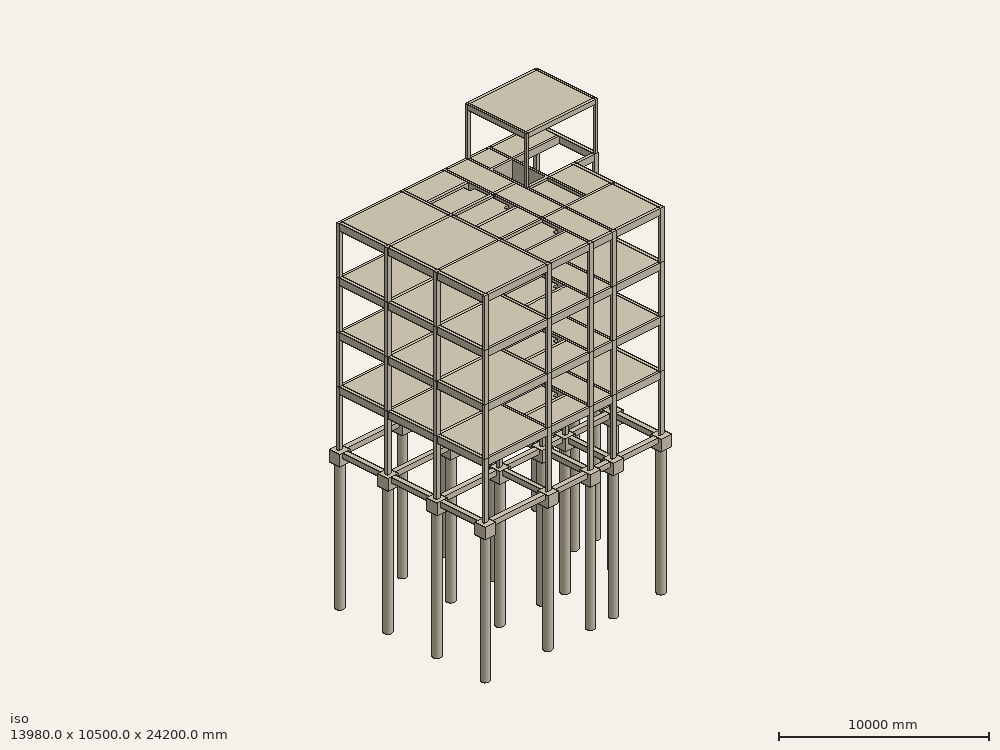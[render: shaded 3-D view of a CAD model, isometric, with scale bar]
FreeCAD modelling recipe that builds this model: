
FCSTD DOCUMENT  (FreeCAD 0.19R23074 (Git))
Label: 2021-01-14 Piloto estructural
License: All rights reserved
objects: Part::FeaturePython×395, Part::Part2DObjectPython×42, App::GeometryPython×29, TechDraw::DrawViewDimension×16, App::FeaturePython×11, App::DocumentObjectGroup×5, TechDraw::DrawSVGTemplate×5, TechDraw::DrawPage×5, TechDraw::DrawViewPart×4, TechDraw::DrawViewAnnotation×2, TechDraw::DrawViewSection×2, Spreadsheet::Sheet×1, App::MaterialObjectPython×1, App::DocumentObjectGroupPython×1, Sketcher::SketchObject×1, TechDraw::DrawViewArch×1
note: 470 computed .brp shape members not serialized (recipe doc carries the construction recipe); baked Part::Feature solids carry a one-line shape summary decoded from their .brp

FEATURE [Part::FeaturePython] Axis  label="Vertical"  # WARN: FeaturePython — macro-defined, semantics opaque (R4)
  Angles = [0,0,0,0,0,0,0]
  Distances = [1930,4230,2850,1550,1450,1770,1430]
  Length = 11000
  Placement = pos=(0,-500,0) rot=(0,0,1;0rad)
FEATURE [Part::FeaturePython] Axis002  label="Horizontal larga"  # WARN: FeaturePython — macro-defined, semantics opaque (R4)
  Angles = [0,0,0,0,0,0]
  Distances = [100,3250,2620,670,1730,1530]
  Length = 32000
  Placement = pos=(31000,1.077e-12,0) rot=(0,0,1;1.5708rad)
FEATURE [Part::Part2DObjectPython] Rectangle001  label="Lote"  # Draft 2D object (typed FeaturePython)
  Area = 0
  ChamferSize = 0
  Columns = 1
  FilletRadius = 0
  Height = 10000
  Length = 30000
  MakeFace = false
  Rows = 1
FEATURE [Part::Part2DObjectPython] Rectangle002  # Draft 2D object (typed FeaturePython)
  Area = 0
  ChamferSize = 0
  Columns = 1
  FilletRadius = 0
  Height = 700
  Length = 700
  MakeFace = false
  Placement = pos=(14860,9550,0) rot=(0,0,1;0rad)
  Rows = 1
  expr: Height = <<Estructura>>.CabAncho
  expr: Length = <<Estructura>>.CabAncho
FEATURE [Part::Part2DObjectPython] Circle  # Draft 2D object (typed FeaturePython)
  Area = 0
  FirstAngle = 0
  LastAngle = 0
  MakeFace = false
  Placement = pos=(15210,9900,0) rot=(0,0,1;0rad)
  Radius = 250
  expr: Radius = <<Estructura>>.PilRad
FEATURE [Part::FeaturePython] Beam001  # Arch/BIM 7 (typed FeaturePython)
  Chamfer = 0
  DentHeight = 0
  DentLength = 0
  Height = 300
  HorizontalArea = 1059000
  IfcData = attributes={"GlobalId": {"name": "GlobalId", "type": "IfcGloballyUniqueId", "is_enum": false, "enum_values": []}, "Description": {"... (+475 chars omitted),+1 more (map truncated)
  IfcType = 7
  Length = 3530
  MoveBase = false
  MoveWithHost = false
  PerimeterLength = 7660
  Placement = pos=(2280,6490,-800) rot=(0,0,1;0rad)
  PredefinedType = 0
  VerticalArea = 2298000
  Width = 300
FEATURE [Part::FeaturePython] Structure041  label="Beam002"  # Arch/BIM 7 (typed FeaturePython)
  FaceMaker = 0
  Height = 300
  HorizontalArea = 768000
  IfcData = attributes={"GlobalId": {"name": "GlobalId", "type": "IfcGloballyUniqueId", "is_enum": false, "enum_values": []}, "Description": {"... (+475 chars omitted),+1 more (map truncated)
  IfcType = 7
  Length = 2560
  MoveBase = false
  MoveWithHost = false
  Nodes = (2) [(1.2326e-31,-1.51582e-15,5.55112e-16),(2560,-1.51582e-15,5.55112e-16)]
  NodesOffset = 0
  Normal = (0,0,0)
  PerimeterLength = 5720
  Placement = pos=(1930,9550,-650) rot=(0,0,-1;1.5708rad)
  PredefinedType = 0
  VerticalArea = 1.716e+06
  Width = 300
  expr: Height = <<Estructura>>.VRAlto
  expr: Width = <<Estructura>>.VRAncho
FEATURE [Part::FeaturePython] Structure042  label="Beam003"  # Arch/BIM 7 (typed FeaturePython)
  FaceMaker = 0
  Height = 300
  HorizontalArea = 777000
  IfcData = attributes={"GlobalId": {"name": "GlobalId", "type": "IfcGloballyUniqueId", "is_enum": false, "enum_values": []}, "Description": {"... (+475 chars omitted),+1 more (map truncated)
  IfcType = 7
  Length = 2590
  MoveBase = false
  MoveWithHost = false
  Nodes = (2) [(1.2326e-31,-1.51582e-15,5.55112e-16),(2590,-1.51582e-15,5.55112e-16)]
  NodesOffset = 0
  Normal = (0,0,0)
  PerimeterLength = 5780
  Placement = pos=(1930,6290,-650) rot=(0,0,-1;1.5708rad)
  PredefinedType = 0
  VerticalArea = 1.734e+06
  Width = 300
FEATURE [Part::FeaturePython] Structure043  label="Beam004"  # Arch/BIM 7 (typed FeaturePython)
  FaceMaker = 0
  Height = 300
  HorizontalArea = 765000
  IfcData = attributes={"GlobalId": {"name": "GlobalId", "type": "IfcGloballyUniqueId", "is_enum": false, "enum_values": []}, "Description": {"... (+475 chars omitted),+1 more (map truncated)
  IfcType = 7
  Length = 2550
  MoveBase = false
  MoveWithHost = false
  Nodes = (2) [(1.2326e-31,-1.51582e-15,5.55112e-16),(2550,-1.51582e-15,5.55112e-16)]
  NodesOffset = 0
  Normal = (0,0,0)
  PerimeterLength = 5700
  Placement = pos=(1930,3000,-650) rot=(0,0,-1;1.5708rad)
  PredefinedType = 0
  VerticalArea = 1.71e+06
  Width = 300
FEATURE [Part::FeaturePython] Structure044  label="Beam005"  # Arch/BIM 7 (typed FeaturePython)
  FaceMaker = 0
  Height = 300
  HorizontalArea = 768000
  IfcData = attributes={"GlobalId": {"name": "GlobalId", "type": "IfcGloballyUniqueId", "is_enum": false, "enum_values": []}, "Description": {"... (+475 chars omitted),+1 more (map truncated)
  IfcType = 7
  Length = 2560
  MoveBase = false
  MoveWithHost = false
  Nodes = (2) [(1.2326e-31,-1.51582e-15,5.55112e-16),(2560,-1.51582e-15,5.55112e-16)]
  NodesOffset = 0
  Normal = (0,0,0)
  PerimeterLength = 5720
  Placement = pos=(6160.36,9550,-650) rot=(0,0,-1;1.5708rad)
  PredefinedType = 0
  VerticalArea = 1.716e+06
  Width = 300
FEATURE [Part::FeaturePython] Structure045  label="Beam006"  # Arch/BIM 7 (typed FeaturePython)
  FaceMaker = 0
  Height = 300
  HorizontalArea = 777000
  IfcData = attributes={"GlobalId": {"name": "GlobalId", "type": "IfcGloballyUniqueId", "is_enum": false, "enum_values": []}, "Description": {"... (+475 chars omitted),+1 more (map truncated)
  IfcType = 7
  Length = 2590
  MoveBase = false
  MoveWithHost = false
  Nodes = (2) [(1.2326e-31,-1.51582e-15,5.55112e-16),(2590,-1.51582e-15,5.55112e-16)]
  NodesOffset = 0
  Normal = (0,0,0)
  PerimeterLength = 5780
  Placement = pos=(6160.36,6290,-650) rot=(0,0,-1;1.5708rad)
  PredefinedType = 0
  VerticalArea = 1.734e+06
  Width = 300
FEATURE [Part::FeaturePython] Structure046  label="Beam007"  # Arch/BIM 7 (typed FeaturePython)
  FaceMaker = 0
  Height = 300
  HorizontalArea = 765000
  IfcData = attributes={"GlobalId": {"name": "GlobalId", "type": "IfcGloballyUniqueId", "is_enum": false, "enum_values": []}, "Description": {"... (+475 chars omitted),+1 more (map truncated)
  IfcType = 7
  Length = 2550
  MoveBase = false
  MoveWithHost = false
  Nodes = (2) [(1.2326e-31,-1.51582e-15,5.55112e-16),(2550,-1.51582e-15,5.55112e-16)]
  NodesOffset = 0
  Normal = (0,0,0)
  PerimeterLength = 5700
  Placement = pos=(6160.36,3000,-650) rot=(0,0,-1;1.5708rad)
  PredefinedType = 0
  VerticalArea = 1.71e+06
  Width = 300
FEATURE [Part::FeaturePython] Structure048  label="Beam009"  # Arch/BIM 7 (typed FeaturePython)
  FaceMaker = 0
  Height = 300
  HorizontalArea = 777000
  IfcData = attributes={"GlobalId": {"name": "GlobalId", "type": "IfcGloballyUniqueId", "is_enum": false, "enum_values": []}, "Description": {"... (+475 chars omitted),+1 more (map truncated)
  IfcType = 7
  Length = 2590
  MoveBase = false
  MoveWithHost = false
  Nodes = (2) [(1.2326e-31,-1.51582e-15,5.55112e-16),(2590,-1.51582e-15,5.55112e-16)]
  NodesOffset = 0
  Normal = (0,0,0)
  PerimeterLength = 5780
  Placement = pos=(9010.18,6290,-650) rot=(0,0,-1;1.5708rad)
  PredefinedType = 0
  VerticalArea = 1.734e+06
  Width = 300
FEATURE [Part::FeaturePython] Structure049  label="Beam010"  # Arch/BIM 7 (typed FeaturePython)
  FaceMaker = 0
  Height = 300
  HorizontalArea = 765000
  IfcData = attributes={"GlobalId": {"name": "GlobalId", "type": "IfcGloballyUniqueId", "is_enum": false, "enum_values": []}, "Description": {"... (+475 chars omitted),+1 more (map truncated)
  IfcType = 7
  Length = 2550
  MoveBase = false
  MoveWithHost = false
  Nodes = (2) [(1.2326e-31,-1.51582e-15,5.55112e-16),(2550,-1.51582e-15,5.55112e-16)]
  NodesOffset = 0
  Normal = (0,0,0)
  PerimeterLength = 5700
  Placement = pos=(9010.18,3000,-650) rot=(0,0,-1;1.5708rad)
  PredefinedType = 0
  VerticalArea = 1.71e+06
  Width = 300
FEATURE [Part::FeaturePython] Structure053  label="Beam014"  # Arch/BIM 7 (typed FeaturePython)
  FaceMaker = 0
  Height = 300
  HorizontalArea = 765000
  IfcData = attributes={"GlobalId": {"name": "GlobalId", "type": "IfcGloballyUniqueId", "is_enum": false, "enum_values": []}, "Description": {"... (+475 chars omitted),+1 more (map truncated)
  IfcType = 7
  Length = 2550
  MoveBase = false
  MoveWithHost = false
  Nodes = (2) [(1.2326e-31,-1.51582e-15,5.55112e-16),(2550,-1.51582e-15,5.55112e-16)]
  NodesOffset = 0
  Normal = (0,0,0)
  PerimeterLength = 5700
  Placement = pos=(13778.3,3000,-650) rot=(0,0,-1;1.5708rad)
  PredefinedType = 0
  VerticalArea = 1.71e+06
  Width = 300
FEATURE [Part::FeaturePython] Structure056  label="Beam017"  # Arch/BIM 7 (typed FeaturePython)
  FaceMaker = 0
  Height = 300
  HorizontalArea = 765000
  IfcData = attributes={"GlobalId": {"name": "GlobalId", "type": "IfcGloballyUniqueId", "is_enum": false, "enum_values": []}, "Description": {"... (+475 chars omitted),+1 more (map truncated)
  IfcType = 7
  Length = 2550
  MoveBase = false
  MoveWithHost = false
  Nodes = (2) [(1.2326e-31,-1.51582e-15,5.55112e-16),(2550,-1.51582e-15,5.55112e-16)]
  NodesOffset = 0
  Normal = (0,0,0)
  PerimeterLength = 5700
  Placement = pos=(10560,3000,-650) rot=(0,0,-1;1.5708rad)
  PredefinedType = 0
  VerticalArea = 1.71e+06
  Width = 300
FEATURE [Part::FeaturePython] Structure059  label="Beam020"  # Arch/BIM 7 (typed FeaturePython)
  FaceMaker = 0
  Height = 300
  HorizontalArea = 645000
  IfcData = attributes={"GlobalId": {"name": "GlobalId", "type": "IfcGloballyUniqueId", "is_enum": false, "enum_values": []}, "Description": {"... (+475 chars omitted),+1 more (map truncated)
  IfcType = 7
  Length = 2150
  MoveBase = false
  MoveWithHost = false
  Nodes = (2) [(1.2326e-31,-1.51582e-15,5.55112e-16),(2150,-1.51582e-15,5.55112e-16)]
  NodesOffset = 0
  Normal = (0,0,0)
  PerimeterLength = 4900
  Placement = pos=(6510,9900,-650) rot=(0,0,1;0rad)
  PredefinedType = 0
  VerticalArea = 1.47e+06
  Width = 300
FEATURE [Part::FeaturePython] Structure060  label="Beam021"  # Arch/BIM 7 (typed FeaturePython)
  FaceMaker = 0
  Height = 300
  HorizontalArea = 690000
  IfcData = attributes={"GlobalId": {"name": "GlobalId", "type": "IfcGloballyUniqueId", "is_enum": false, "enum_values": []}, "Description": {"... (+475 chars omitted),+1 more (map truncated)
  IfcType = 7
  Length = 2300
  MoveBase = false
  MoveWithHost = false
  Nodes = (2) [(1.2326e-31,-1.51582e-15,5.55112e-16),(2300,-1.51582e-15,5.55112e-16)]
  NodesOffset = 0
  Normal = (0,0,0)
  PerimeterLength = 5200
  Placement = pos=(9360,9900,-650) rot=(0,0,1;0rad)
  PredefinedType = 0
  VerticalArea = 1.56e+06
  Width = 300
FEATURE [Part::FeaturePython] Structure061  label="Beam022"  # Arch/BIM 7 (typed FeaturePython)
  FaceMaker = 0
  Height = 300
  HorizontalArea = 750000
  IfcData = attributes={"GlobalId": {"name": "GlobalId", "type": "IfcGloballyUniqueId", "is_enum": false, "enum_values": []}, "Description": {"... (+475 chars omitted),+1 more (map truncated)
  IfcType = 7
  Length = 2500
  MoveBase = false
  MoveWithHost = false
  Nodes = (2) [(1.2326e-31,-1.51582e-15,5.55112e-16),(2500,-1.51582e-15,5.55112e-16)]
  NodesOffset = 0
  Normal = (0,0,0)
  PerimeterLength = 5600
  Placement = pos=(12360,9900,-650) rot=(0,0,1;0rad)
  PredefinedType = 0
  VerticalArea = 1680000
  Width = 300
FEATURE [Part::FeaturePython] Structure064  label="Beam025"  # Arch/BIM 7 (typed FeaturePython)
  FaceMaker = 0
  Height = 300
  HorizontalArea = 645000
  IfcData = attributes={"GlobalId": {"name": "GlobalId", "type": "IfcGloballyUniqueId", "is_enum": false, "enum_values": []}, "Description": {"... (+475 chars omitted),+1 more (map truncated)
  IfcType = 7
  Length = 2150
  MoveBase = false
  MoveWithHost = false
  Nodes = (2) [(1.2326e-31,-1.51582e-15,5.55112e-16),(2150,-1.51582e-15,5.55112e-16)]
  NodesOffset = 0
  Normal = (0,0,0)
  PerimeterLength = 4900
  Placement = pos=(6510,6640,-650) rot=(0,0,1;0rad)
  PredefinedType = 0
  VerticalArea = 1.47e+06
  Width = 300
FEATURE [Part::FeaturePython] Structure065  label="Beam026"  # Arch/BIM 7 (typed FeaturePython)
  FaceMaker = 0
  Height = 300
  HorizontalArea = 768000
  IfcData = attributes={"GlobalId": {"name": "GlobalId", "type": "IfcGloballyUniqueId", "is_enum": false, "enum_values": []}, "Description": {"... (+475 chars omitted),+1 more (map truncated)
  IfcType = 7
  Length = 2560
  MoveBase = false
  MoveWithHost = false
  Nodes = (2) [(1.2326e-31,-1.51582e-15,5.55112e-16),(2560,-1.51582e-15,5.55112e-16)]
  NodesOffset = 0
  Normal = (0,0,0)
  PerimeterLength = 5720
  Placement = pos=(9010,6990,-650) rot=(0,0,1;1.5708rad)
  PredefinedType = 0
  VerticalArea = 1.716e+06
  Width = 300
FEATURE [Part::FeaturePython] Structure066  label="Beam027"  # Arch/BIM 7 (typed FeaturePython)
  FaceMaker = 0
  Height = 300
  HorizontalArea = 1.059e+06
  IfcData = attributes={"GlobalId": {"name": "GlobalId", "type": "IfcGloballyUniqueId", "is_enum": false, "enum_values": []}, "Description": {"... (+475 chars omitted),+1 more (map truncated)
  IfcType = 7
  Length = 3530
  MoveBase = false
  MoveWithHost = false
  Nodes = (2) [(1.2326e-31,-1.51582e-15,5.55112e-16),(3530,-1.51582e-15,5.55112e-16)]
  NodesOffset = 0
  Normal = (0,0,0)
  PerimeterLength = 7660
  Placement = pos=(2280,3350,-650) rot=(0,0,1;0rad)
  PredefinedType = 0
  VerticalArea = 2.298e+06
  Width = 300
FEATURE [Part::FeaturePython] Structure067  label="Beam028"  # Arch/BIM 7 (typed FeaturePython)
  FaceMaker = 0
  Height = 300
  HorizontalArea = 645000
  IfcData = attributes={"GlobalId": {"name": "GlobalId", "type": "IfcGloballyUniqueId", "is_enum": false, "enum_values": []}, "Description": {"... (+475 chars omitted),+1 more (map truncated)
  IfcType = 7
  Length = 2150
  MoveBase = false
  MoveWithHost = false
  Nodes = (2) [(1.2326e-31,-1.51582e-15,5.55112e-16),(2150,-1.51582e-15,5.55112e-16)]
  NodesOffset = 0
  Normal = (0,0,0)
  PerimeterLength = 4900
  Placement = pos=(6510,3350,-650) rot=(0,0,1;0rad)
  PredefinedType = 0
  VerticalArea = 1.47e+06
  Width = 300
FEATURE [Part::FeaturePython] Structure068  label="Beam029"  # Arch/BIM 7 (typed FeaturePython)
  FaceMaker = 0
  Height = 300
  HorizontalArea = 1.059e+06
  IfcData = attributes={"GlobalId": {"name": "GlobalId", "type": "IfcGloballyUniqueId", "is_enum": false, "enum_values": []}, "Description": {"... (+475 chars omitted),+1 more (map truncated)
  IfcType = 7
  Length = 3530
  MoveBase = false
  MoveWithHost = false
  Nodes = (2) [(1.2326e-31,-1.51582e-15,5.55112e-16),(3530,-1.51582e-15,5.55112e-16)]
  NodesOffset = 0
  Normal = (0,0,0)
  PerimeterLength = 7660
  Placement = pos=(2280,100,-650) rot=(0,0,1;0rad)
  PredefinedType = 0
  VerticalArea = 2.298e+06
  Width = 300
FEATURE [Part::FeaturePython] Structure069  label="Beam030"  # Arch/BIM 7 (typed FeaturePython)
  FaceMaker = 0
  Height = 300
  HorizontalArea = 645000
  IfcData = attributes={"GlobalId": {"name": "GlobalId", "type": "IfcGloballyUniqueId", "is_enum": false, "enum_values": []}, "Description": {"... (+475 chars omitted),+1 more (map truncated)
  IfcType = 7
  Length = 2150
  MoveBase = false
  MoveWithHost = false
  Nodes = (2) [(1.2326e-31,-1.51582e-15,5.55112e-16),(2150,-1.51582e-15,5.55112e-16)]
  NodesOffset = 0
  Normal = (0,0,0)
  PerimeterLength = 4900
  Placement = pos=(6510,100,-650) rot=(0,0,1;0rad)
  PredefinedType = 0
  VerticalArea = 1.47e+06
  Width = 300
FEATURE [Part::FeaturePython] Structure070  label="Beam031"  # Arch/BIM 7 (typed FeaturePython)
  FaceMaker = 0
  Height = 300
  HorizontalArea = 255000
  IfcData = attributes={"GlobalId": {"name": "GlobalId", "type": "IfcGloballyUniqueId", "is_enum": false, "enum_values": []}, "Description": {"... (+475 chars omitted),+1 more (map truncated)
  IfcType = 7
  Length = 850
  MoveBase = false
  MoveWithHost = false
  Nodes = (2) [(1.2326e-31,-1.51582e-15,5.55112e-16),(850,-1.51582e-15,5.55112e-16)]
  NodesOffset = 0
  Normal = (0,0,0)
  PerimeterLength = 2300
  Placement = pos=(9360,100,-650) rot=(0,0,1;0rad)
  PredefinedType = 0
  VerticalArea = 690000
  Width = 300
FEATURE [Part::FeaturePython] Structure071  label="Beam032"  # Arch/BIM 7 (typed FeaturePython)
  FaceMaker = 0
  Height = 300
  HorizontalArea = 756000
  IfcData = attributes={"GlobalId": {"name": "GlobalId", "type": "IfcGloballyUniqueId", "is_enum": false, "enum_values": []}, "Description": {"... (+475 chars omitted),+1 more (map truncated)
  IfcType = 7
  Length = 2520
  MoveBase = false
  MoveWithHost = false
  Nodes = (2) [(1.2326e-31,-1.51582e-15,5.55112e-16),(2520,-1.51582e-15,5.55112e-16)]
  NodesOffset = 0
  Normal = (0,0,0)
  PerimeterLength = 5640
  Placement = pos=(10910,100,-650) rot=(0,0,1;0rad)
  PredefinedType = 0
  VerticalArea = 1.692e+06
  Width = 300
FEATURE [Part::FeaturePython] Structure072  label="Beam033"  # Arch/BIM 7 (typed FeaturePython)
  FaceMaker = 0
  Height = 300
  HorizontalArea = 255000
  IfcData = attributes={"GlobalId": {"name": "GlobalId", "type": "IfcGloballyUniqueId", "is_enum": false, "enum_values": []}, "Description": {"... (+475 chars omitted),+1 more (map truncated)
  IfcType = 7
  Length = 850
  MoveBase = false
  MoveWithHost = false
  Nodes = (2) [(1.2326e-31,-1.51582e-15,5.55112e-16),(850,-1.51582e-15,5.55112e-16)]
  NodesOffset = 0
  Normal = (0,0,0)
  PerimeterLength = 2300
  Placement = pos=(9360,3350,-650) rot=(0,0,1;0rad)
  PredefinedType = 0
  VerticalArea = 690000
  Width = 300
FEATURE [Part::FeaturePython] Structure073  label="Beam034"  # Arch/BIM 7 (typed FeaturePython)
  FaceMaker = 0
  Height = 300
  HorizontalArea = 756000
  IfcData = attributes={"GlobalId": {"name": "GlobalId", "type": "IfcGloballyUniqueId", "is_enum": false, "enum_values": []}, "Description": {"... (+475 chars omitted),+1 more (map truncated)
  IfcType = 7
  Length = 2520
  MoveBase = false
  MoveWithHost = false
  Nodes = (2) [(1.2326e-31,-1.51582e-15,5.55112e-16),(2520,-1.51582e-15,5.55112e-16)]
  NodesOffset = 0
  Normal = (0,0,0)
  PerimeterLength = 5640
  Placement = pos=(10910,3350,-650) rot=(0,0,1;0rad)
  PredefinedType = 0
  VerticalArea = 1.692e+06
  Width = 300
FEATURE [Part::FeaturePython] Structure074  label="Beam035"  # Arch/BIM 7 (typed FeaturePython)
  FaceMaker = 0
  Height = 300
  HorizontalArea = 969000
  IfcData = attributes={"GlobalId": {"name": "GlobalId", "type": "IfcGloballyUniqueId", "is_enum": false, "enum_values": []}, "Description": {"... (+475 chars omitted),+1 more (map truncated)
  IfcType = 7
  Length = 3230
  MoveBase = false
  MoveWithHost = false
  Nodes = (2) [(1.2326e-31,-1.51582e-15,5.55112e-16),(3230,-1.51582e-15,5.55112e-16)]
  NodesOffset = 0
  Normal = (0,0,0)
  PerimeterLength = 7060
  Placement = pos=(15210,9550,-650) rot=(0,0,-1;1.5708rad)
  PredefinedType = 0
  VerticalArea = 2.118e+06
  Width = 300
FEATURE [Part::FeaturePython] Structure075  label="Beam036"  # Arch/BIM 7 (typed FeaturePython)
  FaceMaker = 0
  Height = 300
  HorizontalArea = 576000
  IfcData = attributes={"GlobalId": {"name": "GlobalId", "type": "IfcGloballyUniqueId", "is_enum": false, "enum_values": []}, "Description": {"... (+475 chars omitted),+1 more (map truncated)
  IfcType = 7
  Length = 1920
  MoveBase = false
  MoveWithHost = false
  Nodes = (2) [(1.2326e-31,-1.51582e-15,5.55112e-16),(1920,-1.51582e-15,5.55112e-16)]
  NodesOffset = 0
  Normal = (0,0,0)
  PerimeterLength = 4440
  Placement = pos=(13780,3700,-650) rot=(0,0,1;1.5708rad)
  PredefinedType = 0
  VerticalArea = 1.332e+06
  Width = 300
FEATURE [Part::FeaturePython] Structure076  label="Beam037"  # Arch/BIM 7 (typed FeaturePython)
  FaceMaker = 0
  Height = 300
  HorizontalArea = 219000
  IfcData = attributes={"GlobalId": {"name": "GlobalId", "type": "IfcGloballyUniqueId", "is_enum": false, "enum_values": []}, "Description": {"... (+475 chars omitted),+1 more (map truncated)
  IfcType = 7
  Length = 730
  MoveBase = false
  MoveWithHost = false
  Nodes = (2) [(1.2326e-31,-1.51582e-15,5.55112e-16),(730,-1.51582e-15,5.55112e-16)]
  NodesOffset = 0
  Normal = (0,0,0)
  PerimeterLength = 2060
  Placement = pos=(14130,5970,-650) rot=(0,0,1;0rad)
  PredefinedType = 0
  VerticalArea = 618000
  Width = 300
FEATURE [Part::FeaturePython] Structure077  label="Beam038"  # Arch/BIM 7 (typed FeaturePython)
  FaceMaker = 0
  Height = 300
  HorizontalArea = 681000
  IfcData = attributes={"GlobalId": {"name": "GlobalId", "type": "IfcGloballyUniqueId", "is_enum": false, "enum_values": []}, "Description": {"... (+475 chars omitted),+1 more (map truncated)
  IfcType = 7
  Length = 2270
  MoveBase = false
  MoveWithHost = false
  Nodes = (2) [(1.2326e-31,-1.51582e-15,5.55112e-16),(2270,-1.51582e-15,5.55112e-16)]
  NodesOffset = 0
  Normal = (0,0,0)
  PerimeterLength = 5140
  Placement = pos=(10560,3700,-650) rot=(0,0,1;1.5708rad)
  PredefinedType = 0
  VerticalArea = 1.542e+06
  Width = 300
FEATURE [Part::FeaturePython] Structure078  label="Beam039"  # Arch/BIM 7 (typed FeaturePython)
  FaceMaker = 0
  Height = 300
  HorizontalArea = 414000
  IfcData = attributes={"GlobalId": {"name": "GlobalId", "type": "IfcGloballyUniqueId", "is_enum": false, "enum_values": []}, "Description": {"... (+475 chars omitted),+1 more (map truncated)
  IfcType = 7
  Length = 1380
  MoveBase = false
  MoveWithHost = false
  Nodes = (2) [(1.2326e-31,-1.51582e-15,5.55112e-16),(1380,-1.51582e-15,5.55112e-16)]
  NodesOffset = 0
  Normal = (0,0,0)
  PerimeterLength = 3360
  Placement = pos=(10560,9750,-650) rot=(0,0,-1;1.5708rad)
  PredefinedType = 0
  VerticalArea = 1.008e+06
  Width = 300
FEATURE [Part::FeaturePython] Structure079  label="Beam040"  # Arch/BIM 7 (typed FeaturePython)
  FaceMaker = 0
  Height = 300
  HorizontalArea = 354000
  IfcData = attributes={"GlobalId": {"name": "GlobalId", "type": "IfcGloballyUniqueId", "is_enum": false, "enum_values": []}, "Description": {"... (+475 chars omitted),+1 more (map truncated)
  IfcType = 7
  Length = 1180
  MoveBase = false
  MoveWithHost = false
  Nodes = (2) [(1.2326e-31,-1.51582e-15,5.55112e-16),(1180,-1.51582e-15,5.55112e-16)]
  NodesOffset = 0
  Normal = (0,0,0)
  PerimeterLength = 2960
  Placement = pos=(12010,9550,-650) rot=(0,0,-1;1.5708rad)
  PredefinedType = 0
  VerticalArea = 888000
  Width = 300
FEATURE [Part::FeaturePython] Structure080  label="Beam041"  # Arch/BIM 7 (typed FeaturePython)
  FaceMaker = 0
  Height = 300
  HorizontalArea = 426000
  IfcData = attributes={"GlobalId": {"name": "GlobalId", "type": "IfcGloballyUniqueId", "is_enum": false, "enum_values": []}, "Description": {"... (+475 chars omitted),+1 more (map truncated)
  IfcType = 7
  Length = 1420
  MoveBase = false
  MoveWithHost = false
  Nodes = (2) [(1.2326e-31,-1.51582e-15,5.55112e-16),(1420,-1.51582e-15,5.55112e-16)]
  NodesOffset = 0
  Normal = (0,0,0)
  PerimeterLength = 3440
  Placement = pos=(13430,5970,-650) rot=(0,0,1;3.14159rad)
  PredefinedType = 0
  VerticalArea = 1.032e+06
  Width = 300
FEATURE [Part::Part2DObjectPython] Rectangle  # Draft 2D object (typed FeaturePython)
  Area = 0
  ChamferSize = 0
  Columns = 1
  FilletRadius = 0
  Height = 2550
  Length = 1600
  MakeFace = false
  Placement = pos=(10485,5895,0) rot=(0,0,1;0rad)
  Rows = 1
FEATURE [Spreadsheet::Sheet] Spreadsheet  label="Estructura"
  cells = A1=MODELO ESTRUCTURAL; A2=Descripcion; B2=Alias; C2=Valor; D2=Unidad; A3=Cabezal Ancho; B3=CabAncho; C3(CabAncho)=700; D3=mm; A4=Cabezal Espesor; B4=CabEsp; C4(CabEsp)=700; D4=mm; A5=Pilote Radio; B5=PilRad; C5(PilRad)=250; D5=mm; A6=Pilote Profundidad; B6=PilProf; C6(PilProf)=8000; D6=mm; A7=Viga Riostra Ancho; B7=VRAncho; C7(VRAncho)=300; D7=mm; A8=Viga Riostra Alto; B8=VRAlto; C8(VRAlto)=300; D8=mm
FEATURE [Part::FeaturePython] Beam  # Arch/BIM 7 (typed FeaturePython)
  Chamfer = 0
  DentHeight = 0
  DentLength = 0
  Height = 300
  HorizontalArea = 1059000
  IfcData = attributes={"GlobalId": {"name": "GlobalId", "type": "IfcGloballyUniqueId", "is_enum": false, "enum_values": []}, "Description": {"... (+475 chars omitted),+1 more (map truncated)
  IfcType = 7
  Length = 3530
  MoveBase = false
  MoveWithHost = false
  PerimeterLength = 7660
  Placement = pos=(2280,9750,-800) rot=(0,0,1;0rad)
  PredefinedType = 0
  VerticalArea = 2298000
  Width = 300
FEATURE [Part::Part2DObjectPython] Rectangle003  # Draft 2D object (typed FeaturePython)
  Area = 0
  ChamferSize = 0
  Columns = 1
  FilletRadius = 0
  Height = 2550
  Length = 1600
  MakeFace = false
  Placement = pos=(10485,5895,0) rot=(0,0,1;0rad)
  Rows = 1
FEATURE [Part::FeaturePython] Structure142  label="V15x40 V133"  # Arch/BIM 7 (typed FeaturePython)
  FaceMaker = 0
  Height = 400
  HorizontalArea = 597000
  IfcData = attributes={"GlobalId": {"name": "GlobalId", "type": "IfcGloballyUniqueId", "is_enum": false, "enum_values": []}, "Description": {"... (+475 chars omitted),+1 more (map truncated)
  IfcType = 7
  Length = 3980
  MoveBase = false
  MoveWithHost = false
  Nodes = (2) [(-1.72563e-31,-1.42109e-15,-7.77156e-16),(3980,-1.42109e-15,-7.77156e-16)]
  NodesOffset = 0
  Normal = (0,0,0)
  PerimeterLength = 8260
  Placement = pos=(2055,9900,5800) rot=(0,0,1;0rad)
  PredefinedType = 0
  VerticalArea = 3.304e+06
  Width = 150
FEATURE [Part::FeaturePython] Structure143  label="V15x40 V134"  # Arch/BIM 7 (typed FeaturePython)
  FaceMaker = 0
  Height = 400
  HorizontalArea = 390000
  IfcData = attributes={"GlobalId": {"name": "GlobalId", "type": "IfcGloballyUniqueId", "is_enum": false, "enum_values": []}, "Description": {"... (+475 chars omitted),+1 more (map truncated)
  IfcType = 7
  Length = 2600
  MoveBase = false
  MoveWithHost = false
  Nodes = (2) [(-1.72563e-31,-1.42109e-15,-7.77156e-16),(2600,-1.42109e-15,-7.77156e-16)]
  NodesOffset = 0
  Normal = (0,0,0)
  PerimeterLength = 5500
  Placement = pos=(6285,9900,5800) rot=(0,0,1;0rad)
  PredefinedType = 0
  VerticalArea = 2200000
  Width = 150
FEATURE [Part::FeaturePython] Structure144  label="V15x40 V135"  # Arch/BIM 7 (typed FeaturePython)
  FaceMaker = 0
  Height = 400
  HorizontalArea = 412500
  IfcData = attributes={"GlobalId": {"name": "GlobalId", "type": "IfcGloballyUniqueId", "is_enum": false, "enum_values": []}, "Description": {"... (+475 chars omitted),+1 more (map truncated)
  IfcType = 7
  Length = 2750
  MoveBase = false
  MoveWithHost = false
  Nodes = (2) [(-1.72563e-31,-1.42109e-15,-7.77156e-16),(2750,-1.42109e-15,-7.77156e-16)]
  NodesOffset = 0
  Normal = (0,0,0)
  PerimeterLength = 5800
  Placement = pos=(9135,9900,5800) rot=(0,0,1;0rad)
  PredefinedType = 0
  VerticalArea = 2320000
  Width = 150
FEATURE [Part::FeaturePython] Structure145  label="V15x40 V136"  # Arch/BIM 7 (typed FeaturePython)
  FaceMaker = 0
  Height = 400
  HorizontalArea = 442500
  IfcData = attributes={"GlobalId": {"name": "GlobalId", "type": "IfcGloballyUniqueId", "is_enum": false, "enum_values": []}, "Description": {"... (+475 chars omitted),+1 more (map truncated)
  IfcType = 7
  Length = 2950
  MoveBase = false
  MoveWithHost = false
  Nodes = (2) [(-1.72563e-31,-1.42109e-15,-7.77156e-16),(2950,-1.42109e-15,-7.77156e-16)]
  NodesOffset = 0
  Normal = (0,0,0)
  PerimeterLength = 6200
  Placement = pos=(12135,9900,5800) rot=(0,0,1;0rad)
  PredefinedType = 0
  VerticalArea = 2.48e+06
  Width = 150
FEATURE [Part::FeaturePython] Structure146  label="V15x40 V137"  # Arch/BIM 7 (typed FeaturePython)
  FaceMaker = 0
  Height = 400
  HorizontalArea = 453750
  IfcData = attributes={"GlobalId": {"name": "GlobalId", "type": "IfcGloballyUniqueId", "is_enum": false, "enum_values": []}, "Description": {"... (+475 chars omitted),+1 more (map truncated)
  IfcType = 7
  Length = 3025
  MoveBase = false
  MoveWithHost = false
  Nodes = (2) [(-1.72563e-31,-1.42109e-15,-7.77156e-16),(3025,-1.42109e-15,-7.77156e-16)]
  NodesOffset = 0
  Normal = (0,0,0)
  PerimeterLength = 6350
  Placement = pos=(12085,8370,5800) rot=(0,0,1;0rad)
  PredefinedType = 0
  VerticalArea = 2.54e+06
  Width = 150
FEATURE [Part::FeaturePython] Structure147  label="V15x40 V138"  # Arch/BIM 7 (typed FeaturePython)
  FaceMaker = 0
  Height = 400
  HorizontalArea = 597000
  IfcData = attributes={"GlobalId": {"name": "GlobalId", "type": "IfcGloballyUniqueId", "is_enum": false, "enum_values": []}, "Description": {"... (+475 chars omitted),+1 more (map truncated)
  IfcType = 7
  Length = 3980
  MoveBase = false
  MoveWithHost = false
  Nodes = (2) [(-1.72563e-31,-1.42109e-15,-7.77156e-16),(3980,-1.42109e-15,-7.77156e-16)]
  NodesOffset = 0
  Normal = (0,0,0)
  PerimeterLength = 8260
  Placement = pos=(2055,6640,5800) rot=(0,0,1;0rad)
  PredefinedType = 0
  VerticalArea = 3.304e+06
  Width = 150
FEATURE [Part::FeaturePython] Structure148  label="V15x40 V139"  # Arch/BIM 7 (typed FeaturePython)
  FaceMaker = 0
  Height = 400
  HorizontalArea = 397500
  IfcData = attributes={"GlobalId": {"name": "GlobalId", "type": "IfcGloballyUniqueId", "is_enum": false, "enum_values": []}, "Description": {"... (+475 chars omitted),+1 more (map truncated)
  IfcType = 7
  Length = 2650
  MoveBase = false
  MoveWithHost = false
  Nodes = (2) [(-1.72563e-31,-1.42109e-15,-7.77156e-16),(2650,-1.42109e-15,-7.77156e-16)]
  NodesOffset = 0
  Normal = (0,0,0)
  PerimeterLength = 5600
  Placement = pos=(6285,6640,5800) rot=(0,0,1;0rad)
  PredefinedType = 0
  VerticalArea = 2240000
  Width = 150
FEATURE [Part::FeaturePython] Structure149  label="V15x40 V140"  # Arch/BIM 7 (typed FeaturePython)
  FaceMaker = 0
  Height = 400
  HorizontalArea = 210000
  IfcData = attributes={"GlobalId": {"name": "GlobalId", "type": "IfcGloballyUniqueId", "is_enum": false, "enum_values": []}, "Description": {"... (+475 chars omitted),+1 more (map truncated)
  IfcType = 7
  Length = 1400
  MoveBase = false
  MoveWithHost = false
  Nodes = (2) [(-1.72563e-31,-1.42109e-15,-7.77156e-16),(1400,-1.42109e-15,-7.77156e-16)]
  NodesOffset = 0
  Normal = (0,0,0)
  PerimeterLength = 3100
  Placement = pos=(9085,6640,5800) rot=(0,0,1;0rad)
  PredefinedType = 0
  VerticalArea = 1240000
  Width = 150
FEATURE [Part::FeaturePython] Structure150  label="V15x40 V141"  # Arch/BIM 7 (typed FeaturePython)
  FaceMaker = 0
  Height = 400
  HorizontalArea = 235500
  IfcData = attributes={"GlobalId": {"name": "GlobalId", "type": "IfcGloballyUniqueId", "is_enum": false, "enum_values": []}, "Description": {"... (+475 chars omitted),+1 more (map truncated)
  IfcType = 7
  Length = 1570
  MoveBase = false
  MoveWithHost = false
  Nodes = (2) [(-1.72563e-31,-1.42109e-15,-7.77156e-16),(1570,-1.42109e-15,-7.77156e-16)]
  NodesOffset = 0
  Normal = (0,0,0)
  PerimeterLength = 3440
  Placement = pos=(13655,5970,5800) rot=(0,0,1;3.14159rad)
  PredefinedType = 0
  VerticalArea = 1.376e+06
  Width = 150
FEATURE [Part::FeaturePython] Structure151  label="V15x40 V142"  # Arch/BIM 7 (typed FeaturePython)
  FaceMaker = 0
  Height = 400
  HorizontalArea = 177000
  IfcData = attributes={"GlobalId": {"name": "GlobalId", "type": "IfcGloballyUniqueId", "is_enum": false, "enum_values": []}, "Description": {"... (+475 chars omitted),+1 more (map truncated)
  IfcType = 7
  Length = 1180
  MoveBase = false
  MoveWithHost = false
  Nodes = (2) [(-1.72563e-31,-1.42109e-15,-7.77156e-16),(1180,-1.42109e-15,-7.77156e-16)]
  NodesOffset = 0
  Normal = (0,0,0)
  PerimeterLength = 2660
  Placement = pos=(13905,5970,5800) rot=(0,0,1;0rad)
  PredefinedType = 0
  VerticalArea = 1064000
  Width = 150
FEATURE [Part::FeaturePython] Structure152  label="V15x40 V143"  # Arch/BIM 7 (typed FeaturePython)
  FaceMaker = 0
  Height = 400
  HorizontalArea = 597000
  IfcData = attributes={"GlobalId": {"name": "GlobalId", "type": "IfcGloballyUniqueId", "is_enum": false, "enum_values": []}, "Description": {"... (+475 chars omitted),+1 more (map truncated)
  IfcType = 7
  Length = 3980
  MoveBase = false
  MoveWithHost = false
  Nodes = (2) [(-1.72563e-31,-1.42109e-15,-7.77156e-16),(3980,-1.42109e-15,-7.77156e-16)]
  NodesOffset = 0
  Normal = (0,0,0)
  PerimeterLength = 8260
  Placement = pos=(2055,3350,5800) rot=(0,0,1;0rad)
  PredefinedType = 0
  VerticalArea = 3.304e+06
  Width = 150
FEATURE [Part::FeaturePython] Structure153  label="V15x40 V144"  # Arch/BIM 7 (typed FeaturePython)
  FaceMaker = 0
  Height = 400
  HorizontalArea = 397500
  IfcData = attributes={"GlobalId": {"name": "GlobalId", "type": "IfcGloballyUniqueId", "is_enum": false, "enum_values": []}, "Description": {"... (+475 chars omitted),+1 more (map truncated)
  IfcType = 7
  Length = 2650
  MoveBase = false
  MoveWithHost = false
  Nodes = (2) [(-1.72563e-31,-1.42109e-15,-7.77156e-16),(2650,-1.42109e-15,-7.77156e-16)]
  NodesOffset = 0
  Normal = (0,0,0)
  PerimeterLength = 5600
  Placement = pos=(6285,3350,5800) rot=(0,0,1;0rad)
  PredefinedType = 0
  VerticalArea = 2240000
  Width = 150
FEATURE [Part::FeaturePython] Structure154  label="V15x40 V145"  # Arch/BIM 7 (typed FeaturePython)
  FaceMaker = 0
  Height = 400
  HorizontalArea = 210000
  IfcData = attributes={"GlobalId": {"name": "GlobalId", "type": "IfcGloballyUniqueId", "is_enum": false, "enum_values": []}, "Description": {"... (+475 chars omitted),+1 more (map truncated)
  IfcType = 7
  Length = 1400
  MoveBase = false
  MoveWithHost = false
  Nodes = (2) [(-1.72563e-31,-1.42109e-15,-7.77156e-16),(1400,-1.42109e-15,-7.77156e-16)]
  NodesOffset = 0
  Normal = (0,0,0)
  PerimeterLength = 3100
  Placement = pos=(9085,3350,5800) rot=(0,0,1;0rad)
  PredefinedType = 0
  VerticalArea = 1240000
  Width = 150
FEATURE [Part::FeaturePython] Structure155  label="V15x40 V146"  # Arch/BIM 7 (typed FeaturePython)
  FaceMaker = 0
  Height = 400
  HorizontalArea = 460500
  IfcData = attributes={"GlobalId": {"name": "GlobalId", "type": "IfcGloballyUniqueId", "is_enum": false, "enum_values": []}, "Description": {"... (+475 chars omitted),+1 more (map truncated)
  IfcType = 7
  Length = 3070
  MoveBase = false
  MoveWithHost = false
  Nodes = (2) [(-1.72563e-31,-1.42109e-15,-7.77156e-16),(3070,-1.42109e-15,-7.77156e-16)]
  NodesOffset = 0
  Normal = (0,0,0)
  PerimeterLength = 6440
  Placement = pos=(10635,3350,5800) rot=(0,0,1;0rad)
  PredefinedType = 0
  VerticalArea = 2.576e+06
  Width = 150
FEATURE [Part::FeaturePython] Structure156  label="V15x40 V147"  # Arch/BIM 7 (typed FeaturePython)
  FaceMaker = 0
  Height = 400
  HorizontalArea = 597000
  IfcData = attributes={"GlobalId": {"name": "GlobalId", "type": "IfcGloballyUniqueId", "is_enum": false, "enum_values": []}, "Description": {"... (+475 chars omitted),+1 more (map truncated)
  IfcType = 7
  Length = 3980
  MoveBase = false
  MoveWithHost = false
  Nodes = (2) [(-1.72563e-31,-1.42109e-15,-7.77156e-16),(3980,-1.42109e-15,-7.77156e-16)]
  NodesOffset = 0
  Normal = (0,0,0)
  PerimeterLength = 8260
  Placement = pos=(2055,100,5800) rot=(0,0,1;0rad)
  PredefinedType = 0
  VerticalArea = 3.304e+06
  Width = 150
FEATURE [Part::FeaturePython] Structure157  label="V15x40 V148"  # Arch/BIM 7 (typed FeaturePython)
  FaceMaker = 0
  Height = 400
  HorizontalArea = 390000
  IfcData = attributes={"GlobalId": {"name": "GlobalId", "type": "IfcGloballyUniqueId", "is_enum": false, "enum_values": []}, "Description": {"... (+475 chars omitted),+1 more (map truncated)
  IfcType = 7
  Length = 2600
  MoveBase = false
  MoveWithHost = false
  Nodes = (2) [(-1.72563e-31,-1.42109e-15,-7.77156e-16),(2600,-1.42109e-15,-7.77156e-16)]
  NodesOffset = 0
  Normal = (0,0,0)
  PerimeterLength = 5500
  Placement = pos=(6285,100,5800) rot=(0,0,1;0rad)
  PredefinedType = 0
  VerticalArea = 2200000
  Width = 150
FEATURE [Part::FeaturePython] Structure158  label="V15x40 V149"  # Arch/BIM 7 (typed FeaturePython)
  FaceMaker = 0
  Height = 400
  HorizontalArea = 195000
  IfcData = attributes={"GlobalId": {"name": "GlobalId", "type": "IfcGloballyUniqueId", "is_enum": false, "enum_values": []}, "Description": {"... (+475 chars omitted),+1 more (map truncated)
  IfcType = 7
  Length = 1300
  MoveBase = false
  MoveWithHost = false
  Nodes = (2) [(-1.72563e-31,-1.42109e-15,-7.77156e-16),(1300,-1.42109e-15,-7.77156e-16)]
  NodesOffset = 0
  Normal = (0,0,0)
  PerimeterLength = 2900
  Placement = pos=(9135,100,5800) rot=(0,0,1;0rad)
  PredefinedType = 0
  VerticalArea = 1160000
  Width = 150
FEATURE [Part::FeaturePython] Structure159  label="V15x40 V150"  # Arch/BIM 7 (typed FeaturePython)
  FaceMaker = 0
  Height = 400
  HorizontalArea = 445500
  IfcData = attributes={"GlobalId": {"name": "GlobalId", "type": "IfcGloballyUniqueId", "is_enum": false, "enum_values": []}, "Description": {"... (+475 chars omitted),+1 more (map truncated)
  IfcType = 7
  Length = 2970
  MoveBase = false
  MoveWithHost = false
  Nodes = (2) [(-1.72563e-31,-1.42109e-15,-7.77156e-16),(2970,-1.42109e-15,-7.77156e-16)]
  NodesOffset = 0
  Normal = (0,0,0)
  PerimeterLength = 6240
  Placement = pos=(10685,100,5800) rot=(0,0,1;0rad)
  PredefinedType = 0
  VerticalArea = 2.496e+06
  Width = 150
FEATURE [Part::FeaturePython] Structure160  label="V15x40 V151"  # Arch/BIM 7 (typed FeaturePython)
  FaceMaker = 0
  Height = 400
  HorizontalArea = 465000
  IfcData = attributes={"GlobalId": {"name": "GlobalId", "type": "IfcGloballyUniqueId", "is_enum": false, "enum_values": []}, "Description": {"... (+475 chars omitted),+1 more (map truncated)
  IfcType = 7
  Length = 3100
  MoveBase = false
  MoveWithHost = false
  Nodes = (2) [(-1.72563e-31,-1.42109e-15,-7.77156e-16),(3100,-1.42109e-15,-7.77156e-16)]
  NodesOffset = 0
  Normal = (0,0,0)
  PerimeterLength = 6500
  Placement = pos=(6160,3275,5800) rot=(0,0,-1;1.5708rad)
  PredefinedType = 0
  VerticalArea = 2.6e+06
  Width = 150
FEATURE [Part::FeaturePython] Structure161  label="V15x40 V152"  # Arch/BIM 7 (typed FeaturePython)
  FaceMaker = 0
  Height = 400
  HorizontalArea = 471000
  IfcData = attributes={"GlobalId": {"name": "GlobalId", "type": "IfcGloballyUniqueId", "is_enum": false, "enum_values": []}, "Description": {"... (+475 chars omitted),+1 more (map truncated)
  IfcType = 7
  Length = 3140
  MoveBase = false
  MoveWithHost = false
  Nodes = (2) [(-1.72563e-31,-1.42109e-15,-7.77156e-16),(3140,-1.42109e-15,-7.77156e-16)]
  NodesOffset = 0
  Normal = (0,0,0)
  PerimeterLength = 6580
  Placement = pos=(6160,6565,5800) rot=(0,0,-1;1.5708rad)
  PredefinedType = 0
  VerticalArea = 2.632e+06
  Width = 150
FEATURE [Part::FeaturePython] Structure162  label="V15x40 V153"  # Arch/BIM 7 (typed FeaturePython)
  FaceMaker = 0
  Height = 400
  HorizontalArea = 466500
  IfcData = attributes={"GlobalId": {"name": "GlobalId", "type": "IfcGloballyUniqueId", "is_enum": false, "enum_values": []}, "Description": {"... (+475 chars omitted),+1 more (map truncated)
  IfcType = 7
  Length = 3110
  MoveBase = false
  MoveWithHost = false
  Nodes = (2) [(-1.72563e-31,-1.42109e-15,-7.77156e-16),(3110,-1.42109e-15,-7.77156e-16)]
  NodesOffset = 0
  Normal = (0,0,0)
  PerimeterLength = 6520
  Placement = pos=(6160,9825,5800) rot=(0,0,-1;1.5708rad)
  PredefinedType = 0
  VerticalArea = 2.608e+06
  Width = 150
FEATURE [Part::FeaturePython] Structure163  label="V15x40 V154"  # Arch/BIM 7 (typed FeaturePython)
  FaceMaker = 0
  Height = 400
  HorizontalArea = 457500
  IfcData = attributes={"GlobalId": {"name": "GlobalId", "type": "IfcGloballyUniqueId", "is_enum": false, "enum_values": []}, "Description": {"... (+475 chars omitted),+1 more (map truncated)
  IfcType = 7
  Length = 3050
  MoveBase = false
  MoveWithHost = false
  Nodes = (2) [(-1.72563e-31,-1.42109e-15,-7.77156e-16),(3050,-1.42109e-15,-7.77156e-16)]
  NodesOffset = 0
  Normal = (0,0,0)
  PerimeterLength = 6400
  Placement = pos=(9010,3225,5800) rot=(0,0,-1;1.5708rad)
  PredefinedType = 0
  VerticalArea = 2.56e+06
  Width = 150
FEATURE [Part::FeaturePython] Structure164  label="V15x40 V155"  # Arch/BIM 7 (typed FeaturePython)
  FaceMaker = 0
  Height = 400
  HorizontalArea = 456000
  IfcData = attributes={"GlobalId": {"name": "GlobalId", "type": "IfcGloballyUniqueId", "is_enum": false, "enum_values": []}, "Description": {"... (+475 chars omitted),+1 more (map truncated)
  IfcType = 7
  Length = 3040
  MoveBase = false
  MoveWithHost = false
  Nodes = (2) [(-1.72563e-31,-1.42109e-15,-7.77156e-16),(3040,-1.42109e-15,-7.77156e-16)]
  NodesOffset = 0
  Normal = (0,0,0)
  PerimeterLength = 6380
  Placement = pos=(9010,6515,5800) rot=(0,0,-1;1.5708rad)
  PredefinedType = 0
  VerticalArea = 2.552e+06
  Width = 150
FEATURE [Part::FeaturePython] Structure165  label="V15x40 V156"  # Arch/BIM 7 (typed FeaturePython)
  FaceMaker = 0
  Height = 400
  HorizontalArea = 459000
  IfcData = attributes={"GlobalId": {"name": "GlobalId", "type": "IfcGloballyUniqueId", "is_enum": false, "enum_values": []}, "Description": {"... (+475 chars omitted),+1 more (map truncated)
  IfcType = 7
  Length = 3060
  MoveBase = false
  MoveWithHost = false
  Nodes = (2) [(-1.72563e-31,-1.42109e-15,-7.77156e-16),(3060,-1.42109e-15,-7.77156e-16)]
  NodesOffset = 0
  Normal = (0,0,0)
  PerimeterLength = 6420
  Placement = pos=(9010,9825,5800) rot=(0,0,-1;1.5708rad)
  PredefinedType = 0
  VerticalArea = 2.568e+06
  Width = 150
FEATURE [Part::FeaturePython] Structure166  label="V15x40 V157"  # Arch/BIM 7 (typed FeaturePython)
  FaceMaker = 0
  Height = 400
  HorizontalArea = 457500
  IfcData = attributes={"GlobalId": {"name": "GlobalId", "type": "IfcGloballyUniqueId", "is_enum": false, "enum_values": []}, "Description": {"... (+475 chars omitted),+1 more (map truncated)
  IfcType = 7
  Length = 3050
  MoveBase = false
  MoveWithHost = false
  Nodes = (2) [(-1.72563e-31,-1.42109e-15,-7.77156e-16),(3050,-1.42109e-15,-7.77156e-16)]
  NodesOffset = 0
  Normal = (0,0,0)
  PerimeterLength = 6400
  Placement = pos=(10560,3225,5800) rot=(0,0,-1;1.5708rad)
  PredefinedType = 0
  VerticalArea = 2.56e+06
  Width = 150
FEATURE [Part::FeaturePython] Structure167  label="V15x40 V158"  # Arch/BIM 7 (typed FeaturePython)
  FaceMaker = 0
  Height = 400
  HorizontalArea = 363000
  IfcData = attributes={"GlobalId": {"name": "GlobalId", "type": "IfcGloballyUniqueId", "is_enum": false, "enum_values": []}, "Description": {"... (+475 chars omitted),+1 more (map truncated)
  IfcType = 7
  Length = 2420
  MoveBase = false
  MoveWithHost = false
  Nodes = (2) [(-1.72563e-31,-1.42109e-15,-7.77156e-16),(2420,-1.42109e-15,-7.77156e-16)]
  NodesOffset = 0
  Normal = (0,0,0)
  PerimeterLength = 5140
  Placement = pos=(10560,3475,5800) rot=(0,0,1;1.5708rad)
  PredefinedType = 0
  VerticalArea = 2056000
  Width = 150
FEATURE [Part::FeaturePython] Structure168  label="V15x40 V159"  # Arch/BIM 7 (typed FeaturePython)
  FaceMaker = 0
  Height = 400
  HorizontalArea = 207000
  IfcData = attributes={"GlobalId": {"name": "GlobalId", "type": "IfcGloballyUniqueId", "is_enum": false, "enum_values": []}, "Description": {"... (+475 chars omitted),+1 more (map truncated)
  IfcType = 7
  Length = 1380
  MoveBase = false
  MoveWithHost = false
  Nodes = (2) [(-1.72563e-31,-1.42109e-15,-7.77156e-16),(1380,-1.42109e-15,-7.77156e-16)]
  NodesOffset = 0
  Normal = (0,0,0)
  PerimeterLength = 3060
  Placement = pos=(10560,8445,5800) rot=(0,0,1;1.5708rad)
  PredefinedType = 0
  VerticalArea = 1224000
  Width = 150
FEATURE [Part::FeaturePython] Structure169  label="V15x40 V160"  # Arch/BIM 7 (typed FeaturePython)
  FaceMaker = 0
  Height = 400
  HorizontalArea = 207000
  IfcData = attributes={"GlobalId": {"name": "GlobalId", "type": "IfcGloballyUniqueId", "is_enum": false, "enum_values": []}, "Description": {"... (+475 chars omitted),+1 more (map truncated)
  IfcType = 7
  Length = 1380
  MoveBase = false
  MoveWithHost = false
  Nodes = (2) [(-1.72563e-31,-1.42109e-15,-7.77156e-16),(1380,-1.42109e-15,-7.77156e-16)]
  NodesOffset = 0
  Normal = (0,0,0)
  PerimeterLength = 3060
  Placement = pos=(12010,9825,5800) rot=(0,0,-1;1.5708rad)
  PredefinedType = 0
  VerticalArea = 1224000
  Width = 150
FEATURE [Part::FeaturePython] Structure170  label="V20x40 V136"  # Arch/BIM 7 (typed FeaturePython)
  FaceMaker = 0
  Height = 400
  HorizontalArea = 615000
  IfcData = attributes={"GlobalId": {"name": "GlobalId", "type": "IfcGloballyUniqueId", "is_enum": false, "enum_values": []}, "Description": {"... (+475 chars omitted),+1 more (map truncated)
  IfcType = 7
  Length = 3075
  MoveBase = false
  MoveWithHost = false
  Nodes = (2) [(-1.72563e-31,0,-7.77156e-16),(3075,0,-7.77156e-16)]
  NodesOffset = 0
  Normal = (0,0,0)
  PerimeterLength = 6550
  Placement = pos=(1930,3250,5800) rot=(0,0,-1;1.5708rad)
  PredefinedType = 0
  VerticalArea = 2.62e+06
  Width = 200
FEATURE [Part::FeaturePython] Structure171  label="V20x40 V137"  # Arch/BIM 7 (typed FeaturePython)
  FaceMaker = 0
  Height = 400
  HorizontalArea = 618000
  IfcData = attributes={"GlobalId": {"name": "GlobalId", "type": "IfcGloballyUniqueId", "is_enum": false, "enum_values": []}, "Description": {"... (+475 chars omitted),+1 more (map truncated)
  IfcType = 7
  Length = 3090
  MoveBase = false
  MoveWithHost = false
  Nodes = (2) [(-1.72563e-31,0,-7.77156e-16),(3090,0,-7.77156e-16)]
  NodesOffset = 0
  Normal = (0,0,0)
  PerimeterLength = 6580
  Placement = pos=(1930,6540,5800) rot=(0,0,-1;1.5708rad)
  PredefinedType = 0
  VerticalArea = 2.632e+06
  Width = 200
FEATURE [Part::FeaturePython] Structure172  label="V20x40 V138"  # Arch/BIM 7 (typed FeaturePython)
  FaceMaker = 0
  Height = 400
  HorizontalArea = 617000
  IfcData = attributes={"GlobalId": {"name": "GlobalId", "type": "IfcGloballyUniqueId", "is_enum": false, "enum_values": []}, "Description": {"... (+475 chars omitted),+1 more (map truncated)
  IfcType = 7
  Length = 3085
  MoveBase = false
  MoveWithHost = false
  Nodes = (2) [(-1.72563e-31,0,-7.77156e-16),(3085,0,-7.77156e-16)]
  NodesOffset = 0
  Normal = (0,0,0)
  PerimeterLength = 6570
  Placement = pos=(1930,9825,5800) rot=(0,0,-1;1.5708rad)
  PredefinedType = 0
  VerticalArea = 2.628e+06
  Width = 200
FEATURE [Part::FeaturePython] Structure173  label="V20x40 V139"  # Arch/BIM 7 (typed FeaturePython)
  FaceMaker = 0
  Height = 400
  HorizontalArea = 635000
  IfcData = attributes={"GlobalId": {"name": "GlobalId", "type": "IfcGloballyUniqueId", "is_enum": false, "enum_values": []}, "Description": {"... (+475 chars omitted),+1 more (map truncated)
  IfcType = 7
  Length = 3175
  MoveBase = false
  MoveWithHost = false
  Nodes = (2) [(-1.72563e-31,0,-7.77156e-16),(3175,0,-7.77156e-16)]
  NodesOffset = 0
  Normal = (0,0,0)
  PerimeterLength = 6750
  Placement = pos=(13780,175,5800) rot=(0,0,1;1.5708rad)
  PredefinedType = 0
  VerticalArea = 2.7e+06
  Width = 200
FEATURE [Part::FeaturePython] Structure174  label="V20x40 V140"  # Arch/BIM 7 (typed FeaturePython)
  FaceMaker = 0
  Height = 400
  HorizontalArea = 509000
  IfcData = attributes={"GlobalId": {"name": "GlobalId", "type": "IfcGloballyUniqueId", "is_enum": false, "enum_values": []}, "Description": {"... (+475 chars omitted),+1 more (map truncated)
  IfcType = 7
  Length = 2545
  MoveBase = false
  MoveWithHost = false
  Nodes = (2) [(-1.72563e-31,0,-7.77156e-16),(2545,0,-7.77156e-16)]
  NodesOffset = 0
  Normal = (0,0,0)
  PerimeterLength = 5490
  Placement = pos=(13780,3350,5800) rot=(0,0,1;1.5708rad)
  PredefinedType = 0
  VerticalArea = 2196000
  Width = 200
FEATURE [Part::FeaturePython] Structure175  label="V20x40 V141"  # Arch/BIM 7 (typed FeaturePython)
  FaceMaker = 0
  Height = 400
  HorizontalArea = 756000
  IfcData = attributes={"GlobalId": {"name": "GlobalId", "type": "IfcGloballyUniqueId", "is_enum": false, "enum_values": []}, "Description": {"... (+475 chars omitted),+1 more (map truncated)
  IfcType = 7
  Length = 3780
  MoveBase = false
  MoveWithHost = false
  Nodes = (2) [(-1.72563e-31,0,-7.77156e-16),(3780,0,-7.77156e-16)]
  NodesOffset = 0
  Normal = (0,0,0)
  PerimeterLength = 7960
  Placement = pos=(15210,6045,5800) rot=(0,0,1;1.5708rad)
  PredefinedType = 0
  VerticalArea = 3.184e+06
  Width = 200
FEATURE [Part::FeaturePython] Structure176  label="25x15 C026"  # Arch/BIM 24 (typed FeaturePython)
  FaceMaker = 0
  Height = 3000
  HorizontalArea = 37500
  IfcData = attributes={"GlobalId": {"name": "GlobalId", "type": "IfcGloballyUniqueId", "is_enum": false, "enum_values": []}, "Description": {"... (+438 chars omitted),+1 more (map truncated)
  IfcType = 24
  Length = 250
  MoveBase = false
  MoveWithHost = false
  Nodes = (2) [(-1.05471e-15,1.36424e-15,0),(-1.05471e-15,1.36424e-15,3000)]
  NodesOffset = 0
  Normal = (0,0,0)
  PerimeterLength = 800
  Placement = pos=(1930,9900,3000) rot=(0,0,1;0rad)
  PredefinedType = 0
  VerticalArea = 2400000
  Width = 150
FEATURE [Part::FeaturePython] Structure177  label="25x15 C027"  # Arch/BIM 172 (typed FeaturePython)
  FaceMaker = 0
  Height = 3000
  HorizontalArea = 37500
  IfcData = attributes={"GlobalId": {"name": "GlobalId", "type": "IfcGloballyUniqueId", "is_enum": false, "enum_values": []}, "Description": {"... (+484 chars omitted),+1 more (map truncated)
  IfcType = 172
  Length = 250
  MoveBase = false
  MoveWithHost = false
  Nodes = (2) [(-1.05471e-15,1.36424e-15,0),(-1.05471e-15,1.36424e-15,3000)]
  NodesOffset = 0
  Normal = (0,0,0)
  PerimeterLength = 800
  Placement = pos=(1930,100,3000) rot=(0,0,1;0rad)
  PredefinedType = 0
  VerticalArea = 2400000
  Width = 150
FEATURE [Part::FeaturePython] Structure178  label="25x20 C008"  # Arch/BIM 24 (typed FeaturePython)
  FaceMaker = 0
  Height = 3000
  HorizontalArea = 50000
  IfcData = attributes={"GlobalId": {"name": "GlobalId", "type": "IfcGloballyUniqueId", "is_enum": false, "enum_values": []}, "Description": {"... (+438 chars omitted),+1 more (map truncated)
  IfcType = 24
  Length = 250
  MoveBase = false
  MoveWithHost = false
  Nodes = (2) [(-1.05471e-15,-1.81899e-15,0),(-1.05471e-15,-1.81899e-15,3000)]
  NodesOffset = 0
  Normal = (0,0,0)
  PerimeterLength = 900
  Placement = pos=(1930,6640,3000) rot=(0,0,1;0rad)
  PredefinedType = 0
  VerticalArea = 2700000
  Width = 200
FEATURE [Part::FeaturePython] Structure180  label="25x15 C028"  # Arch/BIM 24 (typed FeaturePython)
  FaceMaker = 0
  Height = 3000
  HorizontalArea = 37500
  IfcData = attributes={"GlobalId": {"name": "GlobalId", "type": "IfcGloballyUniqueId", "is_enum": false, "enum_values": []}, "Description": {"... (+438 chars omitted),+1 more (map truncated)
  IfcType = 24
  Length = 250
  MoveBase = false
  MoveWithHost = false
  Nodes = (2) [(-1.05471e-15,1.36424e-15,0),(-1.05471e-15,1.36424e-15,3000)]
  NodesOffset = 0
  Normal = (0,0,0)
  PerimeterLength = 800
  Placement = pos=(6160,6640,3000) rot=(0,0,1;0rad)
  PredefinedType = 0
  VerticalArea = 2400000
  Width = 150
FEATURE [Part::FeaturePython] Structure181  label="25x15 C029"  # Arch/BIM 24 (typed FeaturePython)
  FaceMaker = 0
  Height = 3000
  HorizontalArea = 37500
  IfcData = attributes={"GlobalId": {"name": "GlobalId", "type": "IfcGloballyUniqueId", "is_enum": false, "enum_values": []}, "Description": {"... (+438 chars omitted),+1 more (map truncated)
  IfcType = 24
  Length = 250
  MoveBase = false
  MoveWithHost = false
  Nodes = (2) [(-1.05471e-15,1.36424e-15,0),(-1.05471e-15,1.36424e-15,3000)]
  NodesOffset = 0
  Normal = (0,0,0)
  PerimeterLength = 800
  Placement = pos=(6160,3350,3000) rot=(0,0,1;0rad)
  PredefinedType = 0
  VerticalArea = 2400000
  Width = 150
FEATURE [Part::FeaturePython] Structure182  label="25x15 C030"  # Arch/BIM 24 (typed FeaturePython)
  FaceMaker = 0
  Height = 3000
  HorizontalArea = 37500
  IfcData = attributes={"GlobalId": {"name": "GlobalId", "type": "IfcGloballyUniqueId", "is_enum": false, "enum_values": []}, "Description": {"... (+438 chars omitted),+1 more (map truncated)
  IfcType = 24
  Length = 250
  MoveBase = false
  MoveWithHost = false
  Nodes = (2) [(-1.05471e-15,1.36424e-15,0),(-1.05471e-15,1.36424e-15,3000)]
  NodesOffset = 0
  Normal = (0,0,0)
  PerimeterLength = 800
  Placement = pos=(6160,100,3000) rot=(0,0,1;0rad)
  PredefinedType = 0
  VerticalArea = 2400000
  Width = 150
FEATURE [Part::FeaturePython] Structure183  label="25x15 C031"  # Arch/BIM 24 (typed FeaturePython)
  FaceMaker = 0
  Height = 3000
  HorizontalArea = 37500
  IfcData = attributes={"GlobalId": {"name": "GlobalId", "type": "IfcGloballyUniqueId", "is_enum": false, "enum_values": []}, "Description": {"... (+438 chars omitted),+1 more (map truncated)
  IfcType = 24
  Length = 250
  MoveBase = false
  MoveWithHost = false
  Nodes = (2) [(-1.05471e-15,1.36424e-15,0),(-1.05471e-15,1.36424e-15,3000)]
  NodesOffset = 0
  Normal = (0,0,0)
  PerimeterLength = 800
  Placement = pos=(9010,100,3000) rot=(0,0,1;0rad)
  PredefinedType = 0
  VerticalArea = 2400000
  Width = 150
FEATURE [Part::FeaturePython] Structure184  label="25x15 C032"  # Arch/BIM 24 (typed FeaturePython)
  FaceMaker = 0
  Height = 3000
  HorizontalArea = 37500
  IfcData = attributes={"GlobalId": {"name": "GlobalId", "type": "IfcGloballyUniqueId", "is_enum": false, "enum_values": []}, "Description": {"... (+438 chars omitted),+1 more (map truncated)
  IfcType = 24
  Length = 250
  MoveBase = false
  MoveWithHost = false
  Nodes = (2) [(-1.05471e-15,1.36424e-15,0),(-1.05471e-15,1.36424e-15,3000)]
  NodesOffset = 0
  Normal = (0,0,0)
  PerimeterLength = 800
  Placement = pos=(10560,100,3000) rot=(0,0,1;0rad)
  PredefinedType = 0
  VerticalArea = 2400000
  Width = 150
FEATURE [Part::FeaturePython] Structure185  label="25x15 C033"  # Arch/BIM 24 (typed FeaturePython)
  FaceMaker = 0
  Height = 3000
  HorizontalArea = 37500
  IfcData = attributes={"GlobalId": {"name": "GlobalId", "type": "IfcGloballyUniqueId", "is_enum": false, "enum_values": []}, "Description": {"... (+438 chars omitted),+1 more (map truncated)
  IfcType = 24
  Length = 250
  MoveBase = false
  MoveWithHost = false
  Nodes = (2) [(-1.05471e-15,1.36424e-15,0),(-1.05471e-15,1.36424e-15,3000)]
  NodesOffset = 0
  Normal = (0,0,0)
  PerimeterLength = 800
  Placement = pos=(13780,100,3000) rot=(0,0,1;0rad)
  PredefinedType = 0
  VerticalArea = 2400000
  Width = 150
FEATURE [Part::FeaturePython] Structure186  label="25x15 C034"  # Arch/BIM 24 (typed FeaturePython)
  FaceMaker = 0
  Height = 3000
  HorizontalArea = 37500
  IfcData = attributes={"GlobalId": {"name": "GlobalId", "type": "IfcGloballyUniqueId", "is_enum": false, "enum_values": []}, "Description": {"... (+438 chars omitted),+1 more (map truncated)
  IfcType = 24
  Length = 250
  MoveBase = false
  MoveWithHost = false
  Nodes = (2) [(-1.05471e-15,1.36424e-15,0),(-1.05471e-15,1.36424e-15,3000)]
  NodesOffset = 0
  Normal = (0,0,0)
  PerimeterLength = 800
  Placement = pos=(15210,5970,3000) rot=(0,0,1;0rad)
  PredefinedType = 0
  VerticalArea = 2400000
  Width = 150
FEATURE [Part::FeaturePython] Structure187  label="25x15 C035"  # Arch/BIM 24 (typed FeaturePython)
  FaceMaker = 0
  Height = 3000
  HorizontalArea = 37500
  IfcData = attributes={"GlobalId": {"name": "GlobalId", "type": "IfcGloballyUniqueId", "is_enum": false, "enum_values": []}, "Description": {"... (+438 chars omitted),+1 more (map truncated)
  IfcType = 24
  Length = 250
  MoveBase = false
  MoveWithHost = false
  Nodes = (2) [(-1.05471e-15,1.36424e-15,0),(-1.05471e-15,1.36424e-15,3000)]
  NodesOffset = 0
  Normal = (0,0,0)
  PerimeterLength = 800
  Placement = pos=(13780,5970,3000) rot=(0,0,1;0rad)
  PredefinedType = 0
  VerticalArea = 2400000
  Width = 150
FEATURE [Part::FeaturePython] Structure188  label="25x15 C036"  # Arch/BIM 172 (typed FeaturePython)
  FaceMaker = 0
  Height = 3000
  HorizontalArea = 37500
  IfcData = attributes={"GlobalId": {"name": "GlobalId", "type": "IfcGloballyUniqueId", "is_enum": false, "enum_values": []}, "Description": {"... (+484 chars omitted),+1 more (map truncated)
  IfcType = 172
  Length = 250
  MoveBase = false
  MoveWithHost = false
  Nodes = (2) [(-1.05471e-15,1.36424e-15,0),(-1.05471e-15,1.36424e-15,3000)]
  NodesOffset = 0
  Normal = (0,0,0)
  PerimeterLength = 800
  Placement = pos=(1930,9900,3000) rot=(0,0,1;0rad)
  PredefinedType = 0
  VerticalArea = 2400000
  Width = 150
FEATURE [Part::FeaturePython] Structure189  label="25x15 C037"  # Arch/BIM 172 (typed FeaturePython)
  FaceMaker = 0
  Height = 3000
  HorizontalArea = 37500
  IfcData = attributes={"GlobalId": {"name": "GlobalId", "type": "IfcGloballyUniqueId", "is_enum": false, "enum_values": []}, "Description": {"... (+484 chars omitted),+1 more (map truncated)
  IfcType = 172
  Length = 250
  MoveBase = false
  MoveWithHost = false
  Nodes = (2) [(-1.05471e-15,1.36424e-15,0),(-1.05471e-15,1.36424e-15,3000)]
  NodesOffset = 0
  Normal = (0,0,0)
  PerimeterLength = 800
  Placement = pos=(9010,6640,3000) rot=(0,0,1;1.5708rad)
  PredefinedType = 0
  VerticalArea = 2400000
  Width = 150
FEATURE [Part::FeaturePython] Structure190  label="25x15 C038"  # Arch/BIM 172 (typed FeaturePython)
  FaceMaker = 0
  Height = 3000
  HorizontalArea = 37500
  IfcData = attributes={"GlobalId": {"name": "GlobalId", "type": "IfcGloballyUniqueId", "is_enum": false, "enum_values": []}, "Description": {"... (+484 chars omitted),+1 more (map truncated)
  IfcType = 172
  Length = 250
  MoveBase = false
  MoveWithHost = false
  Nodes = (2) [(-1.05471e-15,1.36424e-15,0),(-1.05471e-15,1.36424e-15,3000)]
  NodesOffset = 0
  Normal = (0,0,0)
  PerimeterLength = 800
  Placement = pos=(9010,3350,3000) rot=(0,0,1;1.5708rad)
  PredefinedType = 0
  VerticalArea = 2400000
  Width = 150
FEATURE [Part::FeaturePython] Structure191  label="25x15 C039"  # Arch/BIM 172 (typed FeaturePython)
  FaceMaker = 0
  Height = 3000
  HorizontalArea = 37500
  IfcData = attributes={"GlobalId": {"name": "GlobalId", "type": "IfcGloballyUniqueId", "is_enum": false, "enum_values": []}, "Description": {"... (+484 chars omitted),+1 more (map truncated)
  IfcType = 172
  Length = 250
  MoveBase = false
  MoveWithHost = false
  Nodes = (2) [(-1.05471e-15,1.36424e-15,0),(-1.05471e-15,1.36424e-15,3000)]
  NodesOffset = 0
  Normal = (0,0,0)
  PerimeterLength = 800
  Placement = pos=(10560,3350,3000) rot=(0,0,1;1.5708rad)
  PredefinedType = 0
  VerticalArea = 2400000
  Width = 150
FEATURE [Part::FeaturePython] Structure192  label="25x15 C040"  # Arch/BIM 172 (typed FeaturePython)
  FaceMaker = 0
  Height = 3000
  HorizontalArea = 37500
  IfcData = attributes={"GlobalId": {"name": "GlobalId", "type": "IfcGloballyUniqueId", "is_enum": false, "enum_values": []}, "Description": {"... (+484 chars omitted),+1 more (map truncated)
  IfcType = 172
  Length = 250
  MoveBase = false
  MoveWithHost = false
  Nodes = (2) [(-1.05471e-15,1.36424e-15,0),(-1.05471e-15,1.36424e-15,3000)]
  NodesOffset = 0
  Normal = (0,0,0)
  PerimeterLength = 800
  Placement = pos=(13780,3350,3000) rot=(0,0,1;1.5708rad)
  PredefinedType = 0
  VerticalArea = 2400000
  Width = 150
FEATURE [Part::FeaturePython] Structure193  label="25x15 C041"  # Arch/BIM 172 (typed FeaturePython)
  FaceMaker = 0
  Height = 3000
  HorizontalArea = 37500
  IfcData = attributes={"GlobalId": {"name": "GlobalId", "type": "IfcGloballyUniqueId", "is_enum": false, "enum_values": []}, "Description": {"... (+484 chars omitted),+1 more (map truncated)
  IfcType = 172
  Length = 250
  MoveBase = false
  MoveWithHost = false
  Nodes = (2) [(-1.05471e-15,1.36424e-15,0),(-1.05471e-15,1.36424e-15,3000)]
  NodesOffset = 0
  Normal = (0,0,0)
  PerimeterLength = 800
  Placement = pos=(9010,9900,3000) rot=(0,0,1;0rad)
  PredefinedType = 0
  VerticalArea = 2400000
  Width = 150
FEATURE [Part::FeaturePython] Structure194  label="25x15 C042"  # Arch/BIM 172 (typed FeaturePython)
  FaceMaker = 0
  Height = 3000
  HorizontalArea = 37500
  IfcData = attributes={"GlobalId": {"name": "GlobalId", "type": "IfcGloballyUniqueId", "is_enum": false, "enum_values": []}, "Description": {"... (+484 chars omitted),+1 more (map truncated)
  IfcType = 172
  Length = 250
  MoveBase = false
  MoveWithHost = false
  Nodes = (2) [(-1.05471e-15,1.36424e-15,0),(-1.05471e-15,1.36424e-15,3000)]
  NodesOffset = 0
  Normal = (0,0,0)
  PerimeterLength = 800
  Placement = pos=(6160,9900,3000) rot=(0,0,1;0rad)
  PredefinedType = 0
  VerticalArea = 2400000
  Width = 150
FEATURE [Part::FeaturePython] Structure195  label="25x15 C043"  # Arch/BIM 172 (typed FeaturePython)
  FaceMaker = 0
  Height = 3000
  HorizontalArea = 37500
  IfcData = attributes={"GlobalId": {"name": "GlobalId", "type": "IfcGloballyUniqueId", "is_enum": false, "enum_values": []}, "Description": {"... (+484 chars omitted),+1 more (map truncated)
  IfcType = 172
  Length = 250
  MoveBase = false
  MoveWithHost = false
  Nodes = (2) [(-1.05471e-15,1.36424e-15,0),(-1.05471e-15,1.36424e-15,3000)]
  NodesOffset = 0
  Normal = (0,0,0)
  PerimeterLength = 800
  Placement = pos=(12010,9900,3000) rot=(0,0,1;0rad)
  PredefinedType = 0
  VerticalArea = 2400000
  Width = 150
FEATURE [Part::FeaturePython] Structure196  label="25x15 C044"  # Arch/BIM 172 (typed FeaturePython)
  FaceMaker = 0
  Height = 3000
  HorizontalArea = 37500
  IfcData = attributes={"GlobalId": {"name": "GlobalId", "type": "IfcGloballyUniqueId", "is_enum": false, "enum_values": []}, "Description": {"... (+484 chars omitted),+1 more (map truncated)
  IfcType = 172
  Length = 250
  MoveBase = false
  MoveWithHost = false
  Nodes = (2) [(-1.05471e-15,1.36424e-15,0),(-1.05471e-15,1.36424e-15,3000)]
  NodesOffset = 0
  Normal = (0,0,0)
  PerimeterLength = 800
  Placement = pos=(15210,9900,3000) rot=(0,0,1;0rad)
  PredefinedType = 0
  VerticalArea = 2400000
  Width = 150
FEATURE [Part::FeaturePython] Structure179  label="25x20 C009"  # Arch/BIM 172 (typed FeaturePython)
  FaceMaker = 0
  Height = 3000
  HorizontalArea = 50000
  IfcData = attributes={"GlobalId": {"name": "GlobalId", "type": "IfcGloballyUniqueId", "is_enum": false, "enum_values": []}, "Description": {"... (+484 chars omitted),+1 more (map truncated)
  IfcType = 172
  Length = 250
  MoveBase = false
  MoveWithHost = false
  Nodes = (2) [(-1.05471e-15,-1.81899e-15,0),(-1.05471e-15,-1.81899e-15,3000)]
  NodesOffset = 0
  Normal = (0,0,0)
  PerimeterLength = 900
  Placement = pos=(1930,3350,3000) rot=(0,0,1;0rad)
  PredefinedType = 0
  VerticalArea = 2700000
  Width = 200
FEATURE [App::GeometryPython] BuildingPart012  label="Columnas P1"  # Arch/BIM 172 (typed FeaturePython)
  Area = 0
  Group = -> [Structure176,Structure177,Structure180,Structure181,Structure182,Structure183,Structure184,Structure185,Structure186,Structure187,Structure188,Structure189,Structure190,Structure191,Structure192,Structure193,Structure194,Structure195,Structure196,Structure178,Structure179]
  Height = 0
  HeightPropagate = true
  IfcData = attributes={"GlobalId": {"name": "GlobalId", "type": "IfcGloballyUniqueId", "is_enum": false, "enum_values": []}, "Description": {"... (+484 chars omitted),+1 more (map truncated)
  IfcType = 172
  LevelOffset = 0
  PredefinedType = 0
FEATURE [Part::FeaturePython] Wall002  label="Tabique Ascensor P1"  # Arch/BIM 166 (typed FeaturePython)
  Align = 1
  Area = 24900000
  Base = -> Rectangle003
  BlockHeight = 0
  BlockLength = 0
  CountBroken = 0
  CountEntire = 0
  Face = 0
  Height = 3000
  HorizontalArea = 1155000
  IfcData = attributes={"GlobalId": {"name": "GlobalId", "type": "IfcGloballyUniqueId", "is_enum": false, "enum_values": []}, "Description": {"... (+533 chars omitted),+1 more (map truncated)
  IfcType = 166
  Joint = 0
  Length = 8300
  MakeBlocks = false
  MoveBase = false
  MoveWithHost = false
  Normal = (0,0,0)
  OffsetFirst = 0
  OffsetSecond = 0
  PerimeterLength = 8300
  Placement = pos=(0,0,3000) rot=(0,0,1;0rad)
  PredefinedType = 0
  VerticalArea = 46200000
  Width = 150
FEATURE [Part::Part2DObjectPython] Rectangle004  # Draft 2D object (typed FeaturePython)
  Area = 12611050
  ChamferSize = 0
  Columns = 1
  FilletRadius = 0
  Height = 3110
  Length = 4055
  MakeFace = true
  Placement = pos=(2030,6715,3000) rot=(0,0,1;0rad)
  Rows = 1
FEATURE [Part::Part2DObjectPython] Rectangle005  # Draft 2D object (typed FeaturePython)
  Area = 12732700
  ChamferSize = 0
  Columns = 1
  FilletRadius = 0
  Height = 3140
  Length = 4055
  MakeFace = true
  Placement = pos=(2030,3425,3000) rot=(0,0,1;0rad)
  Rows = 1
FEATURE [Part::Part2DObjectPython] Rectangle006  # Draft 2D object (typed FeaturePython)
  Area = 1.25705e+07
  ChamferSize = 0
  Columns = 1
  FilletRadius = 0
  Height = 3100
  Length = 4055
  MakeFace = true
  Placement = pos=(2030,175,3000) rot=(0,0,1;0rad)
  Rows = 1
FEATURE [Part::Part2DObjectPython] Rectangle008  # Draft 2D object (typed FeaturePython)
  Area = 4354000
  ChamferSize = 0
  Columns = 1
  FilletRadius = 0
  Height = 3110
  Length = 1400
  MakeFace = true
  Placement = pos=(9085,6715,3000) rot=(0,0,1;0rad)
  Rows = 1
FEATURE [Part::Part2DObjectPython] Rectangle009  # Draft 2D object (typed FeaturePython)
  Area = 1.794e+06
  ChamferSize = 0
  Columns = 1
  FilletRadius = 0
  Height = 1380
  Length = 1300
  MakeFace = true
  Placement = pos=(10635,8445,3000) rot=(0,0,1;0rad)
  Rows = 1
FEATURE [Part::Part2DObjectPython] Rectangle011  # Draft 2D object (typed FeaturePython)
  Area = 4396000
  ChamferSize = 0
  Columns = 1
  FilletRadius = 0
  Height = 3140
  Length = 1400
  MakeFace = true
  Placement = pos=(9085,3425,3000) rot=(0,0,1;0rad)
  Rows = 1
FEATURE [Part::Part2DObjectPython] Rectangle013  # Draft 2D object (typed FeaturePython)
  Area = 4.34e+06
  ChamferSize = 0
  Columns = 1
  FilletRadius = 0
  Height = 3100
  Length = 1400
  MakeFace = true
  Placement = pos=(9085,175,3000) rot=(0,0,1;0rad)
  Rows = 1
FEATURE [Part::Part2DObjectPython] Rectangle014  # Draft 2D object (typed FeaturePython)
  Area = 3928500
  ChamferSize = 0
  Columns = 1
  FilletRadius = 0
  Height = 1455
  Length = 2700
  MakeFace = true
  Placement = pos=(6235,8370,3000) rot=(0,0,1;0rad)
  Rows = 1
FEATURE [Part::Part2DObjectPython] Rectangle015  # Draft 2D object (typed FeaturePython)
  Area = 4.0365e+06
  ChamferSize = 0
  Columns = 1
  FilletRadius = 0
  Height = 1495
  Length = 2700
  MakeFace = true
  Placement = pos=(6235,3425,3000) rot=(0,0,1;0rad)
  Rows = 1
FEATURE [Part::Part2DObjectPython] Rectangle016  # Draft 2D object (typed FeaturePython)
  Area = 3.915e+06
  ChamferSize = 0
  Columns = 1
  FilletRadius = 0
  Height = 1450
  Length = 2700
  MakeFace = true
  Placement = pos=(6235,175,3000) rot=(0,0,1;0rad)
  Rows = 1
FEATURE [Part::Part2DObjectPython] Line  # Draft 2D object (typed FeaturePython)
  Area = 0
  ChamferSize = 0
  Closed = false
  End = (8635,7770,3000)
  FilletRadius = 0
  Length = 450
  MakeFace = true
  Placement = pos=(8635,8220,3000) rot=(0,0,1;0rad)
  Points = (2) [(0,0,0),(0,-450,0)]
  Start = (8635,8220,3000)
  Subdivisions = 0
FEATURE [Part::Part2DObjectPython] Line001  # Draft 2D object (typed FeaturePython)
  Area = 0
  ChamferSize = 0
  Closed = false
  End = (8935,7770,3000)
  FilletRadius = 0
  Length = 300
  MakeFace = true
  Placement = pos=(8635,7770,3000) rot=(0,0,1;0rad)
  Points = (2) [(0,0,0),(300,0,0)]
  Start = (8635,7770,3000)
  Subdivisions = 0
FEATURE [Part::Part2DObjectPython] Line002  # Draft 2D object (typed FeaturePython)
  Area = 0
  ChamferSize = 0
  Closed = false
  End = (8635,5070.11,3000)
  FilletRadius = 0
  Length = 450
  MakeFace = true
  Placement = pos=(8635,5520.11,3000) rot=(0,0,1;0rad)
  Points = (2) [(0,0,0),(0,-450,0)]
  Start = (8635,5520.11,3000)
  Subdivisions = 0
FEATURE [Part::Part2DObjectPython] Line003  # Draft 2D object (typed FeaturePython)
  Area = 0
  ChamferSize = 0
  Closed = false
  End = (8935,5520.11,3000)
  FilletRadius = 0
  Length = 300
  MakeFace = true
  Placement = pos=(8635,5520.11,3000) rot=(0,0,1;0rad)
  Points = (2) [(0,0,0),(300,0,0)]
  Start = (8635,5520.11,3000)
  Subdivisions = 0
FEATURE [Part::Part2DObjectPython] Line004  # Draft 2D object (typed FeaturePython)
  Area = 0
  ChamferSize = 0
  Closed = false
  End = (8935,2225.11,3000)
  FilletRadius = 0
  Length = 300
  MakeFace = true
  Placement = pos=(8635,2225.11,3000) rot=(0,0,1;0rad)
  Points = (2) [(0,0,0),(300,0,0)]
  Start = (8635,2225.11,3000)
  Subdivisions = 0
FEATURE [Part::Part2DObjectPython] Line005  # Draft 2D object (typed FeaturePython)
  Area = 0
  ChamferSize = 0
  Closed = false
  End = (8635,1775.11,3000)
  FilletRadius = 0
  Length = 450
  MakeFace = true
  Placement = pos=(8635,2225.11,3000) rot=(0,0,1;0rad)
  Points = (2) [(0,0,0),(0,-450,0)]
  Start = (8635,2225.11,3000)
  Subdivisions = 0
FEATURE [Part::Part2DObjectPython] Line006  # Draft 2D object (typed FeaturePython)
  Area = 0
  ChamferSize = 0
  Closed = false
  End = (8935,8220,3000)
  FilletRadius = 0
  Length = 540.833
  MakeFace = true
  Placement = pos=(8635,7770,3000) rot=(0,0,1;0rad)
  Points = (2) [(0,0,0),(300,450,0)]
  Start = (8635,7770,3000)
  Subdivisions = 0
FEATURE [Part::Part2DObjectPython] Line007  # Draft 2D object (typed FeaturePython)
  Area = 0
  ChamferSize = 0
  Closed = false
  End = (8935,7770,3000)
  FilletRadius = 0
  Length = 540.833
  MakeFace = true
  Placement = pos=(8635,8220,3000) rot=(0,0,1;0rad)
  Points = (2) [(0,0,0),(300,-450,0)]
  Start = (8635,8220,3000)
  Subdivisions = 0
FEATURE [Part::Part2DObjectPython] Line008  # Draft 2D object (typed FeaturePython)
  Area = 0
  ChamferSize = 0
  Closed = false
  End = (8935,5070,3000)
  FilletRadius = 0
  Length = 540.921
  MakeFace = true
  Placement = pos=(8635,5520.11,3000) rot=(0,0,1;0rad)
  Points = (2) [(0,0,0),(300,-450.106,0)]
  Start = (8635,5520.11,3000)
  Subdivisions = 0
FEATURE [Part::Part2DObjectPython] Line009  # Draft 2D object (typed FeaturePython)
  Area = 0
  ChamferSize = 0
  Closed = false
  End = (8935,5520.11,3000)
  FilletRadius = 0
  Length = 540.833
  MakeFace = true
  Placement = pos=(8635,5070.11,3000) rot=(0,0,1;0rad)
  Points = (2) [(0,0,0),(300,450,0)]
  Start = (8635,5070.11,3000)
  Subdivisions = 0
FEATURE [Part::Part2DObjectPython] Line010  # Draft 2D object (typed FeaturePython)
  Area = 0
  ChamferSize = 0
  Closed = false
  End = (8935,2225.11,3000)
  FilletRadius = 0
  Length = 540.833
  MakeFace = true
  Placement = pos=(8635,1775.11,3000) rot=(0,0,1;0rad)
  Points = (2) [(0,0,0),(300,450,0)]
  Start = (8635,1775.11,3000)
  Subdivisions = 0
FEATURE [Part::Part2DObjectPython] Line011  # Draft 2D object (typed FeaturePython)
  Area = 0
  ChamferSize = 0
  Closed = false
  End = (8935,1775,3000)
  FilletRadius = 0
  Length = 540.921
  MakeFace = true
  Placement = pos=(8635,2225.11,3000) rot=(0,0,1;0rad)
  Points = (2) [(0,0,0),(300,-450.106,0)]
  Start = (8635,2225.11,3000)
  Subdivisions = 0
FEATURE [Part::Part2DObjectPython] Wire  # Draft 2D object (typed FeaturePython)
  Area = 3.9285e+06
  ChamferSize = 0
  Closed = true
  End = (8935,6715,3000)
  FilletRadius = 0
  Length = 8410
  MakeFace = true
  Placement = pos=(6235,6715,3000) rot=(0,0,1;0rad)
  Points = (6) [(0,0,0),(0,1505,0),(2400,1505,0),(2400,1055,0),(2700,1055,0),(2700,9.09495e-13,0)]
  Start = (6235,6715,3000)
  Subdivisions = 0
FEATURE [Part::Part2DObjectPython] Wire001  # Draft 2D object (typed FeaturePython)
  Area = 3.90134e+06
  ChamferSize = 0
  Closed = true
  End = (6235,5070,3000)
  FilletRadius = 0
  Length = 8389.89
  MakeFace = true
  Placement = pos=(6235,6565,3000) rot=(0,0,1;0rad)
  Points = (6) [(0,0,0),(2700,0,0),(2700,-1044.89,0),(2400,-1044.89,0),(2400,-1494.89,0),(0,-1495,0)]
  Start = (6235,6565,3000)
  Subdivisions = 0
FEATURE [Part::Part2DObjectPython] Wire002  # Draft 2D object (typed FeaturePython)
  Area = 3.91484e+06
  ChamferSize = 0
  Closed = true
  End = (6235,1775,3000)
  FilletRadius = 0
  Length = 8399.89
  MakeFace = true
  Placement = pos=(6235,3275,3000) rot=(0,0,1;0rad)
  Points = (6) [(0,0,0),(2700,-4.54747e-13,0),(2700,-1049.89,0),(2400,-1049.89,0),(2400,-1499.89,0),(0,-1500,0)]
  Start = (6235,3275,3000)
  Subdivisions = 0
FEATURE [Part::Part2DObjectPython] Rectangle017  # Draft 2D object (typed FeaturePython)
  Area = 4174500
  ChamferSize = 0
  Columns = 1
  FilletRadius = 0
  Height = 1380
  Length = 3025
  MakeFace = true
  Placement = pos=(12085,8445,3000) rot=(0,0,1;0rad)
  Rows = 1
FEATURE [Part::Part2DObjectPython] Rectangle018  # Draft 2D object (typed FeaturePython)
  Area = 3.211e+06
  ChamferSize = 0
  Columns = 1
  FilletRadius = 0
  Height = 2470
  Length = 1300
  MakeFace = true
  Placement = pos=(10635,3425,3000) rot=(0,0,1;0rad)
  Rows = 1
FEATURE [Part::Part2DObjectPython] Rectangle019  # Draft 2D object (typed FeaturePython)
  Area = 3.93965e+06
  ChamferSize = 0
  Columns = 1
  FilletRadius = 0
  Height = 2470
  Length = 1595
  MakeFace = true
  Placement = pos=(12085,3425,3000) rot=(0,0,1;0rad)
  Rows = 1
FEATURE [Part::Part2DObjectPython] Rectangle020  # Draft 2D object (typed FeaturePython)
  Area = 9439500
  ChamferSize = 0
  Columns = 1
  FilletRadius = 0
  Height = 3100
  Length = 3045
  MakeFace = true
  Placement = pos=(10635,175,3000) rot=(0,0,1;0rad)
  Rows = 1
FEATURE [Part::FeaturePython] Structure219  label="L118"  # Arch/BIM 172 (typed FeaturePython)
  Base = -> Rectangle004
  FaceMaker = 0
  Height = 150
  HorizontalArea = 12611050
  IfcData = attributes={"GlobalId": {"name": "GlobalId", "type": "IfcGloballyUniqueId", "is_enum": false, "enum_values": []}, "Description": {"... (+484 chars omitted),+1 more (map truncated)
  IfcType = 172
  Length = 0
  MoveBase = false
  MoveWithHost = false
  Nodes = (2) [(4057.5,8270,3000),(4057.5,8270,2850)]
  NodesOffset = 0
  Normal = (0,0,-1)
  PerimeterLength = 14330
  Placement = pos=(0,0,3000) rot=(0,0,1;0rad)
  PredefinedType = 0
  VerticalArea = 2149500
  Width = 150
FEATURE [Part::FeaturePython] Structure220  label="L119"  # Arch/BIM 172 (typed FeaturePython)
  Base = -> Rectangle005
  FaceMaker = 0
  Height = 150
  HorizontalArea = 12732700
  IfcData = attributes={"GlobalId": {"name": "GlobalId", "type": "IfcGloballyUniqueId", "is_enum": false, "enum_values": []}, "Description": {"... (+484 chars omitted),+1 more (map truncated)
  IfcType = 172
  Length = 0
  MoveBase = false
  MoveWithHost = false
  Nodes = (2) [(4057.5,4995,3000),(4057.5,4995,2850)]
  NodesOffset = 0
  Normal = (0,0,-1)
  PerimeterLength = 14390
  Placement = pos=(0,0,3000) rot=(0,0,1;0rad)
  PredefinedType = 0
  VerticalArea = 2158500
  Width = 150
FEATURE [Part::FeaturePython] Structure221  label="L120"  # Arch/BIM 172 (typed FeaturePython)
  Base = -> Rectangle006
  FaceMaker = 0
  Height = 150
  HorizontalArea = 1.25705e+07
  IfcData = attributes={"GlobalId": {"name": "GlobalId", "type": "IfcGloballyUniqueId", "is_enum": false, "enum_values": []}, "Description": {"... (+484 chars omitted),+1 more (map truncated)
  IfcType = 172
  Length = 0
  MoveBase = false
  MoveWithHost = false
  Nodes = (2) [(4057.5,1725,3000),(4057.5,1725,2850)]
  NodesOffset = 0
  Normal = (0,0,-1)
  PerimeterLength = 14310
  Placement = pos=(0,0,3000) rot=(0,0,1;0rad)
  PredefinedType = 0
  VerticalArea = 2146500
  Width = 150
FEATURE [Part::FeaturePython] Structure222  label="V15x40 V102a001"  # Arch/BIM 7 (typed FeaturePython)
  FaceMaker = 0
  Height = 400
  HorizontalArea = 405000
  IfcData = attributes={"GlobalId": {"name": "GlobalId", "type": "IfcGloballyUniqueId", "is_enum": false, "enum_values": []}, "Description": {"... (+475 chars omitted),+1 more (map truncated)
  IfcType = 7
  Length = 2700
  MoveBase = false
  MoveWithHost = false
  Nodes = (2) [(-1.72563e-31,-1.42109e-15,-7.77156e-16),(2700,-1.42109e-15,-7.77156e-16)]
  NodesOffset = 0
  Normal = (0,0,0)
  PerimeterLength = 5700
  Placement = pos=(8935,8295,5800) rot=(0,0,1;3.14159rad)
  PredefinedType = 0
  VerticalArea = 2.28e+06
  Width = 150
FEATURE [Part::FeaturePython] Structure223  label="V15x40 V107a001"  # Arch/BIM 7 (typed FeaturePython)
  FaceMaker = 0
  Height = 400
  HorizontalArea = 405000
  IfcData = attributes={"GlobalId": {"name": "GlobalId", "type": "IfcGloballyUniqueId", "is_enum": false, "enum_values": []}, "Description": {"... (+475 chars omitted),+1 more (map truncated)
  IfcType = 7
  Length = 2700
  MoveBase = false
  MoveWithHost = false
  Nodes = (2) [(-1.72563e-31,-1.42109e-15,-7.77156e-16),(2700,-1.42109e-15,-7.77156e-16)]
  NodesOffset = 0
  Normal = (0,0,0)
  PerimeterLength = 5700
  Placement = pos=(8935,4995,5800) rot=(0,0,1;3.14159rad)
  PredefinedType = 0
  VerticalArea = 2.28e+06
  Width = 150
FEATURE [Part::FeaturePython] Structure224  label="V15x40 V112a001"  # Arch/BIM 7 (typed FeaturePython)
  FaceMaker = 0
  Height = 400
  HorizontalArea = 405000
  IfcData = attributes={"GlobalId": {"name": "GlobalId", "type": "IfcGloballyUniqueId", "is_enum": false, "enum_values": []}, "Description": {"... (+475 chars omitted),+1 more (map truncated)
  IfcType = 7
  Length = 2700
  MoveBase = false
  MoveWithHost = false
  Nodes = (2) [(-1.72563e-31,-1.42109e-15,-7.77156e-16),(2700,-1.42109e-15,-7.77156e-16)]
  NodesOffset = 0
  Normal = (0,0,0)
  PerimeterLength = 5700
  Placement = pos=(8935,1700,5800) rot=(0,0,1;3.14159rad)
  PredefinedType = 0
  VerticalArea = 2.28e+06
  Width = 150
FEATURE [Part::FeaturePython] Structure225  label="V15x40 V130a001"  # Arch/BIM 7 (typed FeaturePython)
  FaceMaker = 0
  Height = 400
  HorizontalArea = 370500
  IfcData = attributes={"GlobalId": {"name": "GlobalId", "type": "IfcGloballyUniqueId", "is_enum": false, "enum_values": []}, "Description": {"... (+475 chars omitted),+1 more (map truncated)
  IfcType = 7
  Length = 2470
  MoveBase = false
  MoveWithHost = false
  Nodes = (2) [(-1.72563e-31,-1.42109e-15,-7.77156e-16),(2470,-1.42109e-15,-7.77156e-16)]
  NodesOffset = 0
  Normal = (0,0,0)
  PerimeterLength = 5240
  Placement = pos=(12010,3425,5800) rot=(0,0,1;1.5708rad)
  PredefinedType = 0
  VerticalArea = 2096000
  Width = 150
FEATURE [App::GeometryPython] BuildingPart011  label="Vigas sobre P1"  # Arch/BIM 172 (typed FeaturePython)
  Area = 0
  Group = -> [Structure222,Structure223,Structure224,Structure225,Structure142,Structure143,Structure144,Structure145,Structure146,Structure147,Structure148,Structure149,Structure150,Structure151,Structure152,Structure153,Structure154,Structure155,Structure156,Structure157,Structure158,Structure159,Structure160,Structure161,Structure162,Structure163,Structure164,Structure165,Structure166,Structure167,+8 more]
  Height = 0
  HeightPropagate = true
  IfcData = attributes={"GlobalId": {"name": "GlobalId", "type": "IfcGloballyUniqueId", "is_enum": false, "enum_values": []}, "Description": {"... (+484 chars omitted),+1 more (map truncated)
  IfcType = 172
  LevelOffset = 0
  PredefinedType = 0
FEATURE [Part::FeaturePython] Structure226  label="L121"  # Arch/BIM 172 (typed FeaturePython)
  Base = -> Rectangle014
  FaceMaker = 0
  Height = 150
  HorizontalArea = 3928500
  IfcData = attributes={"GlobalId": {"name": "GlobalId", "type": "IfcGloballyUniqueId", "is_enum": false, "enum_values": []}, "Description": {"... (+484 chars omitted),+1 more (map truncated)
  IfcType = 172
  Length = 0
  MoveBase = false
  MoveWithHost = false
  Nodes = (2) [(7585,9097.5,3000),(7585,9097.5,2850)]
  NodesOffset = 0
  Normal = (0,0,-1)
  PerimeterLength = 8310
  Placement = pos=(0,0,3000) rot=(0,0,1;0rad)
  PredefinedType = 0
  VerticalArea = 1246500
  Width = 150
FEATURE [Part::FeaturePython] Structure227  label="L122"  # Arch/BIM 172 (typed FeaturePython)
  Base = -> Wire
  FaceMaker = 0
  Height = 150
  HorizontalArea = 3.9285e+06
  IfcData = attributes={"GlobalId": {"name": "GlobalId", "type": "IfcGloballyUniqueId", "is_enum": false, "enum_values": []}, "Description": {"... (+484 chars omitted),+1 more (map truncated)
  IfcType = 172
  Length = 0
  MoveBase = false
  MoveWithHost = false
  Nodes = (2) [(7543.76,7449.37,3000),(7543.76,7449.37,2850)]
  NodesOffset = 0
  Normal = (0,0,-1)
  PerimeterLength = 8410
  Placement = pos=(0,0,2850) rot=(0,0,1;0rad)
  PredefinedType = 0
  VerticalArea = 1261500
  Width = 150
FEATURE [Part::FeaturePython] Structure228  label="L123"  # Arch/BIM 172 (typed FeaturePython)
  Base = -> Wire001
  FaceMaker = 0
  Height = 150
  HorizontalArea = 3.90134e+06
  IfcData = attributes={"GlobalId": {"name": "GlobalId", "type": "IfcGloballyUniqueId", "is_enum": false, "enum_values": []}, "Description": {"... (+484 chars omitted),+1 more (map truncated)
  IfcType = 172
  Length = 0
  MoveBase = false
  MoveWithHost = false
  Nodes = (2) [(7543.46,5835.61,3000),(7543.46,5835.61,2850)]
  NodesOffset = 0
  Normal = (0,0,-1)
  PerimeterLength = 8389.89
  Placement = pos=(0,0,2850) rot=(0,0,1;0rad)
  PredefinedType = 0
  VerticalArea = 1.25848e+06
  Width = 150
FEATURE [Part::FeaturePython] Structure229  label="L124"  # Arch/BIM 172 (typed FeaturePython)
  Base = -> Rectangle015
  FaceMaker = 0
  Height = 150
  HorizontalArea = 4.0365e+06
  IfcData = attributes={"GlobalId": {"name": "GlobalId", "type": "IfcGloballyUniqueId", "is_enum": false, "enum_values": []}, "Description": {"... (+484 chars omitted),+1 more (map truncated)
  IfcType = 172
  Length = 0
  MoveBase = false
  MoveWithHost = false
  Nodes = (2) [(7585,4172.5,3000),(7585,4172.5,2850)]
  NodesOffset = 0
  Normal = (0,0,-1)
  PerimeterLength = 8390
  Placement = pos=(0,0,3000) rot=(0,0,1;0rad)
  PredefinedType = 0
  VerticalArea = 1258500
  Width = 150
FEATURE [Part::FeaturePython] Structure230  label="L125"  # Arch/BIM 172 (typed FeaturePython)
  Base = -> Wire002
  FaceMaker = 0
  Height = 150
  HorizontalArea = 3.91484e+06
  IfcData = attributes={"GlobalId": {"name": "GlobalId", "type": "IfcGloballyUniqueId", "is_enum": false, "enum_values": []}, "Description": {"... (+484 chars omitted),+1 more (map truncated)
  IfcType = 172
  Length = 0
  MoveBase = false
  MoveWithHost = false
  Nodes = (2) [(7543.6,2543.13,3000),(7543.6,2543.13,2850)]
  NodesOffset = 0
  Normal = (0,0,-1)
  PerimeterLength = 8399.89
  Placement = pos=(0,0,2850) rot=(0,0,1;0rad)
  PredefinedType = 0
  VerticalArea = 1.25998e+06
  Width = 150
FEATURE [Part::FeaturePython] Structure231  label="L126"  # Arch/BIM 172 (typed FeaturePython)
  Base = -> Rectangle016
  FaceMaker = 0
  Height = 150
  HorizontalArea = 3.915e+06
  IfcData = attributes={"GlobalId": {"name": "GlobalId", "type": "IfcGloballyUniqueId", "is_enum": false, "enum_values": []}, "Description": {"... (+484 chars omitted),+1 more (map truncated)
  IfcType = 172
  Length = 0
  MoveBase = false
  MoveWithHost = false
  Nodes = (2) [(7585,900,3000),(7585,900,2850)]
  NodesOffset = 0
  Normal = (0,0,-1)
  PerimeterLength = 8300
  Placement = pos=(0,0,3000) rot=(0,0,1;0rad)
  PredefinedType = 0
  VerticalArea = 1.245e+06
  Width = 150
FEATURE [Part::FeaturePython] Structure232  label="L127"  # Arch/BIM 172 (typed FeaturePython)
  Base = -> Rectangle008
  FaceMaker = 0
  Height = 150
  HorizontalArea = 4354000
  IfcData = attributes={"GlobalId": {"name": "GlobalId", "type": "IfcGloballyUniqueId", "is_enum": false, "enum_values": []}, "Description": {"... (+484 chars omitted),+1 more (map truncated)
  IfcType = 172
  Length = 0
  MoveBase = false
  MoveWithHost = false
  Nodes = (2) [(9785,8270,3000),(9785,8270,2850)]
  NodesOffset = 0
  Normal = (0,0,-1)
  PerimeterLength = 9020
  Placement = pos=(0,0,3000) rot=(0,0,1;0rad)
  PredefinedType = 0
  VerticalArea = 1353000
  Width = 150
FEATURE [Part::FeaturePython] Structure233  label="L128"  # Arch/BIM 172 (typed FeaturePython)
  Base = -> Rectangle011
  FaceMaker = 0
  Height = 150
  HorizontalArea = 4396000
  IfcData = attributes={"GlobalId": {"name": "GlobalId", "type": "IfcGloballyUniqueId", "is_enum": false, "enum_values": []}, "Description": {"... (+484 chars omitted),+1 more (map truncated)
  IfcType = 172
  Length = 0
  MoveBase = false
  MoveWithHost = false
  Nodes = (2) [(9785,4995,3000),(9785,4995,2850)]
  NodesOffset = 0
  Normal = (0,0,-1)
  PerimeterLength = 9080
  Placement = pos=(0,0,3000) rot=(0,0,1;0rad)
  PredefinedType = 0
  VerticalArea = 1362000
  Width = 150
FEATURE [Part::FeaturePython] Structure234  label="L129"  # Arch/BIM 172 (typed FeaturePython)
  Base = -> Rectangle013
  FaceMaker = 0
  Height = 150
  HorizontalArea = 4.34e+06
  IfcData = attributes={"GlobalId": {"name": "GlobalId", "type": "IfcGloballyUniqueId", "is_enum": false, "enum_values": []}, "Description": {"... (+484 chars omitted),+1 more (map truncated)
  IfcType = 172
  Length = 0
  MoveBase = false
  MoveWithHost = false
  Nodes = (2) [(9785,1725,3000),(9785,1725,2850)]
  NodesOffset = 0
  Normal = (0,0,-1)
  PerimeterLength = 9000
  Placement = pos=(0,0,3000) rot=(0,0,1;0rad)
  PredefinedType = 0
  VerticalArea = 1350000
  Width = 150
FEATURE [Part::FeaturePython] Structure235  label="L130"  # Arch/BIM 172 (typed FeaturePython)
  Base = -> Rectangle009
  FaceMaker = 0
  Height = 150
  HorizontalArea = 1.794e+06
  IfcData = attributes={"GlobalId": {"name": "GlobalId", "type": "IfcGloballyUniqueId", "is_enum": false, "enum_values": []}, "Description": {"... (+484 chars omitted),+1 more (map truncated)
  IfcType = 172
  Length = 0
  MoveBase = false
  MoveWithHost = false
  Nodes = (2) [(11285,9135,3000),(11285,9135,2850)]
  NodesOffset = 0
  Normal = (0,0,-1)
  PerimeterLength = 5360
  Placement = pos=(0,0,3000) rot=(0,0,1;0rad)
  PredefinedType = 0
  VerticalArea = 804000
  Width = 150
FEATURE [Part::FeaturePython] Structure236  label="L131"  # Arch/BIM 172 (typed FeaturePython)
  Base = -> Rectangle018
  FaceMaker = 0
  Height = 150
  HorizontalArea = 3.211e+06
  IfcData = attributes={"GlobalId": {"name": "GlobalId", "type": "IfcGloballyUniqueId", "is_enum": false, "enum_values": []}, "Description": {"... (+484 chars omitted),+1 more (map truncated)
  IfcType = 172
  Length = 0
  MoveBase = false
  MoveWithHost = false
  Nodes = (2) [(11285,4660,3000),(11285,4660,2850)]
  NodesOffset = 0
  Normal = (0,0,-1)
  PerimeterLength = 7540
  Placement = pos=(0,0,2850) rot=(0,0,1;0rad)
  PredefinedType = 0
  VerticalArea = 1.131e+06
  Width = 150
FEATURE [Part::FeaturePython] Structure237  label="L132"  # Arch/BIM 172 (typed FeaturePython)
  Base = -> Rectangle020
  FaceMaker = 0
  Height = 150
  HorizontalArea = 9439500
  IfcData = attributes={"GlobalId": {"name": "GlobalId", "type": "IfcGloballyUniqueId", "is_enum": false, "enum_values": []}, "Description": {"... (+484 chars omitted),+1 more (map truncated)
  IfcType = 172
  Length = 0
  MoveBase = false
  MoveWithHost = false
  Nodes = (2) [(12157.5,1725,3000),(12157.5,1725,2850)]
  NodesOffset = 0
  Normal = (0,0,-1)
  PerimeterLength = 12290
  Placement = pos=(0,0,3000) rot=(0,0,1;0rad)
  PredefinedType = 0
  VerticalArea = 1843500
  Width = 150
FEATURE [Part::FeaturePython] Structure238  label="L133"  # Arch/BIM 172 (typed FeaturePython)
  Base = -> Rectangle019
  FaceMaker = 0
  Height = 150
  HorizontalArea = 3.93965e+06
  IfcData = attributes={"GlobalId": {"name": "GlobalId", "type": "IfcGloballyUniqueId", "is_enum": false, "enum_values": []}, "Description": {"... (+484 chars omitted),+1 more (map truncated)
  IfcType = 172
  Length = 0
  MoveBase = false
  MoveWithHost = false
  Nodes = (2) [(12882.5,4660,3000),(12882.5,4660,2850)]
  NodesOffset = 0
  Normal = (0,0,-1)
  PerimeterLength = 8130
  Placement = pos=(0,0,3000) rot=(0,0,1;0rad)
  PredefinedType = 0
  VerticalArea = 1.2195e+06
  Width = 150
FEATURE [Part::FeaturePython] Structure239  label="L134"  # Arch/BIM 172 (typed FeaturePython)
  Base = -> Rectangle017
  FaceMaker = 0
  Height = 150
  HorizontalArea = 4174500
  IfcData = attributes={"GlobalId": {"name": "GlobalId", "type": "IfcGloballyUniqueId", "is_enum": false, "enum_values": []}, "Description": {"... (+484 chars omitted),+1 more (map truncated)
  IfcType = 172
  Length = 0
  MoveBase = false
  MoveWithHost = false
  Nodes = (2) [(13597.5,9135,3000),(13597.5,9135,2850)]
  NodesOffset = 0
  Normal = (0,0,-1)
  PerimeterLength = 8810
  Placement = pos=(0,0,3000) rot=(0,0,1;0rad)
  PredefinedType = 0
  VerticalArea = 1321500
  Width = 150
FEATURE [App::GeometryPython] BuildingPart015  label="Losas sobre P1"  # Arch/BIM 172 (typed FeaturePython)
  Area = 0
  Group = -> [Structure219,Structure220,Structure221,Structure226,Structure227,Structure228,Structure229,Structure230,Structure231,Structure232,Structure233,Structure234,Structure235,Structure236,Structure237,Structure238,Structure239]
  Height = 0
  HeightPropagate = true
  IfcData = attributes={"GlobalId": {"name": "GlobalId", "type": "IfcGloballyUniqueId", "is_enum": false, "enum_values": []}, "Description": {"... (+484 chars omitted),+1 more (map truncated)
  IfcType = 172
  LevelOffset = 0
  PredefinedType = 0
FEATURE [App::GeometryPython] BuildingPart003  label="Piso 1"  # Arch/BIM 172 (typed FeaturePython)
  Area = 24900000
  Group = -> [BuildingPart012,BuildingPart015,Wall002,BuildingPart011]
  Height = 0
  HeightPropagate = true
  IfcData = attributes={"GlobalId": {"name": "GlobalId", "type": "IfcGloballyUniqueId", "is_enum": false, "enum_values": []}, "Description": {"... (+484 chars omitted),+1 more (map truncated)
  IfcType = 172
  LevelOffset = 0
  Placement = pos=(0,0,3000) rot=(0,0,1;0rad)
  PredefinedType = 0
FEATURE [Part::FeaturePython] Structure240  label="25x15 C045"  # Arch/BIM 24 (typed FeaturePython)
  FaceMaker = 0
  Height = 3000
  HorizontalArea = 37500
  IfcData = attributes={"GlobalId": {"name": "GlobalId", "type": "IfcGloballyUniqueId", "is_enum": false, "enum_values": []}, "Description": {"... (+438 chars omitted),+1 more (map truncated)
  IfcType = 24
  Length = 250
  MoveBase = false
  MoveWithHost = false
  Nodes = (2) [(-1.05471e-15,1.36424e-15,0),(-1.05471e-15,1.36424e-15,3000)]
  NodesOffset = 0
  Normal = (0,0,0)
  PerimeterLength = 800
  Placement = pos=(1930,9900,6000) rot=(0,0,1;0rad)
  PredefinedType = 0
  VerticalArea = 2400000
  Width = 150
FEATURE [Part::FeaturePython] Structure241  label="25x15 C046"  # Arch/BIM 172 (typed FeaturePython)
  FaceMaker = 0
  Height = 3000
  HorizontalArea = 37500
  IfcData = attributes={"GlobalId": {"name": "GlobalId", "type": "IfcGloballyUniqueId", "is_enum": false, "enum_values": []}, "Description": {"... (+484 chars omitted),+1 more (map truncated)
  IfcType = 172
  Length = 250
  MoveBase = false
  MoveWithHost = false
  Nodes = (2) [(-1.05471e-15,1.36424e-15,0),(-1.05471e-15,1.36424e-15,3000)]
  NodesOffset = 0
  Normal = (0,0,0)
  PerimeterLength = 800
  Placement = pos=(1930,100,6000) rot=(0,0,1;0rad)
  PredefinedType = 0
  VerticalArea = 2400000
  Width = 150
FEATURE [Part::FeaturePython] Structure242  label="25x20 C010"  # Arch/BIM 24 (typed FeaturePython)
  FaceMaker = 0
  Height = 3000
  HorizontalArea = 50000
  IfcData = attributes={"GlobalId": {"name": "GlobalId", "type": "IfcGloballyUniqueId", "is_enum": false, "enum_values": []}, "Description": {"... (+438 chars omitted),+1 more (map truncated)
  IfcType = 24
  Length = 250
  MoveBase = false
  MoveWithHost = false
  Nodes = (2) [(-1.05471e-15,-1.81899e-15,0),(-1.05471e-15,-1.81899e-15,3000)]
  NodesOffset = 0
  Normal = (0,0,0)
  PerimeterLength = 900
  Placement = pos=(1930,6640,6000) rot=(0,0,1;0rad)
  PredefinedType = 0
  VerticalArea = 2700000
  Width = 200
FEATURE [Part::FeaturePython] Structure243  label="25x20 C011"  # Arch/BIM 172 (typed FeaturePython)
  FaceMaker = 0
  Height = 3000
  HorizontalArea = 50000
  IfcData = attributes={"GlobalId": {"name": "GlobalId", "type": "IfcGloballyUniqueId", "is_enum": false, "enum_values": []}, "Description": {"... (+484 chars omitted),+1 more (map truncated)
  IfcType = 172
  Length = 250
  MoveBase = false
  MoveWithHost = false
  Nodes = (2) [(-1.05471e-15,-1.81899e-15,0),(-1.05471e-15,-1.81899e-15,3000)]
  NodesOffset = 0
  Normal = (0,0,0)
  PerimeterLength = 900
  Placement = pos=(1930,3350,6000) rot=(0,0,1;0rad)
  PredefinedType = 0
  VerticalArea = 2700000
  Width = 200
FEATURE [Part::FeaturePython] Structure244  label="25x15 C047"  # Arch/BIM 24 (typed FeaturePython)
  FaceMaker = 0
  Height = 3000
  HorizontalArea = 37500
  IfcData = attributes={"GlobalId": {"name": "GlobalId", "type": "IfcGloballyUniqueId", "is_enum": false, "enum_values": []}, "Description": {"... (+438 chars omitted),+1 more (map truncated)
  IfcType = 24
  Length = 250
  MoveBase = false
  MoveWithHost = false
  Nodes = (2) [(-1.05471e-15,1.36424e-15,0),(-1.05471e-15,1.36424e-15,3000)]
  NodesOffset = 0
  Normal = (0,0,0)
  PerimeterLength = 800
  Placement = pos=(6160,6640,6000) rot=(0,0,1;0rad)
  PredefinedType = 0
  VerticalArea = 2400000
  Width = 150
FEATURE [Part::FeaturePython] Structure245  label="25x15 C048"  # Arch/BIM 24 (typed FeaturePython)
  FaceMaker = 0
  Height = 3000
  HorizontalArea = 37500
  IfcData = attributes={"GlobalId": {"name": "GlobalId", "type": "IfcGloballyUniqueId", "is_enum": false, "enum_values": []}, "Description": {"... (+438 chars omitted),+1 more (map truncated)
  IfcType = 24
  Length = 250
  MoveBase = false
  MoveWithHost = false
  Nodes = (2) [(-1.05471e-15,1.36424e-15,0),(-1.05471e-15,1.36424e-15,3000)]
  NodesOffset = 0
  Normal = (0,0,0)
  PerimeterLength = 800
  Placement = pos=(6160,3350,6000) rot=(0,0,1;0rad)
  PredefinedType = 0
  VerticalArea = 2400000
  Width = 150
FEATURE [Part::FeaturePython] Structure246  label="25x15 C049"  # Arch/BIM 24 (typed FeaturePython)
  FaceMaker = 0
  Height = 3000
  HorizontalArea = 37500
  IfcData = attributes={"GlobalId": {"name": "GlobalId", "type": "IfcGloballyUniqueId", "is_enum": false, "enum_values": []}, "Description": {"... (+438 chars omitted),+1 more (map truncated)
  IfcType = 24
  Length = 250
  MoveBase = false
  MoveWithHost = false
  Nodes = (2) [(-1.05471e-15,1.36424e-15,0),(-1.05471e-15,1.36424e-15,3000)]
  NodesOffset = 0
  Normal = (0,0,0)
  PerimeterLength = 800
  Placement = pos=(6160,100,6000) rot=(0,0,1;0rad)
  PredefinedType = 0
  VerticalArea = 2400000
  Width = 150
FEATURE [Part::FeaturePython] Structure247  label="25x15 C050"  # Arch/BIM 24 (typed FeaturePython)
  FaceMaker = 0
  Height = 3000
  HorizontalArea = 37500
  IfcData = attributes={"GlobalId": {"name": "GlobalId", "type": "IfcGloballyUniqueId", "is_enum": false, "enum_values": []}, "Description": {"... (+438 chars omitted),+1 more (map truncated)
  IfcType = 24
  Length = 250
  MoveBase = false
  MoveWithHost = false
  Nodes = (2) [(-1.05471e-15,1.36424e-15,0),(-1.05471e-15,1.36424e-15,3000)]
  NodesOffset = 0
  Normal = (0,0,0)
  PerimeterLength = 800
  Placement = pos=(9010,100,6000) rot=(0,0,1;0rad)
  PredefinedType = 0
  VerticalArea = 2400000
  Width = 150
FEATURE [Part::FeaturePython] Structure248  label="25x15 C051"  # Arch/BIM 24 (typed FeaturePython)
  FaceMaker = 0
  Height = 3000
  HorizontalArea = 37500
  IfcData = attributes={"GlobalId": {"name": "GlobalId", "type": "IfcGloballyUniqueId", "is_enum": false, "enum_values": []}, "Description": {"... (+438 chars omitted),+1 more (map truncated)
  IfcType = 24
  Length = 250
  MoveBase = false
  MoveWithHost = false
  Nodes = (2) [(-1.05471e-15,1.36424e-15,0),(-1.05471e-15,1.36424e-15,3000)]
  NodesOffset = 0
  Normal = (0,0,0)
  PerimeterLength = 800
  Placement = pos=(10560,100,6000) rot=(0,0,1;0rad)
  PredefinedType = 0
  VerticalArea = 2400000
  Width = 150
FEATURE [Part::FeaturePython] Structure249  label="25x15 C052"  # Arch/BIM 24 (typed FeaturePython)
  FaceMaker = 0
  Height = 3000
  HorizontalArea = 37500
  IfcData = attributes={"GlobalId": {"name": "GlobalId", "type": "IfcGloballyUniqueId", "is_enum": false, "enum_values": []}, "Description": {"... (+438 chars omitted),+1 more (map truncated)
  IfcType = 24
  Length = 250
  MoveBase = false
  MoveWithHost = false
  Nodes = (2) [(-1.05471e-15,1.36424e-15,0),(-1.05471e-15,1.36424e-15,3000)]
  NodesOffset = 0
  Normal = (0,0,0)
  PerimeterLength = 800
  Placement = pos=(13780,100,6000) rot=(0,0,1;0rad)
  PredefinedType = 0
  VerticalArea = 2400000
  Width = 150
FEATURE [Part::FeaturePython] Structure250  label="25x15 C053"  # Arch/BIM 24 (typed FeaturePython)
  FaceMaker = 0
  Height = 3000
  HorizontalArea = 37500
  IfcData = attributes={"GlobalId": {"name": "GlobalId", "type": "IfcGloballyUniqueId", "is_enum": false, "enum_values": []}, "Description": {"... (+438 chars omitted),+1 more (map truncated)
  IfcType = 24
  Length = 250
  MoveBase = false
  MoveWithHost = false
  Nodes = (2) [(-1.05471e-15,1.36424e-15,0),(-1.05471e-15,1.36424e-15,3000)]
  NodesOffset = 0
  Normal = (0,0,0)
  PerimeterLength = 800
  Placement = pos=(15210,5970,6000) rot=(0,0,1;0rad)
  PredefinedType = 0
  VerticalArea = 2400000
  Width = 150
FEATURE [Part::FeaturePython] Structure251  label="25x15 C054"  # Arch/BIM 24 (typed FeaturePython)
  FaceMaker = 0
  Height = 3000
  HorizontalArea = 37500
  IfcData = attributes={"GlobalId": {"name": "GlobalId", "type": "IfcGloballyUniqueId", "is_enum": false, "enum_values": []}, "Description": {"... (+438 chars omitted),+1 more (map truncated)
  IfcType = 24
  Length = 250
  MoveBase = false
  MoveWithHost = false
  Nodes = (2) [(-1.05471e-15,1.36424e-15,0),(-1.05471e-15,1.36424e-15,3000)]
  NodesOffset = 0
  Normal = (0,0,0)
  PerimeterLength = 800
  Placement = pos=(13780,5970,6000) rot=(0,0,1;0rad)
  PredefinedType = 0
  VerticalArea = 2400000
  Width = 150
FEATURE [Part::FeaturePython] Structure252  label="25x15 C055"  # Arch/BIM 172 (typed FeaturePython)
  FaceMaker = 0
  Height = 3000
  HorizontalArea = 37500
  IfcData = attributes={"GlobalId": {"name": "GlobalId", "type": "IfcGloballyUniqueId", "is_enum": false, "enum_values": []}, "Description": {"... (+484 chars omitted),+1 more (map truncated)
  IfcType = 172
  Length = 250
  MoveBase = false
  MoveWithHost = false
  Nodes = (2) [(-1.05471e-15,1.36424e-15,0),(-1.05471e-15,1.36424e-15,3000)]
  NodesOffset = 0
  Normal = (0,0,0)
  PerimeterLength = 800
  Placement = pos=(1930,9900,6000) rot=(0,0,1;0rad)
  PredefinedType = 0
  VerticalArea = 2400000
  Width = 150
FEATURE [Part::FeaturePython] Structure253  label="25x15 C056"  # Arch/BIM 172 (typed FeaturePython)
  FaceMaker = 0
  Height = 3000
  HorizontalArea = 37500
  IfcData = attributes={"GlobalId": {"name": "GlobalId", "type": "IfcGloballyUniqueId", "is_enum": false, "enum_values": []}, "Description": {"... (+484 chars omitted),+1 more (map truncated)
  IfcType = 172
  Length = 250
  MoveBase = false
  MoveWithHost = false
  Nodes = (2) [(-1.05471e-15,1.36424e-15,0),(-1.05471e-15,1.36424e-15,3000)]
  NodesOffset = 0
  Normal = (0,0,0)
  PerimeterLength = 800
  Placement = pos=(9010,6640,6000) rot=(0,0,1;1.5708rad)
  PredefinedType = 0
  VerticalArea = 2400000
  Width = 150
FEATURE [Part::FeaturePython] Structure254  label="25x15 C057"  # Arch/BIM 172 (typed FeaturePython)
  FaceMaker = 0
  Height = 3000
  HorizontalArea = 37500
  IfcData = attributes={"GlobalId": {"name": "GlobalId", "type": "IfcGloballyUniqueId", "is_enum": false, "enum_values": []}, "Description": {"... (+484 chars omitted),+1 more (map truncated)
  IfcType = 172
  Length = 250
  MoveBase = false
  MoveWithHost = false
  Nodes = (2) [(-1.05471e-15,1.36424e-15,0),(-1.05471e-15,1.36424e-15,3000)]
  NodesOffset = 0
  Normal = (0,0,0)
  PerimeterLength = 800
  Placement = pos=(9010,3350,6000) rot=(0,0,1;1.5708rad)
  PredefinedType = 0
  VerticalArea = 2400000
  Width = 150
FEATURE [Part::FeaturePython] Structure255  label="25x15 C058"  # Arch/BIM 172 (typed FeaturePython)
  FaceMaker = 0
  Height = 3000
  HorizontalArea = 37500
  IfcData = attributes={"GlobalId": {"name": "GlobalId", "type": "IfcGloballyUniqueId", "is_enum": false, "enum_values": []}, "Description": {"... (+484 chars omitted),+1 more (map truncated)
  IfcType = 172
  Length = 250
  MoveBase = false
  MoveWithHost = false
  Nodes = (2) [(-1.05471e-15,1.36424e-15,0),(-1.05471e-15,1.36424e-15,3000)]
  NodesOffset = 0
  Normal = (0,0,0)
  PerimeterLength = 800
  Placement = pos=(10560,3350,6000) rot=(0,0,1;1.5708rad)
  PredefinedType = 0
  VerticalArea = 2400000
  Width = 150
FEATURE [Part::FeaturePython] Structure256  label="25x15 C059"  # Arch/BIM 172 (typed FeaturePython)
  FaceMaker = 0
  Height = 3000
  HorizontalArea = 37500
  IfcData = attributes={"GlobalId": {"name": "GlobalId", "type": "IfcGloballyUniqueId", "is_enum": false, "enum_values": []}, "Description": {"... (+484 chars omitted),+1 more (map truncated)
  IfcType = 172
  Length = 250
  MoveBase = false
  MoveWithHost = false
  Nodes = (2) [(-1.05471e-15,1.36424e-15,0),(-1.05471e-15,1.36424e-15,3000)]
  NodesOffset = 0
  Normal = (0,0,0)
  PerimeterLength = 800
  Placement = pos=(13780,3350,6000) rot=(0,0,1;1.5708rad)
  PredefinedType = 0
  VerticalArea = 2400000
  Width = 150
FEATURE [Part::FeaturePython] Structure257  label="25x15 C060"  # Arch/BIM 172 (typed FeaturePython)
  FaceMaker = 0
  Height = 3000
  HorizontalArea = 37500
  IfcData = attributes={"GlobalId": {"name": "GlobalId", "type": "IfcGloballyUniqueId", "is_enum": false, "enum_values": []}, "Description": {"... (+484 chars omitted),+1 more (map truncated)
  IfcType = 172
  Length = 250
  MoveBase = false
  MoveWithHost = false
  Nodes = (2) [(-1.05471e-15,1.36424e-15,0),(-1.05471e-15,1.36424e-15,3000)]
  NodesOffset = 0
  Normal = (0,0,0)
  PerimeterLength = 800
  Placement = pos=(9010,9900,6000) rot=(0,0,1;0rad)
  PredefinedType = 0
  VerticalArea = 2400000
  Width = 150
FEATURE [Part::FeaturePython] Structure258  label="25x15 C061"  # Arch/BIM 172 (typed FeaturePython)
  FaceMaker = 0
  Height = 3000
  HorizontalArea = 37500
  IfcData = attributes={"GlobalId": {"name": "GlobalId", "type": "IfcGloballyUniqueId", "is_enum": false, "enum_values": []}, "Description": {"... (+484 chars omitted),+1 more (map truncated)
  IfcType = 172
  Length = 250
  MoveBase = false
  MoveWithHost = false
  Nodes = (2) [(-1.05471e-15,1.36424e-15,0),(-1.05471e-15,1.36424e-15,3000)]
  NodesOffset = 0
  Normal = (0,0,0)
  PerimeterLength = 800
  Placement = pos=(6160,9900,6000) rot=(0,0,1;0rad)
  PredefinedType = 0
  VerticalArea = 2400000
  Width = 150
FEATURE [Part::FeaturePython] Structure259  label="25x15 C062"  # Arch/BIM 172 (typed FeaturePython)
  FaceMaker = 0
  Height = 3000
  HorizontalArea = 37500
  IfcData = attributes={"GlobalId": {"name": "GlobalId", "type": "IfcGloballyUniqueId", "is_enum": false, "enum_values": []}, "Description": {"... (+484 chars omitted),+1 more (map truncated)
  IfcType = 172
  Length = 250
  MoveBase = false
  MoveWithHost = false
  Nodes = (2) [(-1.05471e-15,1.36424e-15,0),(-1.05471e-15,1.36424e-15,3000)]
  NodesOffset = 0
  Normal = (0,0,0)
  PerimeterLength = 800
  Placement = pos=(12010,9900,6000) rot=(0,0,1;0rad)
  PredefinedType = 0
  VerticalArea = 2400000
  Width = 150
FEATURE [Part::FeaturePython] Structure260  label="25x15 C063"  # Arch/BIM 172 (typed FeaturePython)
  FaceMaker = 0
  Height = 3000
  HorizontalArea = 37500
  IfcData = attributes={"GlobalId": {"name": "GlobalId", "type": "IfcGloballyUniqueId", "is_enum": false, "enum_values": []}, "Description": {"... (+484 chars omitted),+1 more (map truncated)
  IfcType = 172
  Length = 250
  MoveBase = false
  MoveWithHost = false
  Nodes = (2) [(-1.05471e-15,1.36424e-15,0),(-1.05471e-15,1.36424e-15,3000)]
  NodesOffset = 0
  Normal = (0,0,0)
  PerimeterLength = 800
  Placement = pos=(15210,9900,6000) rot=(0,0,1;0rad)
  PredefinedType = 0
  VerticalArea = 2400000
  Width = 150
FEATURE [App::GeometryPython] BuildingPart016  label="Columnas P2"  # Arch/BIM 172 (typed FeaturePython)
  Area = 0
  Group = -> [Structure240,Structure241,Structure244,Structure245,Structure246,Structure247,Structure248,Structure249,Structure250,Structure251,Structure252,Structure253,Structure254,Structure255,Structure256,Structure257,Structure258,Structure259,Structure260,Structure242,Structure243]
  Height = 0
  HeightPropagate = true
  IfcData = attributes={"GlobalId": {"name": "GlobalId", "type": "IfcGloballyUniqueId", "is_enum": false, "enum_values": []}, "Description": {"... (+484 chars omitted),+1 more (map truncated)
  IfcType = 172
  LevelOffset = 0
  PredefinedType = 0
FEATURE [Part::FeaturePython] Wall003  label="Tabique Ascensor P2"  # Arch/BIM 166 (typed FeaturePython)
  Align = 1
  Area = 24900000
  Base = -> Rectangle003
  BlockHeight = 0
  BlockLength = 0
  CountBroken = 0
  CountEntire = 0
  Face = 0
  Height = 3000
  HorizontalArea = 1155000
  IfcData = attributes={"GlobalId": {"name": "GlobalId", "type": "IfcGloballyUniqueId", "is_enum": false, "enum_values": []}, "Description": {"... (+533 chars omitted),+1 more (map truncated)
  IfcType = 166
  Joint = 0
  Length = 8300
  MakeBlocks = false
  MoveBase = false
  MoveWithHost = false
  Normal = (0,0,0)
  OffsetFirst = 0
  OffsetSecond = 0
  PerimeterLength = 8300
  Placement = pos=(0,0,6000) rot=(0,0,1;0rad)
  PredefinedType = 0
  VerticalArea = 46200000
  Width = 150
FEATURE [Part::FeaturePython] Structure261  label="V15x40 V161"  # Arch/BIM 7 (typed FeaturePython)
  FaceMaker = 0
  Height = 400
  HorizontalArea = 597000
  IfcData = attributes={"GlobalId": {"name": "GlobalId", "type": "IfcGloballyUniqueId", "is_enum": false, "enum_values": []}, "Description": {"... (+475 chars omitted),+1 more (map truncated)
  IfcType = 7
  Length = 3980
  MoveBase = false
  MoveWithHost = false
  Nodes = (2) [(-1.72563e-31,-1.42109e-15,-7.77156e-16),(3980,-1.42109e-15,-7.77156e-16)]
  NodesOffset = 0
  Normal = (0,0,0)
  PerimeterLength = 8260
  Placement = pos=(2055,9900,8800) rot=(0,0,1;0rad)
  PredefinedType = 0
  VerticalArea = 3.304e+06
  Width = 150
FEATURE [Part::FeaturePython] Structure262  label="V15x40 V162"  # Arch/BIM 7 (typed FeaturePython)
  FaceMaker = 0
  Height = 400
  HorizontalArea = 390000
  IfcData = attributes={"GlobalId": {"name": "GlobalId", "type": "IfcGloballyUniqueId", "is_enum": false, "enum_values": []}, "Description": {"... (+475 chars omitted),+1 more (map truncated)
  IfcType = 7
  Length = 2600
  MoveBase = false
  MoveWithHost = false
  Nodes = (2) [(-1.72563e-31,-1.42109e-15,-7.77156e-16),(2600,-1.42109e-15,-7.77156e-16)]
  NodesOffset = 0
  Normal = (0,0,0)
  PerimeterLength = 5500
  Placement = pos=(6285,9900,8800) rot=(0,0,1;0rad)
  PredefinedType = 0
  VerticalArea = 2200000
  Width = 150
FEATURE [Part::FeaturePython] Structure263  label="V15x40 V163"  # Arch/BIM 7 (typed FeaturePython)
  FaceMaker = 0
  Height = 400
  HorizontalArea = 412500
  IfcData = attributes={"GlobalId": {"name": "GlobalId", "type": "IfcGloballyUniqueId", "is_enum": false, "enum_values": []}, "Description": {"... (+475 chars omitted),+1 more (map truncated)
  IfcType = 7
  Length = 2750
  MoveBase = false
  MoveWithHost = false
  Nodes = (2) [(-1.72563e-31,-1.42109e-15,-7.77156e-16),(2750,-1.42109e-15,-7.77156e-16)]
  NodesOffset = 0
  Normal = (0,0,0)
  PerimeterLength = 5800
  Placement = pos=(9135,9900,8800) rot=(0,0,1;0rad)
  PredefinedType = 0
  VerticalArea = 2320000
  Width = 150
FEATURE [Part::FeaturePython] Structure264  label="V15x40 V164"  # Arch/BIM 7 (typed FeaturePython)
  FaceMaker = 0
  Height = 400
  HorizontalArea = 442500
  IfcData = attributes={"GlobalId": {"name": "GlobalId", "type": "IfcGloballyUniqueId", "is_enum": false, "enum_values": []}, "Description": {"... (+475 chars omitted),+1 more (map truncated)
  IfcType = 7
  Length = 2950
  MoveBase = false
  MoveWithHost = false
  Nodes = (2) [(-1.72563e-31,-1.42109e-15,-7.77156e-16),(2950,-1.42109e-15,-7.77156e-16)]
  NodesOffset = 0
  Normal = (0,0,0)
  PerimeterLength = 6200
  Placement = pos=(12135,9900,8800) rot=(0,0,1;0rad)
  PredefinedType = 0
  VerticalArea = 2.48e+06
  Width = 150
FEATURE [Part::FeaturePython] Structure265  label="V15x40 V165"  # Arch/BIM 7 (typed FeaturePython)
  FaceMaker = 0
  Height = 400
  HorizontalArea = 453750
  IfcData = attributes={"GlobalId": {"name": "GlobalId", "type": "IfcGloballyUniqueId", "is_enum": false, "enum_values": []}, "Description": {"... (+475 chars omitted),+1 more (map truncated)
  IfcType = 7
  Length = 3025
  MoveBase = false
  MoveWithHost = false
  Nodes = (2) [(-1.72563e-31,-1.42109e-15,-7.77156e-16),(3025,-1.42109e-15,-7.77156e-16)]
  NodesOffset = 0
  Normal = (0,0,0)
  PerimeterLength = 6350
  Placement = pos=(12085,8370,8800) rot=(0,0,1;0rad)
  PredefinedType = 0
  VerticalArea = 2.54e+06
  Width = 150
FEATURE [Part::FeaturePython] Structure266  label="V15x40 V166"  # Arch/BIM 7 (typed FeaturePython)
  FaceMaker = 0
  Height = 400
  HorizontalArea = 597000
  IfcData = attributes={"GlobalId": {"name": "GlobalId", "type": "IfcGloballyUniqueId", "is_enum": false, "enum_values": []}, "Description": {"... (+475 chars omitted),+1 more (map truncated)
  IfcType = 7
  Length = 3980
  MoveBase = false
  MoveWithHost = false
  Nodes = (2) [(-1.72563e-31,-1.42109e-15,-7.77156e-16),(3980,-1.42109e-15,-7.77156e-16)]
  NodesOffset = 0
  Normal = (0,0,0)
  PerimeterLength = 8260
  Placement = pos=(2055,6640,8800) rot=(0,0,1;0rad)
  PredefinedType = 0
  VerticalArea = 3.304e+06
  Width = 150
FEATURE [Part::FeaturePython] Structure267  label="V15x40 V167"  # Arch/BIM 7 (typed FeaturePython)
  FaceMaker = 0
  Height = 400
  HorizontalArea = 397500
  IfcData = attributes={"GlobalId": {"name": "GlobalId", "type": "IfcGloballyUniqueId", "is_enum": false, "enum_values": []}, "Description": {"... (+475 chars omitted),+1 more (map truncated)
  IfcType = 7
  Length = 2650
  MoveBase = false
  MoveWithHost = false
  Nodes = (2) [(-1.72563e-31,-1.42109e-15,-7.77156e-16),(2650,-1.42109e-15,-7.77156e-16)]
  NodesOffset = 0
  Normal = (0,0,0)
  PerimeterLength = 5600
  Placement = pos=(6285,6640,8800) rot=(0,0,1;0rad)
  PredefinedType = 0
  VerticalArea = 2240000
  Width = 150
FEATURE [Part::FeaturePython] Structure268  label="V15x40 V168"  # Arch/BIM 7 (typed FeaturePython)
  FaceMaker = 0
  Height = 400
  HorizontalArea = 210000
  IfcData = attributes={"GlobalId": {"name": "GlobalId", "type": "IfcGloballyUniqueId", "is_enum": false, "enum_values": []}, "Description": {"... (+475 chars omitted),+1 more (map truncated)
  IfcType = 7
  Length = 1400
  MoveBase = false
  MoveWithHost = false
  Nodes = (2) [(-1.72563e-31,-1.42109e-15,-7.77156e-16),(1400,-1.42109e-15,-7.77156e-16)]
  NodesOffset = 0
  Normal = (0,0,0)
  PerimeterLength = 3100
  Placement = pos=(9085,6640,8800) rot=(0,0,1;0rad)
  PredefinedType = 0
  VerticalArea = 1240000
  Width = 150
FEATURE [Part::FeaturePython] Structure269  label="V15x40 V169"  # Arch/BIM 7 (typed FeaturePython)
  FaceMaker = 0
  Height = 400
  HorizontalArea = 235500
  IfcData = attributes={"GlobalId": {"name": "GlobalId", "type": "IfcGloballyUniqueId", "is_enum": false, "enum_values": []}, "Description": {"... (+475 chars omitted),+1 more (map truncated)
  IfcType = 7
  Length = 1570
  MoveBase = false
  MoveWithHost = false
  Nodes = (2) [(-1.72563e-31,-1.42109e-15,-7.77156e-16),(1570,-1.42109e-15,-7.77156e-16)]
  NodesOffset = 0
  Normal = (0,0,0)
  PerimeterLength = 3440
  Placement = pos=(13655,5970,8800) rot=(0,0,1;3.14159rad)
  PredefinedType = 0
  VerticalArea = 1.376e+06
  Width = 150
FEATURE [Part::FeaturePython] Structure270  label="V15x40 V170"  # Arch/BIM 7 (typed FeaturePython)
  FaceMaker = 0
  Height = 400
  HorizontalArea = 177000
  IfcData = attributes={"GlobalId": {"name": "GlobalId", "type": "IfcGloballyUniqueId", "is_enum": false, "enum_values": []}, "Description": {"... (+475 chars omitted),+1 more (map truncated)
  IfcType = 7
  Length = 1180
  MoveBase = false
  MoveWithHost = false
  Nodes = (2) [(-1.72563e-31,-1.42109e-15,-7.77156e-16),(1180,-1.42109e-15,-7.77156e-16)]
  NodesOffset = 0
  Normal = (0,0,0)
  PerimeterLength = 2660
  Placement = pos=(13905,5970,8800) rot=(0,0,1;0rad)
  PredefinedType = 0
  VerticalArea = 1064000
  Width = 150
FEATURE [Part::FeaturePython] Structure271  label="V15x40 V171"  # Arch/BIM 7 (typed FeaturePython)
  FaceMaker = 0
  Height = 400
  HorizontalArea = 597000
  IfcData = attributes={"GlobalId": {"name": "GlobalId", "type": "IfcGloballyUniqueId", "is_enum": false, "enum_values": []}, "Description": {"... (+475 chars omitted),+1 more (map truncated)
  IfcType = 7
  Length = 3980
  MoveBase = false
  MoveWithHost = false
  Nodes = (2) [(-1.72563e-31,-1.42109e-15,-7.77156e-16),(3980,-1.42109e-15,-7.77156e-16)]
  NodesOffset = 0
  Normal = (0,0,0)
  PerimeterLength = 8260
  Placement = pos=(2055,3350,8800) rot=(0,0,1;0rad)
  PredefinedType = 0
  VerticalArea = 3.304e+06
  Width = 150
FEATURE [Part::FeaturePython] Structure272  label="V15x40 V172"  # Arch/BIM 7 (typed FeaturePython)
  FaceMaker = 0
  Height = 400
  HorizontalArea = 397500
  IfcData = attributes={"GlobalId": {"name": "GlobalId", "type": "IfcGloballyUniqueId", "is_enum": false, "enum_values": []}, "Description": {"... (+475 chars omitted),+1 more (map truncated)
  IfcType = 7
  Length = 2650
  MoveBase = false
  MoveWithHost = false
  Nodes = (2) [(-1.72563e-31,-1.42109e-15,-7.77156e-16),(2650,-1.42109e-15,-7.77156e-16)]
  NodesOffset = 0
  Normal = (0,0,0)
  PerimeterLength = 5600
  Placement = pos=(6285,3350,8800) rot=(0,0,1;0rad)
  PredefinedType = 0
  VerticalArea = 2240000
  Width = 150
FEATURE [Part::FeaturePython] Structure273  label="V15x40 V173"  # Arch/BIM 7 (typed FeaturePython)
  FaceMaker = 0
  Height = 400
  HorizontalArea = 210000
  IfcData = attributes={"GlobalId": {"name": "GlobalId", "type": "IfcGloballyUniqueId", "is_enum": false, "enum_values": []}, "Description": {"... (+475 chars omitted),+1 more (map truncated)
  IfcType = 7
  Length = 1400
  MoveBase = false
  MoveWithHost = false
  Nodes = (2) [(-1.72563e-31,-1.42109e-15,-7.77156e-16),(1400,-1.42109e-15,-7.77156e-16)]
  NodesOffset = 0
  Normal = (0,0,0)
  PerimeterLength = 3100
  Placement = pos=(9085,3350,8800) rot=(0,0,1;0rad)
  PredefinedType = 0
  VerticalArea = 1240000
  Width = 150
FEATURE [Part::FeaturePython] Structure274  label="V15x40 V174"  # Arch/BIM 7 (typed FeaturePython)
  FaceMaker = 0
  Height = 400
  HorizontalArea = 460500
  IfcData = attributes={"GlobalId": {"name": "GlobalId", "type": "IfcGloballyUniqueId", "is_enum": false, "enum_values": []}, "Description": {"... (+475 chars omitted),+1 more (map truncated)
  IfcType = 7
  Length = 3070
  MoveBase = false
  MoveWithHost = false
  Nodes = (2) [(-1.72563e-31,-1.42109e-15,-7.77156e-16),(3070,-1.42109e-15,-7.77156e-16)]
  NodesOffset = 0
  Normal = (0,0,0)
  PerimeterLength = 6440
  Placement = pos=(10635,3350,8800) rot=(0,0,1;0rad)
  PredefinedType = 0
  VerticalArea = 2.576e+06
  Width = 150
FEATURE [Part::FeaturePython] Structure275  label="V15x40 V175"  # Arch/BIM 7 (typed FeaturePython)
  FaceMaker = 0
  Height = 400
  HorizontalArea = 597000
  IfcData = attributes={"GlobalId": {"name": "GlobalId", "type": "IfcGloballyUniqueId", "is_enum": false, "enum_values": []}, "Description": {"... (+475 chars omitted),+1 more (map truncated)
  IfcType = 7
  Length = 3980
  MoveBase = false
  MoveWithHost = false
  Nodes = (2) [(-1.72563e-31,-1.42109e-15,-7.77156e-16),(3980,-1.42109e-15,-7.77156e-16)]
  NodesOffset = 0
  Normal = (0,0,0)
  PerimeterLength = 8260
  Placement = pos=(2055,100,8800) rot=(0,0,1;0rad)
  PredefinedType = 0
  VerticalArea = 3.304e+06
  Width = 150
FEATURE [Part::FeaturePython] Structure276  label="V15x40 V176"  # Arch/BIM 7 (typed FeaturePython)
  FaceMaker = 0
  Height = 400
  HorizontalArea = 390000
  IfcData = attributes={"GlobalId": {"name": "GlobalId", "type": "IfcGloballyUniqueId", "is_enum": false, "enum_values": []}, "Description": {"... (+475 chars omitted),+1 more (map truncated)
  IfcType = 7
  Length = 2600
  MoveBase = false
  MoveWithHost = false
  Nodes = (2) [(-1.72563e-31,-1.42109e-15,-7.77156e-16),(2600,-1.42109e-15,-7.77156e-16)]
  NodesOffset = 0
  Normal = (0,0,0)
  PerimeterLength = 5500
  Placement = pos=(6285,100,8800) rot=(0,0,1;0rad)
  PredefinedType = 0
  VerticalArea = 2200000
  Width = 150
FEATURE [Part::FeaturePython] Structure277  label="V15x40 V177"  # Arch/BIM 7 (typed FeaturePython)
  FaceMaker = 0
  Height = 400
  HorizontalArea = 195000
  IfcData = attributes={"GlobalId": {"name": "GlobalId", "type": "IfcGloballyUniqueId", "is_enum": false, "enum_values": []}, "Description": {"... (+475 chars omitted),+1 more (map truncated)
  IfcType = 7
  Length = 1300
  MoveBase = false
  MoveWithHost = false
  Nodes = (2) [(-1.72563e-31,-1.42109e-15,-7.77156e-16),(1300,-1.42109e-15,-7.77156e-16)]
  NodesOffset = 0
  Normal = (0,0,0)
  PerimeterLength = 2900
  Placement = pos=(9135,100,8800) rot=(0,0,1;0rad)
  PredefinedType = 0
  VerticalArea = 1160000
  Width = 150
FEATURE [Part::FeaturePython] Structure278  label="V15x40 V178"  # Arch/BIM 7 (typed FeaturePython)
  FaceMaker = 0
  Height = 400
  HorizontalArea = 445500
  IfcData = attributes={"GlobalId": {"name": "GlobalId", "type": "IfcGloballyUniqueId", "is_enum": false, "enum_values": []}, "Description": {"... (+475 chars omitted),+1 more (map truncated)
  IfcType = 7
  Length = 2970
  MoveBase = false
  MoveWithHost = false
  Nodes = (2) [(-1.72563e-31,-1.42109e-15,-7.77156e-16),(2970,-1.42109e-15,-7.77156e-16)]
  NodesOffset = 0
  Normal = (0,0,0)
  PerimeterLength = 6240
  Placement = pos=(10685,100,8800) rot=(0,0,1;0rad)
  PredefinedType = 0
  VerticalArea = 2.496e+06
  Width = 150
FEATURE [Part::FeaturePython] Structure279  label="V15x40 V179"  # Arch/BIM 7 (typed FeaturePython)
  FaceMaker = 0
  Height = 400
  HorizontalArea = 465000
  IfcData = attributes={"GlobalId": {"name": "GlobalId", "type": "IfcGloballyUniqueId", "is_enum": false, "enum_values": []}, "Description": {"... (+475 chars omitted),+1 more (map truncated)
  IfcType = 7
  Length = 3100
  MoveBase = false
  MoveWithHost = false
  Nodes = (2) [(-1.72563e-31,-1.42109e-15,-7.77156e-16),(3100,-1.42109e-15,-7.77156e-16)]
  NodesOffset = 0
  Normal = (0,0,0)
  PerimeterLength = 6500
  Placement = pos=(6160,3275,8800) rot=(0,0,-1;1.5708rad)
  PredefinedType = 0
  VerticalArea = 2.6e+06
  Width = 150
FEATURE [Part::FeaturePython] Structure280  label="V15x40 V180"  # Arch/BIM 7 (typed FeaturePython)
  FaceMaker = 0
  Height = 400
  HorizontalArea = 471000
  IfcData = attributes={"GlobalId": {"name": "GlobalId", "type": "IfcGloballyUniqueId", "is_enum": false, "enum_values": []}, "Description": {"... (+475 chars omitted),+1 more (map truncated)
  IfcType = 7
  Length = 3140
  MoveBase = false
  MoveWithHost = false
  Nodes = (2) [(-1.72563e-31,-1.42109e-15,-7.77156e-16),(3140,-1.42109e-15,-7.77156e-16)]
  NodesOffset = 0
  Normal = (0,0,0)
  PerimeterLength = 6580
  Placement = pos=(6160,6565,8800) rot=(0,0,-1;1.5708rad)
  PredefinedType = 0
  VerticalArea = 2.632e+06
  Width = 150
FEATURE [Part::FeaturePython] Structure281  label="V15x40 V181"  # Arch/BIM 7 (typed FeaturePython)
  FaceMaker = 0
  Height = 400
  HorizontalArea = 466500
  IfcData = attributes={"GlobalId": {"name": "GlobalId", "type": "IfcGloballyUniqueId", "is_enum": false, "enum_values": []}, "Description": {"... (+475 chars omitted),+1 more (map truncated)
  IfcType = 7
  Length = 3110
  MoveBase = false
  MoveWithHost = false
  Nodes = (2) [(-1.72563e-31,-1.42109e-15,-7.77156e-16),(3110,-1.42109e-15,-7.77156e-16)]
  NodesOffset = 0
  Normal = (0,0,0)
  PerimeterLength = 6520
  Placement = pos=(6160,9825,8800) rot=(0,0,-1;1.5708rad)
  PredefinedType = 0
  VerticalArea = 2.608e+06
  Width = 150
FEATURE [Part::FeaturePython] Structure282  label="V15x40 V182"  # Arch/BIM 7 (typed FeaturePython)
  FaceMaker = 0
  Height = 400
  HorizontalArea = 457500
  IfcData = attributes={"GlobalId": {"name": "GlobalId", "type": "IfcGloballyUniqueId", "is_enum": false, "enum_values": []}, "Description": {"... (+475 chars omitted),+1 more (map truncated)
  IfcType = 7
  Length = 3050
  MoveBase = false
  MoveWithHost = false
  Nodes = (2) [(-1.72563e-31,-1.42109e-15,-7.77156e-16),(3050,-1.42109e-15,-7.77156e-16)]
  NodesOffset = 0
  Normal = (0,0,0)
  PerimeterLength = 6400
  Placement = pos=(9010,3225,8800) rot=(0,0,-1;1.5708rad)
  PredefinedType = 0
  VerticalArea = 2.56e+06
  Width = 150
FEATURE [Part::FeaturePython] Structure283  label="V15x40 V183"  # Arch/BIM 7 (typed FeaturePython)
  FaceMaker = 0
  Height = 400
  HorizontalArea = 456000
  IfcData = attributes={"GlobalId": {"name": "GlobalId", "type": "IfcGloballyUniqueId", "is_enum": false, "enum_values": []}, "Description": {"... (+475 chars omitted),+1 more (map truncated)
  IfcType = 7
  Length = 3040
  MoveBase = false
  MoveWithHost = false
  Nodes = (2) [(-1.72563e-31,-1.42109e-15,-7.77156e-16),(3040,-1.42109e-15,-7.77156e-16)]
  NodesOffset = 0
  Normal = (0,0,0)
  PerimeterLength = 6380
  Placement = pos=(9010,6515,8800) rot=(0,0,-1;1.5708rad)
  PredefinedType = 0
  VerticalArea = 2.552e+06
  Width = 150
FEATURE [Part::FeaturePython] Structure284  label="V15x40 V184"  # Arch/BIM 7 (typed FeaturePython)
  FaceMaker = 0
  Height = 400
  HorizontalArea = 459000
  IfcData = attributes={"GlobalId": {"name": "GlobalId", "type": "IfcGloballyUniqueId", "is_enum": false, "enum_values": []}, "Description": {"... (+475 chars omitted),+1 more (map truncated)
  IfcType = 7
  Length = 3060
  MoveBase = false
  MoveWithHost = false
  Nodes = (2) [(-1.72563e-31,-1.42109e-15,-7.77156e-16),(3060,-1.42109e-15,-7.77156e-16)]
  NodesOffset = 0
  Normal = (0,0,0)
  PerimeterLength = 6420
  Placement = pos=(9010,9825,8800) rot=(0,0,-1;1.5708rad)
  PredefinedType = 0
  VerticalArea = 2.568e+06
  Width = 150
FEATURE [Part::FeaturePython] Structure285  label="V15x40 V185"  # Arch/BIM 7 (typed FeaturePython)
  FaceMaker = 0
  Height = 400
  HorizontalArea = 457500
  IfcData = attributes={"GlobalId": {"name": "GlobalId", "type": "IfcGloballyUniqueId", "is_enum": false, "enum_values": []}, "Description": {"... (+475 chars omitted),+1 more (map truncated)
  IfcType = 7
  Length = 3050
  MoveBase = false
  MoveWithHost = false
  Nodes = (2) [(-1.72563e-31,-1.42109e-15,-7.77156e-16),(3050,-1.42109e-15,-7.77156e-16)]
  NodesOffset = 0
  Normal = (0,0,0)
  PerimeterLength = 6400
  Placement = pos=(10560,3225,8800) rot=(0,0,-1;1.5708rad)
  PredefinedType = 0
  VerticalArea = 2.56e+06
  Width = 150
FEATURE [Part::FeaturePython] Structure286  label="V15x40 V186"  # Arch/BIM 7 (typed FeaturePython)
  FaceMaker = 0
  Height = 400
  HorizontalArea = 363000
  IfcData = attributes={"GlobalId": {"name": "GlobalId", "type": "IfcGloballyUniqueId", "is_enum": false, "enum_values": []}, "Description": {"... (+475 chars omitted),+1 more (map truncated)
  IfcType = 7
  Length = 2420
  MoveBase = false
  MoveWithHost = false
  Nodes = (2) [(-1.72563e-31,-1.42109e-15,-7.77156e-16),(2420,-1.42109e-15,-7.77156e-16)]
  NodesOffset = 0
  Normal = (0,0,0)
  PerimeterLength = 5140
  Placement = pos=(10560,3475,8800) rot=(0,0,1;1.5708rad)
  PredefinedType = 0
  VerticalArea = 2056000
  Width = 150
FEATURE [Part::FeaturePython] Structure287  label="V15x40 V187"  # Arch/BIM 7 (typed FeaturePython)
  FaceMaker = 0
  Height = 400
  HorizontalArea = 207000
  IfcData = attributes={"GlobalId": {"name": "GlobalId", "type": "IfcGloballyUniqueId", "is_enum": false, "enum_values": []}, "Description": {"... (+475 chars omitted),+1 more (map truncated)
  IfcType = 7
  Length = 1380
  MoveBase = false
  MoveWithHost = false
  Nodes = (2) [(-1.72563e-31,-1.42109e-15,-7.77156e-16),(1380,-1.42109e-15,-7.77156e-16)]
  NodesOffset = 0
  Normal = (0,0,0)
  PerimeterLength = 3060
  Placement = pos=(10560,8445,8800) rot=(0,0,1;1.5708rad)
  PredefinedType = 0
  VerticalArea = 1224000
  Width = 150
FEATURE [Part::FeaturePython] Structure288  label="V15x40 V188"  # Arch/BIM 7 (typed FeaturePython)
  FaceMaker = 0
  Height = 400
  HorizontalArea = 207000
  IfcData = attributes={"GlobalId": {"name": "GlobalId", "type": "IfcGloballyUniqueId", "is_enum": false, "enum_values": []}, "Description": {"... (+475 chars omitted),+1 more (map truncated)
  IfcType = 7
  Length = 1380
  MoveBase = false
  MoveWithHost = false
  Nodes = (2) [(-1.72563e-31,-1.42109e-15,-7.77156e-16),(1380,-1.42109e-15,-7.77156e-16)]
  NodesOffset = 0
  Normal = (0,0,0)
  PerimeterLength = 3060
  Placement = pos=(12010,9825,8800) rot=(0,0,-1;1.5708rad)
  PredefinedType = 0
  VerticalArea = 1224000
  Width = 150
FEATURE [Part::FeaturePython] Structure289  label="V20x40 V142"  # Arch/BIM 7 (typed FeaturePython)
  FaceMaker = 0
  Height = 400
  HorizontalArea = 615000
  IfcData = attributes={"GlobalId": {"name": "GlobalId", "type": "IfcGloballyUniqueId", "is_enum": false, "enum_values": []}, "Description": {"... (+475 chars omitted),+1 more (map truncated)
  IfcType = 7
  Length = 3075
  MoveBase = false
  MoveWithHost = false
  Nodes = (2) [(-1.72563e-31,0,-7.77156e-16),(3075,0,-7.77156e-16)]
  NodesOffset = 0
  Normal = (0,0,0)
  PerimeterLength = 6550
  Placement = pos=(1930,3250,8800) rot=(0,0,-1;1.5708rad)
  PredefinedType = 0
  VerticalArea = 2.62e+06
  Width = 200
FEATURE [Part::FeaturePython] Structure290  label="V20x40 V143"  # Arch/BIM 7 (typed FeaturePython)
  FaceMaker = 0
  Height = 400
  HorizontalArea = 618000
  IfcData = attributes={"GlobalId": {"name": "GlobalId", "type": "IfcGloballyUniqueId", "is_enum": false, "enum_values": []}, "Description": {"... (+475 chars omitted),+1 more (map truncated)
  IfcType = 7
  Length = 3090
  MoveBase = false
  MoveWithHost = false
  Nodes = (2) [(-1.72563e-31,0,-7.77156e-16),(3090,0,-7.77156e-16)]
  NodesOffset = 0
  Normal = (0,0,0)
  PerimeterLength = 6580
  Placement = pos=(1930,6540,8800) rot=(0,0,-1;1.5708rad)
  PredefinedType = 0
  VerticalArea = 2.632e+06
  Width = 200
FEATURE [Part::FeaturePython] Structure291  label="V20x40 V144"  # Arch/BIM 7 (typed FeaturePython)
  FaceMaker = 0
  Height = 400
  HorizontalArea = 617000
  IfcData = attributes={"GlobalId": {"name": "GlobalId", "type": "IfcGloballyUniqueId", "is_enum": false, "enum_values": []}, "Description": {"... (+475 chars omitted),+1 more (map truncated)
  IfcType = 7
  Length = 3085
  MoveBase = false
  MoveWithHost = false
  Nodes = (2) [(-1.72563e-31,0,-7.77156e-16),(3085,0,-7.77156e-16)]
  NodesOffset = 0
  Normal = (0,0,0)
  PerimeterLength = 6570
  Placement = pos=(1930,9825,8800) rot=(0,0,-1;1.5708rad)
  PredefinedType = 0
  VerticalArea = 2.628e+06
  Width = 200
FEATURE [Part::FeaturePython] Structure292  label="V20x40 V145"  # Arch/BIM 7 (typed FeaturePython)
  FaceMaker = 0
  Height = 400
  HorizontalArea = 635000
  IfcData = attributes={"GlobalId": {"name": "GlobalId", "type": "IfcGloballyUniqueId", "is_enum": false, "enum_values": []}, "Description": {"... (+475 chars omitted),+1 more (map truncated)
  IfcType = 7
  Length = 3175
  MoveBase = false
  MoveWithHost = false
  Nodes = (2) [(-1.72563e-31,0,-7.77156e-16),(3175,0,-7.77156e-16)]
  NodesOffset = 0
  Normal = (0,0,0)
  PerimeterLength = 6750
  Placement = pos=(13780,175,8800) rot=(0,0,1;1.5708rad)
  PredefinedType = 0
  VerticalArea = 2.7e+06
  Width = 200
FEATURE [Part::FeaturePython] Structure293  label="V20x40 V146"  # Arch/BIM 7 (typed FeaturePython)
  FaceMaker = 0
  Height = 400
  HorizontalArea = 509000
  IfcData = attributes={"GlobalId": {"name": "GlobalId", "type": "IfcGloballyUniqueId", "is_enum": false, "enum_values": []}, "Description": {"... (+475 chars omitted),+1 more (map truncated)
  IfcType = 7
  Length = 2545
  MoveBase = false
  MoveWithHost = false
  Nodes = (2) [(-1.72563e-31,0,-7.77156e-16),(2545,0,-7.77156e-16)]
  NodesOffset = 0
  Normal = (0,0,0)
  PerimeterLength = 5490
  Placement = pos=(13780,3350,8800) rot=(0,0,1;1.5708rad)
  PredefinedType = 0
  VerticalArea = 2196000
  Width = 200
FEATURE [Part::FeaturePython] Structure294  label="V20x40 V147"  # Arch/BIM 7 (typed FeaturePython)
  FaceMaker = 0
  Height = 400
  HorizontalArea = 756000
  IfcData = attributes={"GlobalId": {"name": "GlobalId", "type": "IfcGloballyUniqueId", "is_enum": false, "enum_values": []}, "Description": {"... (+475 chars omitted),+1 more (map truncated)
  IfcType = 7
  Length = 3780
  MoveBase = false
  MoveWithHost = false
  Nodes = (2) [(-1.72563e-31,0,-7.77156e-16),(3780,0,-7.77156e-16)]
  NodesOffset = 0
  Normal = (0,0,0)
  PerimeterLength = 7960
  Placement = pos=(15210,6045,8800) rot=(0,0,1;1.5708rad)
  PredefinedType = 0
  VerticalArea = 3.184e+06
  Width = 200
FEATURE [Part::FeaturePython] Structure295  label="L135"  # Arch/BIM 172 (typed FeaturePython)
  Base = -> Rectangle004
  FaceMaker = 0
  Height = 150
  HorizontalArea = 12611050
  IfcData = attributes={"GlobalId": {"name": "GlobalId", "type": "IfcGloballyUniqueId", "is_enum": false, "enum_values": []}, "Description": {"... (+484 chars omitted),+1 more (map truncated)
  IfcType = 172
  Length = 0
  MoveBase = false
  MoveWithHost = false
  Nodes = (2) [(4057.5,8270,3000),(4057.5,8270,2850)]
  NodesOffset = 0
  Normal = (0,0,-1)
  PerimeterLength = 14330
  Placement = pos=(0,0,6000) rot=(0,0,1;0rad)
  PredefinedType = 0
  VerticalArea = 2149500
  Width = 150
FEATURE [Part::FeaturePython] Structure296  label="L136"  # Arch/BIM 172 (typed FeaturePython)
  Base = -> Rectangle005
  FaceMaker = 0
  Height = 150
  HorizontalArea = 12732700
  IfcData = attributes={"GlobalId": {"name": "GlobalId", "type": "IfcGloballyUniqueId", "is_enum": false, "enum_values": []}, "Description": {"... (+484 chars omitted),+1 more (map truncated)
  IfcType = 172
  Length = 0
  MoveBase = false
  MoveWithHost = false
  Nodes = (2) [(4057.5,4995,3000),(4057.5,4995,2850)]
  NodesOffset = 0
  Normal = (0,0,-1)
  PerimeterLength = 14390
  Placement = pos=(0,0,6000) rot=(0,0,1;0rad)
  PredefinedType = 0
  VerticalArea = 2158500
  Width = 150
FEATURE [Part::FeaturePython] Structure297  label="L137"  # Arch/BIM 172 (typed FeaturePython)
  Base = -> Rectangle006
  FaceMaker = 0
  Height = 150
  HorizontalArea = 1.25705e+07
  IfcData = attributes={"GlobalId": {"name": "GlobalId", "type": "IfcGloballyUniqueId", "is_enum": false, "enum_values": []}, "Description": {"... (+484 chars omitted),+1 more (map truncated)
  IfcType = 172
  Length = 0
  MoveBase = false
  MoveWithHost = false
  Nodes = (2) [(4057.5,1725,3000),(4057.5,1725,2850)]
  NodesOffset = 0
  Normal = (0,0,-1)
  PerimeterLength = 14310
  Placement = pos=(0,0,6000) rot=(0,0,1;0rad)
  PredefinedType = 0
  VerticalArea = 2146500
  Width = 150
FEATURE [Part::FeaturePython] Structure298  label="V15x40 V102a002"  # Arch/BIM 7 (typed FeaturePython)
  FaceMaker = 0
  Height = 400
  HorizontalArea = 405000
  IfcData = attributes={"GlobalId": {"name": "GlobalId", "type": "IfcGloballyUniqueId", "is_enum": false, "enum_values": []}, "Description": {"... (+475 chars omitted),+1 more (map truncated)
  IfcType = 7
  Length = 2700
  MoveBase = false
  MoveWithHost = false
  Nodes = (2) [(-1.72563e-31,-1.42109e-15,-7.77156e-16),(2700,-1.42109e-15,-7.77156e-16)]
  NodesOffset = 0
  Normal = (0,0,0)
  PerimeterLength = 5700
  Placement = pos=(8935,8295,8800) rot=(0,0,1;3.14159rad)
  PredefinedType = 0
  VerticalArea = 2.28e+06
  Width = 150
FEATURE [Part::FeaturePython] Structure299  label="V15x40 V107a002"  # Arch/BIM 7 (typed FeaturePython)
  FaceMaker = 0
  Height = 400
  HorizontalArea = 405000
  IfcData = attributes={"GlobalId": {"name": "GlobalId", "type": "IfcGloballyUniqueId", "is_enum": false, "enum_values": []}, "Description": {"... (+475 chars omitted),+1 more (map truncated)
  IfcType = 7
  Length = 2700
  MoveBase = false
  MoveWithHost = false
  Nodes = (2) [(-1.72563e-31,-1.42109e-15,-7.77156e-16),(2700,-1.42109e-15,-7.77156e-16)]
  NodesOffset = 0
  Normal = (0,0,0)
  PerimeterLength = 5700
  Placement = pos=(8935,4995,8800) rot=(0,0,1;3.14159rad)
  PredefinedType = 0
  VerticalArea = 2.28e+06
  Width = 150
FEATURE [Part::FeaturePython] Structure300  label="V15x40 V112a002"  # Arch/BIM 7 (typed FeaturePython)
  FaceMaker = 0
  Height = 400
  HorizontalArea = 405000
  IfcData = attributes={"GlobalId": {"name": "GlobalId", "type": "IfcGloballyUniqueId", "is_enum": false, "enum_values": []}, "Description": {"... (+475 chars omitted),+1 more (map truncated)
  IfcType = 7
  Length = 2700
  MoveBase = false
  MoveWithHost = false
  Nodes = (2) [(-1.72563e-31,-1.42109e-15,-7.77156e-16),(2700,-1.42109e-15,-7.77156e-16)]
  NodesOffset = 0
  Normal = (0,0,0)
  PerimeterLength = 5700
  Placement = pos=(8935,1700,8800) rot=(0,0,1;3.14159rad)
  PredefinedType = 0
  VerticalArea = 2.28e+06
  Width = 150
FEATURE [Part::FeaturePython] Structure301  label="V15x40 V130a002"  # Arch/BIM 7 (typed FeaturePython)
  FaceMaker = 0
  Height = 400
  HorizontalArea = 370500
  IfcData = attributes={"GlobalId": {"name": "GlobalId", "type": "IfcGloballyUniqueId", "is_enum": false, "enum_values": []}, "Description": {"... (+475 chars omitted),+1 more (map truncated)
  IfcType = 7
  Length = 2470
  MoveBase = false
  MoveWithHost = false
  Nodes = (2) [(-1.72563e-31,-1.42109e-15,-7.77156e-16),(2470,-1.42109e-15,-7.77156e-16)]
  NodesOffset = 0
  Normal = (0,0,0)
  PerimeterLength = 5240
  Placement = pos=(12010,3425,8800) rot=(0,0,1;1.5708rad)
  PredefinedType = 0
  VerticalArea = 2096000
  Width = 150
FEATURE [App::GeometryPython] BuildingPart017  label="Vigas sobre P2"  # Arch/BIM 172 (typed FeaturePython)
  Area = 0
  Group = -> [Structure298,Structure299,Structure300,Structure301,Structure261,Structure262,Structure263,Structure264,Structure265,Structure266,Structure267,Structure268,Structure269,Structure270,Structure271,Structure272,Structure273,Structure274,Structure275,Structure276,Structure277,Structure278,Structure279,Structure280,Structure281,Structure282,Structure283,Structure284,Structure285,Structure286,+8 more]
  Height = 0
  HeightPropagate = true
  IfcData = attributes={"GlobalId": {"name": "GlobalId", "type": "IfcGloballyUniqueId", "is_enum": false, "enum_values": []}, "Description": {"... (+484 chars omitted),+1 more (map truncated)
  IfcType = 172
  LevelOffset = 0
  PredefinedType = 0
FEATURE [Part::FeaturePython] Structure302  label="L138"  # Arch/BIM 172 (typed FeaturePython)
  Base = -> Rectangle014
  FaceMaker = 0
  Height = 150
  HorizontalArea = 3928500
  IfcData = attributes={"GlobalId": {"name": "GlobalId", "type": "IfcGloballyUniqueId", "is_enum": false, "enum_values": []}, "Description": {"... (+484 chars omitted),+1 more (map truncated)
  IfcType = 172
  Length = 0
  MoveBase = false
  MoveWithHost = false
  Nodes = (2) [(7585,9097.5,3000),(7585,9097.5,2850)]
  NodesOffset = 0
  Normal = (0,0,-1)
  PerimeterLength = 8310
  Placement = pos=(0,0,6000) rot=(0,0,1;0rad)
  PredefinedType = 0
  VerticalArea = 1246500
  Width = 150
FEATURE [Part::FeaturePython] Structure303  label="L139"  # Arch/BIM 172 (typed FeaturePython)
  Base = -> Wire
  FaceMaker = 0
  Height = 150
  HorizontalArea = 3.9285e+06
  IfcData = attributes={"GlobalId": {"name": "GlobalId", "type": "IfcGloballyUniqueId", "is_enum": false, "enum_values": []}, "Description": {"... (+484 chars omitted),+1 more (map truncated)
  IfcType = 172
  Length = 0
  MoveBase = false
  MoveWithHost = false
  Nodes = (2) [(7543.76,7449.37,3000),(7543.76,7449.37,2850)]
  NodesOffset = 0
  Normal = (0,0,-1)
  PerimeterLength = 8410
  Placement = pos=(0,0,5850) rot=(0,0,1;0rad)
  PredefinedType = 0
  VerticalArea = 1261500
  Width = 150
FEATURE [Part::FeaturePython] Structure304  label="L140"  # Arch/BIM 172 (typed FeaturePython)
  Base = -> Wire001
  FaceMaker = 0
  Height = 150
  HorizontalArea = 3.90134e+06
  IfcData = attributes={"GlobalId": {"name": "GlobalId", "type": "IfcGloballyUniqueId", "is_enum": false, "enum_values": []}, "Description": {"... (+484 chars omitted),+1 more (map truncated)
  IfcType = 172
  Length = 0
  MoveBase = false
  MoveWithHost = false
  Nodes = (2) [(7543.46,5835.61,3000),(7543.46,5835.61,2850)]
  NodesOffset = 0
  Normal = (0,0,-1)
  PerimeterLength = 8389.89
  Placement = pos=(0,0,5850) rot=(0,0,1;0rad)
  PredefinedType = 0
  VerticalArea = 1.25848e+06
  Width = 150
FEATURE [Part::FeaturePython] Structure305  label="L141"  # Arch/BIM 172 (typed FeaturePython)
  Base = -> Rectangle015
  FaceMaker = 0
  Height = 150
  HorizontalArea = 4.0365e+06
  IfcData = attributes={"GlobalId": {"name": "GlobalId", "type": "IfcGloballyUniqueId", "is_enum": false, "enum_values": []}, "Description": {"... (+484 chars omitted),+1 more (map truncated)
  IfcType = 172
  Length = 0
  MoveBase = false
  MoveWithHost = false
  Nodes = (2) [(7585,4172.5,3000),(7585,4172.5,2850)]
  NodesOffset = 0
  Normal = (0,0,-1)
  PerimeterLength = 8390
  Placement = pos=(0,0,6000) rot=(0,0,1;0rad)
  PredefinedType = 0
  VerticalArea = 1258500
  Width = 150
FEATURE [Part::FeaturePython] Structure306  label="L142"  # Arch/BIM 172 (typed FeaturePython)
  Base = -> Wire002
  FaceMaker = 0
  Height = 150
  HorizontalArea = 3.91484e+06
  IfcData = attributes={"GlobalId": {"name": "GlobalId", "type": "IfcGloballyUniqueId", "is_enum": false, "enum_values": []}, "Description": {"... (+484 chars omitted),+1 more (map truncated)
  IfcType = 172
  Length = 0
  MoveBase = false
  MoveWithHost = false
  Nodes = (2) [(7543.6,2543.13,3000),(7543.6,2543.13,2850)]
  NodesOffset = 0
  Normal = (0,0,-1)
  PerimeterLength = 8399.89
  Placement = pos=(0,0,5850) rot=(0,0,1;0rad)
  PredefinedType = 0
  VerticalArea = 1.25998e+06
  Width = 150
FEATURE [Part::FeaturePython] Structure307  label="L143"  # Arch/BIM 172 (typed FeaturePython)
  Base = -> Rectangle016
  FaceMaker = 0
  Height = 150
  HorizontalArea = 3.915e+06
  IfcData = attributes={"GlobalId": {"name": "GlobalId", "type": "IfcGloballyUniqueId", "is_enum": false, "enum_values": []}, "Description": {"... (+484 chars omitted),+1 more (map truncated)
  IfcType = 172
  Length = 0
  MoveBase = false
  MoveWithHost = false
  Nodes = (2) [(7585,900,3000),(7585,900,2850)]
  NodesOffset = 0
  Normal = (0,0,-1)
  PerimeterLength = 8300
  Placement = pos=(0,0,6000) rot=(0,0,1;0rad)
  PredefinedType = 0
  VerticalArea = 1.245e+06
  Width = 150
FEATURE [Part::FeaturePython] Structure308  label="L144"  # Arch/BIM 172 (typed FeaturePython)
  Base = -> Rectangle008
  FaceMaker = 0
  Height = 150
  HorizontalArea = 4354000
  IfcData = attributes={"GlobalId": {"name": "GlobalId", "type": "IfcGloballyUniqueId", "is_enum": false, "enum_values": []}, "Description": {"... (+484 chars omitted),+1 more (map truncated)
  IfcType = 172
  Length = 0
  MoveBase = false
  MoveWithHost = false
  Nodes = (2) [(9785,8270,3000),(9785,8270,2850)]
  NodesOffset = 0
  Normal = (0,0,-1)
  PerimeterLength = 9020
  Placement = pos=(0,0,6000) rot=(0,0,1;0rad)
  PredefinedType = 0
  VerticalArea = 1353000
  Width = 150
FEATURE [Part::FeaturePython] Structure309  label="L145"  # Arch/BIM 172 (typed FeaturePython)
  Base = -> Rectangle011
  FaceMaker = 0
  Height = 150
  HorizontalArea = 4396000
  IfcData = attributes={"GlobalId": {"name": "GlobalId", "type": "IfcGloballyUniqueId", "is_enum": false, "enum_values": []}, "Description": {"... (+484 chars omitted),+1 more (map truncated)
  IfcType = 172
  Length = 0
  MoveBase = false
  MoveWithHost = false
  Nodes = (2) [(9785,4995,3000),(9785,4995,2850)]
  NodesOffset = 0
  Normal = (0,0,-1)
  PerimeterLength = 9080
  Placement = pos=(0,0,6000) rot=(0,0,1;0rad)
  PredefinedType = 0
  VerticalArea = 1362000
  Width = 150
FEATURE [Part::FeaturePython] Structure310  label="L146"  # Arch/BIM 172 (typed FeaturePython)
  Base = -> Rectangle013
  FaceMaker = 0
  Height = 150
  HorizontalArea = 4.34e+06
  IfcData = attributes={"GlobalId": {"name": "GlobalId", "type": "IfcGloballyUniqueId", "is_enum": false, "enum_values": []}, "Description": {"... (+484 chars omitted),+1 more (map truncated)
  IfcType = 172
  Length = 0
  MoveBase = false
  MoveWithHost = false
  Nodes = (2) [(9785,1725,3000),(9785,1725,2850)]
  NodesOffset = 0
  Normal = (0,0,-1)
  PerimeterLength = 9000
  Placement = pos=(0,0,6000) rot=(0,0,1;0rad)
  PredefinedType = 0
  VerticalArea = 1350000
  Width = 150
FEATURE [Part::FeaturePython] Structure311  label="L147"  # Arch/BIM 172 (typed FeaturePython)
  Base = -> Rectangle009
  FaceMaker = 0
  Height = 150
  HorizontalArea = 1.794e+06
  IfcData = attributes={"GlobalId": {"name": "GlobalId", "type": "IfcGloballyUniqueId", "is_enum": false, "enum_values": []}, "Description": {"... (+484 chars omitted),+1 more (map truncated)
  IfcType = 172
  Length = 0
  MoveBase = false
  MoveWithHost = false
  Nodes = (2) [(11285,9135,3000),(11285,9135,2850)]
  NodesOffset = 0
  Normal = (0,0,-1)
  PerimeterLength = 5360
  Placement = pos=(0,0,6000) rot=(0,0,1;0rad)
  PredefinedType = 0
  VerticalArea = 804000
  Width = 150
FEATURE [Part::FeaturePython] Structure312  label="L148"  # Arch/BIM 172 (typed FeaturePython)
  Base = -> Rectangle018
  FaceMaker = 0
  Height = 150
  HorizontalArea = 3.211e+06
  IfcData = attributes={"GlobalId": {"name": "GlobalId", "type": "IfcGloballyUniqueId", "is_enum": false, "enum_values": []}, "Description": {"... (+484 chars omitted),+1 more (map truncated)
  IfcType = 172
  Length = 0
  MoveBase = false
  MoveWithHost = false
  Nodes = (2) [(11285,4660,3000),(11285,4660,2850)]
  NodesOffset = 0
  Normal = (0,0,-1)
  PerimeterLength = 7540
  Placement = pos=(0,0,5850) rot=(0,0,1;0rad)
  PredefinedType = 0
  VerticalArea = 1.131e+06
  Width = 150
FEATURE [Part::FeaturePython] Structure313  label="L149"  # Arch/BIM 172 (typed FeaturePython)
  Base = -> Rectangle020
  FaceMaker = 0
  Height = 150
  HorizontalArea = 9439500
  IfcData = attributes={"GlobalId": {"name": "GlobalId", "type": "IfcGloballyUniqueId", "is_enum": false, "enum_values": []}, "Description": {"... (+484 chars omitted),+1 more (map truncated)
  IfcType = 172
  Length = 0
  MoveBase = false
  MoveWithHost = false
  Nodes = (2) [(12157.5,1725,3000),(12157.5,1725,2850)]
  NodesOffset = 0
  Normal = (0,0,-1)
  PerimeterLength = 12290
  Placement = pos=(0,0,6000) rot=(0,0,1;0rad)
  PredefinedType = 0
  VerticalArea = 1843500
  Width = 150
FEATURE [Part::FeaturePython] Structure314  label="L150"  # Arch/BIM 172 (typed FeaturePython)
  Base = -> Rectangle019
  FaceMaker = 0
  Height = 150
  HorizontalArea = 3.93965e+06
  IfcData = attributes={"GlobalId": {"name": "GlobalId", "type": "IfcGloballyUniqueId", "is_enum": false, "enum_values": []}, "Description": {"... (+484 chars omitted),+1 more (map truncated)
  IfcType = 172
  Length = 0
  MoveBase = false
  MoveWithHost = false
  Nodes = (2) [(12882.5,4660,3000),(12882.5,4660,2850)]
  NodesOffset = 0
  Normal = (0,0,-1)
  PerimeterLength = 8130
  Placement = pos=(0,0,6000) rot=(0,0,1;0rad)
  PredefinedType = 0
  VerticalArea = 1.2195e+06
  Width = 150
FEATURE [Part::FeaturePython] Structure315  label="L151"  # Arch/BIM 172 (typed FeaturePython)
  Base = -> Rectangle017
  FaceMaker = 0
  Height = 150
  HorizontalArea = 4174500
  IfcData = attributes={"GlobalId": {"name": "GlobalId", "type": "IfcGloballyUniqueId", "is_enum": false, "enum_values": []}, "Description": {"... (+484 chars omitted),+1 more (map truncated)
  IfcType = 172
  Length = 0
  MoveBase = false
  MoveWithHost = false
  Nodes = (2) [(13597.5,9135,3000),(13597.5,9135,2850)]
  NodesOffset = 0
  Normal = (0,0,-1)
  PerimeterLength = 8810
  Placement = pos=(0,0,6000) rot=(0,0,1;0rad)
  PredefinedType = 0
  VerticalArea = 1321500
  Width = 150
FEATURE [App::GeometryPython] BuildingPart018  label="Losas sobre P2"  # Arch/BIM 172 (typed FeaturePython)
  Area = 0
  Group = -> [Structure295,Structure296,Structure297,Structure302,Structure303,Structure304,Structure305,Structure306,Structure307,Structure308,Structure309,Structure310,Structure311,Structure312,Structure313,Structure314,Structure315]
  Height = 0
  HeightPropagate = true
  IfcData = attributes={"GlobalId": {"name": "GlobalId", "type": "IfcGloballyUniqueId", "is_enum": false, "enum_values": []}, "Description": {"... (+484 chars omitted),+1 more (map truncated)
  IfcType = 172
  LevelOffset = 0
  PredefinedType = 0
FEATURE [App::GeometryPython] BuildingPart010  label="Piso 2"  # Arch/BIM 172 (typed FeaturePython)
  Area = 24900000
  Group = -> [BuildingPart016,BuildingPart018,Wall003,BuildingPart017]
  Height = 0
  HeightPropagate = true
  IfcData = attributes={"GlobalId": {"name": "GlobalId", "type": "IfcGloballyUniqueId", "is_enum": false, "enum_values": []}, "Description": {"... (+484 chars omitted),+1 more (map truncated)
  IfcType = 172
  LevelOffset = 0
  Placement = pos=(0,0,6000) rot=(0,0,1;0rad)
  PredefinedType = 0
FEATURE [Part::FeaturePython] Structure316  label="25x15 C064"  # Arch/BIM 24 (typed FeaturePython)
  FaceMaker = 0
  Height = 3000
  HorizontalArea = 37500
  IfcData = attributes={"GlobalId": {"name": "GlobalId", "type": "IfcGloballyUniqueId", "is_enum": false, "enum_values": []}, "Description": {"... (+438 chars omitted),+1 more (map truncated)
  IfcType = 24
  Length = 250
  MoveBase = false
  MoveWithHost = false
  Nodes = (2) [(-1.05471e-15,1.36424e-15,0),(-1.05471e-15,1.36424e-15,3000)]
  NodesOffset = 0
  Normal = (0,0,0)
  PerimeterLength = 800
  Placement = pos=(1930,9900,9000) rot=(0,0,1;0rad)
  PredefinedType = 0
  VerticalArea = 2400000
  Width = 150
FEATURE [Part::FeaturePython] Structure317  label="25x15 C065"  # Arch/BIM 172 (typed FeaturePython)
  FaceMaker = 0
  Height = 3000
  HorizontalArea = 37500
  IfcData = attributes={"GlobalId": {"name": "GlobalId", "type": "IfcGloballyUniqueId", "is_enum": false, "enum_values": []}, "Description": {"... (+484 chars omitted),+1 more (map truncated)
  IfcType = 172
  Length = 250
  MoveBase = false
  MoveWithHost = false
  Nodes = (2) [(-1.05471e-15,1.36424e-15,0),(-1.05471e-15,1.36424e-15,3000)]
  NodesOffset = 0
  Normal = (0,0,0)
  PerimeterLength = 800
  Placement = pos=(1930,100,9000) rot=(0,0,1;0rad)
  PredefinedType = 0
  VerticalArea = 2400000
  Width = 150
FEATURE [Part::FeaturePython] Structure318  label="25x15 C066"  # Arch/BIM 24 (typed FeaturePython)
  FaceMaker = 0
  Height = 3000
  HorizontalArea = 37500
  IfcData = attributes={"GlobalId": {"name": "GlobalId", "type": "IfcGloballyUniqueId", "is_enum": false, "enum_values": []}, "Description": {"... (+438 chars omitted),+1 more (map truncated)
  IfcType = 24
  Length = 250
  MoveBase = false
  MoveWithHost = false
  Nodes = (2) [(-1.05471e-15,1.36424e-15,0),(-1.05471e-15,1.36424e-15,3000)]
  NodesOffset = 0
  Normal = (0,0,0)
  PerimeterLength = 800
  Placement = pos=(6160,6640,9000) rot=(0,0,1;0rad)
  PredefinedType = 0
  VerticalArea = 2400000
  Width = 150
FEATURE [Part::FeaturePython] Structure319  label="25x15 C067"  # Arch/BIM 24 (typed FeaturePython)
  FaceMaker = 0
  Height = 3000
  HorizontalArea = 37500
  IfcData = attributes={"GlobalId": {"name": "GlobalId", "type": "IfcGloballyUniqueId", "is_enum": false, "enum_values": []}, "Description": {"... (+438 chars omitted),+1 more (map truncated)
  IfcType = 24
  Length = 250
  MoveBase = false
  MoveWithHost = false
  Nodes = (2) [(-1.05471e-15,1.36424e-15,0),(-1.05471e-15,1.36424e-15,3000)]
  NodesOffset = 0
  Normal = (0,0,0)
  PerimeterLength = 800
  Placement = pos=(6160,3350,9000) rot=(0,0,1;0rad)
  PredefinedType = 0
  VerticalArea = 2400000
  Width = 150
FEATURE [Part::FeaturePython] Structure320  label="25x15 C068"  # Arch/BIM 24 (typed FeaturePython)
  FaceMaker = 0
  Height = 3000
  HorizontalArea = 37500
  IfcData = attributes={"GlobalId": {"name": "GlobalId", "type": "IfcGloballyUniqueId", "is_enum": false, "enum_values": []}, "Description": {"... (+438 chars omitted),+1 more (map truncated)
  IfcType = 24
  Length = 250
  MoveBase = false
  MoveWithHost = false
  Nodes = (2) [(-1.05471e-15,1.36424e-15,0),(-1.05471e-15,1.36424e-15,3000)]
  NodesOffset = 0
  Normal = (0,0,0)
  PerimeterLength = 800
  Placement = pos=(6160,100,9000) rot=(0,0,1;0rad)
  PredefinedType = 0
  VerticalArea = 2400000
  Width = 150
FEATURE [Part::FeaturePython] Structure321  label="25x15 C069"  # Arch/BIM 24 (typed FeaturePython)
  FaceMaker = 0
  Height = 3000
  HorizontalArea = 37500
  IfcData = attributes={"GlobalId": {"name": "GlobalId", "type": "IfcGloballyUniqueId", "is_enum": false, "enum_values": []}, "Description": {"... (+438 chars omitted),+1 more (map truncated)
  IfcType = 24
  Length = 250
  MoveBase = false
  MoveWithHost = false
  Nodes = (2) [(-1.05471e-15,1.36424e-15,0),(-1.05471e-15,1.36424e-15,3000)]
  NodesOffset = 0
  Normal = (0,0,0)
  PerimeterLength = 800
  Placement = pos=(9010,100,9000) rot=(0,0,1;0rad)
  PredefinedType = 0
  VerticalArea = 2400000
  Width = 150
FEATURE [Part::FeaturePython] Structure322  label="25x15 C070"  # Arch/BIM 24 (typed FeaturePython)
  FaceMaker = 0
  Height = 3000
  HorizontalArea = 37500
  IfcData = attributes={"GlobalId": {"name": "GlobalId", "type": "IfcGloballyUniqueId", "is_enum": false, "enum_values": []}, "Description": {"... (+438 chars omitted),+1 more (map truncated)
  IfcType = 24
  Length = 250
  MoveBase = false
  MoveWithHost = false
  Nodes = (2) [(-1.05471e-15,1.36424e-15,0),(-1.05471e-15,1.36424e-15,3000)]
  NodesOffset = 0
  Normal = (0,0,0)
  PerimeterLength = 800
  Placement = pos=(10560,100,9000) rot=(0,0,1;0rad)
  PredefinedType = 0
  VerticalArea = 2400000
  Width = 150
FEATURE [Part::FeaturePython] Structure323  label="25x15 C071"  # Arch/BIM 24 (typed FeaturePython)
  FaceMaker = 0
  Height = 3000
  HorizontalArea = 37500
  IfcData = attributes={"GlobalId": {"name": "GlobalId", "type": "IfcGloballyUniqueId", "is_enum": false, "enum_values": []}, "Description": {"... (+438 chars omitted),+1 more (map truncated)
  IfcType = 24
  Length = 250
  MoveBase = false
  MoveWithHost = false
  Nodes = (2) [(-1.05471e-15,1.36424e-15,0),(-1.05471e-15,1.36424e-15,3000)]
  NodesOffset = 0
  Normal = (0,0,0)
  PerimeterLength = 800
  Placement = pos=(13780,100,9000) rot=(0,0,1;0rad)
  PredefinedType = 0
  VerticalArea = 2400000
  Width = 150
FEATURE [Part::FeaturePython] Structure324  label="25x15 C072"  # Arch/BIM 24 (typed FeaturePython)
  FaceMaker = 0
  Height = 3000
  HorizontalArea = 37500
  IfcData = attributes={"GlobalId": {"name": "GlobalId", "type": "IfcGloballyUniqueId", "is_enum": false, "enum_values": []}, "Description": {"... (+438 chars omitted),+1 more (map truncated)
  IfcType = 24
  Length = 250
  MoveBase = false
  MoveWithHost = false
  Nodes = (2) [(-1.05471e-15,1.36424e-15,0),(-1.05471e-15,1.36424e-15,3000)]
  NodesOffset = 0
  Normal = (0,0,0)
  PerimeterLength = 800
  Placement = pos=(15210,5970,9000) rot=(0,0,1;0rad)
  PredefinedType = 0
  VerticalArea = 2400000
  Width = 150
FEATURE [Part::FeaturePython] Structure325  label="25x15 C073"  # Arch/BIM 24 (typed FeaturePython)
  FaceMaker = 0
  Height = 3000
  HorizontalArea = 37500
  IfcData = attributes={"GlobalId": {"name": "GlobalId", "type": "IfcGloballyUniqueId", "is_enum": false, "enum_values": []}, "Description": {"... (+438 chars omitted),+1 more (map truncated)
  IfcType = 24
  Length = 250
  MoveBase = false
  MoveWithHost = false
  Nodes = (2) [(-1.05471e-15,1.36424e-15,0),(-1.05471e-15,1.36424e-15,3000)]
  NodesOffset = 0
  Normal = (0,0,0)
  PerimeterLength = 800
  Placement = pos=(13780,5970,9000) rot=(0,0,1;0rad)
  PredefinedType = 0
  VerticalArea = 2400000
  Width = 150
FEATURE [Part::FeaturePython] Structure326  label="25x15 C074"  # Arch/BIM 172 (typed FeaturePython)
  FaceMaker = 0
  Height = 3000
  HorizontalArea = 37500
  IfcData = attributes={"GlobalId": {"name": "GlobalId", "type": "IfcGloballyUniqueId", "is_enum": false, "enum_values": []}, "Description": {"... (+484 chars omitted),+1 more (map truncated)
  IfcType = 172
  Length = 250
  MoveBase = false
  MoveWithHost = false
  Nodes = (2) [(-1.05471e-15,1.36424e-15,0),(-1.05471e-15,1.36424e-15,3000)]
  NodesOffset = 0
  Normal = (0,0,0)
  PerimeterLength = 800
  Placement = pos=(1930,9900,9000) rot=(0,0,1;0rad)
  PredefinedType = 0
  VerticalArea = 2400000
  Width = 150
FEATURE [Part::FeaturePython] Structure327  label="25x15 C075"  # Arch/BIM 172 (typed FeaturePython)
  FaceMaker = 0
  Height = 3000
  HorizontalArea = 37500
  IfcData = attributes={"GlobalId": {"name": "GlobalId", "type": "IfcGloballyUniqueId", "is_enum": false, "enum_values": []}, "Description": {"... (+484 chars omitted),+1 more (map truncated)
  IfcType = 172
  Length = 250
  MoveBase = false
  MoveWithHost = false
  Nodes = (2) [(-1.05471e-15,1.36424e-15,0),(-1.05471e-15,1.36424e-15,3000)]
  NodesOffset = 0
  Normal = (0,0,0)
  PerimeterLength = 800
  Placement = pos=(9010,6640,9000) rot=(0,0,1;1.5708rad)
  PredefinedType = 0
  VerticalArea = 2400000
  Width = 150
FEATURE [Part::FeaturePython] Structure328  label="25x15 C076"  # Arch/BIM 172 (typed FeaturePython)
  FaceMaker = 0
  Height = 3000
  HorizontalArea = 37500
  IfcData = attributes={"GlobalId": {"name": "GlobalId", "type": "IfcGloballyUniqueId", "is_enum": false, "enum_values": []}, "Description": {"... (+484 chars omitted),+1 more (map truncated)
  IfcType = 172
  Length = 250
  MoveBase = false
  MoveWithHost = false
  Nodes = (2) [(-1.05471e-15,1.36424e-15,0),(-1.05471e-15,1.36424e-15,3000)]
  NodesOffset = 0
  Normal = (0,0,0)
  PerimeterLength = 800
  Placement = pos=(9010,3350,9000) rot=(0,0,1;1.5708rad)
  PredefinedType = 0
  VerticalArea = 2400000
  Width = 150
FEATURE [Part::FeaturePython] Structure329  label="25x15 C077"  # Arch/BIM 172 (typed FeaturePython)
  FaceMaker = 0
  Height = 3000
  HorizontalArea = 37500
  IfcData = attributes={"GlobalId": {"name": "GlobalId", "type": "IfcGloballyUniqueId", "is_enum": false, "enum_values": []}, "Description": {"... (+484 chars omitted),+1 more (map truncated)
  IfcType = 172
  Length = 250
  MoveBase = false
  MoveWithHost = false
  Nodes = (2) [(-1.05471e-15,1.36424e-15,0),(-1.05471e-15,1.36424e-15,3000)]
  NodesOffset = 0
  Normal = (0,0,0)
  PerimeterLength = 800
  Placement = pos=(10560,3350,9000) rot=(0,0,1;1.5708rad)
  PredefinedType = 0
  VerticalArea = 2400000
  Width = 150
FEATURE [Part::FeaturePython] Structure330  label="25x15 C078"  # Arch/BIM 172 (typed FeaturePython)
  FaceMaker = 0
  Height = 3000
  HorizontalArea = 37500
  IfcData = attributes={"GlobalId": {"name": "GlobalId", "type": "IfcGloballyUniqueId", "is_enum": false, "enum_values": []}, "Description": {"... (+484 chars omitted),+1 more (map truncated)
  IfcType = 172
  Length = 250
  MoveBase = false
  MoveWithHost = false
  Nodes = (2) [(-1.05471e-15,1.36424e-15,0),(-1.05471e-15,1.36424e-15,3000)]
  NodesOffset = 0
  Normal = (0,0,0)
  PerimeterLength = 800
  Placement = pos=(13780,3350,9000) rot=(0,0,1;1.5708rad)
  PredefinedType = 0
  VerticalArea = 2400000
  Width = 150
FEATURE [Part::FeaturePython] Structure331  label="25x15 C079"  # Arch/BIM 172 (typed FeaturePython)
  FaceMaker = 0
  Height = 3000
  HorizontalArea = 37500
  IfcData = attributes={"GlobalId": {"name": "GlobalId", "type": "IfcGloballyUniqueId", "is_enum": false, "enum_values": []}, "Description": {"... (+484 chars omitted),+1 more (map truncated)
  IfcType = 172
  Length = 250
  MoveBase = false
  MoveWithHost = false
  Nodes = (2) [(-1.05471e-15,1.36424e-15,0),(-1.05471e-15,1.36424e-15,3000)]
  NodesOffset = 0
  Normal = (0,0,0)
  PerimeterLength = 800
  Placement = pos=(9010,9900,9000) rot=(0,0,1;0rad)
  PredefinedType = 0
  VerticalArea = 2400000
  Width = 150
FEATURE [Part::FeaturePython] Structure332  label="25x15 C080"  # Arch/BIM 172 (typed FeaturePython)
  FaceMaker = 0
  Height = 3000
  HorizontalArea = 37500
  IfcData = attributes={"GlobalId": {"name": "GlobalId", "type": "IfcGloballyUniqueId", "is_enum": false, "enum_values": []}, "Description": {"... (+484 chars omitted),+1 more (map truncated)
  IfcType = 172
  Length = 250
  MoveBase = false
  MoveWithHost = false
  Nodes = (2) [(-1.05471e-15,1.36424e-15,0),(-1.05471e-15,1.36424e-15,3000)]
  NodesOffset = 0
  Normal = (0,0,0)
  PerimeterLength = 800
  Placement = pos=(6160,9900,9000) rot=(0,0,1;0rad)
  PredefinedType = 0
  VerticalArea = 2400000
  Width = 150
FEATURE [Part::FeaturePython] Structure333  label="25x15 C081"  # Arch/BIM 172 (typed FeaturePython)
  FaceMaker = 0
  Height = 3000
  HorizontalArea = 37500
  IfcData = attributes={"GlobalId": {"name": "GlobalId", "type": "IfcGloballyUniqueId", "is_enum": false, "enum_values": []}, "Description": {"... (+484 chars omitted),+1 more (map truncated)
  IfcType = 172
  Length = 250
  MoveBase = false
  MoveWithHost = false
  Nodes = (2) [(-1.05471e-15,1.36424e-15,0),(-1.05471e-15,1.36424e-15,3000)]
  NodesOffset = 0
  Normal = (0,0,0)
  PerimeterLength = 800
  Placement = pos=(12010,9900,9000) rot=(0,0,1;0rad)
  PredefinedType = 0
  VerticalArea = 2400000
  Width = 150
FEATURE [Part::FeaturePython] Structure334  label="25x15 C082"  # Arch/BIM 172 (typed FeaturePython)
  FaceMaker = 0
  Height = 3000
  HorizontalArea = 37500
  IfcData = attributes={"GlobalId": {"name": "GlobalId", "type": "IfcGloballyUniqueId", "is_enum": false, "enum_values": []}, "Description": {"... (+484 chars omitted),+1 more (map truncated)
  IfcType = 172
  Length = 250
  MoveBase = false
  MoveWithHost = false
  Nodes = (2) [(-1.05471e-15,1.36424e-15,0),(-1.05471e-15,1.36424e-15,3000)]
  NodesOffset = 0
  Normal = (0,0,0)
  PerimeterLength = 800
  Placement = pos=(15210,9900,9000) rot=(0,0,1;0rad)
  PredefinedType = 0
  VerticalArea = 2400000
  Width = 150
FEATURE [Part::FeaturePython] Structure335  label="25x20 C012"  # Arch/BIM 24 (typed FeaturePython)
  FaceMaker = 0
  Height = 3000
  HorizontalArea = 50000
  IfcData = attributes={"GlobalId": {"name": "GlobalId", "type": "IfcGloballyUniqueId", "is_enum": false, "enum_values": []}, "Description": {"... (+438 chars omitted),+1 more (map truncated)
  IfcType = 24
  Length = 250
  MoveBase = false
  MoveWithHost = false
  Nodes = (2) [(-1.05471e-15,-1.81899e-15,0),(-1.05471e-15,-1.81899e-15,3000)]
  NodesOffset = 0
  Normal = (0,0,0)
  PerimeterLength = 900
  Placement = pos=(1930,6640,9000) rot=(0,0,1;0rad)
  PredefinedType = 0
  VerticalArea = 2700000
  Width = 200
FEATURE [Part::FeaturePython] Structure336  label="25x20 C013"  # Arch/BIM 172 (typed FeaturePython)
  FaceMaker = 0
  Height = 3000
  HorizontalArea = 50000
  IfcData = attributes={"GlobalId": {"name": "GlobalId", "type": "IfcGloballyUniqueId", "is_enum": false, "enum_values": []}, "Description": {"... (+484 chars omitted),+1 more (map truncated)
  IfcType = 172
  Length = 250
  MoveBase = false
  MoveWithHost = false
  Nodes = (2) [(-1.05471e-15,-1.81899e-15,0),(-1.05471e-15,-1.81899e-15,3000)]
  NodesOffset = 0
  Normal = (0,0,0)
  PerimeterLength = 900
  Placement = pos=(1930,3350,9000) rot=(0,0,1;0rad)
  PredefinedType = 0
  VerticalArea = 2700000
  Width = 200
FEATURE [App::GeometryPython] BuildingPart020  label="Columnas sobre P3"  # Arch/BIM 172 (typed FeaturePython)
  Area = 0
  Group = -> [Structure316,Structure317,Structure318,Structure319,Structure320,Structure321,Structure322,Structure323,Structure324,Structure325,Structure326,Structure327,Structure328,Structure329,Structure330,Structure331,Structure332,Structure333,Structure334,Structure335,Structure336]
  Height = 0
  HeightPropagate = true
  IfcData = attributes={"GlobalId": {"name": "GlobalId", "type": "IfcGloballyUniqueId", "is_enum": false, "enum_values": []}, "Description": {"... (+484 chars omitted),+1 more (map truncated)
  IfcType = 172
  LevelOffset = 0
  PredefinedType = 0
FEATURE [Part::FeaturePython] Structure337  label="L152"  # Arch/BIM 172 (typed FeaturePython)
  Base = -> Rectangle004
  FaceMaker = 0
  Height = 150
  HorizontalArea = 12611050
  IfcData = attributes={"GlobalId": {"name": "GlobalId", "type": "IfcGloballyUniqueId", "is_enum": false, "enum_values": []}, "Description": {"... (+484 chars omitted),+1 more (map truncated)
  IfcType = 172
  Length = 0
  MoveBase = false
  MoveWithHost = false
  Nodes = (2) [(4057.5,8270,3000),(4057.5,8270,2850)]
  NodesOffset = 0
  Normal = (0,0,-1)
  PerimeterLength = 14330
  Placement = pos=(0,0,9000) rot=(0,0,1;0rad)
  PredefinedType = 0
  VerticalArea = 2149500
  Width = 150
FEATURE [Part::FeaturePython] Structure338  label="L153"  # Arch/BIM 172 (typed FeaturePython)
  Base = -> Rectangle005
  FaceMaker = 0
  Height = 150
  HorizontalArea = 12732700
  IfcData = attributes={"GlobalId": {"name": "GlobalId", "type": "IfcGloballyUniqueId", "is_enum": false, "enum_values": []}, "Description": {"... (+484 chars omitted),+1 more (map truncated)
  IfcType = 172
  Length = 0
  MoveBase = false
  MoveWithHost = false
  Nodes = (2) [(4057.5,4995,3000),(4057.5,4995,2850)]
  NodesOffset = 0
  Normal = (0,0,-1)
  PerimeterLength = 14390
  Placement = pos=(0,0,9000) rot=(0,0,1;0rad)
  PredefinedType = 0
  VerticalArea = 2158500
  Width = 150
FEATURE [Part::FeaturePython] Structure339  label="L154"  # Arch/BIM 172 (typed FeaturePython)
  Base = -> Rectangle006
  FaceMaker = 0
  Height = 150
  HorizontalArea = 1.25705e+07
  IfcData = attributes={"GlobalId": {"name": "GlobalId", "type": "IfcGloballyUniqueId", "is_enum": false, "enum_values": []}, "Description": {"... (+484 chars omitted),+1 more (map truncated)
  IfcType = 172
  Length = 0
  MoveBase = false
  MoveWithHost = false
  Nodes = (2) [(4057.5,1725,3000),(4057.5,1725,2850)]
  NodesOffset = 0
  Normal = (0,0,-1)
  PerimeterLength = 14310
  Placement = pos=(0,0,9000) rot=(0,0,1;0rad)
  PredefinedType = 0
  VerticalArea = 2146500
  Width = 150
FEATURE [Part::FeaturePython] Structure340  label="L155"  # Arch/BIM 172 (typed FeaturePython)
  Base = -> Rectangle014
  FaceMaker = 0
  Height = 150
  HorizontalArea = 3928500
  IfcData = attributes={"GlobalId": {"name": "GlobalId", "type": "IfcGloballyUniqueId", "is_enum": false, "enum_values": []}, "Description": {"... (+484 chars omitted),+1 more (map truncated)
  IfcType = 172
  Length = 0
  MoveBase = false
  MoveWithHost = false
  Nodes = (2) [(7585,9097.5,3000),(7585,9097.5,2850)]
  NodesOffset = 0
  Normal = (0,0,-1)
  PerimeterLength = 8310
  Placement = pos=(0,0,9000) rot=(0,0,1;0rad)
  PredefinedType = 0
  VerticalArea = 1246500
  Width = 150
FEATURE [Part::FeaturePython] Structure341  label="L156"  # Arch/BIM 172 (typed FeaturePython)
  Base = -> Wire
  FaceMaker = 0
  Height = 150
  HorizontalArea = 3.9285e+06
  IfcData = attributes={"GlobalId": {"name": "GlobalId", "type": "IfcGloballyUniqueId", "is_enum": false, "enum_values": []}, "Description": {"... (+484 chars omitted),+1 more (map truncated)
  IfcType = 172
  Length = 0
  MoveBase = false
  MoveWithHost = false
  Nodes = (2) [(7543.76,7449.37,3000),(7543.76,7449.37,2850)]
  NodesOffset = 0
  Normal = (0,0,-1)
  PerimeterLength = 8410
  Placement = pos=(0,0,8850) rot=(0,0,1;0rad)
  PredefinedType = 0
  VerticalArea = 1261500
  Width = 150
FEATURE [Part::FeaturePython] Structure342  label="L157"  # Arch/BIM 172 (typed FeaturePython)
  Base = -> Wire001
  FaceMaker = 0
  Height = 150
  HorizontalArea = 3.90134e+06
  IfcData = attributes={"GlobalId": {"name": "GlobalId", "type": "IfcGloballyUniqueId", "is_enum": false, "enum_values": []}, "Description": {"... (+484 chars omitted),+1 more (map truncated)
  IfcType = 172
  Length = 0
  MoveBase = false
  MoveWithHost = false
  Nodes = (2) [(7543.46,5835.61,3000),(7543.46,5835.61,2850)]
  NodesOffset = 0
  Normal = (0,0,-1)
  PerimeterLength = 8389.89
  Placement = pos=(0,0,8850) rot=(0,0,1;0rad)
  PredefinedType = 0
  VerticalArea = 1.25848e+06
  Width = 150
FEATURE [Part::FeaturePython] Structure343  label="L158"  # Arch/BIM 172 (typed FeaturePython)
  Base = -> Rectangle015
  FaceMaker = 0
  Height = 150
  HorizontalArea = 4.0365e+06
  IfcData = attributes={"GlobalId": {"name": "GlobalId", "type": "IfcGloballyUniqueId", "is_enum": false, "enum_values": []}, "Description": {"... (+484 chars omitted),+1 more (map truncated)
  IfcType = 172
  Length = 0
  MoveBase = false
  MoveWithHost = false
  Nodes = (2) [(7585,4172.5,3000),(7585,4172.5,2850)]
  NodesOffset = 0
  Normal = (0,0,-1)
  PerimeterLength = 8390
  Placement = pos=(0,0,9000) rot=(0,0,1;0rad)
  PredefinedType = 0
  VerticalArea = 1258500
  Width = 150
FEATURE [Part::FeaturePython] Structure344  label="L159"  # Arch/BIM 172 (typed FeaturePython)
  Base = -> Wire002
  FaceMaker = 0
  Height = 150
  HorizontalArea = 3.91484e+06
  IfcData = attributes={"GlobalId": {"name": "GlobalId", "type": "IfcGloballyUniqueId", "is_enum": false, "enum_values": []}, "Description": {"... (+484 chars omitted),+1 more (map truncated)
  IfcType = 172
  Length = 0
  MoveBase = false
  MoveWithHost = false
  Nodes = (2) [(7543.6,2543.13,3000),(7543.6,2543.13,2850)]
  NodesOffset = 0
  Normal = (0,0,-1)
  PerimeterLength = 8399.89
  Placement = pos=(0,0,8850) rot=(0,0,1;0rad)
  PredefinedType = 0
  VerticalArea = 1.25998e+06
  Width = 150
FEATURE [Part::FeaturePython] Structure345  label="L160"  # Arch/BIM 172 (typed FeaturePython)
  Base = -> Rectangle016
  FaceMaker = 0
  Height = 150
  HorizontalArea = 3.915e+06
  IfcData = attributes={"GlobalId": {"name": "GlobalId", "type": "IfcGloballyUniqueId", "is_enum": false, "enum_values": []}, "Description": {"... (+484 chars omitted),+1 more (map truncated)
  IfcType = 172
  Length = 0
  MoveBase = false
  MoveWithHost = false
  Nodes = (2) [(7585,900,3000),(7585,900,2850)]
  NodesOffset = 0
  Normal = (0,0,-1)
  PerimeterLength = 8300
  Placement = pos=(0,0,9000) rot=(0,0,1;0rad)
  PredefinedType = 0
  VerticalArea = 1.245e+06
  Width = 150
FEATURE [Part::FeaturePython] Structure346  label="L161"  # Arch/BIM 172 (typed FeaturePython)
  Base = -> Rectangle008
  FaceMaker = 0
  Height = 150
  HorizontalArea = 4354000
  IfcData = attributes={"GlobalId": {"name": "GlobalId", "type": "IfcGloballyUniqueId", "is_enum": false, "enum_values": []}, "Description": {"... (+484 chars omitted),+1 more (map truncated)
  IfcType = 172
  Length = 0
  MoveBase = false
  MoveWithHost = false
  Nodes = (2) [(9785,8270,3000),(9785,8270,2850)]
  NodesOffset = 0
  Normal = (0,0,-1)
  PerimeterLength = 9020
  Placement = pos=(0,0,9000) rot=(0,0,1;0rad)
  PredefinedType = 0
  VerticalArea = 1353000
  Width = 150
FEATURE [Part::FeaturePython] Structure347  label="L162"  # Arch/BIM 172 (typed FeaturePython)
  Base = -> Rectangle011
  FaceMaker = 0
  Height = 150
  HorizontalArea = 4396000
  IfcData = attributes={"GlobalId": {"name": "GlobalId", "type": "IfcGloballyUniqueId", "is_enum": false, "enum_values": []}, "Description": {"... (+484 chars omitted),+1 more (map truncated)
  IfcType = 172
  Length = 0
  MoveBase = false
  MoveWithHost = false
  Nodes = (2) [(9785,4995,3000),(9785,4995,2850)]
  NodesOffset = 0
  Normal = (0,0,-1)
  PerimeterLength = 9080
  Placement = pos=(0,0,9000) rot=(0,0,1;0rad)
  PredefinedType = 0
  VerticalArea = 1362000
  Width = 150
FEATURE [Part::FeaturePython] Structure348  label="L163"  # Arch/BIM 172 (typed FeaturePython)
  Base = -> Rectangle013
  FaceMaker = 0
  Height = 150
  HorizontalArea = 4.34e+06
  IfcData = attributes={"GlobalId": {"name": "GlobalId", "type": "IfcGloballyUniqueId", "is_enum": false, "enum_values": []}, "Description": {"... (+484 chars omitted),+1 more (map truncated)
  IfcType = 172
  Length = 0
  MoveBase = false
  MoveWithHost = false
  Nodes = (2) [(9785,1725,3000),(9785,1725,2850)]
  NodesOffset = 0
  Normal = (0,0,-1)
  PerimeterLength = 9000
  Placement = pos=(0,0,9000) rot=(0,0,1;0rad)
  PredefinedType = 0
  VerticalArea = 1350000
  Width = 150
FEATURE [Part::FeaturePython] Structure349  label="L164"  # Arch/BIM 172 (typed FeaturePython)
  Base = -> Rectangle009
  FaceMaker = 0
  Height = 150
  HorizontalArea = 1.794e+06
  IfcData = attributes={"GlobalId": {"name": "GlobalId", "type": "IfcGloballyUniqueId", "is_enum": false, "enum_values": []}, "Description": {"... (+484 chars omitted),+1 more (map truncated)
  IfcType = 172
  Length = 0
  MoveBase = false
  MoveWithHost = false
  Nodes = (2) [(11285,9135,3000),(11285,9135,2850)]
  NodesOffset = 0
  Normal = (0,0,-1)
  PerimeterLength = 5360
  Placement = pos=(0,0,9000) rot=(0,0,1;0rad)
  PredefinedType = 0
  VerticalArea = 804000
  Width = 150
FEATURE [Part::FeaturePython] Structure350  label="L165"  # Arch/BIM 172 (typed FeaturePython)
  Base = -> Rectangle018
  FaceMaker = 0
  Height = 150
  HorizontalArea = 3.211e+06
  IfcData = attributes={"GlobalId": {"name": "GlobalId", "type": "IfcGloballyUniqueId", "is_enum": false, "enum_values": []}, "Description": {"... (+484 chars omitted),+1 more (map truncated)
  IfcType = 172
  Length = 0
  MoveBase = false
  MoveWithHost = false
  Nodes = (2) [(11285,4660,3000),(11285,4660,2850)]
  NodesOffset = 0
  Normal = (0,0,-1)
  PerimeterLength = 7540
  Placement = pos=(0,0,8850) rot=(0,0,1;0rad)
  PredefinedType = 0
  VerticalArea = 1.131e+06
  Width = 150
FEATURE [Part::FeaturePython] Structure351  label="L166"  # Arch/BIM 172 (typed FeaturePython)
  Base = -> Rectangle020
  FaceMaker = 0
  Height = 150
  HorizontalArea = 9439500
  IfcData = attributes={"GlobalId": {"name": "GlobalId", "type": "IfcGloballyUniqueId", "is_enum": false, "enum_values": []}, "Description": {"... (+484 chars omitted),+1 more (map truncated)
  IfcType = 172
  Length = 0
  MoveBase = false
  MoveWithHost = false
  Nodes = (2) [(12157.5,1725,3000),(12157.5,1725,2850)]
  NodesOffset = 0
  Normal = (0,0,-1)
  PerimeterLength = 12290
  Placement = pos=(0,0,9000) rot=(0,0,1;0rad)
  PredefinedType = 0
  VerticalArea = 1843500
  Width = 150
FEATURE [Part::FeaturePython] Structure352  label="L167"  # Arch/BIM 172 (typed FeaturePython)
  Base = -> Rectangle019
  FaceMaker = 0
  Height = 150
  HorizontalArea = 3.93965e+06
  IfcData = attributes={"GlobalId": {"name": "GlobalId", "type": "IfcGloballyUniqueId", "is_enum": false, "enum_values": []}, "Description": {"... (+484 chars omitted),+1 more (map truncated)
  IfcType = 172
  Length = 0
  MoveBase = false
  MoveWithHost = false
  Nodes = (2) [(12882.5,4660,3000),(12882.5,4660,2850)]
  NodesOffset = 0
  Normal = (0,0,-1)
  PerimeterLength = 8130
  Placement = pos=(0,0,9000) rot=(0,0,1;0rad)
  PredefinedType = 0
  VerticalArea = 1.2195e+06
  Width = 150
FEATURE [Part::FeaturePython] Structure353  label="L168"  # Arch/BIM 172 (typed FeaturePython)
  Base = -> Rectangle017
  FaceMaker = 0
  Height = 150
  HorizontalArea = 4174500
  IfcData = attributes={"GlobalId": {"name": "GlobalId", "type": "IfcGloballyUniqueId", "is_enum": false, "enum_values": []}, "Description": {"... (+484 chars omitted),+1 more (map truncated)
  IfcType = 172
  Length = 0
  MoveBase = false
  MoveWithHost = false
  Nodes = (2) [(13597.5,9135,3000),(13597.5,9135,2850)]
  NodesOffset = 0
  Normal = (0,0,-1)
  PerimeterLength = 8810
  Placement = pos=(0,0,9000) rot=(0,0,1;0rad)
  PredefinedType = 0
  VerticalArea = 1321500
  Width = 150
FEATURE [App::GeometryPython] BuildingPart021  label="Losas sobre P3"  # Arch/BIM 172 (typed FeaturePython)
  Area = 0
  Group = -> [Structure337,Structure338,Structure339,Structure340,Structure341,Structure342,Structure343,Structure344,Structure345,Structure346,Structure347,Structure348,Structure349,Structure350,Structure351,Structure352,Structure353]
  Height = 0
  HeightPropagate = true
  IfcData = attributes={"GlobalId": {"name": "GlobalId", "type": "IfcGloballyUniqueId", "is_enum": false, "enum_values": []}, "Description": {"... (+484 chars omitted),+1 more (map truncated)
  IfcType = 172
  LevelOffset = 0
  PredefinedType = 0
FEATURE [Part::FeaturePython] Wall004  label="Tabique Ascensor P3"  # Arch/BIM 166 (typed FeaturePython)
  Align = 1
  Area = 24900000
  Base = -> Rectangle003
  BlockHeight = 0
  BlockLength = 0
  CountBroken = 0
  CountEntire = 0
  Face = 0
  Height = 3000
  HorizontalArea = 1155000
  IfcData = attributes={"GlobalId": {"name": "GlobalId", "type": "IfcGloballyUniqueId", "is_enum": false, "enum_values": []}, "Description": {"... (+533 chars omitted),+1 more (map truncated)
  IfcType = 166
  Joint = 0
  Length = 8300
  MakeBlocks = false
  MoveBase = false
  MoveWithHost = false
  Normal = (0,0,0)
  OffsetFirst = 0
  OffsetSecond = 0
  PerimeterLength = 8300
  Placement = pos=(0,0,9000) rot=(0,0,1;0rad)
  PredefinedType = 0
  VerticalArea = 46200000
  Width = 150
FEATURE [Part::FeaturePython] Structure354  label="V15x40 V102a003"  # Arch/BIM 7 (typed FeaturePython)
  FaceMaker = 0
  Height = 400
  HorizontalArea = 405000
  IfcData = attributes={"GlobalId": {"name": "GlobalId", "type": "IfcGloballyUniqueId", "is_enum": false, "enum_values": []}, "Description": {"... (+475 chars omitted),+1 more (map truncated)
  IfcType = 7
  Length = 2700
  MoveBase = false
  MoveWithHost = false
  Nodes = (2) [(-1.72563e-31,-1.42109e-15,-7.77156e-16),(2700,-1.42109e-15,-7.77156e-16)]
  NodesOffset = 0
  Normal = (0,0,0)
  PerimeterLength = 5700
  Placement = pos=(8935,8295,11800) rot=(0,0,1;3.14159rad)
  PredefinedType = 0
  VerticalArea = 2.28e+06
  Width = 150
FEATURE [Part::FeaturePython] Structure355  label="V15x40 V107a003"  # Arch/BIM 7 (typed FeaturePython)
  FaceMaker = 0
  Height = 400
  HorizontalArea = 405000
  IfcData = attributes={"GlobalId": {"name": "GlobalId", "type": "IfcGloballyUniqueId", "is_enum": false, "enum_values": []}, "Description": {"... (+475 chars omitted),+1 more (map truncated)
  IfcType = 7
  Length = 2700
  MoveBase = false
  MoveWithHost = false
  Nodes = (2) [(-1.72563e-31,-1.42109e-15,-7.77156e-16),(2700,-1.42109e-15,-7.77156e-16)]
  NodesOffset = 0
  Normal = (0,0,0)
  PerimeterLength = 5700
  Placement = pos=(8935,4995,11800) rot=(0,0,1;3.14159rad)
  PredefinedType = 0
  VerticalArea = 2.28e+06
  Width = 150
FEATURE [Part::FeaturePython] Structure356  label="V15x40 V112a003"  # Arch/BIM 7 (typed FeaturePython)
  FaceMaker = 0
  Height = 400
  HorizontalArea = 405000
  IfcData = attributes={"GlobalId": {"name": "GlobalId", "type": "IfcGloballyUniqueId", "is_enum": false, "enum_values": []}, "Description": {"... (+475 chars omitted),+1 more (map truncated)
  IfcType = 7
  Length = 2700
  MoveBase = false
  MoveWithHost = false
  Nodes = (2) [(-1.72563e-31,-1.42109e-15,-7.77156e-16),(2700,-1.42109e-15,-7.77156e-16)]
  NodesOffset = 0
  Normal = (0,0,0)
  PerimeterLength = 5700
  Placement = pos=(8935,1700,11800) rot=(0,0,1;3.14159rad)
  PredefinedType = 0
  VerticalArea = 2.28e+06
  Width = 150
FEATURE [Part::FeaturePython] Structure357  label="V15x40 V130a003"  # Arch/BIM 7 (typed FeaturePython)
  FaceMaker = 0
  Height = 400
  HorizontalArea = 370500
  IfcData = attributes={"GlobalId": {"name": "GlobalId", "type": "IfcGloballyUniqueId", "is_enum": false, "enum_values": []}, "Description": {"... (+475 chars omitted),+1 more (map truncated)
  IfcType = 7
  Length = 2470
  MoveBase = false
  MoveWithHost = false
  Nodes = (2) [(-1.72563e-31,-1.42109e-15,-7.77156e-16),(2470,-1.42109e-15,-7.77156e-16)]
  NodesOffset = 0
  Normal = (0,0,0)
  PerimeterLength = 5240
  Placement = pos=(12010,3425,11800) rot=(0,0,1;1.5708rad)
  PredefinedType = 0
  VerticalArea = 2096000
  Width = 150
FEATURE [Part::FeaturePython] Structure358  label="V15x40 V189"  # Arch/BIM 7 (typed FeaturePython)
  FaceMaker = 0
  Height = 400
  HorizontalArea = 597000
  IfcData = attributes={"GlobalId": {"name": "GlobalId", "type": "IfcGloballyUniqueId", "is_enum": false, "enum_values": []}, "Description": {"... (+475 chars omitted),+1 more (map truncated)
  IfcType = 7
  Length = 3980
  MoveBase = false
  MoveWithHost = false
  Nodes = (2) [(-1.72563e-31,-1.42109e-15,-7.77156e-16),(3980,-1.42109e-15,-7.77156e-16)]
  NodesOffset = 0
  Normal = (0,0,0)
  PerimeterLength = 8260
  Placement = pos=(2055,9900,11800) rot=(0,0,1;0rad)
  PredefinedType = 0
  VerticalArea = 3.304e+06
  Width = 150
FEATURE [Part::FeaturePython] Structure359  label="V15x40 V190"  # Arch/BIM 7 (typed FeaturePython)
  FaceMaker = 0
  Height = 400
  HorizontalArea = 390000
  IfcData = attributes={"GlobalId": {"name": "GlobalId", "type": "IfcGloballyUniqueId", "is_enum": false, "enum_values": []}, "Description": {"... (+475 chars omitted),+1 more (map truncated)
  IfcType = 7
  Length = 2600
  MoveBase = false
  MoveWithHost = false
  Nodes = (2) [(-1.72563e-31,-1.42109e-15,-7.77156e-16),(2600,-1.42109e-15,-7.77156e-16)]
  NodesOffset = 0
  Normal = (0,0,0)
  PerimeterLength = 5500
  Placement = pos=(6285,9900,11800) rot=(0,0,1;0rad)
  PredefinedType = 0
  VerticalArea = 2200000
  Width = 150
FEATURE [Part::FeaturePython] Structure360  label="V15x40 V191"  # Arch/BIM 7 (typed FeaturePython)
  FaceMaker = 0
  Height = 400
  HorizontalArea = 412500
  IfcData = attributes={"GlobalId": {"name": "GlobalId", "type": "IfcGloballyUniqueId", "is_enum": false, "enum_values": []}, "Description": {"... (+475 chars omitted),+1 more (map truncated)
  IfcType = 7
  Length = 2750
  MoveBase = false
  MoveWithHost = false
  Nodes = (2) [(-1.72563e-31,-1.42109e-15,-7.77156e-16),(2750,-1.42109e-15,-7.77156e-16)]
  NodesOffset = 0
  Normal = (0,0,0)
  PerimeterLength = 5800
  Placement = pos=(9135,9900,11800) rot=(0,0,1;0rad)
  PredefinedType = 0
  VerticalArea = 2320000
  Width = 150
FEATURE [Part::FeaturePython] Structure361  label="V15x40 V192"  # Arch/BIM 7 (typed FeaturePython)
  FaceMaker = 0
  Height = 400
  HorizontalArea = 442500
  IfcData = attributes={"GlobalId": {"name": "GlobalId", "type": "IfcGloballyUniqueId", "is_enum": false, "enum_values": []}, "Description": {"... (+475 chars omitted),+1 more (map truncated)
  IfcType = 7
  Length = 2950
  MoveBase = false
  MoveWithHost = false
  Nodes = (2) [(-1.72563e-31,-1.42109e-15,-7.77156e-16),(2950,-1.42109e-15,-7.77156e-16)]
  NodesOffset = 0
  Normal = (0,0,0)
  PerimeterLength = 6200
  Placement = pos=(12135,9900,11800) rot=(0,0,1;0rad)
  PredefinedType = 0
  VerticalArea = 2.48e+06
  Width = 150
FEATURE [Part::FeaturePython] Structure362  label="V15x40 V193"  # Arch/BIM 7 (typed FeaturePython)
  FaceMaker = 0
  Height = 400
  HorizontalArea = 453750
  IfcData = attributes={"GlobalId": {"name": "GlobalId", "type": "IfcGloballyUniqueId", "is_enum": false, "enum_values": []}, "Description": {"... (+475 chars omitted),+1 more (map truncated)
  IfcType = 7
  Length = 3025
  MoveBase = false
  MoveWithHost = false
  Nodes = (2) [(-1.72563e-31,-1.42109e-15,-7.77156e-16),(3025,-1.42109e-15,-7.77156e-16)]
  NodesOffset = 0
  Normal = (0,0,0)
  PerimeterLength = 6350
  Placement = pos=(12085,8370,11800) rot=(0,0,1;0rad)
  PredefinedType = 0
  VerticalArea = 2.54e+06
  Width = 150
FEATURE [Part::FeaturePython] Structure363  label="V15x40 V194"  # Arch/BIM 7 (typed FeaturePython)
  FaceMaker = 0
  Height = 400
  HorizontalArea = 597000
  IfcData = attributes={"GlobalId": {"name": "GlobalId", "type": "IfcGloballyUniqueId", "is_enum": false, "enum_values": []}, "Description": {"... (+475 chars omitted),+1 more (map truncated)
  IfcType = 7
  Length = 3980
  MoveBase = false
  MoveWithHost = false
  Nodes = (2) [(-1.72563e-31,-1.42109e-15,-7.77156e-16),(3980,-1.42109e-15,-7.77156e-16)]
  NodesOffset = 0
  Normal = (0,0,0)
  PerimeterLength = 8260
  Placement = pos=(2055,6640,11800) rot=(0,0,1;0rad)
  PredefinedType = 0
  VerticalArea = 3.304e+06
  Width = 150
FEATURE [Part::FeaturePython] Structure364  label="V15x40 V195"  # Arch/BIM 7 (typed FeaturePython)
  FaceMaker = 0
  Height = 400
  HorizontalArea = 397500
  IfcData = attributes={"GlobalId": {"name": "GlobalId", "type": "IfcGloballyUniqueId", "is_enum": false, "enum_values": []}, "Description": {"... (+475 chars omitted),+1 more (map truncated)
  IfcType = 7
  Length = 2650
  MoveBase = false
  MoveWithHost = false
  Nodes = (2) [(-1.72563e-31,-1.42109e-15,-7.77156e-16),(2650,-1.42109e-15,-7.77156e-16)]
  NodesOffset = 0
  Normal = (0,0,0)
  PerimeterLength = 5600
  Placement = pos=(6285,6640,11800) rot=(0,0,1;0rad)
  PredefinedType = 0
  VerticalArea = 2240000
  Width = 150
FEATURE [Part::FeaturePython] Structure365  label="V15x40 V196"  # Arch/BIM 7 (typed FeaturePython)
  FaceMaker = 0
  Height = 400
  HorizontalArea = 210000
  IfcData = attributes={"GlobalId": {"name": "GlobalId", "type": "IfcGloballyUniqueId", "is_enum": false, "enum_values": []}, "Description": {"... (+475 chars omitted),+1 more (map truncated)
  IfcType = 7
  Length = 1400
  MoveBase = false
  MoveWithHost = false
  Nodes = (2) [(-1.72563e-31,-1.42109e-15,-7.77156e-16),(1400,-1.42109e-15,-7.77156e-16)]
  NodesOffset = 0
  Normal = (0,0,0)
  PerimeterLength = 3100
  Placement = pos=(9085,6640,11800) rot=(0,0,1;0rad)
  PredefinedType = 0
  VerticalArea = 1240000
  Width = 150
FEATURE [Part::FeaturePython] Structure366  label="V15x40 V197"  # Arch/BIM 7 (typed FeaturePython)
  FaceMaker = 0
  Height = 400
  HorizontalArea = 235500
  IfcData = attributes={"GlobalId": {"name": "GlobalId", "type": "IfcGloballyUniqueId", "is_enum": false, "enum_values": []}, "Description": {"... (+475 chars omitted),+1 more (map truncated)
  IfcType = 7
  Length = 1570
  MoveBase = false
  MoveWithHost = false
  Nodes = (2) [(-1.72563e-31,-1.42109e-15,-7.77156e-16),(1570,-1.42109e-15,-7.77156e-16)]
  NodesOffset = 0
  Normal = (0,0,0)
  PerimeterLength = 3440
  Placement = pos=(13655,5970,11800) rot=(0,0,1;3.14159rad)
  PredefinedType = 0
  VerticalArea = 1.376e+06
  Width = 150
FEATURE [Part::FeaturePython] Structure367  label="V15x40 V198"  # Arch/BIM 7 (typed FeaturePython)
  FaceMaker = 0
  Height = 400
  HorizontalArea = 177000
  IfcData = attributes={"GlobalId": {"name": "GlobalId", "type": "IfcGloballyUniqueId", "is_enum": false, "enum_values": []}, "Description": {"... (+475 chars omitted),+1 more (map truncated)
  IfcType = 7
  Length = 1180
  MoveBase = false
  MoveWithHost = false
  Nodes = (2) [(-1.72563e-31,-1.42109e-15,-7.77156e-16),(1180,-1.42109e-15,-7.77156e-16)]
  NodesOffset = 0
  Normal = (0,0,0)
  PerimeterLength = 2660
  Placement = pos=(13905,5970,11800) rot=(0,0,1;0rad)
  PredefinedType = 0
  VerticalArea = 1064000
  Width = 150
FEATURE [Part::FeaturePython] Structure368  label="V15x40 V199"  # Arch/BIM 7 (typed FeaturePython)
  FaceMaker = 0
  Height = 400
  HorizontalArea = 597000
  IfcData = attributes={"GlobalId": {"name": "GlobalId", "type": "IfcGloballyUniqueId", "is_enum": false, "enum_values": []}, "Description": {"... (+475 chars omitted),+1 more (map truncated)
  IfcType = 7
  Length = 3980
  MoveBase = false
  MoveWithHost = false
  Nodes = (2) [(-1.72563e-31,-1.42109e-15,-7.77156e-16),(3980,-1.42109e-15,-7.77156e-16)]
  NodesOffset = 0
  Normal = (0,0,0)
  PerimeterLength = 8260
  Placement = pos=(2055,3350,11800) rot=(0,0,1;0rad)
  PredefinedType = 0
  VerticalArea = 3.304e+06
  Width = 150
FEATURE [Part::FeaturePython] Structure369  label="V15x40 V200"  # Arch/BIM 7 (typed FeaturePython)
  FaceMaker = 0
  Height = 400
  HorizontalArea = 397500
  IfcData = attributes={"GlobalId": {"name": "GlobalId", "type": "IfcGloballyUniqueId", "is_enum": false, "enum_values": []}, "Description": {"... (+475 chars omitted),+1 more (map truncated)
  IfcType = 7
  Length = 2650
  MoveBase = false
  MoveWithHost = false
  Nodes = (2) [(-1.72563e-31,-1.42109e-15,-7.77156e-16),(2650,-1.42109e-15,-7.77156e-16)]
  NodesOffset = 0
  Normal = (0,0,0)
  PerimeterLength = 5600
  Placement = pos=(6285,3350,11800) rot=(0,0,1;0rad)
  PredefinedType = 0
  VerticalArea = 2240000
  Width = 150
FEATURE [Part::FeaturePython] Structure370  label="V15x40 V201"  # Arch/BIM 7 (typed FeaturePython)
  FaceMaker = 0
  Height = 400
  HorizontalArea = 210000
  IfcData = attributes={"GlobalId": {"name": "GlobalId", "type": "IfcGloballyUniqueId", "is_enum": false, "enum_values": []}, "Description": {"... (+475 chars omitted),+1 more (map truncated)
  IfcType = 7
  Length = 1400
  MoveBase = false
  MoveWithHost = false
  Nodes = (2) [(-1.72563e-31,-1.42109e-15,-7.77156e-16),(1400,-1.42109e-15,-7.77156e-16)]
  NodesOffset = 0
  Normal = (0,0,0)
  PerimeterLength = 3100
  Placement = pos=(9085,3350,11800) rot=(0,0,1;0rad)
  PredefinedType = 0
  VerticalArea = 1240000
  Width = 150
FEATURE [Part::FeaturePython] Structure371  label="V15x40 V202"  # Arch/BIM 7 (typed FeaturePython)
  FaceMaker = 0
  Height = 400
  HorizontalArea = 460500
  IfcData = attributes={"GlobalId": {"name": "GlobalId", "type": "IfcGloballyUniqueId", "is_enum": false, "enum_values": []}, "Description": {"... (+475 chars omitted),+1 more (map truncated)
  IfcType = 7
  Length = 3070
  MoveBase = false
  MoveWithHost = false
  Nodes = (2) [(-1.72563e-31,-1.42109e-15,-7.77156e-16),(3070,-1.42109e-15,-7.77156e-16)]
  NodesOffset = 0
  Normal = (0,0,0)
  PerimeterLength = 6440
  Placement = pos=(10635,3350,11800) rot=(0,0,1;0rad)
  PredefinedType = 0
  VerticalArea = 2.576e+06
  Width = 150
FEATURE [Part::FeaturePython] Structure372  label="V15x40 V203"  # Arch/BIM 7 (typed FeaturePython)
  FaceMaker = 0
  Height = 400
  HorizontalArea = 597000
  IfcData = attributes={"GlobalId": {"name": "GlobalId", "type": "IfcGloballyUniqueId", "is_enum": false, "enum_values": []}, "Description": {"... (+475 chars omitted),+1 more (map truncated)
  IfcType = 7
  Length = 3980
  MoveBase = false
  MoveWithHost = false
  Nodes = (2) [(-1.72563e-31,-1.42109e-15,-7.77156e-16),(3980,-1.42109e-15,-7.77156e-16)]
  NodesOffset = 0
  Normal = (0,0,0)
  PerimeterLength = 8260
  Placement = pos=(2055,100,11800) rot=(0,0,1;0rad)
  PredefinedType = 0
  VerticalArea = 3.304e+06
  Width = 150
FEATURE [Part::FeaturePython] Structure373  label="V15x40 V204"  # Arch/BIM 7 (typed FeaturePython)
  FaceMaker = 0
  Height = 400
  HorizontalArea = 390000
  IfcData = attributes={"GlobalId": {"name": "GlobalId", "type": "IfcGloballyUniqueId", "is_enum": false, "enum_values": []}, "Description": {"... (+475 chars omitted),+1 more (map truncated)
  IfcType = 7
  Length = 2600
  MoveBase = false
  MoveWithHost = false
  Nodes = (2) [(-1.72563e-31,-1.42109e-15,-7.77156e-16),(2600,-1.42109e-15,-7.77156e-16)]
  NodesOffset = 0
  Normal = (0,0,0)
  PerimeterLength = 5500
  Placement = pos=(6285,100,11800) rot=(0,0,1;0rad)
  PredefinedType = 0
  VerticalArea = 2200000
  Width = 150
FEATURE [Part::FeaturePython] Structure374  label="V15x40 V205"  # Arch/BIM 7 (typed FeaturePython)
  FaceMaker = 0
  Height = 400
  HorizontalArea = 195000
  IfcData = attributes={"GlobalId": {"name": "GlobalId", "type": "IfcGloballyUniqueId", "is_enum": false, "enum_values": []}, "Description": {"... (+475 chars omitted),+1 more (map truncated)
  IfcType = 7
  Length = 1300
  MoveBase = false
  MoveWithHost = false
  Nodes = (2) [(-1.72563e-31,-1.42109e-15,-7.77156e-16),(1300,-1.42109e-15,-7.77156e-16)]
  NodesOffset = 0
  Normal = (0,0,0)
  PerimeterLength = 2900
  Placement = pos=(9135,100,11800) rot=(0,0,1;0rad)
  PredefinedType = 0
  VerticalArea = 1160000
  Width = 150
FEATURE [Part::FeaturePython] Structure375  label="V15x40 V206"  # Arch/BIM 7 (typed FeaturePython)
  FaceMaker = 0
  Height = 400
  HorizontalArea = 445500
  IfcData = attributes={"GlobalId": {"name": "GlobalId", "type": "IfcGloballyUniqueId", "is_enum": false, "enum_values": []}, "Description": {"... (+475 chars omitted),+1 more (map truncated)
  IfcType = 7
  Length = 2970
  MoveBase = false
  MoveWithHost = false
  Nodes = (2) [(-1.72563e-31,-1.42109e-15,-7.77156e-16),(2970,-1.42109e-15,-7.77156e-16)]
  NodesOffset = 0
  Normal = (0,0,0)
  PerimeterLength = 6240
  Placement = pos=(10685,100,11800) rot=(0,0,1;0rad)
  PredefinedType = 0
  VerticalArea = 2.496e+06
  Width = 150
FEATURE [Part::FeaturePython] Structure376  label="V15x40 V207"  # Arch/BIM 7 (typed FeaturePython)
  FaceMaker = 0
  Height = 400
  HorizontalArea = 465000
  IfcData = attributes={"GlobalId": {"name": "GlobalId", "type": "IfcGloballyUniqueId", "is_enum": false, "enum_values": []}, "Description": {"... (+475 chars omitted),+1 more (map truncated)
  IfcType = 7
  Length = 3100
  MoveBase = false
  MoveWithHost = false
  Nodes = (2) [(-1.72563e-31,-1.42109e-15,-7.77156e-16),(3100,-1.42109e-15,-7.77156e-16)]
  NodesOffset = 0
  Normal = (0,0,0)
  PerimeterLength = 6500
  Placement = pos=(6160,3275,11800) rot=(0,0,-1;1.5708rad)
  PredefinedType = 0
  VerticalArea = 2.6e+06
  Width = 150
FEATURE [Part::FeaturePython] Structure377  label="V15x40 V208"  # Arch/BIM 7 (typed FeaturePython)
  FaceMaker = 0
  Height = 400
  HorizontalArea = 471000
  IfcData = attributes={"GlobalId": {"name": "GlobalId", "type": "IfcGloballyUniqueId", "is_enum": false, "enum_values": []}, "Description": {"... (+475 chars omitted),+1 more (map truncated)
  IfcType = 7
  Length = 3140
  MoveBase = false
  MoveWithHost = false
  Nodes = (2) [(-1.72563e-31,-1.42109e-15,-7.77156e-16),(3140,-1.42109e-15,-7.77156e-16)]
  NodesOffset = 0
  Normal = (0,0,0)
  PerimeterLength = 6580
  Placement = pos=(6160,6565,11800) rot=(0,0,-1;1.5708rad)
  PredefinedType = 0
  VerticalArea = 2.632e+06
  Width = 150
FEATURE [Part::FeaturePython] Structure378  label="V15x40 V209"  # Arch/BIM 7 (typed FeaturePython)
  FaceMaker = 0
  Height = 400
  HorizontalArea = 466500
  IfcData = attributes={"GlobalId": {"name": "GlobalId", "type": "IfcGloballyUniqueId", "is_enum": false, "enum_values": []}, "Description": {"... (+475 chars omitted),+1 more (map truncated)
  IfcType = 7
  Length = 3110
  MoveBase = false
  MoveWithHost = false
  Nodes = (2) [(-1.72563e-31,-1.42109e-15,-7.77156e-16),(3110,-1.42109e-15,-7.77156e-16)]
  NodesOffset = 0
  Normal = (0,0,0)
  PerimeterLength = 6520
  Placement = pos=(6160,9825,11800) rot=(0,0,-1;1.5708rad)
  PredefinedType = 0
  VerticalArea = 2.608e+06
  Width = 150
FEATURE [Part::FeaturePython] Structure379  label="V15x40 V210"  # Arch/BIM 7 (typed FeaturePython)
  FaceMaker = 0
  Height = 400
  HorizontalArea = 457500
  IfcData = attributes={"GlobalId": {"name": "GlobalId", "type": "IfcGloballyUniqueId", "is_enum": false, "enum_values": []}, "Description": {"... (+475 chars omitted),+1 more (map truncated)
  IfcType = 7
  Length = 3050
  MoveBase = false
  MoveWithHost = false
  Nodes = (2) [(-1.72563e-31,-1.42109e-15,-7.77156e-16),(3050,-1.42109e-15,-7.77156e-16)]
  NodesOffset = 0
  Normal = (0,0,0)
  PerimeterLength = 6400
  Placement = pos=(9010,3225,11800) rot=(0,0,-1;1.5708rad)
  PredefinedType = 0
  VerticalArea = 2.56e+06
  Width = 150
FEATURE [Part::FeaturePython] Structure380  label="V15x40 V211"  # Arch/BIM 7 (typed FeaturePython)
  FaceMaker = 0
  Height = 400
  HorizontalArea = 456000
  IfcData = attributes={"GlobalId": {"name": "GlobalId", "type": "IfcGloballyUniqueId", "is_enum": false, "enum_values": []}, "Description": {"... (+475 chars omitted),+1 more (map truncated)
  IfcType = 7
  Length = 3040
  MoveBase = false
  MoveWithHost = false
  Nodes = (2) [(-1.72563e-31,-1.42109e-15,-7.77156e-16),(3040,-1.42109e-15,-7.77156e-16)]
  NodesOffset = 0
  Normal = (0,0,0)
  PerimeterLength = 6380
  Placement = pos=(9010,6515,11800) rot=(0,0,-1;1.5708rad)
  PredefinedType = 0
  VerticalArea = 2.552e+06
  Width = 150
FEATURE [Part::FeaturePython] Structure381  label="V15x40 V212"  # Arch/BIM 7 (typed FeaturePython)
  FaceMaker = 0
  Height = 400
  HorizontalArea = 459000
  IfcData = attributes={"GlobalId": {"name": "GlobalId", "type": "IfcGloballyUniqueId", "is_enum": false, "enum_values": []}, "Description": {"... (+475 chars omitted),+1 more (map truncated)
  IfcType = 7
  Length = 3060
  MoveBase = false
  MoveWithHost = false
  Nodes = (2) [(-1.72563e-31,-1.42109e-15,-7.77156e-16),(3060,-1.42109e-15,-7.77156e-16)]
  NodesOffset = 0
  Normal = (0,0,0)
  PerimeterLength = 6420
  Placement = pos=(9010,9825,11800) rot=(0,0,-1;1.5708rad)
  PredefinedType = 0
  VerticalArea = 2.568e+06
  Width = 150
FEATURE [Part::FeaturePython] Structure382  label="V15x40 V213"  # Arch/BIM 7 (typed FeaturePython)
  FaceMaker = 0
  Height = 400
  HorizontalArea = 457500
  IfcData = attributes={"GlobalId": {"name": "GlobalId", "type": "IfcGloballyUniqueId", "is_enum": false, "enum_values": []}, "Description": {"... (+475 chars omitted),+1 more (map truncated)
  IfcType = 7
  Length = 3050
  MoveBase = false
  MoveWithHost = false
  Nodes = (2) [(-1.72563e-31,-1.42109e-15,-7.77156e-16),(3050,-1.42109e-15,-7.77156e-16)]
  NodesOffset = 0
  Normal = (0,0,0)
  PerimeterLength = 6400
  Placement = pos=(10560,3225,11800) rot=(0,0,-1;1.5708rad)
  PredefinedType = 0
  VerticalArea = 2.56e+06
  Width = 150
FEATURE [Part::FeaturePython] Structure383  label="V15x40 V214"  # Arch/BIM 7 (typed FeaturePython)
  FaceMaker = 0
  Height = 400
  HorizontalArea = 363000
  IfcData = attributes={"GlobalId": {"name": "GlobalId", "type": "IfcGloballyUniqueId", "is_enum": false, "enum_values": []}, "Description": {"... (+475 chars omitted),+1 more (map truncated)
  IfcType = 7
  Length = 2420
  MoveBase = false
  MoveWithHost = false
  Nodes = (2) [(-1.72563e-31,-1.42109e-15,-7.77156e-16),(2420,-1.42109e-15,-7.77156e-16)]
  NodesOffset = 0
  Normal = (0,0,0)
  PerimeterLength = 5140
  Placement = pos=(10560,3475,11800) rot=(0,0,1;1.5708rad)
  PredefinedType = 0
  VerticalArea = 2056000
  Width = 150
FEATURE [Part::FeaturePython] Structure384  label="V15x40 V215"  # Arch/BIM 7 (typed FeaturePython)
  FaceMaker = 0
  Height = 400
  HorizontalArea = 207000
  IfcData = attributes={"GlobalId": {"name": "GlobalId", "type": "IfcGloballyUniqueId", "is_enum": false, "enum_values": []}, "Description": {"... (+475 chars omitted),+1 more (map truncated)
  IfcType = 7
  Length = 1380
  MoveBase = false
  MoveWithHost = false
  Nodes = (2) [(-1.72563e-31,-1.42109e-15,-7.77156e-16),(1380,-1.42109e-15,-7.77156e-16)]
  NodesOffset = 0
  Normal = (0,0,0)
  PerimeterLength = 3060
  Placement = pos=(10560,8445,11800) rot=(0,0,1;1.5708rad)
  PredefinedType = 0
  VerticalArea = 1224000
  Width = 150
FEATURE [Part::FeaturePython] Structure385  label="V15x40 V216"  # Arch/BIM 7 (typed FeaturePython)
  FaceMaker = 0
  Height = 400
  HorizontalArea = 207000
  IfcData = attributes={"GlobalId": {"name": "GlobalId", "type": "IfcGloballyUniqueId", "is_enum": false, "enum_values": []}, "Description": {"... (+475 chars omitted),+1 more (map truncated)
  IfcType = 7
  Length = 1380
  MoveBase = false
  MoveWithHost = false
  Nodes = (2) [(-1.72563e-31,-1.42109e-15,-7.77156e-16),(1380,-1.42109e-15,-7.77156e-16)]
  NodesOffset = 0
  Normal = (0,0,0)
  PerimeterLength = 3060
  Placement = pos=(12010,9825,11800) rot=(0,0,-1;1.5708rad)
  PredefinedType = 0
  VerticalArea = 1224000
  Width = 150
FEATURE [Part::FeaturePython] Structure386  label="V20x40 V148"  # Arch/BIM 7 (typed FeaturePython)
  FaceMaker = 0
  Height = 400
  HorizontalArea = 615000
  IfcData = attributes={"GlobalId": {"name": "GlobalId", "type": "IfcGloballyUniqueId", "is_enum": false, "enum_values": []}, "Description": {"... (+475 chars omitted),+1 more (map truncated)
  IfcType = 7
  Length = 3075
  MoveBase = false
  MoveWithHost = false
  Nodes = (2) [(-1.72563e-31,0,-7.77156e-16),(3075,0,-7.77156e-16)]
  NodesOffset = 0
  Normal = (0,0,0)
  PerimeterLength = 6550
  Placement = pos=(1930,3250,11800) rot=(0,0,-1;1.5708rad)
  PredefinedType = 0
  VerticalArea = 2.62e+06
  Width = 200
FEATURE [Part::FeaturePython] Structure387  label="V20x40 V149"  # Arch/BIM 7 (typed FeaturePython)
  FaceMaker = 0
  Height = 400
  HorizontalArea = 618000
  IfcData = attributes={"GlobalId": {"name": "GlobalId", "type": "IfcGloballyUniqueId", "is_enum": false, "enum_values": []}, "Description": {"... (+475 chars omitted),+1 more (map truncated)
  IfcType = 7
  Length = 3090
  MoveBase = false
  MoveWithHost = false
  Nodes = (2) [(-1.72563e-31,0,-7.77156e-16),(3090,0,-7.77156e-16)]
  NodesOffset = 0
  Normal = (0,0,0)
  PerimeterLength = 6580
  Placement = pos=(1930,6540,11800) rot=(0,0,-1;1.5708rad)
  PredefinedType = 0
  VerticalArea = 2.632e+06
  Width = 200
FEATURE [Part::FeaturePython] Structure388  label="V20x40 V150"  # Arch/BIM 7 (typed FeaturePython)
  FaceMaker = 0
  Height = 400
  HorizontalArea = 617000
  IfcData = attributes={"GlobalId": {"name": "GlobalId", "type": "IfcGloballyUniqueId", "is_enum": false, "enum_values": []}, "Description": {"... (+475 chars omitted),+1 more (map truncated)
  IfcType = 7
  Length = 3085
  MoveBase = false
  MoveWithHost = false
  Nodes = (2) [(-1.72563e-31,0,-7.77156e-16),(3085,0,-7.77156e-16)]
  NodesOffset = 0
  Normal = (0,0,0)
  PerimeterLength = 6570
  Placement = pos=(1930,9825,11800) rot=(0,0,-1;1.5708rad)
  PredefinedType = 0
  VerticalArea = 2.628e+06
  Width = 200
FEATURE [Part::FeaturePython] Structure389  label="V20x40 V151"  # Arch/BIM 7 (typed FeaturePython)
  FaceMaker = 0
  Height = 400
  HorizontalArea = 635000
  IfcData = attributes={"GlobalId": {"name": "GlobalId", "type": "IfcGloballyUniqueId", "is_enum": false, "enum_values": []}, "Description": {"... (+475 chars omitted),+1 more (map truncated)
  IfcType = 7
  Length = 3175
  MoveBase = false
  MoveWithHost = false
  Nodes = (2) [(-1.72563e-31,0,-7.77156e-16),(3175,0,-7.77156e-16)]
  NodesOffset = 0
  Normal = (0,0,0)
  PerimeterLength = 6750
  Placement = pos=(13780,175,11800) rot=(0,0,1;1.5708rad)
  PredefinedType = 0
  VerticalArea = 2.7e+06
  Width = 200
FEATURE [Part::FeaturePython] Structure390  label="V20x40 V152"  # Arch/BIM 7 (typed FeaturePython)
  FaceMaker = 0
  Height = 400
  HorizontalArea = 509000
  IfcData = attributes={"GlobalId": {"name": "GlobalId", "type": "IfcGloballyUniqueId", "is_enum": false, "enum_values": []}, "Description": {"... (+475 chars omitted),+1 more (map truncated)
  IfcType = 7
  Length = 2545
  MoveBase = false
  MoveWithHost = false
  Nodes = (2) [(-1.72563e-31,0,-7.77156e-16),(2545,0,-7.77156e-16)]
  NodesOffset = 0
  Normal = (0,0,0)
  PerimeterLength = 5490
  Placement = pos=(13780,3350,11800) rot=(0,0,1;1.5708rad)
  PredefinedType = 0
  VerticalArea = 2196000
  Width = 200
FEATURE [Part::FeaturePython] Structure391  label="V20x40 V153"  # Arch/BIM 7 (typed FeaturePython)
  FaceMaker = 0
  Height = 400
  HorizontalArea = 756000
  IfcData = attributes={"GlobalId": {"name": "GlobalId", "type": "IfcGloballyUniqueId", "is_enum": false, "enum_values": []}, "Description": {"... (+475 chars omitted),+1 more (map truncated)
  IfcType = 7
  Length = 3780
  MoveBase = false
  MoveWithHost = false
  Nodes = (2) [(-1.72563e-31,0,-7.77156e-16),(3780,0,-7.77156e-16)]
  NodesOffset = 0
  Normal = (0,0,0)
  PerimeterLength = 7960
  Placement = pos=(15210,6045,11800) rot=(0,0,1;1.5708rad)
  PredefinedType = 0
  VerticalArea = 3.184e+06
  Width = 200
FEATURE [App::GeometryPython] BuildingPart022  label="Vigas sobre P3"  # Arch/BIM 172 (typed FeaturePython)
  Area = 0
  Group = -> [Structure354,Structure355,Structure356,Structure357,Structure358,Structure359,Structure360,Structure361,Structure362,Structure363,Structure364,Structure365,Structure366,Structure367,Structure368,Structure369,Structure370,Structure371,Structure372,Structure373,Structure374,Structure375,Structure376,Structure377,Structure378,Structure379,Structure380,Structure381,Structure382,Structure383,+8 more]
  Height = 0
  HeightPropagate = true
  IfcData = attributes={"GlobalId": {"name": "GlobalId", "type": "IfcGloballyUniqueId", "is_enum": false, "enum_values": []}, "Description": {"... (+484 chars omitted),+1 more (map truncated)
  IfcType = 172
  LevelOffset = 0
  PredefinedType = 0
FEATURE [App::GeometryPython] BuildingPart019  label="Piso 3"  # Arch/BIM 172 (typed FeaturePython)
  Area = 24900000
  Group = -> [BuildingPart020,BuildingPart021,Wall004,BuildingPart022]
  Height = 0
  HeightPropagate = true
  IfcData = attributes={"GlobalId": {"name": "GlobalId", "type": "IfcGloballyUniqueId", "is_enum": false, "enum_values": []}, "Description": {"... (+484 chars omitted),+1 more (map truncated)
  IfcType = 172
  LevelOffset = 0
  Placement = pos=(0,0,9000) rot=(0,0,1;0rad)
  PredefinedType = 0
FEATURE [App::GeometryPython] BuildingPart024  label="Sobre Terraza"  # Arch/BIM 172 (typed FeaturePython)
  Area = 0
  Height = 0
  HeightPropagate = true
  IfcData = attributes={"GlobalId": {"name": "GlobalId", "type": "IfcGloballyUniqueId", "is_enum": false, "enum_values": []}, "Description": {"... (+484 chars omitted),+1 more (map truncated)
  IfcType = 172
  LevelOffset = 0
  PredefinedType = 0
FEATURE [Part::FeaturePython] Structure392  label="Column"  # Arch/BIM 24 (typed FeaturePython)
  FaceMaker = 0
  Height = 3000
  HorizontalArea = 22500
  IfcData = attributes={"GlobalId": {"name": "GlobalId", "type": "IfcGloballyUniqueId", "is_enum": false, "enum_values": []}, "Description": {"... (+438 chars omitted),+1 more (map truncated)
  IfcType = 24
  Length = 150
  MoveBase = false
  MoveWithHost = false
  Nodes = (2) [(2.77556e-16,7.57912e-16,0),(2.77556e-16,7.57912e-16,3000)]
  NodesOffset = 0
  Normal = (0,0,0)
  PerimeterLength = 600
  Placement = pos=(15210,9900,12000) rot=(0,0,1;0rad)
  PredefinedType = 0
  VerticalArea = 1800000
  Width = 150
FEATURE [Part::FeaturePython] Structure393  label="Column001"  # Arch/BIM 24 (typed FeaturePython)
  FaceMaker = 0
  Height = 3000
  HorizontalArea = 22500
  IfcData = attributes={"GlobalId": {"name": "GlobalId", "type": "IfcGloballyUniqueId", "is_enum": false, "enum_values": []}, "Description": {"... (+438 chars omitted),+1 more (map truncated)
  IfcType = 24
  Length = 150
  MoveBase = false
  MoveWithHost = false
  Nodes = (2) [(2.77556e-16,7.57912e-16,0),(2.77556e-16,7.57912e-16,3000)]
  NodesOffset = 0
  Normal = (0,0,0)
  PerimeterLength = 600
  Placement = pos=(10560,9900,12000) rot=(0,0,1;0rad)
  PredefinedType = 0
  VerticalArea = 1800000
  Width = 150
FEATURE [Part::FeaturePython] Structure394  label="Column002"  # Arch/BIM 24 (typed FeaturePython)
  FaceMaker = 0
  Height = 3000
  HorizontalArea = 22500
  IfcData = attributes={"GlobalId": {"name": "GlobalId", "type": "IfcGloballyUniqueId", "is_enum": false, "enum_values": []}, "Description": {"... (+438 chars omitted),+1 more (map truncated)
  IfcType = 24
  Length = 150
  MoveBase = false
  MoveWithHost = false
  Nodes = (2) [(2.77556e-16,7.57912e-16,0),(2.77556e-16,7.57912e-16,3000)]
  NodesOffset = 0
  Normal = (0,0,0)
  PerimeterLength = 600
  Placement = pos=(15210,5970,12000) rot=(0,0,1;0rad)
  PredefinedType = 0
  VerticalArea = 1800000
  Width = 150
FEATURE [Part::FeaturePython] Structure395  label="Column003"  # Arch/BIM 24 (typed FeaturePython)
  FaceMaker = 0
  Height = 3000
  HorizontalArea = 22500
  IfcData = attributes={"GlobalId": {"name": "GlobalId", "type": "IfcGloballyUniqueId", "is_enum": false, "enum_values": []}, "Description": {"... (+438 chars omitted),+1 more (map truncated)
  IfcType = 24
  Length = 150
  MoveBase = false
  MoveWithHost = false
  Nodes = (2) [(2.77556e-16,7.57912e-16,0),(2.77556e-16,7.57912e-16,3000)]
  NodesOffset = 0
  Normal = (0,0,0)
  PerimeterLength = 600
  Placement = pos=(10560,5970,12000) rot=(0,0,1;0rad)
  PredefinedType = 0
  VerticalArea = 1800000
  Width = 150
FEATURE [Part::FeaturePython] Structure396  label="Beam042"  # Arch/BIM 7 (typed FeaturePython)
  FaceMaker = 0
  Height = 300
  HorizontalArea = 675000
  IfcData = attributes={"GlobalId": {"name": "GlobalId", "type": "IfcGloballyUniqueId", "is_enum": false, "enum_values": []}, "Description": {"... (+475 chars omitted),+1 more (map truncated)
  IfcType = 7
  Length = 4500
  MoveBase = false
  MoveWithHost = false
  Nodes = (2) [(1.2326e-31,-7.57912e-16,5.55112e-16),(4500,-7.57912e-16,5.55112e-16)]
  NodesOffset = 0
  Normal = (0,0,0)
  PerimeterLength = 9300
  Placement = pos=(10635,9900,14850) rot=(0,0,1;0rad)
  PredefinedType = 0
  VerticalArea = 2790000
  Width = 150
FEATURE [Part::FeaturePython] Structure397  label="Beam043"  # Arch/BIM 7 (typed FeaturePython)
  FaceMaker = 0
  Height = 300
  HorizontalArea = 567000
  IfcData = attributes={"GlobalId": {"name": "GlobalId", "type": "IfcGloballyUniqueId", "is_enum": false, "enum_values": []}, "Description": {"... (+475 chars omitted),+1 more (map truncated)
  IfcType = 7
  Length = 3780
  MoveBase = false
  MoveWithHost = false
  Nodes = (2) [(1.2326e-31,-7.57912e-16,5.55112e-16),(3780,-7.57912e-16,5.55112e-16)]
  NodesOffset = 0
  Normal = (0,0,0)
  PerimeterLength = 7860
  Placement = pos=(15210,9825,14850) rot=(0,0,-1;1.5708rad)
  PredefinedType = 0
  VerticalArea = 2.358e+06
  Width = 150
FEATURE [Part::FeaturePython] Structure398  label="Beam044"  # Arch/BIM 7 (typed FeaturePython)
  FaceMaker = 0
  Height = 300
  HorizontalArea = 675000
  IfcData = attributes={"GlobalId": {"name": "GlobalId", "type": "IfcGloballyUniqueId", "is_enum": false, "enum_values": []}, "Description": {"... (+475 chars omitted),+1 more (map truncated)
  IfcType = 7
  Length = 4500
  MoveBase = false
  MoveWithHost = false
  Nodes = (2) [(1.2326e-31,-7.57912e-16,5.55112e-16),(4500,-7.57912e-16,5.55112e-16)]
  NodesOffset = 0
  Normal = (0,0,0)
  PerimeterLength = 9300
  Placement = pos=(15135,5970,14850) rot=(0,0,1;3.14159rad)
  PredefinedType = 0
  VerticalArea = 2790000
  Width = 150
FEATURE [Part::FeaturePython] Structure399  label="Beam045"  # Arch/BIM 7 (typed FeaturePython)
  FaceMaker = 0
  Height = 300
  HorizontalArea = 567000
  IfcData = attributes={"GlobalId": {"name": "GlobalId", "type": "IfcGloballyUniqueId", "is_enum": false, "enum_values": []}, "Description": {"... (+475 chars omitted),+1 more (map truncated)
  IfcType = 7
  Length = 3780
  MoveBase = false
  MoveWithHost = false
  Nodes = (2) [(1.2326e-31,-7.57912e-16,5.55112e-16),(3780,-7.57912e-16,5.55112e-16)]
  NodesOffset = 0
  Normal = (0,0,0)
  PerimeterLength = 7860
  Placement = pos=(10560,6045,14850) rot=(0,0,1;1.5708rad)
  PredefinedType = 0
  VerticalArea = 2.358e+06
  Width = 150
FEATURE [App::GeometryPython] BuildingPart025  label="Vigas sobre Terraza"  # Arch/BIM 172 (typed FeaturePython)
  Area = 0
  Group = -> [Structure396,Structure397,Structure398,Structure399]
  Height = 0
  HeightPropagate = true
  IfcData = attributes={"GlobalId": {"name": "GlobalId", "type": "IfcGloballyUniqueId", "is_enum": false, "enum_values": []}, "Description": {"... (+484 chars omitted),+1 more (map truncated)
  IfcType = 172
  LevelOffset = 0
  Placement = pos=(0,0,12000) rot=(0,0,1;0rad)
  PredefinedType = 0
FEATURE [App::GeometryPython] BuildingPart026  label="Columnas Terraza"  # Arch/BIM 172 (typed FeaturePython)
  Area = 0
  Group = -> [Structure392,Structure393,Structure394,Structure395]
  Height = 0
  HeightPropagate = true
  IfcData = attributes={"GlobalId": {"name": "GlobalId", "type": "IfcGloballyUniqueId", "is_enum": false, "enum_values": []}, "Description": {"... (+484 chars omitted),+1 more (map truncated)
  IfcType = 172
  LevelOffset = 0
  Placement = pos=(0,0,12000) rot=(0,0,1;0rad)
  PredefinedType = 0
FEATURE [Part::Part2DObjectPython] Rectangle021  # Draft 2D object (typed FeaturePython)
  Area = 1.701e+07
  ChamferSize = 0
  Columns = 1
  FilletRadius = 0
  Height = 3780
  Length = 4500
  MakeFace = true
  Placement = pos=(10635,6045,15000) rot=(0,0,1;0rad)
  Rows = 1
FEATURE [Part::FeaturePython] Structure400  label="Structure"  # Arch/BIM 172 (typed FeaturePython)
  Base = -> Rectangle021
  FaceMaker = 0
  Height = 150
  HorizontalArea = 1.701e+07
  IfcData = attributes={"GlobalId": {"name": "GlobalId", "type": "IfcGloballyUniqueId", "is_enum": false, "enum_values": []}, "Description": {"... (+484 chars omitted),+1 more (map truncated)
  IfcType = 172
  Length = 0
  MoveBase = false
  MoveWithHost = false
  Nodes = (2) [(12885,7935,15000),(12885,7935,14850)]
  NodesOffset = 0
  Normal = (0,0,-1)
  PerimeterLength = 16560
  PredefinedType = 0
  VerticalArea = 2484000
  Width = 150
FEATURE [App::GeometryPython] BuildingPart027  label="Losas sobre Terraza"  # Arch/BIM 172 (typed FeaturePython)
  Area = 0
  Group = -> [Structure400]
  Height = 0
  HeightPropagate = true
  IfcData = attributes={"GlobalId": {"name": "GlobalId", "type": "IfcGloballyUniqueId", "is_enum": false, "enum_values": []}, "Description": {"... (+484 chars omitted),+1 more (map truncated)
  IfcType = 172
  LevelOffset = 0
  Placement = pos=(0,0,12000) rot=(0,0,1;0rad)
  PredefinedType = 0
FEATURE [App::GeometryPython] BuildingPart023  label="Terraza"  # Arch/BIM 172 (typed FeaturePython)
  Area = 0
  Group = -> [BuildingPart026,BuildingPart025,BuildingPart027]
  Height = 0
  HeightPropagate = true
  IfcData = attributes={"GlobalId": {"name": "GlobalId", "type": "IfcGloballyUniqueId", "is_enum": false, "enum_values": []}, "Description": {"... (+484 chars omitted),+1 more (map truncated)
  IfcType = 172
  LevelOffset = 0
  Placement = pos=(0,0,12000) rot=(0,0,1;0rad)
  PredefinedType = 0
FEATURE [Part::FeaturePython] Axis004  label="Horizontal corta"  # WARN: FeaturePython — macro-defined, semantics opaque (R4)
  Angles = [0,0,0,0,0,0]
  Distances = [100,3250,2620,670,1730,1530]
  Length = 18000
  Placement = pos=(17000,1.077e-12,0) rot=(0,0,1;1.5708rad)
FEATURE [App::DocumentObjectGroup] Group  label="Rejillas"
  Group = -> [Axis002,Axis,Axis004]
FEATURE [App::DocumentObjectGroup] Group004  label="2D-Nivel 0"
  Group = -> [Line,Line001,Line002,Line003,Line004,Line005,Line006,Line007,Line008,Line009,Line010,Line011]
FEATURE [App::DocumentObjectGroup] Group003  label="Anotaciones"
  Group = -> [Group004,Group,Rectangle001]
FEATURE [App::MaterialObjectPython] Material  label="Hormigon Armado"  # material (typed FeaturePython)
  Description = HA
  Material = Description=HA,DiffuseColor=(0.8500000238418579, 0.8500000238418579, 0.8500000238418579),Name=Hormigon Armado,+2 more (map truncated)
  Transparency = 0
FEATURE [Part::FeaturePython] Structure  label="CAB PIL 1"  # Arch/BIM 77 (typed FeaturePython)
  Base = -> Rectangle002
  Description = Pilote rectangular
  FaceMaker = 0
  Height = 700
  HorizontalArea = 490000
  IfcData = attributes={"GlobalId": {"name": "GlobalId", "type": "IfcGloballyUniqueId", "is_enum": false, "enum_values": []}, "Description": {"... (+547 chars omitted),+1 more (map truncated)
  IfcType = 77
  Length = 0
  Material = -> Material
  MoveBase = false
  MoveWithHost = false
  Nodes = (2) [(15210,9900,0),(15210,9900,-700)]
  NodesOffset = 0
  Normal = (0,0,-1)
  PerimeterLength = 2800
  Placement = pos=(-13280,1.819e-12,-500) rot=(0,0,1;0rad)
  PredefinedType = 3
  Tag = B1
  VerticalArea = 1960000
  Width = 0
  expr: Height = <<Estructura>>.CabEsp
FEATURE [Part::FeaturePython] Structure001  label="PIL 1"  # Arch/BIM 96 (typed FeaturePython)
  Base = -> Circle
  ConstructionType = 0
  Description = Pilote circular
  FaceMaker = 0
  Height = 8000
  HorizontalArea = 196350
  IfcData = attributes={"GlobalId": {"name": "GlobalId", "type": "IfcGloballyUniqueId", "is_enum": false, "enum_values": []}, "Description": {"... (+752 chars omitted),+1 more (map truncated)
  IfcType = 96
  Length = 0
  Material = -> Material
  MoveBase = false
  MoveWithHost = false
  Nodes = (2) [(15210,9900,0),(15210,9900,-8000)]
  NodesOffset = 0
  Normal = (0,0,-1)
  PerimeterLength = 1570.8
  Placement = pos=(-13280,1.819e-12,-1200) rot=(0,0,1;0rad)
  PredefinedType = 5
  VerticalArea = 1.25664e+07
  Width = 100
  expr: Height = <<Estructura>>.PilProf
FEATURE [Part::FeaturePython] Structure002  label="CAB PIL 6"  # Arch/BIM 172 (typed FeaturePython)
  CloneOf = -> Structure
  FaceMaker = 0
  Height = 700
  HorizontalArea = 490000
  IfcData = attributes={"GlobalId": {"name": "GlobalId", "type": "IfcGloballyUniqueId", "is_enum": false, "enum_values": []}, "Description": {"... (+484 chars omitted),+1 more (map truncated)
  IfcType = 172
  Length = 0
  Material = -> Material
  MoveBase = false
  MoveWithHost = false
  Nodes = (2) [(15210,9900,0),(15210,9900,-700)]
  NodesOffset = 0
  Normal = (0,0,0)
  PerimeterLength = 2800
  Placement = pos=(-13280,-3260,-500) rot=(0,0,1;0rad)
  PredefinedType = 0
  VerticalArea = 1960000
  Width = 0
FEATURE [Part::FeaturePython] Structure003  label="PIL 6"  # Arch/BIM 172 (typed FeaturePython)
  CloneOf = -> Structure001
  FaceMaker = 0
  Height = 8000
  HorizontalArea = 196350
  IfcData = attributes={"GlobalId": {"name": "GlobalId", "type": "IfcGloballyUniqueId", "is_enum": false, "enum_values": []}, "Description": {"... (+484 chars omitted),+1 more (map truncated)
  IfcType = 172
  Length = 0
  Material = -> Material
  MoveBase = false
  MoveWithHost = false
  Nodes = (2) [(15210,9900,0),(15210,9900,-8000)]
  NodesOffset = 0
  Normal = (0,0,0)
  PerimeterLength = 1570.8
  Placement = pos=(-13280,-3260,-1200) rot=(0,0,1;0rad)
  PredefinedType = 0
  VerticalArea = 1.25664e+07
  Width = 100
FEATURE [Part::FeaturePython] Structure004  label="CAB PIL 11"  # Arch/BIM 172 (typed FeaturePython)
  CloneOf = -> Structure
  FaceMaker = 0
  Height = 700
  HorizontalArea = 490000
  IfcData = attributes={"GlobalId": {"name": "GlobalId", "type": "IfcGloballyUniqueId", "is_enum": false, "enum_values": []}, "Description": {"... (+484 chars omitted),+1 more (map truncated)
  IfcType = 172
  Length = 0
  Material = -> Material
  MoveBase = false
  MoveWithHost = false
  Nodes = (2) [(15210,9900,0),(15210,9900,-700)]
  NodesOffset = 0
  Normal = (0,0,0)
  PerimeterLength = 2800
  Placement = pos=(-13280,-6550,-500) rot=(0,0,1;0rad)
  PredefinedType = 0
  VerticalArea = 1960000
  Width = 0
FEATURE [Part::FeaturePython] Structure005  label="PIL 11"  # Arch/BIM 172 (typed FeaturePython)
  CloneOf = -> Structure001
  FaceMaker = 0
  Height = 8000
  HorizontalArea = 196350
  IfcData = attributes={"GlobalId": {"name": "GlobalId", "type": "IfcGloballyUniqueId", "is_enum": false, "enum_values": []}, "Description": {"... (+484 chars omitted),+1 more (map truncated)
  IfcType = 172
  Length = 0
  Material = -> Material
  MoveBase = false
  MoveWithHost = false
  Nodes = (2) [(15210,9900,0),(15210,9900,-8000)]
  NodesOffset = 0
  Normal = (0,0,0)
  PerimeterLength = 1570.8
  Placement = pos=(-13280,-6550,-1200) rot=(0,0,1;0rad)
  PredefinedType = 0
  VerticalArea = 1.25664e+07
  Width = 100
FEATURE [Part::FeaturePython] Structure006  label="CAB PIL 2"  # Arch/BIM 172 (typed FeaturePython)
  CloneOf = -> Structure
  FaceMaker = 0
  Height = 700
  HorizontalArea = 490000
  IfcData = attributes={"GlobalId": {"name": "GlobalId", "type": "IfcGloballyUniqueId", "is_enum": false, "enum_values": []}, "Description": {"... (+484 chars omitted),+1 more (map truncated)
  IfcType = 172
  Length = 0
  Material = -> Material
  MoveBase = false
  MoveWithHost = false
  Nodes = (2) [(15210,9900,0),(15210,9900,-700)]
  NodesOffset = 0
  Normal = (0,0,0)
  PerimeterLength = 2800
  Placement = pos=(-9050,0,-500) rot=(0,0,1;0rad)
  PredefinedType = 0
  VerticalArea = 1960000
  Width = 0
FEATURE [Part::FeaturePython] Structure007  label="PIL 2"  # Arch/BIM 172 (typed FeaturePython)
  CloneOf = -> Structure001
  FaceMaker = 0
  Height = 8000
  HorizontalArea = 196350
  IfcData = attributes={"GlobalId": {"name": "GlobalId", "type": "IfcGloballyUniqueId", "is_enum": false, "enum_values": []}, "Description": {"... (+484 chars omitted),+1 more (map truncated)
  IfcType = 172
  Length = 0
  Material = -> Material
  MoveBase = false
  MoveWithHost = false
  Nodes = (2) [(15210,9900,0),(15210,9900,-8000)]
  NodesOffset = 0
  Normal = (0,0,0)
  PerimeterLength = 1570.8
  Placement = pos=(-9050,0,-1200) rot=(0,0,1;0rad)
  PredefinedType = 0
  VerticalArea = 1.25664e+07
  Width = 100
FEATURE [Part::FeaturePython] Structure008  label="CAB PIL 3"  # Arch/BIM 172 (typed FeaturePython)
  CloneOf = -> Structure
  FaceMaker = 0
  Height = 700
  HorizontalArea = 490000
  IfcData = attributes={"GlobalId": {"name": "GlobalId", "type": "IfcGloballyUniqueId", "is_enum": false, "enum_values": []}, "Description": {"... (+484 chars omitted),+1 more (map truncated)
  IfcType = 172
  Length = 0
  Material = -> Material
  MoveBase = false
  MoveWithHost = false
  Nodes = (2) [(15210,9900,0),(15210,9900,-700)]
  NodesOffset = 0
  Normal = (0,0,0)
  PerimeterLength = 2800
  Placement = pos=(-6200,0,-500) rot=(0,0,1;0rad)
  PredefinedType = 0
  VerticalArea = 1960000
  Width = 0
FEATURE [Part::FeaturePython] Structure009  label="PIL 3"  # Arch/BIM 172 (typed FeaturePython)
  CloneOf = -> Structure001
  FaceMaker = 0
  Height = 8000
  HorizontalArea = 196350
  IfcData = attributes={"GlobalId": {"name": "GlobalId", "type": "IfcGloballyUniqueId", "is_enum": false, "enum_values": []}, "Description": {"... (+484 chars omitted),+1 more (map truncated)
  IfcType = 172
  Length = 0
  Material = -> Material
  MoveBase = false
  MoveWithHost = false
  Nodes = (2) [(15210,9900,0),(15210,9900,-8000)]
  NodesOffset = 0
  Normal = (0,0,0)
  PerimeterLength = 1570.8
  Placement = pos=(-6200,0,-1200) rot=(0,0,1;0rad)
  PredefinedType = 0
  VerticalArea = 1.25664e+07
  Width = 100
FEATURE [Part::FeaturePython] Structure010  label="CAB PIL 4"  # Arch/BIM 172 (typed FeaturePython)
  CloneOf = -> Structure
  FaceMaker = 0
  Height = 700
  HorizontalArea = 490000
  IfcData = attributes={"GlobalId": {"name": "GlobalId", "type": "IfcGloballyUniqueId", "is_enum": false, "enum_values": []}, "Description": {"... (+484 chars omitted),+1 more (map truncated)
  IfcType = 172
  Length = 0
  Material = -> Material
  MoveBase = false
  MoveWithHost = false
  Nodes = (2) [(15210,9900,0),(15210,9900,-700)]
  NodesOffset = 0
  Normal = (0,0,0)
  PerimeterLength = 2800
  Placement = pos=(-3200,0,-500) rot=(0,0,1;0rad)
  PredefinedType = 0
  VerticalArea = 1960000
  Width = 0
FEATURE [Part::FeaturePython] Structure011  label="PIL 4"  # Arch/BIM 172 (typed FeaturePython)
  CloneOf = -> Structure001
  FaceMaker = 0
  Height = 8000
  HorizontalArea = 196350
  IfcData = attributes={"GlobalId": {"name": "GlobalId", "type": "IfcGloballyUniqueId", "is_enum": false, "enum_values": []}, "Description": {"... (+484 chars omitted),+1 more (map truncated)
  IfcType = 172
  Length = 0
  Material = -> Material
  MoveBase = false
  MoveWithHost = false
  Nodes = (2) [(15210,9900,0),(15210,9900,-8000)]
  NodesOffset = 0
  Normal = (0,0,0)
  PerimeterLength = 1570.8
  Placement = pos=(-3200,0,-1200) rot=(0,0,1;0rad)
  PredefinedType = 0
  VerticalArea = 1.25664e+07
  Width = 100
FEATURE [Part::FeaturePython] Structure012  label="CAB PIL 5"  # Arch/BIM 172 (typed FeaturePython)
  CloneOf = -> Structure
  FaceMaker = 0
  Height = 700
  HorizontalArea = 490000
  IfcData = attributes={"GlobalId": {"name": "GlobalId", "type": "IfcGloballyUniqueId", "is_enum": false, "enum_values": []}, "Description": {"... (+484 chars omitted),+1 more (map truncated)
  IfcType = 172
  Length = 0
  Material = -> Material
  MoveBase = false
  MoveWithHost = false
  Nodes = (2) [(15210,9900,0),(15210,9900,-700)]
  NodesOffset = 0
  Normal = (0,0,0)
  PerimeterLength = 2800
  Placement = pos=(-9.09e-13,0,-500) rot=(0,0,1;0rad)
  PredefinedType = 0
  VerticalArea = 1960000
  Width = 0
FEATURE [Part::FeaturePython] Structure013  label="PIL 5"  # Arch/BIM 172 (typed FeaturePython)
  CloneOf = -> Structure001
  FaceMaker = 0
  Height = 8000
  HorizontalArea = 196350
  IfcData = attributes={"GlobalId": {"name": "GlobalId", "type": "IfcGloballyUniqueId", "is_enum": false, "enum_values": []}, "Description": {"... (+484 chars omitted),+1 more (map truncated)
  IfcType = 172
  Length = 0
  Material = -> Material
  MoveBase = false
  MoveWithHost = false
  Nodes = (2) [(15210,9900,0),(15210,9900,-8000)]
  NodesOffset = 0
  Normal = (0,0,0)
  PerimeterLength = 1570.8
  Placement = pos=(-9.09e-13,0,-1200) rot=(0,0,1;0rad)
  PredefinedType = 0
  VerticalArea = 1.25664e+07
  Width = 100
FEATURE [Part::FeaturePython] Structure014  label="CAB PIL 7"  # Arch/BIM 172 (typed FeaturePython)
  CloneOf = -> Structure
  FaceMaker = 0
  Height = 700
  HorizontalArea = 490000
  IfcData = attributes={"GlobalId": {"name": "GlobalId", "type": "IfcGloballyUniqueId", "is_enum": false, "enum_values": []}, "Description": {"... (+484 chars omitted),+1 more (map truncated)
  IfcType = 172
  Length = 0
  Material = -> Material
  MoveBase = false
  MoveWithHost = false
  Nodes = (2) [(15210,9900,0),(15210,9900,-700)]
  NodesOffset = 0
  Normal = (0,0,0)
  PerimeterLength = 2800
  Placement = pos=(-9050,-3260,-500) rot=(0,0,1;0rad)
  PredefinedType = 0
  VerticalArea = 1960000
  Width = 0
FEATURE [Part::FeaturePython] Structure015  label="PIL 7"  # Arch/BIM 172 (typed FeaturePython)
  CloneOf = -> Structure001
  FaceMaker = 0
  Height = 8000
  HorizontalArea = 196350
  IfcData = attributes={"GlobalId": {"name": "GlobalId", "type": "IfcGloballyUniqueId", "is_enum": false, "enum_values": []}, "Description": {"... (+484 chars omitted),+1 more (map truncated)
  IfcType = 172
  Length = 0
  Material = -> Material
  MoveBase = false
  MoveWithHost = false
  Nodes = (2) [(15210,9900,0),(15210,9900,-8000)]
  NodesOffset = 0
  Normal = (0,0,0)
  PerimeterLength = 1570.8
  Placement = pos=(-9050,-3260,-1200) rot=(0,0,1;0rad)
  PredefinedType = 0
  VerticalArea = 1.25664e+07
  Width = 100
FEATURE [Part::FeaturePython] Structure016  label="CAB PIL 8"  # Arch/BIM 172 (typed FeaturePython)
  CloneOf = -> Structure
  FaceMaker = 0
  Height = 700
  HorizontalArea = 490000
  IfcData = attributes={"GlobalId": {"name": "GlobalId", "type": "IfcGloballyUniqueId", "is_enum": false, "enum_values": []}, "Description": {"... (+484 chars omitted),+1 more (map truncated)
  IfcType = 172
  Length = 0
  Material = -> Material
  MoveBase = false
  MoveWithHost = false
  Nodes = (2) [(15210,9900,0),(15210,9900,-700)]
  NodesOffset = 0
  Normal = (0,0,0)
  PerimeterLength = 2800
  Placement = pos=(-6200,-3260,-500) rot=(0,0,1;0rad)
  PredefinedType = 0
  VerticalArea = 1960000
  Width = 0
FEATURE [Part::FeaturePython] Structure017  label="PIL 8"  # Arch/BIM 172 (typed FeaturePython)
  CloneOf = -> Structure001
  FaceMaker = 0
  Height = 8000
  HorizontalArea = 196350
  IfcData = attributes={"GlobalId": {"name": "GlobalId", "type": "IfcGloballyUniqueId", "is_enum": false, "enum_values": []}, "Description": {"... (+484 chars omitted),+1 more (map truncated)
  IfcType = 172
  Length = 0
  Material = -> Material
  MoveBase = false
  MoveWithHost = false
  Nodes = (2) [(15210,9900,0),(15210,9900,-8000)]
  NodesOffset = 0
  Normal = (0,0,0)
  PerimeterLength = 1570.8
  Placement = pos=(-6200,-3260,-1200) rot=(0,0,1;0rad)
  PredefinedType = 0
  VerticalArea = 1.25664e+07
  Width = 100
FEATURE [Part::FeaturePython] Structure018  label="CAB PIL 9"  # Arch/BIM 172 (typed FeaturePython)
  CloneOf = -> Structure
  FaceMaker = 0
  Height = 700
  HorizontalArea = 490000
  IfcData = attributes={"GlobalId": {"name": "GlobalId", "type": "IfcGloballyUniqueId", "is_enum": false, "enum_values": []}, "Description": {"... (+484 chars omitted),+1 more (map truncated)
  IfcType = 172
  Length = 0
  Material = -> Material
  MoveBase = false
  MoveWithHost = false
  Nodes = (2) [(15210,9900,0),(15210,9900,-700)]
  NodesOffset = 0
  Normal = (0,0,0)
  PerimeterLength = 2800
  Placement = pos=(-1430,-3930,-500) rot=(0,0,1;0rad)
  PredefinedType = 0
  VerticalArea = 1960000
  Width = 0
FEATURE [Part::FeaturePython] Structure019  label="PIL 9"  # Arch/BIM 172 (typed FeaturePython)
  CloneOf = -> Structure001
  FaceMaker = 0
  Height = 8000
  HorizontalArea = 196350
  IfcData = attributes={"GlobalId": {"name": "GlobalId", "type": "IfcGloballyUniqueId", "is_enum": false, "enum_values": []}, "Description": {"... (+484 chars omitted),+1 more (map truncated)
  IfcType = 172
  Length = 0
  Material = -> Material
  MoveBase = false
  MoveWithHost = false
  Nodes = (2) [(15210,9900,0),(15210,9900,-8000)]
  NodesOffset = 0
  Normal = (0,0,0)
  PerimeterLength = 1570.8
  Placement = pos=(-1430,-3930,-1200) rot=(0,0,1;0rad)
  PredefinedType = 0
  VerticalArea = 1.25664e+07
  Width = 100
FEATURE [Part::FeaturePython] Structure020  label="CAB PIL 10"  # Arch/BIM 172 (typed FeaturePython)
  CloneOf = -> Structure
  FaceMaker = 0
  Height = 700
  HorizontalArea = 490000
  IfcData = attributes={"GlobalId": {"name": "GlobalId", "type": "IfcGloballyUniqueId", "is_enum": false, "enum_values": []}, "Description": {"... (+484 chars omitted),+1 more (map truncated)
  IfcType = 172
  Length = 0
  Material = -> Material
  MoveBase = false
  MoveWithHost = false
  Nodes = (2) [(15210,9900,0),(15210,9900,-700)]
  NodesOffset = 0
  Normal = (0,0,0)
  PerimeterLength = 2800
  Placement = pos=(-9.09e-13,-3930,-500) rot=(0,0,1;0rad)
  PredefinedType = 0
  VerticalArea = 1960000
  Width = 0
FEATURE [Part::FeaturePython] Structure021  label="PIL 10"  # Arch/BIM 172 (typed FeaturePython)
  CloneOf = -> Structure001
  FaceMaker = 0
  Height = 8000
  HorizontalArea = 196350
  IfcData = attributes={"GlobalId": {"name": "GlobalId", "type": "IfcGloballyUniqueId", "is_enum": false, "enum_values": []}, "Description": {"... (+484 chars omitted),+1 more (map truncated)
  IfcType = 172
  Length = 0
  Material = -> Material
  MoveBase = false
  MoveWithHost = false
  Nodes = (2) [(15210,9900,0),(15210,9900,-8000)]
  NodesOffset = 0
  Normal = (0,0,0)
  PerimeterLength = 1570.8
  Placement = pos=(-9.09e-13,-3930,-1200) rot=(0,0,1;0rad)
  PredefinedType = 0
  VerticalArea = 1.25664e+07
  Width = 100
FEATURE [Part::FeaturePython] Structure022  label="CAB PIL 12"  # Arch/BIM 172 (typed FeaturePython)
  CloneOf = -> Structure
  FaceMaker = 0
  Height = 700
  HorizontalArea = 490000
  IfcData = attributes={"GlobalId": {"name": "GlobalId", "type": "IfcGloballyUniqueId", "is_enum": false, "enum_values": []}, "Description": {"... (+484 chars omitted),+1 more (map truncated)
  IfcType = 172
  Length = 0
  Material = -> Material
  MoveBase = false
  MoveWithHost = false
  Nodes = (2) [(15210,9900,0),(15210,9900,-700)]
  NodesOffset = 0
  Normal = (0,0,0)
  PerimeterLength = 2800
  Placement = pos=(-9050,-6550,-500) rot=(0,0,1;0rad)
  PredefinedType = 0
  VerticalArea = 1960000
  Width = 0
FEATURE [Part::FeaturePython] Structure023  label="PIL 12"  # Arch/BIM 172 (typed FeaturePython)
  CloneOf = -> Structure001
  FaceMaker = 0
  Height = 8000
  HorizontalArea = 196350
  IfcData = attributes={"GlobalId": {"name": "GlobalId", "type": "IfcGloballyUniqueId", "is_enum": false, "enum_values": []}, "Description": {"... (+484 chars omitted),+1 more (map truncated)
  IfcType = 172
  Length = 0
  Material = -> Material
  MoveBase = false
  MoveWithHost = false
  Nodes = (2) [(15210,9900,0),(15210,9900,-8000)]
  NodesOffset = 0
  Normal = (0,0,0)
  PerimeterLength = 1570.8
  Placement = pos=(-9050,-6550,-1200) rot=(0,0,1;0rad)
  PredefinedType = 0
  VerticalArea = 1.25664e+07
  Width = 100
FEATURE [Part::FeaturePython] Structure024  label="CAB PIL 13"  # Arch/BIM 172 (typed FeaturePython)
  CloneOf = -> Structure
  FaceMaker = 0
  Height = 700
  HorizontalArea = 490000
  IfcData = attributes={"GlobalId": {"name": "GlobalId", "type": "IfcGloballyUniqueId", "is_enum": false, "enum_values": []}, "Description": {"... (+484 chars omitted),+1 more (map truncated)
  IfcType = 172
  Length = 0
  Material = -> Material
  MoveBase = false
  MoveWithHost = false
  Nodes = (2) [(15210,9900,0),(15210,9900,-700)]
  NodesOffset = 0
  Normal = (0,0,0)
  PerimeterLength = 2800
  Placement = pos=(-6200,-6550,-500) rot=(0,0,1;0rad)
  PredefinedType = 0
  VerticalArea = 1960000
  Width = 0
FEATURE [Part::FeaturePython] Structure025  label="PIL 13"  # Arch/BIM 172 (typed FeaturePython)
  CloneOf = -> Structure001
  FaceMaker = 0
  Height = 8000
  HorizontalArea = 196350
  IfcData = attributes={"GlobalId": {"name": "GlobalId", "type": "IfcGloballyUniqueId", "is_enum": false, "enum_values": []}, "Description": {"... (+484 chars omitted),+1 more (map truncated)
  IfcType = 172
  Length = 0
  Material = -> Material
  MoveBase = false
  MoveWithHost = false
  Nodes = (2) [(15210,9900,0),(15210,9900,-8000)]
  NodesOffset = 0
  Normal = (0,0,0)
  PerimeterLength = 1570.8
  Placement = pos=(-6200,-6550,-1200) rot=(0,0,1;0rad)
  PredefinedType = 0
  VerticalArea = 1.25664e+07
  Width = 100
FEATURE [Part::FeaturePython] Structure026  label="CAB PIL 14"  # Arch/BIM 172 (typed FeaturePython)
  CloneOf = -> Structure
  FaceMaker = 0
  Height = 700
  HorizontalArea = 490000
  IfcData = attributes={"GlobalId": {"name": "GlobalId", "type": "IfcGloballyUniqueId", "is_enum": false, "enum_values": []}, "Description": {"... (+484 chars omitted),+1 more (map truncated)
  IfcType = 172
  Length = 0
  Material = -> Material
  MoveBase = false
  MoveWithHost = false
  Nodes = (2) [(15210,9900,0),(15210,9900,-700)]
  NodesOffset = 0
  Normal = (0,0,0)
  PerimeterLength = 2800
  Placement = pos=(-4650,-6550,-500) rot=(0,0,1;0rad)
  PredefinedType = 0
  VerticalArea = 1960000
  Width = 0
FEATURE [Part::FeaturePython] Structure027  label="PIL 14"  # Arch/BIM 172 (typed FeaturePython)
  CloneOf = -> Structure001
  FaceMaker = 0
  Height = 8000
  HorizontalArea = 196350
  IfcData = attributes={"GlobalId": {"name": "GlobalId", "type": "IfcGloballyUniqueId", "is_enum": false, "enum_values": []}, "Description": {"... (+484 chars omitted),+1 more (map truncated)
  IfcType = 172
  Length = 0
  Material = -> Material
  MoveBase = false
  MoveWithHost = false
  Nodes = (2) [(15210,9900,0),(15210,9900,-8000)]
  NodesOffset = 0
  Normal = (0,0,0)
  PerimeterLength = 1570.8
  Placement = pos=(-4650,-6550,-1200) rot=(0,0,1;0rad)
  PredefinedType = 0
  VerticalArea = 1.25664e+07
  Width = 100
FEATURE [Part::FeaturePython] Structure028  label="PIL 15"  # Arch/BIM 172 (typed FeaturePython)
  CloneOf = -> Structure001
  FaceMaker = 0
  Height = 8000
  HorizontalArea = 196350
  IfcData = attributes={"GlobalId": {"name": "GlobalId", "type": "IfcGloballyUniqueId", "is_enum": false, "enum_values": []}, "Description": {"... (+484 chars omitted),+1 more (map truncated)
  IfcType = 172
  Length = 0
  Material = -> Material
  MoveBase = false
  MoveWithHost = false
  Nodes = (2) [(15210,9900,0),(15210,9900,-8000)]
  NodesOffset = 0
  Normal = (0,0,0)
  PerimeterLength = 1570.8
  Placement = pos=(-1430,-6550,-1200) rot=(0,0,1;0rad)
  PredefinedType = 0
  VerticalArea = 1.25664e+07
  Width = 100
FEATURE [Part::FeaturePython] Structure029  label="CAB PIL 15"  # Arch/BIM 172 (typed FeaturePython)
  CloneOf = -> Structure
  FaceMaker = 0
  Height = 700
  HorizontalArea = 490000
  IfcData = attributes={"GlobalId": {"name": "GlobalId", "type": "IfcGloballyUniqueId", "is_enum": false, "enum_values": []}, "Description": {"... (+484 chars omitted),+1 more (map truncated)
  IfcType = 172
  Length = 0
  Material = -> Material
  MoveBase = false
  MoveWithHost = false
  Nodes = (2) [(15210,9900,0),(15210,9900,-700)]
  NodesOffset = 0
  Normal = (0,0,0)
  PerimeterLength = 2800
  Placement = pos=(-1430,-6550,-500) rot=(0,0,1;0rad)
  PredefinedType = 0
  VerticalArea = 1960000
  Width = 0
FEATURE [Part::FeaturePython] Structure030  label="CAB PIL 16"  # Arch/BIM 172 (typed FeaturePython)
  CloneOf = -> Structure
  FaceMaker = 0
  Height = 700
  HorizontalArea = 490000
  IfcData = attributes={"GlobalId": {"name": "GlobalId", "type": "IfcGloballyUniqueId", "is_enum": false, "enum_values": []}, "Description": {"... (+484 chars omitted),+1 more (map truncated)
  IfcType = 172
  Length = 0
  Material = -> Material
  MoveBase = false
  MoveWithHost = false
  Nodes = (2) [(15210,9900,0),(15210,9900,-700)]
  NodesOffset = 0
  Normal = (0,0,0)
  PerimeterLength = 2800
  Placement = pos=(-13280,-9800,-500) rot=(0,0,1;0rad)
  PredefinedType = 0
  VerticalArea = 1960000
  Width = 0
FEATURE [Part::FeaturePython] Structure031  label="PIL 16"  # Arch/BIM 172 (typed FeaturePython)
  CloneOf = -> Structure001
  FaceMaker = 0
  Height = 8000
  HorizontalArea = 196350
  IfcData = attributes={"GlobalId": {"name": "GlobalId", "type": "IfcGloballyUniqueId", "is_enum": false, "enum_values": []}, "Description": {"... (+484 chars omitted),+1 more (map truncated)
  IfcType = 172
  Length = 0
  Material = -> Material
  MoveBase = false
  MoveWithHost = false
  Nodes = (2) [(15210,9900,0),(15210,9900,-8000)]
  NodesOffset = 0
  Normal = (0,0,0)
  PerimeterLength = 1570.8
  Placement = pos=(-13280,-9800,-1200) rot=(0,0,1;0rad)
  PredefinedType = 0
  VerticalArea = 1.25664e+07
  Width = 100
FEATURE [Part::FeaturePython] Structure032  label="CAB PIL 17"  # Arch/BIM 172 (typed FeaturePython)
  CloneOf = -> Structure
  FaceMaker = 0
  Height = 700
  HorizontalArea = 490000
  IfcData = attributes={"GlobalId": {"name": "GlobalId", "type": "IfcGloballyUniqueId", "is_enum": false, "enum_values": []}, "Description": {"... (+484 chars omitted),+1 more (map truncated)
  IfcType = 172
  Length = 0
  Material = -> Material
  MoveBase = false
  MoveWithHost = false
  Nodes = (2) [(15210,9900,0),(15210,9900,-700)]
  NodesOffset = 0
  Normal = (0,0,0)
  PerimeterLength = 2800
  Placement = pos=(-9050,-9800,-500) rot=(0,0,1;0rad)
  PredefinedType = 0
  VerticalArea = 1960000
  Width = 0
FEATURE [Part::FeaturePython] Structure033  label="PIL 17"  # Arch/BIM 172 (typed FeaturePython)
  CloneOf = -> Structure001
  FaceMaker = 0
  Height = 8000
  HorizontalArea = 196350
  IfcData = attributes={"GlobalId": {"name": "GlobalId", "type": "IfcGloballyUniqueId", "is_enum": false, "enum_values": []}, "Description": {"... (+484 chars omitted),+1 more (map truncated)
  IfcType = 172
  Length = 0
  Material = -> Material
  MoveBase = false
  MoveWithHost = false
  Nodes = (2) [(15210,9900,0),(15210,9900,-8000)]
  NodesOffset = 0
  Normal = (0,0,0)
  PerimeterLength = 1570.8
  Placement = pos=(-9050,-9800,-1200) rot=(0,0,1;0rad)
  PredefinedType = 0
  VerticalArea = 1.25664e+07
  Width = 100
FEATURE [Part::FeaturePython] Structure034  label="CAB PIL 18"  # Arch/BIM 172 (typed FeaturePython)
  CloneOf = -> Structure
  FaceMaker = 0
  Height = 700
  HorizontalArea = 490000
  IfcData = attributes={"GlobalId": {"name": "GlobalId", "type": "IfcGloballyUniqueId", "is_enum": false, "enum_values": []}, "Description": {"... (+484 chars omitted),+1 more (map truncated)
  IfcType = 172
  Length = 0
  Material = -> Material
  MoveBase = false
  MoveWithHost = false
  Nodes = (2) [(15210,9900,0),(15210,9900,-700)]
  NodesOffset = 0
  Normal = (0,0,0)
  PerimeterLength = 2800
  Placement = pos=(-6200,-9800,-500) rot=(0,0,1;0rad)
  PredefinedType = 0
  VerticalArea = 1960000
  Width = 0
FEATURE [Part::FeaturePython] Structure035  label="PIL 18"  # Arch/BIM 172 (typed FeaturePython)
  CloneOf = -> Structure001
  FaceMaker = 0
  Height = 8000
  HorizontalArea = 196350
  IfcData = attributes={"GlobalId": {"name": "GlobalId", "type": "IfcGloballyUniqueId", "is_enum": false, "enum_values": []}, "Description": {"... (+484 chars omitted),+1 more (map truncated)
  IfcType = 172
  Length = 0
  Material = -> Material
  MoveBase = false
  MoveWithHost = false
  Nodes = (2) [(15210,9900,0),(15210,9900,-8000)]
  NodesOffset = 0
  Normal = (0,0,0)
  PerimeterLength = 1570.8
  Placement = pos=(-6200,-9800,-1200) rot=(0,0,1;0rad)
  PredefinedType = 0
  VerticalArea = 1.25664e+07
  Width = 100
FEATURE [Part::FeaturePython] Structure036  label="CAB PIL 19"  # Arch/BIM 172 (typed FeaturePython)
  CloneOf = -> Structure
  FaceMaker = 0
  Height = 700
  HorizontalArea = 490000
  IfcData = attributes={"GlobalId": {"name": "GlobalId", "type": "IfcGloballyUniqueId", "is_enum": false, "enum_values": []}, "Description": {"... (+484 chars omitted),+1 more (map truncated)
  IfcType = 172
  Length = 0
  Material = -> Material
  MoveBase = false
  MoveWithHost = false
  Nodes = (2) [(15210,9900,0),(15210,9900,-700)]
  NodesOffset = 0
  Normal = (0,0,0)
  PerimeterLength = 2800
  Placement = pos=(-4650,-9800,-500) rot=(0,0,1;0rad)
  PredefinedType = 0
  VerticalArea = 1960000
  Width = 0
FEATURE [Part::FeaturePython] Structure037  label="PIL 19"  # Arch/BIM 172 (typed FeaturePython)
  CloneOf = -> Structure001
  FaceMaker = 0
  Height = 8000
  HorizontalArea = 196350
  IfcData = attributes={"GlobalId": {"name": "GlobalId", "type": "IfcGloballyUniqueId", "is_enum": false, "enum_values": []}, "Description": {"... (+484 chars omitted),+1 more (map truncated)
  IfcType = 172
  Length = 0
  Material = -> Material
  MoveBase = false
  MoveWithHost = false
  Nodes = (2) [(15210,9900,0),(15210,9900,-8000)]
  NodesOffset = 0
  Normal = (0,0,0)
  PerimeterLength = 1570.8
  Placement = pos=(-4650,-9800,-1200) rot=(0,0,1;0rad)
  PredefinedType = 0
  VerticalArea = 1.25664e+07
  Width = 100
FEATURE [Part::FeaturePython] Structure038  label="CAB PIL 20"  # Arch/BIM 172 (typed FeaturePython)
  CloneOf = -> Structure
  FaceMaker = 0
  Height = 700
  HorizontalArea = 490000
  IfcData = attributes={"GlobalId": {"name": "GlobalId", "type": "IfcGloballyUniqueId", "is_enum": false, "enum_values": []}, "Description": {"... (+484 chars omitted),+1 more (map truncated)
  IfcType = 172
  Length = 0
  Material = -> Material
  MoveBase = false
  MoveWithHost = false
  Nodes = (2) [(15210,9900,0),(15210,9900,-700)]
  NodesOffset = 0
  Normal = (0,0,0)
  PerimeterLength = 2800
  Placement = pos=(-1430,-9800,-500) rot=(0,0,1;0rad)
  PredefinedType = 0
  VerticalArea = 1960000
  Width = 0
FEATURE [Part::FeaturePython] Structure039  label="PIL 20"  # Arch/BIM 172 (typed FeaturePython)
  CloneOf = -> Structure001
  FaceMaker = 0
  Height = 8000
  HorizontalArea = 196350
  IfcData = attributes={"GlobalId": {"name": "GlobalId", "type": "IfcGloballyUniqueId", "is_enum": false, "enum_values": []}, "Description": {"... (+484 chars omitted),+1 more (map truncated)
  IfcType = 172
  Length = 0
  Material = -> Material
  MoveBase = false
  MoveWithHost = false
  Nodes = (2) [(15210,9900,0),(15210,9900,-8000)]
  NodesOffset = 0
  Normal = (0,0,0)
  PerimeterLength = 1570.8
  Placement = pos=(-1430,-9800,-1200) rot=(0,0,1;0rad)
  PredefinedType = 0
  VerticalArea = 1.25664e+07
  Width = 100
FEATURE [Part::FeaturePython] Structure040  label="L01"  # Arch/BIM 172 (typed FeaturePython)
  FaceMaker = 0
  Height = 250
  HorizontalArea = 9230000
  IfcData = attributes={"GlobalId": {"name": "GlobalId", "type": "IfcGloballyUniqueId", "is_enum": false, "enum_values": []}, "Description": {"... (+484 chars omitted),+1 more (map truncated)
  IfcType = 172
  Length = 0
  Material = -> Material
  MoveBase = false
  MoveWithHost = false
  Nodes = (2) [(18300,6875,0),(18300,6875,-250)]
  NodesOffset = 0
  Normal = (0,0,-1)
  PerimeterLength = 12300
  Placement = pos=(-7015,295,-1000) rot=(0,0,1;0rad)
  PredefinedType = 0
  VerticalArea = 3075000
  Width = 100
FEATURE [Part::FeaturePython] Structure081  label="25x15 C1"  # Arch/BIM 24 (typed FeaturePython)
  FaceMaker = 0
  Height = 3500
  HorizontalArea = 37500
  IfcData = attributes={"GlobalId": {"name": "GlobalId", "type": "IfcGloballyUniqueId", "is_enum": false, "enum_values": []}, "Description": {"... (+438 chars omitted),+1 more (map truncated)
  IfcType = 24
  Length = 250
  Material = -> Material
  MoveBase = false
  MoveWithHost = false
  Nodes = (2) [(-1.05471e-15,1.36424e-15,0),(-1.05471e-15,1.36424e-15,3500)]
  NodesOffset = 0
  Normal = (0,0,0)
  PerimeterLength = 800
  Placement = pos=(1930,9900,-500) rot=(0,0,1;0rad)
  PredefinedType = 0
  VerticalArea = 2.8e+06
  Width = 150
FEATURE [Part::FeaturePython] Structure084  label="25x15 C004"  # Arch/BIM 172 (typed FeaturePython)
  CloneOf = -> Structure081
  FaceMaker = 0
  Height = 3500
  HorizontalArea = 37500
  IfcData = attributes={"GlobalId": {"name": "GlobalId", "type": "IfcGloballyUniqueId", "is_enum": false, "enum_values": []}, "Description": {"... (+484 chars omitted),+1 more (map truncated)
  IfcType = 172
  Length = 250
  Material = -> Material
  MoveBase = false
  MoveWithHost = false
  Nodes = (2) [(-1.05471e-15,1.36424e-15,0),(-1.05471e-15,1.36424e-15,3500)]
  NodesOffset = 0
  Normal = (0,0,0)
  PerimeterLength = 800
  Placement = pos=(1930,100,-500) rot=(0,0,1;0rad)
  PredefinedType = 0
  VerticalArea = 2.8e+06
  Width = 150
FEATURE [Part::FeaturePython] Structure085  label="25x20 C6"  # Arch/BIM 24 (typed FeaturePython)
  FaceMaker = 0
  Height = 3500
  HorizontalArea = 50000
  IfcData = attributes={"GlobalId": {"name": "GlobalId", "type": "IfcGloballyUniqueId", "is_enum": false, "enum_values": []}, "Description": {"... (+438 chars omitted),+1 more (map truncated)
  IfcType = 24
  Length = 250
  Material = -> Material
  MoveBase = false
  MoveWithHost = false
  Nodes = (2) [(-1.05471e-15,-1.81899e-15,0),(-1.05471e-15,-1.81899e-15,3500)]
  NodesOffset = 0
  Normal = (0,0,0)
  PerimeterLength = 900
  Placement = pos=(1930,6640,-500) rot=(0,0,1;0rad)
  PredefinedType = 0
  VerticalArea = 3.15e+06
  Width = 200
FEATURE [Part::FeaturePython] Structure086  label="25x20 C007"  # Arch/BIM 172 (typed FeaturePython)
  CloneOf = -> Structure085
  FaceMaker = 0
  Height = 3500
  HorizontalArea = 50000
  IfcData = attributes={"GlobalId": {"name": "GlobalId", "type": "IfcGloballyUniqueId", "is_enum": false, "enum_values": []}, "Description": {"... (+484 chars omitted),+1 more (map truncated)
  IfcType = 172
  Length = 250
  Material = -> Material
  MoveBase = false
  MoveWithHost = false
  Nodes = (2) [(-1.05471e-15,-1.81899e-15,0),(-1.05471e-15,-1.81899e-15,3500)]
  NodesOffset = 0
  Normal = (0,0,0)
  PerimeterLength = 900
  Placement = pos=(1930,3350,-500) rot=(0,0,1;0rad)
  PredefinedType = 0
  VerticalArea = 3.15e+06
  Width = 200
FEATURE [Part::FeaturePython] Structure088  label="25x15 C005"  # Arch/BIM 24 (typed FeaturePython)
  FaceMaker = 0
  Height = 3500
  HorizontalArea = 37500
  IfcData = attributes={"GlobalId": {"name": "GlobalId", "type": "IfcGloballyUniqueId", "is_enum": false, "enum_values": []}, "Description": {"... (+438 chars omitted),+1 more (map truncated)
  IfcType = 24
  Length = 250
  Material = -> Material
  MoveBase = false
  MoveWithHost = false
  Nodes = (2) [(-1.05471e-15,1.36424e-15,0),(-1.05471e-15,1.36424e-15,3500)]
  NodesOffset = 0
  Normal = (0,0,0)
  PerimeterLength = 800
  Placement = pos=(6160,6640,-500) rot=(0,0,1;0rad)
  PredefinedType = 0
  VerticalArea = 2.8e+06
  Width = 150
FEATURE [Part::FeaturePython] Structure089  label="25x15 C006"  # Arch/BIM 24 (typed FeaturePython)
  FaceMaker = 0
  Height = 3500
  HorizontalArea = 37500
  IfcData = attributes={"GlobalId": {"name": "GlobalId", "type": "IfcGloballyUniqueId", "is_enum": false, "enum_values": []}, "Description": {"... (+438 chars omitted),+1 more (map truncated)
  IfcType = 24
  Length = 250
  Material = -> Material
  MoveBase = false
  MoveWithHost = false
  Nodes = (2) [(-1.05471e-15,1.36424e-15,0),(-1.05471e-15,1.36424e-15,3500)]
  NodesOffset = 0
  Normal = (0,0,0)
  PerimeterLength = 800
  Placement = pos=(6160,3350,-500) rot=(0,0,1;0rad)
  PredefinedType = 0
  VerticalArea = 2.8e+06
  Width = 150
FEATURE [Part::FeaturePython] Structure090  label="25x15 C007"  # Arch/BIM 24 (typed FeaturePython)
  FaceMaker = 0
  Height = 3500
  HorizontalArea = 37500
  IfcData = attributes={"GlobalId": {"name": "GlobalId", "type": "IfcGloballyUniqueId", "is_enum": false, "enum_values": []}, "Description": {"... (+438 chars omitted),+1 more (map truncated)
  IfcType = 24
  Length = 250
  Material = -> Material
  MoveBase = false
  MoveWithHost = false
  Nodes = (2) [(-1.05471e-15,1.36424e-15,0),(-1.05471e-15,1.36424e-15,3500)]
  NodesOffset = 0
  Normal = (0,0,0)
  PerimeterLength = 800
  Placement = pos=(6160,100,-500) rot=(0,0,1;0rad)
  PredefinedType = 0
  VerticalArea = 2.8e+06
  Width = 150
FEATURE [Part::FeaturePython] Structure091  label="25x15 C008"  # Arch/BIM 24 (typed FeaturePython)
  FaceMaker = 0
  Height = 3500
  HorizontalArea = 37500
  IfcData = attributes={"GlobalId": {"name": "GlobalId", "type": "IfcGloballyUniqueId", "is_enum": false, "enum_values": []}, "Description": {"... (+438 chars omitted),+1 more (map truncated)
  IfcType = 24
  Length = 250
  Material = -> Material
  MoveBase = false
  MoveWithHost = false
  Nodes = (2) [(-1.05471e-15,1.36424e-15,0),(-1.05471e-15,1.36424e-15,3500)]
  NodesOffset = 0
  Normal = (0,0,0)
  PerimeterLength = 800
  Placement = pos=(9010,100,-500) rot=(0,0,1;0rad)
  PredefinedType = 0
  VerticalArea = 2.8e+06
  Width = 150
FEATURE [Part::FeaturePython] Structure092  label="25x15 C009"  # Arch/BIM 24 (typed FeaturePython)
  FaceMaker = 0
  Height = 3500
  HorizontalArea = 37500
  IfcData = attributes={"GlobalId": {"name": "GlobalId", "type": "IfcGloballyUniqueId", "is_enum": false, "enum_values": []}, "Description": {"... (+438 chars omitted),+1 more (map truncated)
  IfcType = 24
  Length = 250
  Material = -> Material
  MoveBase = false
  MoveWithHost = false
  Nodes = (2) [(-1.05471e-15,1.36424e-15,0),(-1.05471e-15,1.36424e-15,3500)]
  NodesOffset = 0
  Normal = (0,0,0)
  PerimeterLength = 800
  Placement = pos=(10560,100,-500) rot=(0,0,1;0rad)
  PredefinedType = 0
  VerticalArea = 2.8e+06
  Width = 150
FEATURE [Part::FeaturePython] Structure093  label="25x15 C010"  # Arch/BIM 24 (typed FeaturePython)
  FaceMaker = 0
  Height = 3500
  HorizontalArea = 37500
  IfcData = attributes={"GlobalId": {"name": "GlobalId", "type": "IfcGloballyUniqueId", "is_enum": false, "enum_values": []}, "Description": {"... (+438 chars omitted),+1 more (map truncated)
  IfcType = 24
  Length = 250
  Material = -> Material
  MoveBase = false
  MoveWithHost = false
  Nodes = (2) [(-1.05471e-15,1.36424e-15,0),(-1.05471e-15,1.36424e-15,3500)]
  NodesOffset = 0
  Normal = (0,0,0)
  PerimeterLength = 800
  Placement = pos=(13780,100,-500) rot=(0,0,1;0rad)
  PredefinedType = 0
  VerticalArea = 2.8e+06
  Width = 150
FEATURE [Part::FeaturePython] Structure097  label="25x15 C014"  # Arch/BIM 24 (typed FeaturePython)
  FaceMaker = 0
  Height = 3500
  HorizontalArea = 37500
  IfcData = attributes={"GlobalId": {"name": "GlobalId", "type": "IfcGloballyUniqueId", "is_enum": false, "enum_values": []}, "Description": {"... (+438 chars omitted),+1 more (map truncated)
  IfcType = 24
  Length = 250
  Material = -> Material
  MoveBase = false
  MoveWithHost = false
  Nodes = (2) [(-1.05471e-15,1.36424e-15,0),(-1.05471e-15,1.36424e-15,3500)]
  NodesOffset = 0
  Normal = (0,0,0)
  PerimeterLength = 800
  Placement = pos=(15210,5970,-500) rot=(0,0,1;0rad)
  PredefinedType = 0
  VerticalArea = 2.8e+06
  Width = 150
FEATURE [Part::FeaturePython] Structure098  label="25x15 C015"  # Arch/BIM 24 (typed FeaturePython)
  FaceMaker = 0
  Height = 3500
  HorizontalArea = 37500
  IfcData = attributes={"GlobalId": {"name": "GlobalId", "type": "IfcGloballyUniqueId", "is_enum": false, "enum_values": []}, "Description": {"... (+438 chars omitted),+1 more (map truncated)
  IfcType = 24
  Length = 250
  Material = -> Material
  MoveBase = false
  MoveWithHost = false
  Nodes = (2) [(-1.05471e-15,1.36424e-15,0),(-1.05471e-15,1.36424e-15,3500)]
  NodesOffset = 0
  Normal = (0,0,0)
  PerimeterLength = 800
  Placement = pos=(13780,5970,-500) rot=(0,0,1;0rad)
  PredefinedType = 0
  VerticalArea = 2.8e+06
  Width = 150
FEATURE [Part::FeaturePython] Wall  label="Tabique Ascensor"  # Arch/BIM 166 (typed FeaturePython)
  Align = 1
  Area = 8300000
  Base = -> Rectangle
  BlockHeight = 0
  BlockLength = 0
  CountBroken = 0
  CountEntire = 0
  Face = 0
  Height = 1000
  HorizontalArea = 1155000
  IfcData = attributes={"GlobalId": {"name": "GlobalId", "type": "IfcGloballyUniqueId", "is_enum": false, "enum_values": []}, "Description": {"... (+533 chars omitted),+1 more (map truncated)
  IfcType = 166
  Joint = 0
  Length = 8300
  MakeBlocks = false
  Material = -> Material
  MoveBase = false
  MoveWithHost = false
  Normal = (0,0,0)
  OffsetFirst = 0
  OffsetSecond = 0
  PerimeterLength = 8300
  Placement = pos=(0,0,-1000) rot=(0,0,1;0rad)
  PredefinedType = 0
  VerticalArea = 15400000
  Width = 150
FEATURE [App::GeometryPython] BuildingPart006  label="Pilotes"  # Arch/BIM 172 (typed FeaturePython)
  Area = 0
  Group = -> [Structure001,Structure021,Structure005,Structure023,Structure025,Structure027,Structure028,Structure031,Structure033,Structure035,Structure037,Structure007,Structure039,Structure009,Structure011,Structure013,Structure003,Structure015,Structure017,Structure019]
  Height = 0
  HeightPropagate = true
  IfcData = attributes={"GlobalId": {"name": "GlobalId", "type": "IfcGloballyUniqueId", "is_enum": false, "enum_values": []}, "Description": {"... (+484 chars omitted),+1 more (map truncated)
  IfcType = 172
  LevelOffset = 0
  Placement = pos=(0,0,500) rot=(0,0,1;0rad)
  PredefinedType = 0
FEATURE [App::GeometryPython] BuildingPart007  label="Cabezales Pilotes"  # Arch/BIM 172 (typed FeaturePython)
  Area = 0
  Group = -> [Structure,Structure020,Structure004,Structure022,Structure024,Structure026,Structure029,Structure030,Structure032,Structure034,Structure036,Structure006,Structure038,Structure008,Structure010,Structure012,Structure002,Structure014,Structure016,Structure018]
  Height = 0
  HeightPropagate = true
  IfcData = attributes={"GlobalId": {"name": "GlobalId", "type": "IfcGloballyUniqueId", "is_enum": false, "enum_values": []}, "Description": {"... (+484 chars omitted),+1 more (map truncated)
  IfcType = 172
  LevelOffset = 0
  Placement = pos=(0,0,500) rot=(0,0,1;0rad)
  PredefinedType = 0
FEATURE [App::GeometryPython] BuildingPart008  label="Losa fundacion"  # Arch/BIM 172 (typed FeaturePython)
  Area = 0
  Group = -> [Structure040]
  Height = 0
  HeightPropagate = true
  IfcData = attributes={"GlobalId": {"name": "GlobalId", "type": "IfcGloballyUniqueId", "is_enum": false, "enum_values": []}, "Description": {"... (+484 chars omitted),+1 more (map truncated)
  IfcType = 172
  LevelOffset = 0
  Placement = pos=(0,0,500) rot=(0,0,1;0rad)
  PredefinedType = 0
FEATURE [Part::FeaturePython] Structure099  label="25x15 C016"  # Arch/BIM 172 (typed FeaturePython)
  CloneOf = -> Structure081
  FaceMaker = 0
  Height = 3500
  HorizontalArea = 37500
  IfcData = attributes={"GlobalId": {"name": "GlobalId", "type": "IfcGloballyUniqueId", "is_enum": false, "enum_values": []}, "Description": {"... (+484 chars omitted),+1 more (map truncated)
  IfcType = 172
  Length = 250
  Material = -> Material
  MoveBase = false
  MoveWithHost = false
  Nodes = (2) [(-1.05471e-15,1.36424e-15,0),(-1.05471e-15,1.36424e-15,3500)]
  NodesOffset = 0
  Normal = (0,0,0)
  PerimeterLength = 800
  Placement = pos=(1930,9900,-500) rot=(0,0,1;0rad)
  PredefinedType = 0
  VerticalArea = 2.8e+06
  Width = 150
FEATURE [Part::FeaturePython] Structure100  label="25x15 C017"  # Arch/BIM 172 (typed FeaturePython)
  CloneOf = -> Structure081
  FaceMaker = 0
  Height = 3500
  HorizontalArea = 37500
  IfcData = attributes={"GlobalId": {"name": "GlobalId", "type": "IfcGloballyUniqueId", "is_enum": false, "enum_values": []}, "Description": {"... (+484 chars omitted),+1 more (map truncated)
  IfcType = 172
  Length = 250
  Material = -> Material
  MoveBase = false
  MoveWithHost = false
  Nodes = (2) [(-1.05471e-15,1.36424e-15,0),(-1.05471e-15,1.36424e-15,3500)]
  NodesOffset = 0
  Normal = (0,0,0)
  PerimeterLength = 800
  Placement = pos=(9010,6640,-500) rot=(0,0,1;1.5708rad)
  PredefinedType = 0
  VerticalArea = 2.8e+06
  Width = 150
FEATURE [Part::FeaturePython] Structure101  label="25x15 C018"  # Arch/BIM 172 (typed FeaturePython)
  CloneOf = -> Structure081
  FaceMaker = 0
  Height = 3500
  HorizontalArea = 37500
  IfcData = attributes={"GlobalId": {"name": "GlobalId", "type": "IfcGloballyUniqueId", "is_enum": false, "enum_values": []}, "Description": {"... (+484 chars omitted),+1 more (map truncated)
  IfcType = 172
  Length = 250
  Material = -> Material
  MoveBase = false
  MoveWithHost = false
  Nodes = (2) [(-1.05471e-15,1.36424e-15,0),(-1.05471e-15,1.36424e-15,3500)]
  NodesOffset = 0
  Normal = (0,0,0)
  PerimeterLength = 800
  Placement = pos=(9010,3350,-500) rot=(0,0,1;1.5708rad)
  PredefinedType = 0
  VerticalArea = 2.8e+06
  Width = 150
FEATURE [Part::FeaturePython] Structure102  label="25x15 C019"  # Arch/BIM 172 (typed FeaturePython)
  CloneOf = -> Structure081
  FaceMaker = 0
  Height = 3500
  HorizontalArea = 37500
  IfcData = attributes={"GlobalId": {"name": "GlobalId", "type": "IfcGloballyUniqueId", "is_enum": false, "enum_values": []}, "Description": {"... (+484 chars omitted),+1 more (map truncated)
  IfcType = 172
  Length = 250
  Material = -> Material
  MoveBase = false
  MoveWithHost = false
  Nodes = (2) [(-1.05471e-15,1.36424e-15,0),(-1.05471e-15,1.36424e-15,3500)]
  NodesOffset = 0
  Normal = (0,0,0)
  PerimeterLength = 800
  Placement = pos=(10560,3350,-500) rot=(0,0,1;1.5708rad)
  PredefinedType = 0
  VerticalArea = 2.8e+06
  Width = 150
FEATURE [Part::FeaturePython] Structure103  label="25x15 C020"  # Arch/BIM 172 (typed FeaturePython)
  CloneOf = -> Structure081
  FaceMaker = 0
  Height = 3500
  HorizontalArea = 37500
  IfcData = attributes={"GlobalId": {"name": "GlobalId", "type": "IfcGloballyUniqueId", "is_enum": false, "enum_values": []}, "Description": {"... (+484 chars omitted),+1 more (map truncated)
  IfcType = 172
  Length = 250
  Material = -> Material
  MoveBase = false
  MoveWithHost = false
  Nodes = (2) [(-1.05471e-15,1.36424e-15,0),(-1.05471e-15,1.36424e-15,3500)]
  NodesOffset = 0
  Normal = (0,0,0)
  PerimeterLength = 800
  Placement = pos=(13780,3350,-500) rot=(0,0,1;1.5708rad)
  PredefinedType = 0
  VerticalArea = 2.8e+06
  Width = 150
FEATURE [Part::FeaturePython] Structure104  label="25x15 C003"  # Arch/BIM 172 (typed FeaturePython)
  CloneOf = -> Structure081
  FaceMaker = 0
  Height = 3500
  HorizontalArea = 37500
  IfcData = attributes={"GlobalId": {"name": "GlobalId", "type": "IfcGloballyUniqueId", "is_enum": false, "enum_values": []}, "Description": {"... (+484 chars omitted),+1 more (map truncated)
  IfcType = 172
  Length = 250
  Material = -> Material
  MoveBase = false
  MoveWithHost = false
  Nodes = (2) [(-1.05471e-15,1.36424e-15,0),(-1.05471e-15,1.36424e-15,3500)]
  NodesOffset = 0
  Normal = (0,0,0)
  PerimeterLength = 800
  Placement = pos=(9010,9900,-500) rot=(0,0,1;0rad)
  PredefinedType = 0
  VerticalArea = 2.8e+06
  Width = 150
FEATURE [Part::FeaturePython] Structure105  label="25x15 C002"  # Arch/BIM 172 (typed FeaturePython)
  CloneOf = -> Structure081
  FaceMaker = 0
  Height = 3500
  HorizontalArea = 37500
  IfcData = attributes={"GlobalId": {"name": "GlobalId", "type": "IfcGloballyUniqueId", "is_enum": false, "enum_values": []}, "Description": {"... (+484 chars omitted),+1 more (map truncated)
  IfcType = 172
  Length = 250
  Material = -> Material
  MoveBase = false
  MoveWithHost = false
  Nodes = (2) [(-1.05471e-15,1.36424e-15,0),(-1.05471e-15,1.36424e-15,3500)]
  NodesOffset = 0
  Normal = (0,0,0)
  PerimeterLength = 800
  Placement = pos=(6160,9900,-500) rot=(0,0,1;0rad)
  PredefinedType = 0
  VerticalArea = 2.8e+06
  Width = 150
FEATURE [Part::FeaturePython] Structure106  label="25x15 C025"  # Arch/BIM 172 (typed FeaturePython)
  CloneOf = -> Structure081
  FaceMaker = 0
  Height = 3500
  HorizontalArea = 37500
  IfcData = attributes={"GlobalId": {"name": "GlobalId", "type": "IfcGloballyUniqueId", "is_enum": false, "enum_values": []}, "Description": {"... (+484 chars omitted),+1 more (map truncated)
  IfcType = 172
  Length = 250
  Material = -> Material
  MoveBase = false
  MoveWithHost = false
  Nodes = (2) [(-1.05471e-15,1.36424e-15,0),(-1.05471e-15,1.36424e-15,3500)]
  NodesOffset = 0
  Normal = (0,0,0)
  PerimeterLength = 800
  Placement = pos=(12010,9900,-500) rot=(0,0,1;0rad)
  PredefinedType = 0
  VerticalArea = 2.8e+06
  Width = 150
FEATURE [Part::FeaturePython] Structure107  label="25x15 C024"  # Arch/BIM 172 (typed FeaturePython)
  CloneOf = -> Structure081
  FaceMaker = 0
  Height = 3500
  HorizontalArea = 37500
  IfcData = attributes={"GlobalId": {"name": "GlobalId", "type": "IfcGloballyUniqueId", "is_enum": false, "enum_values": []}, "Description": {"... (+484 chars omitted),+1 more (map truncated)
  IfcType = 172
  Length = 250
  Material = -> Material
  MoveBase = false
  MoveWithHost = false
  Nodes = (2) [(-1.05471e-15,1.36424e-15,0),(-1.05471e-15,1.36424e-15,3500)]
  NodesOffset = 0
  Normal = (0,0,0)
  PerimeterLength = 800
  Placement = pos=(15210,9900,-500) rot=(0,0,1;0rad)
  PredefinedType = 0
  VerticalArea = 2.8e+06
  Width = 150
FEATURE [App::GeometryPython] BuildingPart004  label="Columnas"  # Arch/BIM 172 (typed FeaturePython)
  Area = 0
  Group = -> [Structure105,Structure104,Structure084,Structure088,Structure089,Structure090,Structure091,Structure092,Structure093,Structure097,Structure098,Structure099,Structure100,Structure101,Structure102,Structure103,Structure107,Structure106,Structure081,Structure086,Structure085]
  Height = 0
  HeightPropagate = true
  IfcData = attributes={"GlobalId": {"name": "GlobalId", "type": "IfcGloballyUniqueId", "is_enum": false, "enum_values": []}, "Description": {"... (+484 chars omitted),+1 more (map truncated)
  IfcType = 172
  LevelOffset = 0
  PredefinedType = 0
FEATURE [Part::FeaturePython] Wall001  label="Tabique Ascensor PB"  # Arch/BIM 166 (typed FeaturePython)
  Align = 1
  Area = 24900000
  Base = -> Rectangle003
  BlockHeight = 0
  BlockLength = 0
  CountBroken = 0
  CountEntire = 0
  Face = 0
  Height = 3000
  HorizontalArea = 1155000
  IfcData = attributes={"GlobalId": {"name": "GlobalId", "type": "IfcGloballyUniqueId", "is_enum": false, "enum_values": []}, "Description": {"... (+533 chars omitted),+1 more (map truncated)
  IfcType = 166
  Joint = 0
  Length = 8300
  MakeBlocks = false
  Material = -> Material
  MoveBase = false
  MoveWithHost = false
  Normal = (0,0,0)
  OffsetFirst = 0
  OffsetSecond = 0
  PerimeterLength = 8300
  PredefinedType = 0
  VerticalArea = 46200000
  Width = 150
FEATURE [Part::FeaturePython] Structure108  label="V20x40 V122"  # Arch/BIM 7 (typed FeaturePython)
  FaceMaker = 0
  Height = 400
  HorizontalArea = 617000
  IfcData = attributes={"GlobalId": {"name": "GlobalId", "type": "IfcGloballyUniqueId", "is_enum": false, "enum_values": []}, "Description": {"... (+475 chars omitted),+1 more (map truncated)
  IfcType = 7
  Length = 3085
  Material = -> Material
  MoveBase = false
  MoveWithHost = false
  Nodes = (2) [(-1.72563e-31,0,-7.77156e-16),(3085,0,-7.77156e-16)]
  NodesOffset = 0
  Normal = (0,0,0)
  PerimeterLength = 6570
  Placement = pos=(1930,9825,2800) rot=(0,0,-1;1.5708rad)
  PredefinedType = 0
  VerticalArea = 2.628e+06
  Width = 200
FEATURE [Part::FeaturePython] Structure109  label="V15x40 V101"  # Arch/BIM 7 (typed FeaturePython)
  FaceMaker = 0
  Height = 400
  HorizontalArea = 597000
  IfcData = attributes={"GlobalId": {"name": "GlobalId", "type": "IfcGloballyUniqueId", "is_enum": false, "enum_values": []}, "Description": {"... (+475 chars omitted),+1 more (map truncated)
  IfcType = 7
  Length = 3980
  Material = -> Material
  MoveBase = false
  MoveWithHost = false
  Nodes = (2) [(-1.72563e-31,-1.42109e-15,-7.77156e-16),(3980,-1.42109e-15,-7.77156e-16)]
  NodesOffset = 0
  Normal = (0,0,0)
  PerimeterLength = 8260
  Placement = pos=(2055,9900,2800) rot=(0,0,1;0rad)
  PredefinedType = 0
  VerticalArea = 3.304e+06
  Width = 150
FEATURE [Part::FeaturePython] Structure110  label="V20x40 V121"  # Arch/BIM 7 (typed FeaturePython)
  FaceMaker = 0
  Height = 400
  HorizontalArea = 618000
  IfcData = attributes={"GlobalId": {"name": "GlobalId", "type": "IfcGloballyUniqueId", "is_enum": false, "enum_values": []}, "Description": {"... (+475 chars omitted),+1 more (map truncated)
  IfcType = 7
  Length = 3090
  Material = -> Material
  MoveBase = false
  MoveWithHost = false
  Nodes = (2) [(-1.72563e-31,0,-7.77156e-16),(3090,0,-7.77156e-16)]
  NodesOffset = 0
  Normal = (0,0,0)
  PerimeterLength = 6580
  Placement = pos=(1930,6540,2800) rot=(0,0,-1;1.5708rad)
  PredefinedType = 0
  VerticalArea = 2.632e+06
  Width = 200
FEATURE [Part::FeaturePython] Structure111  label="V20x40 V120"  # Arch/BIM 7 (typed FeaturePython)
  FaceMaker = 0
  Height = 400
  HorizontalArea = 615000
  IfcData = attributes={"GlobalId": {"name": "GlobalId", "type": "IfcGloballyUniqueId", "is_enum": false, "enum_values": []}, "Description": {"... (+475 chars omitted),+1 more (map truncated)
  IfcType = 7
  Length = 3075
  Material = -> Material
  MoveBase = false
  MoveWithHost = false
  Nodes = (2) [(-1.72563e-31,0,-7.77156e-16),(3075,0,-7.77156e-16)]
  NodesOffset = 0
  Normal = (0,0,0)
  PerimeterLength = 6550
  Placement = pos=(1930,3250,2800) rot=(0,0,-1;1.5708rad)
  PredefinedType = 0
  VerticalArea = 2.62e+06
  Width = 200
FEATURE [Part::FeaturePython] Structure112  label="V15x40 V106"  # Arch/BIM 7 (typed FeaturePython)
  FaceMaker = 0
  Height = 400
  HorizontalArea = 597000
  IfcData = attributes={"GlobalId": {"name": "GlobalId", "type": "IfcGloballyUniqueId", "is_enum": false, "enum_values": []}, "Description": {"... (+475 chars omitted),+1 more (map truncated)
  IfcType = 7
  Length = 3980
  Material = -> Material
  MoveBase = false
  MoveWithHost = false
  Nodes = (2) [(-1.72563e-31,-1.42109e-15,-7.77156e-16),(3980,-1.42109e-15,-7.77156e-16)]
  NodesOffset = 0
  Normal = (0,0,0)
  PerimeterLength = 8260
  Placement = pos=(2055,6640,2800) rot=(0,0,1;0rad)
  PredefinedType = 0
  VerticalArea = 3.304e+06
  Width = 150
FEATURE [Part::FeaturePython] Structure113  label="V15x40 V111"  # Arch/BIM 7 (typed FeaturePython)
  FaceMaker = 0
  Height = 400
  HorizontalArea = 597000
  IfcData = attributes={"GlobalId": {"name": "GlobalId", "type": "IfcGloballyUniqueId", "is_enum": false, "enum_values": []}, "Description": {"... (+475 chars omitted),+1 more (map truncated)
  IfcType = 7
  Length = 3980
  Material = -> Material
  MoveBase = false
  MoveWithHost = false
  Nodes = (2) [(-1.72563e-31,-1.42109e-15,-7.77156e-16),(3980,-1.42109e-15,-7.77156e-16)]
  NodesOffset = 0
  Normal = (0,0,0)
  PerimeterLength = 8260
  Placement = pos=(2055,3350,2800) rot=(0,0,1;0rad)
  PredefinedType = 0
  VerticalArea = 3.304e+06
  Width = 150
FEATURE [Part::FeaturePython] Structure114  label="V15x40 V116"  # Arch/BIM 7 (typed FeaturePython)
  FaceMaker = 0
  Height = 400
  HorizontalArea = 597000
  IfcData = attributes={"GlobalId": {"name": "GlobalId", "type": "IfcGloballyUniqueId", "is_enum": false, "enum_values": []}, "Description": {"... (+475 chars omitted),+1 more (map truncated)
  IfcType = 7
  Length = 3980
  Material = -> Material
  MoveBase = false
  MoveWithHost = false
  Nodes = (2) [(-1.72563e-31,-1.42109e-15,-7.77156e-16),(3980,-1.42109e-15,-7.77156e-16)]
  NodesOffset = 0
  Normal = (0,0,0)
  PerimeterLength = 8260
  Placement = pos=(2055,100,2800) rot=(0,0,1;0rad)
  PredefinedType = 0
  VerticalArea = 3.304e+06
  Width = 150
FEATURE [Part::FeaturePython] Structure115  label="V15x40 V102"  # Arch/BIM 7 (typed FeaturePython)
  FaceMaker = 0
  Height = 400
  HorizontalArea = 390000
  IfcData = attributes={"GlobalId": {"name": "GlobalId", "type": "IfcGloballyUniqueId", "is_enum": false, "enum_values": []}, "Description": {"... (+475 chars omitted),+1 more (map truncated)
  IfcType = 7
  Length = 2600
  Material = -> Material
  MoveBase = false
  MoveWithHost = false
  Nodes = (2) [(-1.72563e-31,-1.42109e-15,-7.77156e-16),(2600,-1.42109e-15,-7.77156e-16)]
  NodesOffset = 0
  Normal = (0,0,0)
  PerimeterLength = 5500
  Placement = pos=(6285,9900,2800) rot=(0,0,1;0rad)
  PredefinedType = 0
  VerticalArea = 2200000
  Width = 150
FEATURE [Part::FeaturePython] Structure116  label="V15x40 V107"  # Arch/BIM 7 (typed FeaturePython)
  FaceMaker = 0
  Height = 400
  HorizontalArea = 397500
  IfcData = attributes={"GlobalId": {"name": "GlobalId", "type": "IfcGloballyUniqueId", "is_enum": false, "enum_values": []}, "Description": {"... (+475 chars omitted),+1 more (map truncated)
  IfcType = 7
  Length = 2650
  Material = -> Material
  MoveBase = false
  MoveWithHost = false
  Nodes = (2) [(-1.72563e-31,-1.42109e-15,-7.77156e-16),(2650,-1.42109e-15,-7.77156e-16)]
  NodesOffset = 0
  Normal = (0,0,0)
  PerimeterLength = 5600
  Placement = pos=(6285,6640,2800) rot=(0,0,1;0rad)
  PredefinedType = 0
  VerticalArea = 2240000
  Width = 150
FEATURE [Part::FeaturePython] Structure117  label="V15x40 V112"  # Arch/BIM 7 (typed FeaturePython)
  FaceMaker = 0
  Height = 400
  HorizontalArea = 397500
  IfcData = attributes={"GlobalId": {"name": "GlobalId", "type": "IfcGloballyUniqueId", "is_enum": false, "enum_values": []}, "Description": {"... (+475 chars omitted),+1 more (map truncated)
  IfcType = 7
  Length = 2650
  Material = -> Material
  MoveBase = false
  MoveWithHost = false
  Nodes = (2) [(-1.72563e-31,-1.42109e-15,-7.77156e-16),(2650,-1.42109e-15,-7.77156e-16)]
  NodesOffset = 0
  Normal = (0,0,0)
  PerimeterLength = 5600
  Placement = pos=(6285,3350,2800) rot=(0,0,1;0rad)
  PredefinedType = 0
  VerticalArea = 2240000
  Width = 150
FEATURE [Part::FeaturePython] Structure118  label="V15x40 V117"  # Arch/BIM 7 (typed FeaturePython)
  FaceMaker = 0
  Height = 400
  HorizontalArea = 390000
  IfcData = attributes={"GlobalId": {"name": "GlobalId", "type": "IfcGloballyUniqueId", "is_enum": false, "enum_values": []}, "Description": {"... (+475 chars omitted),+1 more (map truncated)
  IfcType = 7
  Length = 2600
  Material = -> Material
  MoveBase = false
  MoveWithHost = false
  Nodes = (2) [(-1.72563e-31,-1.42109e-15,-7.77156e-16),(2600,-1.42109e-15,-7.77156e-16)]
  NodesOffset = 0
  Normal = (0,0,0)
  PerimeterLength = 5500
  Placement = pos=(6285,100,2800) rot=(0,0,1;0rad)
  PredefinedType = 0
  VerticalArea = 2200000
  Width = 150
FEATURE [Part::FeaturePython] Structure119  label="V15x40 V103"  # Arch/BIM 7 (typed FeaturePython)
  FaceMaker = 0
  Height = 400
  HorizontalArea = 412500
  IfcData = attributes={"GlobalId": {"name": "GlobalId", "type": "IfcGloballyUniqueId", "is_enum": false, "enum_values": []}, "Description": {"... (+475 chars omitted),+1 more (map truncated)
  IfcType = 7
  Length = 2750
  Material = -> Material
  MoveBase = false
  MoveWithHost = false
  Nodes = (2) [(-1.72563e-31,-1.42109e-15,-7.77156e-16),(2750,-1.42109e-15,-7.77156e-16)]
  NodesOffset = 0
  Normal = (0,0,0)
  PerimeterLength = 5800
  Placement = pos=(9135,9900,2800) rot=(0,0,1;0rad)
  PredefinedType = 0
  VerticalArea = 2320000
  Width = 150
FEATURE [Part::FeaturePython] Structure120  label="V15x40 V104"  # Arch/BIM 7 (typed FeaturePython)
  FaceMaker = 0
  Height = 400
  HorizontalArea = 442500
  IfcData = attributes={"GlobalId": {"name": "GlobalId", "type": "IfcGloballyUniqueId", "is_enum": false, "enum_values": []}, "Description": {"... (+475 chars omitted),+1 more (map truncated)
  IfcType = 7
  Length = 2950
  Material = -> Material
  MoveBase = false
  MoveWithHost = false
  Nodes = (2) [(-1.72563e-31,-1.42109e-15,-7.77156e-16),(2950,-1.42109e-15,-7.77156e-16)]
  NodesOffset = 0
  Normal = (0,0,0)
  PerimeterLength = 6200
  Placement = pos=(12135,9900,2800) rot=(0,0,1;0rad)
  PredefinedType = 0
  VerticalArea = 2.48e+06
  Width = 150
FEATURE [Part::FeaturePython] Structure121  label="V15x40 V108"  # Arch/BIM 7 (typed FeaturePython)
  FaceMaker = 0
  Height = 400
  HorizontalArea = 210000
  IfcData = attributes={"GlobalId": {"name": "GlobalId", "type": "IfcGloballyUniqueId", "is_enum": false, "enum_values": []}, "Description": {"... (+475 chars omitted),+1 more (map truncated)
  IfcType = 7
  Length = 1400
  Material = -> Material
  MoveBase = false
  MoveWithHost = false
  Nodes = (2) [(-1.72563e-31,-1.42109e-15,-7.77156e-16),(1400,-1.42109e-15,-7.77156e-16)]
  NodesOffset = 0
  Normal = (0,0,0)
  PerimeterLength = 3100
  Placement = pos=(9085,6640,2800) rot=(0,0,1;0rad)
  PredefinedType = 0
  VerticalArea = 1240000
  Width = 150
FEATURE [Part::FeaturePython] Structure122  label="V15x40 V113"  # Arch/BIM 7 (typed FeaturePython)
  FaceMaker = 0
  Height = 400
  HorizontalArea = 210000
  IfcData = attributes={"GlobalId": {"name": "GlobalId", "type": "IfcGloballyUniqueId", "is_enum": false, "enum_values": []}, "Description": {"... (+475 chars omitted),+1 more (map truncated)
  IfcType = 7
  Length = 1400
  Material = -> Material
  MoveBase = false
  MoveWithHost = false
  Nodes = (2) [(-1.72563e-31,-1.42109e-15,-7.77156e-16),(1400,-1.42109e-15,-7.77156e-16)]
  NodesOffset = 0
  Normal = (0,0,0)
  PerimeterLength = 3100
  Placement = pos=(9085,3350,2800) rot=(0,0,1;0rad)
  PredefinedType = 0
  VerticalArea = 1240000
  Width = 150
FEATURE [Part::FeaturePython] Structure123  label="V15x40 V118"  # Arch/BIM 7 (typed FeaturePython)
  FaceMaker = 0
  Height = 400
  HorizontalArea = 195000
  IfcData = attributes={"GlobalId": {"name": "GlobalId", "type": "IfcGloballyUniqueId", "is_enum": false, "enum_values": []}, "Description": {"... (+475 chars omitted),+1 more (map truncated)
  IfcType = 7
  Length = 1300
  Material = -> Material
  MoveBase = false
  MoveWithHost = false
  Nodes = (2) [(-1.72563e-31,-1.42109e-15,-7.77156e-16),(1300,-1.42109e-15,-7.77156e-16)]
  NodesOffset = 0
  Normal = (0,0,0)
  PerimeterLength = 2900
  Placement = pos=(9135,100,2800) rot=(0,0,1;0rad)
  PredefinedType = 0
  VerticalArea = 1160000
  Width = 150
FEATURE [Part::FeaturePython] Structure124  label="V15x40 V119"  # Arch/BIM 7 (typed FeaturePython)
  FaceMaker = 0
  Height = 400
  HorizontalArea = 445500
  IfcData = attributes={"GlobalId": {"name": "GlobalId", "type": "IfcGloballyUniqueId", "is_enum": false, "enum_values": []}, "Description": {"... (+475 chars omitted),+1 more (map truncated)
  IfcType = 7
  Length = 2970
  Material = -> Material
  MoveBase = false
  MoveWithHost = false
  Nodes = (2) [(-1.72563e-31,-1.42109e-15,-7.77156e-16),(2970,-1.42109e-15,-7.77156e-16)]
  NodesOffset = 0
  Normal = (0,0,0)
  PerimeterLength = 6240
  Placement = pos=(10685,100,2800) rot=(0,0,1;0rad)
  PredefinedType = 0
  VerticalArea = 2.496e+06
  Width = 150
FEATURE [Part::FeaturePython] Structure125  label="V15x40 V115"  # Arch/BIM 7 (typed FeaturePython)
  FaceMaker = 0
  Height = 400
  HorizontalArea = 460500
  IfcData = attributes={"GlobalId": {"name": "GlobalId", "type": "IfcGloballyUniqueId", "is_enum": false, "enum_values": []}, "Description": {"... (+475 chars omitted),+1 more (map truncated)
  IfcType = 7
  Length = 3070
  Material = -> Material
  MoveBase = false
  MoveWithHost = false
  Nodes = (2) [(-1.72563e-31,-1.42109e-15,-7.77156e-16),(3070,-1.42109e-15,-7.77156e-16)]
  NodesOffset = 0
  Normal = (0,0,0)
  PerimeterLength = 6440
  Placement = pos=(10635,3350,2800) rot=(0,0,1;0rad)
  PredefinedType = 0
  VerticalArea = 2.576e+06
  Width = 150
FEATURE [Part::FeaturePython] Structure126  label="V20x40 V133"  # Arch/BIM 7 (typed FeaturePython)
  FaceMaker = 0
  Height = 400
  HorizontalArea = 635000
  IfcData = attributes={"GlobalId": {"name": "GlobalId", "type": "IfcGloballyUniqueId", "is_enum": false, "enum_values": []}, "Description": {"... (+475 chars omitted),+1 more (map truncated)
  IfcType = 7
  Length = 3175
  Material = -> Material
  MoveBase = false
  MoveWithHost = false
  Nodes = (2) [(-1.72563e-31,0,-7.77156e-16),(3175,0,-7.77156e-16)]
  NodesOffset = 0
  Normal = (0,0,0)
  PerimeterLength = 6750
  Placement = pos=(13780,175,2800) rot=(0,0,1;1.5708rad)
  PredefinedType = 0
  VerticalArea = 2.7e+06
  Width = 200
FEATURE [Part::FeaturePython] Structure127  label="V20x40 V134"  # Arch/BIM 7 (typed FeaturePython)
  FaceMaker = 0
  Height = 400
  HorizontalArea = 509000
  IfcData = attributes={"GlobalId": {"name": "GlobalId", "type": "IfcGloballyUniqueId", "is_enum": false, "enum_values": []}, "Description": {"... (+475 chars omitted),+1 more (map truncated)
  IfcType = 7
  Length = 2545
  Material = -> Material
  MoveBase = false
  MoveWithHost = false
  Nodes = (2) [(-1.72563e-31,0,-7.77156e-16),(2545,0,-7.77156e-16)]
  NodesOffset = 0
  Normal = (0,0,0)
  PerimeterLength = 5490
  Placement = pos=(13780,3350,2800) rot=(0,0,1;1.5708rad)
  PredefinedType = 0
  VerticalArea = 2196000
  Width = 200
FEATURE [Part::FeaturePython] Structure128  label="V20x40 V135"  # Arch/BIM 7 (typed FeaturePython)
  FaceMaker = 0
  Height = 400
  HorizontalArea = 756000
  IfcData = attributes={"GlobalId": {"name": "GlobalId", "type": "IfcGloballyUniqueId", "is_enum": false, "enum_values": []}, "Description": {"... (+475 chars omitted),+1 more (map truncated)
  IfcType = 7
  Length = 3780
  Material = -> Material
  MoveBase = false
  MoveWithHost = false
  Nodes = (2) [(-1.72563e-31,0,-7.77156e-16),(3780,0,-7.77156e-16)]
  NodesOffset = 0
  Normal = (0,0,0)
  PerimeterLength = 7960
  Placement = pos=(15210,6045,2800) rot=(0,0,1;1.5708rad)
  PredefinedType = 0
  VerticalArea = 3.184e+06
  Width = 200
FEATURE [Part::FeaturePython] Structure129  label="V15x40 V109"  # Arch/BIM 7 (typed FeaturePython)
  FaceMaker = 0
  Height = 400
  HorizontalArea = 235500
  IfcData = attributes={"GlobalId": {"name": "GlobalId", "type": "IfcGloballyUniqueId", "is_enum": false, "enum_values": []}, "Description": {"... (+475 chars omitted),+1 more (map truncated)
  IfcType = 7
  Length = 1570
  Material = -> Material
  MoveBase = false
  MoveWithHost = false
  Nodes = (2) [(-1.72563e-31,-1.42109e-15,-7.77156e-16),(1570,-1.42109e-15,-7.77156e-16)]
  NodesOffset = 0
  Normal = (0,0,0)
  PerimeterLength = 3440
  Placement = pos=(13655,5970,2800) rot=(0,0,1;3.14159rad)
  PredefinedType = 0
  VerticalArea = 1.376e+06
  Width = 150
FEATURE [Part::FeaturePython] Structure130  label="V15x40 V110"  # Arch/BIM 7 (typed FeaturePython)
  FaceMaker = 0
  Height = 400
  HorizontalArea = 177000
  IfcData = attributes={"GlobalId": {"name": "GlobalId", "type": "IfcGloballyUniqueId", "is_enum": false, "enum_values": []}, "Description": {"... (+475 chars omitted),+1 more (map truncated)
  IfcType = 7
  Length = 1180
  Material = -> Material
  MoveBase = false
  MoveWithHost = false
  Nodes = (2) [(-1.72563e-31,-1.42109e-15,-7.77156e-16),(1180,-1.42109e-15,-7.77156e-16)]
  NodesOffset = 0
  Normal = (0,0,0)
  PerimeterLength = 2660
  Placement = pos=(13905,5970,2800) rot=(0,0,1;0rad)
  PredefinedType = 0
  VerticalArea = 1064000
  Width = 150
FEATURE [Part::FeaturePython] Structure131  label="V15x40 V125"  # Arch/BIM 7 (typed FeaturePython)
  FaceMaker = 0
  Height = 400
  HorizontalArea = 466500
  IfcData = attributes={"GlobalId": {"name": "GlobalId", "type": "IfcGloballyUniqueId", "is_enum": false, "enum_values": []}, "Description": {"... (+475 chars omitted),+1 more (map truncated)
  IfcType = 7
  Length = 3110
  Material = -> Material
  MoveBase = false
  MoveWithHost = false
  Nodes = (2) [(-1.72563e-31,-1.42109e-15,-7.77156e-16),(3110,-1.42109e-15,-7.77156e-16)]
  NodesOffset = 0
  Normal = (0,0,0)
  PerimeterLength = 6520
  Placement = pos=(6160,9825,2800) rot=(0,0,-1;1.5708rad)
  PredefinedType = 0
  VerticalArea = 2.608e+06
  Width = 150
FEATURE [Part::FeaturePython] Structure132  label="V15x40 V124"  # Arch/BIM 7 (typed FeaturePython)
  FaceMaker = 0
  Height = 400
  HorizontalArea = 471000
  IfcData = attributes={"GlobalId": {"name": "GlobalId", "type": "IfcGloballyUniqueId", "is_enum": false, "enum_values": []}, "Description": {"... (+475 chars omitted),+1 more (map truncated)
  IfcType = 7
  Length = 3140
  Material = -> Material
  MoveBase = false
  MoveWithHost = false
  Nodes = (2) [(-1.72563e-31,-1.42109e-15,-7.77156e-16),(3140,-1.42109e-15,-7.77156e-16)]
  NodesOffset = 0
  Normal = (0,0,0)
  PerimeterLength = 6580
  Placement = pos=(6160,6565,2800) rot=(0,0,-1;1.5708rad)
  PredefinedType = 0
  VerticalArea = 2.632e+06
  Width = 150
FEATURE [Part::FeaturePython] Structure133  label="V15x40 V123"  # Arch/BIM 7 (typed FeaturePython)
  FaceMaker = 0
  Height = 400
  HorizontalArea = 465000
  IfcData = attributes={"GlobalId": {"name": "GlobalId", "type": "IfcGloballyUniqueId", "is_enum": false, "enum_values": []}, "Description": {"... (+475 chars omitted),+1 more (map truncated)
  IfcType = 7
  Length = 3100
  Material = -> Material
  MoveBase = false
  MoveWithHost = false
  Nodes = (2) [(-1.72563e-31,-1.42109e-15,-7.77156e-16),(3100,-1.42109e-15,-7.77156e-16)]
  NodesOffset = 0
  Normal = (0,0,0)
  PerimeterLength = 6500
  Placement = pos=(6160,3275,2800) rot=(0,0,-1;1.5708rad)
  PredefinedType = 0
  VerticalArea = 2.6e+06
  Width = 150
FEATURE [Part::FeaturePython] Structure134  label="V15x40 V128"  # Arch/BIM 7 (typed FeaturePython)
  FaceMaker = 0
  Height = 400
  HorizontalArea = 459000
  IfcData = attributes={"GlobalId": {"name": "GlobalId", "type": "IfcGloballyUniqueId", "is_enum": false, "enum_values": []}, "Description": {"... (+475 chars omitted),+1 more (map truncated)
  IfcType = 7
  Length = 3060
  Material = -> Material
  MoveBase = false
  MoveWithHost = false
  Nodes = (2) [(-1.72563e-31,-1.42109e-15,-7.77156e-16),(3060,-1.42109e-15,-7.77156e-16)]
  NodesOffset = 0
  Normal = (0,0,0)
  PerimeterLength = 6420
  Placement = pos=(9010,9825,2800) rot=(0,0,-1;1.5708rad)
  PredefinedType = 0
  VerticalArea = 2.568e+06
  Width = 150
FEATURE [Part::FeaturePython] Structure135  label="V15x40 V127"  # Arch/BIM 7 (typed FeaturePython)
  FaceMaker = 0
  Height = 400
  HorizontalArea = 456000
  IfcData = attributes={"GlobalId": {"name": "GlobalId", "type": "IfcGloballyUniqueId", "is_enum": false, "enum_values": []}, "Description": {"... (+475 chars omitted),+1 more (map truncated)
  IfcType = 7
  Length = 3040
  Material = -> Material
  MoveBase = false
  MoveWithHost = false
  Nodes = (2) [(-1.72563e-31,-1.42109e-15,-7.77156e-16),(3040,-1.42109e-15,-7.77156e-16)]
  NodesOffset = 0
  Normal = (0,0,0)
  PerimeterLength = 6380
  Placement = pos=(9010,6515,2800) rot=(0,0,-1;1.5708rad)
  PredefinedType = 0
  VerticalArea = 2.552e+06
  Width = 150
FEATURE [Part::FeaturePython] Structure136  label="V15x40 V126"  # Arch/BIM 7 (typed FeaturePython)
  FaceMaker = 0
  Height = 400
  HorizontalArea = 457500
  IfcData = attributes={"GlobalId": {"name": "GlobalId", "type": "IfcGloballyUniqueId", "is_enum": false, "enum_values": []}, "Description": {"... (+475 chars omitted),+1 more (map truncated)
  IfcType = 7
  Length = 3050
  Material = -> Material
  MoveBase = false
  MoveWithHost = false
  Nodes = (2) [(-1.72563e-31,-1.42109e-15,-7.77156e-16),(3050,-1.42109e-15,-7.77156e-16)]
  NodesOffset = 0
  Normal = (0,0,0)
  PerimeterLength = 6400
  Placement = pos=(9010,3225,2800) rot=(0,0,-1;1.5708rad)
  PredefinedType = 0
  VerticalArea = 2.56e+06
  Width = 150
FEATURE [Part::FeaturePython] Structure137  label="V15x40 V132"  # Arch/BIM 7 (typed FeaturePython)
  FaceMaker = 0
  Height = 400
  HorizontalArea = 207000
  IfcData = attributes={"GlobalId": {"name": "GlobalId", "type": "IfcGloballyUniqueId", "is_enum": false, "enum_values": []}, "Description": {"... (+475 chars omitted),+1 more (map truncated)
  IfcType = 7
  Length = 1380
  Material = -> Material
  MoveBase = false
  MoveWithHost = false
  Nodes = (2) [(-1.72563e-31,-1.42109e-15,-7.77156e-16),(1380,-1.42109e-15,-7.77156e-16)]
  NodesOffset = 0
  Normal = (0,0,0)
  PerimeterLength = 3060
  Placement = pos=(12010,9825,2800) rot=(0,0,-1;1.5708rad)
  PredefinedType = 0
  VerticalArea = 1224000
  Width = 150
FEATURE [Part::FeaturePython] Structure138  label="V15x40 V131"  # Arch/BIM 7 (typed FeaturePython)
  FaceMaker = 0
  Height = 400
  HorizontalArea = 207000
  IfcData = attributes={"GlobalId": {"name": "GlobalId", "type": "IfcGloballyUniqueId", "is_enum": false, "enum_values": []}, "Description": {"... (+475 chars omitted),+1 more (map truncated)
  IfcType = 7
  Length = 1380
  Material = -> Material
  MoveBase = false
  MoveWithHost = false
  Nodes = (2) [(-1.72563e-31,-1.42109e-15,-7.77156e-16),(1380,-1.42109e-15,-7.77156e-16)]
  NodesOffset = 0
  Normal = (0,0,0)
  PerimeterLength = 3060
  Placement = pos=(10560,8445,2800) rot=(0,0,1;1.5708rad)
  PredefinedType = 0
  VerticalArea = 1224000
  Width = 150
FEATURE [Part::FeaturePython] Structure139  label="V15x40 V130"  # Arch/BIM 7 (typed FeaturePython)
  FaceMaker = 0
  Height = 400
  HorizontalArea = 363000
  IfcData = attributes={"GlobalId": {"name": "GlobalId", "type": "IfcGloballyUniqueId", "is_enum": false, "enum_values": []}, "Description": {"... (+475 chars omitted),+1 more (map truncated)
  IfcType = 7
  Length = 2420
  Material = -> Material
  MoveBase = false
  MoveWithHost = false
  Nodes = (2) [(-1.72563e-31,-1.42109e-15,-7.77156e-16),(2420,-1.42109e-15,-7.77156e-16)]
  NodesOffset = 0
  Normal = (0,0,0)
  PerimeterLength = 5140
  Placement = pos=(10560,3475,2800) rot=(0,0,1;1.5708rad)
  PredefinedType = 0
  VerticalArea = 2056000
  Width = 150
FEATURE [Part::FeaturePython] Structure140  label="V15x40 V129"  # Arch/BIM 7 (typed FeaturePython)
  FaceMaker = 0
  Height = 400
  HorizontalArea = 457500
  IfcData = attributes={"GlobalId": {"name": "GlobalId", "type": "IfcGloballyUniqueId", "is_enum": false, "enum_values": []}, "Description": {"... (+475 chars omitted),+1 more (map truncated)
  IfcType = 7
  Length = 3050
  Material = -> Material
  MoveBase = false
  MoveWithHost = false
  Nodes = (2) [(-1.72563e-31,-1.42109e-15,-7.77156e-16),(3050,-1.42109e-15,-7.77156e-16)]
  NodesOffset = 0
  Normal = (0,0,0)
  PerimeterLength = 6400
  Placement = pos=(10560,3225,2800) rot=(0,0,-1;1.5708rad)
  PredefinedType = 0
  VerticalArea = 2.56e+06
  Width = 150
FEATURE [Part::FeaturePython] Structure141  label="V15x40 V105"  # Arch/BIM 7 (typed FeaturePython)
  FaceMaker = 0
  Height = 400
  HorizontalArea = 453750
  IfcData = attributes={"GlobalId": {"name": "GlobalId", "type": "IfcGloballyUniqueId", "is_enum": false, "enum_values": []}, "Description": {"... (+475 chars omitted),+1 more (map truncated)
  IfcType = 7
  Length = 3025
  Material = -> Material
  MoveBase = false
  MoveWithHost = false
  Nodes = (2) [(-1.72563e-31,-1.42109e-15,-7.77156e-16),(3025,-1.42109e-15,-7.77156e-16)]
  NodesOffset = 0
  Normal = (0,0,0)
  PerimeterLength = 6350
  Placement = pos=(12085,8370,2800) rot=(0,0,1;0rad)
  PredefinedType = 0
  VerticalArea = 2.54e+06
  Width = 150
FEATURE [Part::FeaturePython] Structure197  label="L101"  # Arch/BIM 172 (typed FeaturePython)
  Base = -> Rectangle004
  FaceMaker = 0
  Height = 150
  HorizontalArea = 12611050
  IfcData = attributes={"GlobalId": {"name": "GlobalId", "type": "IfcGloballyUniqueId", "is_enum": false, "enum_values": []}, "Description": {"... (+484 chars omitted),+1 more (map truncated)
  IfcType = 172
  Length = 0
  Material = -> Material
  MoveBase = false
  MoveWithHost = false
  Nodes = (2) [(4057.5,8270,3000),(4057.5,8270,2850)]
  NodesOffset = 0
  Normal = (0,0,-1)
  PerimeterLength = 14330
  PredefinedType = 0
  VerticalArea = 2149500
  Width = 150
FEATURE [Part::FeaturePython] Structure198  label="L107"  # Arch/BIM 172 (typed FeaturePython)
  Base = -> Rectangle005
  FaceMaker = 0
  Height = 150
  HorizontalArea = 12732700
  IfcData = attributes={"GlobalId": {"name": "GlobalId", "type": "IfcGloballyUniqueId", "is_enum": false, "enum_values": []}, "Description": {"... (+484 chars omitted),+1 more (map truncated)
  IfcType = 172
  Length = 0
  Material = -> Material
  MoveBase = false
  MoveWithHost = false
  Nodes = (2) [(4057.5,4995,3000),(4057.5,4995,2850)]
  NodesOffset = 0
  Normal = (0,0,-1)
  PerimeterLength = 14390
  PredefinedType = 0
  VerticalArea = 2158500
  Width = 150
FEATURE [Part::FeaturePython] Structure199  label="L113"  # Arch/BIM 172 (typed FeaturePython)
  Base = -> Rectangle006
  FaceMaker = 0
  Height = 150
  HorizontalArea = 1.25705e+07
  IfcData = attributes={"GlobalId": {"name": "GlobalId", "type": "IfcGloballyUniqueId", "is_enum": false, "enum_values": []}, "Description": {"... (+484 chars omitted),+1 more (map truncated)
  IfcType = 172
  Length = 0
  Material = -> Material
  MoveBase = false
  MoveWithHost = false
  Nodes = (2) [(4057.5,1725,3000),(4057.5,1725,2850)]
  NodesOffset = 0
  Normal = (0,0,-1)
  PerimeterLength = 14310
  PredefinedType = 0
  VerticalArea = 2146500
  Width = 150
FEATURE [Part::FeaturePython] Structure200  label="V15x40 V102a"  # Arch/BIM 7 (typed FeaturePython)
  FaceMaker = 0
  Height = 400
  HorizontalArea = 405000
  IfcData = attributes={"GlobalId": {"name": "GlobalId", "type": "IfcGloballyUniqueId", "is_enum": false, "enum_values": []}, "Description": {"... (+475 chars omitted),+1 more (map truncated)
  IfcType = 7
  Length = 2700
  Material = -> Material
  MoveBase = false
  MoveWithHost = false
  Nodes = (2) [(-1.72563e-31,-1.42109e-15,-7.77156e-16),(2700,-1.42109e-15,-7.77156e-16)]
  NodesOffset = 0
  Normal = (0,0,0)
  PerimeterLength = 5700
  Placement = pos=(8935,8295,2800) rot=(0,0,1;3.14159rad)
  PredefinedType = 0
  VerticalArea = 2.28e+06
  Width = 150
FEATURE [Part::FeaturePython] Structure201  label="V15x40 V107a"  # Arch/BIM 7 (typed FeaturePython)
  FaceMaker = 0
  Height = 400
  HorizontalArea = 405000
  IfcData = attributes={"GlobalId": {"name": "GlobalId", "type": "IfcGloballyUniqueId", "is_enum": false, "enum_values": []}, "Description": {"... (+475 chars omitted),+1 more (map truncated)
  IfcType = 7
  Length = 2700
  Material = -> Material
  MoveBase = false
  MoveWithHost = false
  Nodes = (2) [(-1.72563e-31,-1.42109e-15,-7.77156e-16),(2700,-1.42109e-15,-7.77156e-16)]
  NodesOffset = 0
  Normal = (0,0,0)
  PerimeterLength = 5700
  Placement = pos=(8935,4995,2800) rot=(0,0,1;3.14159rad)
  PredefinedType = 0
  VerticalArea = 2.28e+06
  Width = 150
FEATURE [Part::FeaturePython] Structure202  label="V15x40 V112a"  # Arch/BIM 7 (typed FeaturePython)
  FaceMaker = 0
  Height = 400
  HorizontalArea = 405000
  IfcData = attributes={"GlobalId": {"name": "GlobalId", "type": "IfcGloballyUniqueId", "is_enum": false, "enum_values": []}, "Description": {"... (+475 chars omitted),+1 more (map truncated)
  IfcType = 7
  Length = 2700
  Material = -> Material
  MoveBase = false
  MoveWithHost = false
  Nodes = (2) [(-1.72563e-31,-1.42109e-15,-7.77156e-16),(2700,-1.42109e-15,-7.77156e-16)]
  NodesOffset = 0
  Normal = (0,0,0)
  PerimeterLength = 5700
  Placement = pos=(8935,1700,2800) rot=(0,0,1;3.14159rad)
  PredefinedType = 0
  VerticalArea = 2.28e+06
  Width = 150
FEATURE [Part::FeaturePython] Structure204  label="V15x40 V130a"  # Arch/BIM 7 (typed FeaturePython)
  FaceMaker = 0
  Height = 400
  HorizontalArea = 370500
  IfcData = attributes={"GlobalId": {"name": "GlobalId", "type": "IfcGloballyUniqueId", "is_enum": false, "enum_values": []}, "Description": {"... (+475 chars omitted),+1 more (map truncated)
  IfcType = 7
  Length = 2470
  Material = -> Material
  MoveBase = false
  MoveWithHost = false
  Nodes = (2) [(-1.72563e-31,-1.42109e-15,-7.77156e-16),(2470,-1.42109e-15,-7.77156e-16)]
  NodesOffset = 0
  Normal = (0,0,0)
  PerimeterLength = 5240
  Placement = pos=(12010,3425,2800) rot=(0,0,1;1.5708rad)
  PredefinedType = 0
  VerticalArea = 2096000
  Width = 150
FEATURE [App::GeometryPython] BuildingPart009  label="Vigas sobre PB"  # Arch/BIM 172 (typed FeaturePython)
  Area = 0
  Group = -> [Structure109,Structure115,Structure200,Structure119,Structure120,Structure141,Structure112,Structure116,Structure201,Structure121,Structure129,Structure130,Structure113,Structure117,Structure202,Structure122,Structure125,Structure114,Structure118,Structure123,Structure124,Structure133,Structure132,Structure131,Structure136,Structure135,Structure134,Structure140,Structure139,Structure204,+8 more]
  Height = 0
  HeightPropagate = true
  IfcData = attributes={"GlobalId": {"name": "GlobalId", "type": "IfcGloballyUniqueId", "is_enum": false, "enum_values": []}, "Description": {"... (+484 chars omitted),+1 more (map truncated)
  IfcType = 172
  LevelOffset = 0
  PredefinedType = 0
FEATURE [Part::FeaturePython] Structure205  label="L102"  # Arch/BIM 172 (typed FeaturePython)
  Base = -> Rectangle014
  FaceMaker = 0
  Height = 150
  HorizontalArea = 3928500
  IfcData = attributes={"GlobalId": {"name": "GlobalId", "type": "IfcGloballyUniqueId", "is_enum": false, "enum_values": []}, "Description": {"... (+484 chars omitted),+1 more (map truncated)
  IfcType = 172
  Length = 0
  Material = -> Material
  MoveBase = false
  MoveWithHost = false
  Nodes = (2) [(7585,9097.5,3000),(7585,9097.5,2850)]
  NodesOffset = 0
  Normal = (0,0,-1)
  PerimeterLength = 8310
  PredefinedType = 0
  VerticalArea = 1246500
  Width = 150
FEATURE [Part::FeaturePython] Structure206  label="L103"  # Arch/BIM 172 (typed FeaturePython)
  Base = -> Wire
  FaceMaker = 0
  Height = 150
  HorizontalArea = 3.9285e+06
  IfcData = attributes={"GlobalId": {"name": "GlobalId", "type": "IfcGloballyUniqueId", "is_enum": false, "enum_values": []}, "Description": {"... (+484 chars omitted),+1 more (map truncated)
  IfcType = 172
  Length = 0
  Material = -> Material
  MoveBase = false
  MoveWithHost = false
  Nodes = (2) [(7543.76,7449.37,3000),(7543.76,7449.37,2850)]
  NodesOffset = 0
  Normal = (0,0,-1)
  PerimeterLength = 8410
  Placement = pos=(0,0,-150) rot=(0,0,1;0rad)
  PredefinedType = 0
  VerticalArea = 1261500
  Width = 150
FEATURE [Part::FeaturePython] Structure207  label="L108"  # Arch/BIM 172 (typed FeaturePython)
  Base = -> Wire001
  FaceMaker = 0
  Height = 150
  HorizontalArea = 3.90134e+06
  IfcData = attributes={"GlobalId": {"name": "GlobalId", "type": "IfcGloballyUniqueId", "is_enum": false, "enum_values": []}, "Description": {"... (+484 chars omitted),+1 more (map truncated)
  IfcType = 172
  Length = 0
  Material = -> Material
  MoveBase = false
  MoveWithHost = false
  Nodes = (2) [(7543.46,5835.61,3000),(7543.46,5835.61,2850)]
  NodesOffset = 0
  Normal = (0,0,-1)
  PerimeterLength = 8389.89
  Placement = pos=(0,0,-150) rot=(0,0,1;0rad)
  PredefinedType = 0
  VerticalArea = 1.25848e+06
  Width = 150
FEATURE [Part::FeaturePython] Structure208  label="L109"  # Arch/BIM 172 (typed FeaturePython)
  Base = -> Rectangle015
  FaceMaker = 0
  Height = 150
  HorizontalArea = 4.0365e+06
  IfcData = attributes={"GlobalId": {"name": "GlobalId", "type": "IfcGloballyUniqueId", "is_enum": false, "enum_values": []}, "Description": {"... (+484 chars omitted),+1 more (map truncated)
  IfcType = 172
  Length = 0
  Material = -> Material
  MoveBase = false
  MoveWithHost = false
  Nodes = (2) [(7585,4172.5,3000),(7585,4172.5,2850)]
  NodesOffset = 0
  Normal = (0,0,-1)
  PerimeterLength = 8390
  PredefinedType = 0
  VerticalArea = 1258500
  Width = 150
FEATURE [Part::FeaturePython] Structure209  label="L114"  # Arch/BIM 172 (typed FeaturePython)
  Base = -> Wire002
  FaceMaker = 0
  Height = 150
  HorizontalArea = 3.91484e+06
  IfcData = attributes={"GlobalId": {"name": "GlobalId", "type": "IfcGloballyUniqueId", "is_enum": false, "enum_values": []}, "Description": {"... (+484 chars omitted),+1 more (map truncated)
  IfcType = 172
  Length = 0
  Material = -> Material
  MoveBase = false
  MoveWithHost = false
  Nodes = (2) [(7543.6,2543.13,3000),(7543.6,2543.13,2850)]
  NodesOffset = 0
  Normal = (0,0,-1)
  PerimeterLength = 8399.89
  Placement = pos=(0,0,-150) rot=(0,0,1;0rad)
  PredefinedType = 0
  VerticalArea = 1.25998e+06
  Width = 150
FEATURE [Part::FeaturePython] Structure210  label="L115"  # Arch/BIM 172 (typed FeaturePython)
  Base = -> Rectangle016
  FaceMaker = 0
  Height = 150
  HorizontalArea = 3.915e+06
  IfcData = attributes={"GlobalId": {"name": "GlobalId", "type": "IfcGloballyUniqueId", "is_enum": false, "enum_values": []}, "Description": {"... (+484 chars omitted),+1 more (map truncated)
  IfcType = 172
  Length = 0
  Material = -> Material
  MoveBase = false
  MoveWithHost = false
  Nodes = (2) [(7585,900,3000),(7585,900,2850)]
  NodesOffset = 0
  Normal = (0,0,-1)
  PerimeterLength = 8300
  PredefinedType = 0
  VerticalArea = 1.245e+06
  Width = 150
FEATURE [Part::FeaturePython] Structure211  label="L104"  # Arch/BIM 172 (typed FeaturePython)
  Base = -> Rectangle008
  FaceMaker = 0
  Height = 150
  HorizontalArea = 4354000
  IfcData = attributes={"GlobalId": {"name": "GlobalId", "type": "IfcGloballyUniqueId", "is_enum": false, "enum_values": []}, "Description": {"... (+484 chars omitted),+1 more (map truncated)
  IfcType = 172
  Length = 0
  Material = -> Material
  MoveBase = false
  MoveWithHost = false
  Nodes = (2) [(9785,8270,3000),(9785,8270,2850)]
  NodesOffset = 0
  Normal = (0,0,-1)
  PerimeterLength = 9020
  PredefinedType = 0
  VerticalArea = 1353000
  Width = 150
FEATURE [Part::FeaturePython] Structure212  label="L110"  # Arch/BIM 172 (typed FeaturePython)
  Base = -> Rectangle011
  FaceMaker = 0
  Height = 150
  HorizontalArea = 4396000
  IfcData = attributes={"GlobalId": {"name": "GlobalId", "type": "IfcGloballyUniqueId", "is_enum": false, "enum_values": []}, "Description": {"... (+484 chars omitted),+1 more (map truncated)
  IfcType = 172
  Length = 0
  Material = -> Material
  MoveBase = false
  MoveWithHost = false
  Nodes = (2) [(9785,4995,3000),(9785,4995,2850)]
  NodesOffset = 0
  Normal = (0,0,-1)
  PerimeterLength = 9080
  PredefinedType = 0
  VerticalArea = 1362000
  Width = 150
FEATURE [Part::FeaturePython] Structure213  label="L116"  # Arch/BIM 172 (typed FeaturePython)
  Base = -> Rectangle013
  FaceMaker = 0
  Height = 150
  HorizontalArea = 4.34e+06
  IfcData = attributes={"GlobalId": {"name": "GlobalId", "type": "IfcGloballyUniqueId", "is_enum": false, "enum_values": []}, "Description": {"... (+484 chars omitted),+1 more (map truncated)
  IfcType = 172
  Length = 0
  Material = -> Material
  MoveBase = false
  MoveWithHost = false
  Nodes = (2) [(9785,1725,3000),(9785,1725,2850)]
  NodesOffset = 0
  Normal = (0,0,-1)
  PerimeterLength = 9000
  PredefinedType = 0
  VerticalArea = 1350000
  Width = 150
FEATURE [Part::FeaturePython] Structure214  label="L105"  # Arch/BIM 172 (typed FeaturePython)
  Base = -> Rectangle009
  FaceMaker = 0
  Height = 150
  HorizontalArea = 1.794e+06
  IfcData = attributes={"GlobalId": {"name": "GlobalId", "type": "IfcGloballyUniqueId", "is_enum": false, "enum_values": []}, "Description": {"... (+484 chars omitted),+1 more (map truncated)
  IfcType = 172
  Length = 0
  Material = -> Material
  MoveBase = false
  MoveWithHost = false
  Nodes = (2) [(11285,9135,3000),(11285,9135,2850)]
  NodesOffset = 0
  Normal = (0,0,-1)
  PerimeterLength = 5360
  PredefinedType = 0
  VerticalArea = 804000
  Width = 150
FEATURE [Part::FeaturePython] Structure215  label="L111"  # Arch/BIM 172 (typed FeaturePython)
  Base = -> Rectangle018
  FaceMaker = 0
  Height = 150
  HorizontalArea = 3.211e+06
  IfcData = attributes={"GlobalId": {"name": "GlobalId", "type": "IfcGloballyUniqueId", "is_enum": false, "enum_values": []}, "Description": {"... (+484 chars omitted),+1 more (map truncated)
  IfcType = 172
  Length = 0
  Material = -> Material
  MoveBase = false
  MoveWithHost = false
  Nodes = (2) [(11285,4660,3000),(11285,4660,2850)]
  NodesOffset = 0
  Normal = (0,0,-1)
  PerimeterLength = 7540
  Placement = pos=(0,0,-150) rot=(0,0,1;0rad)
  PredefinedType = 0
  VerticalArea = 1.131e+06
  Width = 150
FEATURE [Part::FeaturePython] Structure216  label="L117"  # Arch/BIM 172 (typed FeaturePython)
  Base = -> Rectangle020
  FaceMaker = 0
  Height = 150
  HorizontalArea = 9439500
  IfcData = attributes={"GlobalId": {"name": "GlobalId", "type": "IfcGloballyUniqueId", "is_enum": false, "enum_values": []}, "Description": {"... (+484 chars omitted),+1 more (map truncated)
  IfcType = 172
  Length = 0
  Material = -> Material
  MoveBase = false
  MoveWithHost = false
  Nodes = (2) [(12157.5,1725,3000),(12157.5,1725,2850)]
  NodesOffset = 0
  Normal = (0,0,-1)
  PerimeterLength = 12290
  PredefinedType = 0
  VerticalArea = 1843500
  Width = 150
FEATURE [Part::FeaturePython] Structure217  label="L112"  # Arch/BIM 172 (typed FeaturePython)
  Base = -> Rectangle019
  FaceMaker = 0
  Height = 150
  HorizontalArea = 3.93965e+06
  IfcData = attributes={"GlobalId": {"name": "GlobalId", "type": "IfcGloballyUniqueId", "is_enum": false, "enum_values": []}, "Description": {"... (+484 chars omitted),+1 more (map truncated)
  IfcType = 172
  Length = 0
  Material = -> Material
  MoveBase = false
  MoveWithHost = false
  Nodes = (2) [(12882.5,4660,3000),(12882.5,4660,2850)]
  NodesOffset = 0
  Normal = (0,0,-1)
  PerimeterLength = 8130
  PredefinedType = 0
  VerticalArea = 1.2195e+06
  Width = 150
FEATURE [Part::FeaturePython] Structure218  label="L106"  # Arch/BIM 172 (typed FeaturePython)
  Base = -> Rectangle017
  FaceMaker = 0
  Height = 150
  HorizontalArea = 4174500
  IfcData = attributes={"GlobalId": {"name": "GlobalId", "type": "IfcGloballyUniqueId", "is_enum": false, "enum_values": []}, "Description": {"... (+484 chars omitted),+1 more (map truncated)
  IfcType = 172
  Length = 0
  Material = -> Material
  MoveBase = false
  MoveWithHost = false
  Nodes = (2) [(13597.5,9135,3000),(13597.5,9135,2850)]
  NodesOffset = 0
  Normal = (0,0,-1)
  PerimeterLength = 8810
  PredefinedType = 0
  VerticalArea = 1321500
  Width = 150
FEATURE [App::GeometryPython] BuildingPart014  label="Losas sobre PB"  # Arch/BIM 172 (typed FeaturePython)
  Area = 0
  Group = -> [Structure197,Structure205,Structure206,Structure211,Structure214,Structure218,Structure198,Structure207,Structure208,Structure212,Structure215,Structure217,Structure199,Structure209,Structure210,Structure213,Structure216]
  Height = 0
  HeightPropagate = true
  IfcData = attributes={"GlobalId": {"name": "GlobalId", "type": "IfcGloballyUniqueId", "is_enum": false, "enum_values": []}, "Description": {"... (+484 chars omitted),+1 more (map truncated)
  IfcType = 172
  LevelOffset = 0
  PredefinedType = 0
FEATURE [App::GeometryPython] BuildingPart001  label="Nivel 0"  # Arch/BIM 172 (typed FeaturePython)
  Area = 24900000
  Group = -> [BuildingPart004,BuildingPart014,Wall001,BuildingPart009]
  Height = 0
  HeightPropagate = true
  IfcData = attributes={"GlobalId": {"name": "GlobalId", "type": "IfcGloballyUniqueId", "is_enum": false, "enum_values": []}, "Description": {"... (+484 chars omitted),+1 more (map truncated)
  IfcType = 172
  LevelOffset = 0
  PredefinedType = 0
FEATURE [App::FeaturePython] Section004  label="SEC-01-Corte Columnas Nivel 0"  # WARN: FeaturePython — macro-defined, semantics opaque (R4)
  Clip = false
  Objects = -> [BuildingPart001,Axis,Axis004]
  OnlySolids = false
  Placement = pos=(0,0,300) rot=(0,0,1;0rad)
  UseMaterialColorForFill = true
FEATURE [App::DocumentObjectGroupPython] MaterialContainer  label="Materials"  # scripted group (container) (typed FeaturePython)
  Group = -> [Material]
FEATURE [Part::Part2DObjectPython] Shape2DView  label="DRW-01-Corte Columnas Nivel 0"  # Draft 2D object (typed FeaturePython)
  Base = -> Section004
  FuseArch = false
  HiddenLines = false
  InPlace = true
  Placement = pos=(0,-20000,0) rot=(0,0,1;0rad)
  Projection = (0,0,1)
  ProjectionMode = 3
  SegmentLength = 0.05
  Tessellation = false
  VisibleOnly = false
FEATURE [Part::FeaturePython] Structure401  label="Beam046"  # Arch/BIM 7 (typed FeaturePython)
  FaceMaker = 0
  Height = 300
  HorizontalArea = 337500
  IfcData = attributes={"GlobalId": {"name": "GlobalId", "type": "IfcGloballyUniqueId", "is_enum": false, "enum_values": []}, "Description": {"... (+475 chars omitted),+1 more (map truncated)
  IfcType = 7
  Length = 1125
  Material = -> Material
  MoveBase = false
  MoveWithHost = false
  Nodes = (2) [(1.2326e-31,-1.51582e-15,5.55112e-16),(1125,-1.51582e-15,5.55112e-16)]
  NodesOffset = 0
  Normal = (0,0,0)
  PerimeterLength = 2850
  Placement = pos=(9360,6640,-650) rot=(0,0,1;0rad)
  PredefinedType = 0
  VerticalArea = 855000
  Width = 300
FEATURE [App::GeometryPython] BuildingPart005  label="Vigas riostras"  # Arch/BIM 172 (typed FeaturePython)
  Area = 0
  Group = -> [Beam,Beam001,Structure041,Structure042,Structure043,Structure044,Structure045,Structure046,Structure048,Structure049,Structure053,Structure056,Structure059,Structure060,Structure061,Structure064,Structure065,Structure066,Structure067,Structure068,Structure069,Structure070,Structure071,Structure072,Structure073,Structure074,Structure075,Structure076,Structure077,Structure078,Structure079,+2 more]
  Height = 0
  HeightPropagate = true
  IfcData = attributes={"GlobalId": {"name": "GlobalId", "type": "IfcGloballyUniqueId", "is_enum": false, "enum_values": []}, "Description": {"... (+484 chars omitted),+1 more (map truncated)
  IfcType = 172
  LevelOffset = 0
  Placement = pos=(0,0,500) rot=(0,0,1;0rad)
  PredefinedType = 0
FEATURE [App::GeometryPython] BuildingPart002  label="Fundaciones"  # Arch/BIM 172 (typed FeaturePython)
  Area = 8300000
  Group = -> [BuildingPart005,BuildingPart006,BuildingPart007,BuildingPart008,Wall]
  Height = 0
  HeightPropagate = true
  IfcData = attributes={"GlobalId": {"name": "GlobalId", "type": "IfcGloballyUniqueId", "is_enum": false, "enum_values": []}, "Description": {"... (+484 chars omitted),+1 more (map truncated)
  IfcType = 172
  LevelOffset = 0
  PredefinedType = 0
FEATURE [App::GeometryPython] BuildingPart  label="Building"  # Arch/BIM 10 (typed FeaturePython)
  Area = 107900000
  BuildingType = 0
  CompositionType = 0
  ElevationOfRefHeight = 0
  ElevationOfTerrain = 0
  Group = -> [BuildingPart002,BuildingPart001,BuildingPart003,BuildingPart010,BuildingPart019,BuildingPart023,BuildingPart024]
  Height = 0
  HeightPropagate = true
  IfcData = attributes={"GlobalId": {"name": "GlobalId", "type": "IfcGloballyUniqueId", "is_enum": false, "enum_values": []}, "Description": {"... (+1010 chars omitted),+1 more (map truncated)
  IfcType = 10
  LevelOffset = 0
  LongName = Building
FEATURE [App::FeaturePython] Section005  label="SEC-001-PLANTA FUNDACIONES"  # WARN: FeaturePython — macro-defined, semantics opaque (R4)
  Clip = false
  OnlySolids = true
  Placement = pos=(8570,-15000,150) rot=(0,0,1;0rad)
  UseMaterialColorForFill = false
FEATURE [Part::Part2DObjectPython] Line013  # Draft 2D object (typed FeaturePython)
  Area = 0
  ChamferSize = 0
  Closed = false
  End = (16168.2,10722.3,-500)
  FilletRadius = 0
  Length = 15174.9
  MakeFace = true
  Placement = pos=(993.232,10722.3,-500) rot=(0,0,1;0rad)
  Points = (2) [(0,0,0),(15174.9,0,0)]
  Start = (993.232,10722.3,-500)
  Subdivisions = 0
FEATURE [TechDraw::DrawSVGTemplate] Template007
  EditableTexts = Cliente 1=UNIVERSO BIM,Comprobado por=UB,Dibujado por=LSG,Escala=1:50,Fecha=12/2020,Nombre plano 1=FUNDACIONES,Numero Proyecto=001,Numero plano=02,+2 more (map truncated)
  Height = 297
  Orientation = 1
  Width = 420
FEATURE [TechDraw::DrawSVGTemplate] Template008
  EditableTexts = Cliente 1=UNIVERSO BIM,Comprobado por=GORO,Dibujado por=GORO,Escala=-,Fecha=2021/01,Nombre plano 1=PORTADA,Numero Proyecto=21005,Numero plano=ES-001,+2 more (map truncated)
  Height = 297
  Orientation = 1
  Width = 420
FEATURE [TechDraw::DrawViewPart] View  label="VIEW-Vista Portada"
  Caption = VISTA DEL PROYECTO
  CoarseView = false
  Direction = (0.473,-0.767,0.435)
  Focus = 200
  HardHidden = false
  IsoCount = 0
  IsoHidden = false
  IsoVisible = false
  LockPosition = false
  Perspective = true
  Rotation = 0
  Scale = 0.007
  ScaleType = 0
  SeamHidden = false
  SeamVisible = true
  SmoothHidden = false
  SmoothVisible = true
  Source = -> [BuildingPart]
  X = 317.281
  XDirection = (0.844,0.536,0.027)
  Y = 166.952
FEATURE [TechDraw::DrawViewAnnotation] Annotation
  Font = Arial
  LineSpace = 80
  LockPosition = false
  MaxWidth = -1
  Rotation = 0
  ScaleType = 0
  Text = LISTA DE PLANOS
  TextSize = 5
  TextStyle = 0
  X = 60.7425
  Y = 271.395
FEATURE [TechDraw::DrawPage] Page008  label="ES-001-PORTADA"
  KeepUpdated = true
  NextBalloonIndex = 1
  ProjectionType = 0
  Template = -> Template008
  Views = -> [View,Annotation]
FEATURE [App::FeaturePython] dLabel001  # WARN: FeaturePython — macro-defined, semantics opaque (R4)
  CustomText = Label
  LabelType = 7
  Placement = pos=(2285.07,10563.2,-300) rot=(0,0,1;0rad)
  Points = (3) [(2285.07,10563.2,-300),(2435.66,10563.2,-300),(1668.37,10162.8,-300)]
  StraightDirection = 0
  StraightDistance = 150.591
  Target = -> Structure [Face5]
  TargetPoint = (1668.37,10162.8,-300)
  Text = B1
FEATURE [TechDraw::DrawSVGTemplate] Template
  EditableTexts = Cliente 1=UNIVERSO BIM,Comprobado por=GORO,Dibujado por=GORO,Escala=1:50,Fecha=2021/01,Nombre plano 1=ESTRUCTURA CIMIENTOS,Numero Proyecto=21005,+3 more (map truncated)
  Height = 297
  Orientation = 1
  Width = 420
FEATURE [TechDraw::DrawSVGTemplate] Template009
  EditableTexts = Cliente 1=LINEA 1,Cliente 2=LINEA 2,Comprobado por=Comp por,Dibujado por=Dibujado por,Escala=Escala,Fecha=Fecha,Nombre plano 1=LINEA 1,+6 more (map truncated)
  Height = 297
  Orientation = 1
  Width = 420
FEATURE [TechDraw::DrawPage] Page009
  KeepUpdated = true
  NextBalloonIndex = 1
  ProjectionType = 0
  Template = -> Template009
FEATURE [TechDraw::DrawSVGTemplate] Template010
  EditableTexts = Cliente 1=LINEA 1,Cliente 2=LINEA 2,Comprobado por=Comp por,Dibujado por=Dibujado por,Escala=Escala,Fecha=Fecha,Nombre plano 1=LINEA 1,+6 more (map truncated)
  Height = 297
  Orientation = 1
  Width = 420
FEATURE [TechDraw::DrawViewPart] View003
  CoarseView = false
  Direction = (0,-1,0)
  Focus = 100
  HardHidden = false
  IsoCount = 0
  IsoHidden = false
  IsoVisible = false
  LockPosition = false
  Perspective = false
  Rotation = 0
  Scale = 0.02
  ScaleType = 0
  SeamHidden = false
  SeamVisible = true
  SmoothHidden = false
  SmoothVisible = true
  Source = -> [BuildingPart]
  X = -198.186
  XDirection = (1,0,0)
  Y = 135.252
FEATURE [TechDraw::DrawViewSection] SectionView001  label="Section  - "
  BaseView = -> View003
  CoarseView = false
  CutSurfaceDisplay = 1
  Direction = (0,0,-1)
  FileGeomPattern = <path>
  FileHatchPattern = <path>
  Focus = 100
  FuseBeforeCut = false
  HardHidden = false
  HatchScale = 1
  IsoCount = 0
  IsoHidden = false
  IsoVisible = false
  LockPosition = false
  NameGeomPattern = Diamond
  Perspective = false
  Rotation = 0
  Scale = 0.02
  ScaleType = 0
  SeamHidden = false
  SeamVisible = true
  SectionDirection = 2
  SectionNormal = (0,0,-1)
  SectionOrigin = (8570,5000,1500)
  SmoothHidden = false
  SmoothVisible = true
  Source = -> [BuildingPart001,BuildingPart003]
  X = 214.381
  XDirection = (1,0,0)
  Y = 169.708
FEATURE [TechDraw::DrawPage] Page010  label="03b-EST s/PB"
  KeepUpdated = true
  NextBalloonIndex = 1
  ProjectionType = 0
  Template = -> Template010
  Views = -> [View003,SectionView001]
FEATURE [Sketcher::SketchObject] Sketch001
  Placement = pos=(1141.19,10409,0) rot=(0,0,1;0rad)
  sketch-geometry (6):
    g0: LineSegment StartX=0 StartY=0 StartZ=0 EndX=5 EndY=0 EndZ=0
    g1: LineSegment StartX=0 StartY=1 StartZ=0 EndX=5 EndY=1 EndZ=0
    g2: LineSegment StartX=0 StartY=2 StartZ=0 EndX=5 EndY=2 EndZ=0
    g3: LineSegment StartX=0 StartY=3 StartZ=0 EndX=5 EndY=3 EndZ=0
    g4: LineSegment StartX=0 StartY=4 StartZ=0 EndX=5 EndY=4 EndZ=0
    g5: LineSegment StartX=0 StartY=5 StartZ=0 EndX=7 EndY=5 EndZ=0
  constraints (23):
    c: Coincident(g0,g-1)
    c: PointOnObject(g0,g-1)
    c: PointOnObject(g1,g-2)
    c: Horizontal(g1)
    c: PointOnObject(g2,g-2)
    c: Horizontal(g2)
    c: PointOnObject(g3,g-2)
    c: Horizontal(g3)
    c: PointOnObject(g4,g-2)
    c: Horizontal(g4)
    c: PointOnObject(g5,g-2)
    c: Horizontal(g5)
    c: DistanceX(g0,g0) = 5
    c: DistanceY(g0,g1) = 1
    c: DistanceY(g1,g2) = 1
    c: DistanceY(g2,g3) = 1
    c: DistanceY(g3,g4) = 1
    c: DistanceY(g4,g5) = 1
    c: DistanceX(g1,g1) = 5
    c: DistanceX(g2,g2) = 5
    c: DistanceX(g3,g3) = 5
    c: DistanceX(g4,g4) = 5
    c: DistanceX(g5,g5) = 7
FEATURE [Part::Part2DObjectPython] Line014  # Draft 2D object (typed FeaturePython)
  Area = 0
  ChamferSize = 0
  Closed = false
  End = (0,5,0)
  FilletRadius = 0
  Length = 5
  MakeFace = true
  Points = (2) [(0,0,0),(0,5,0)]
  Start = (0,0,0)
  Subdivisions = 0
FEATURE [Part::Part2DObjectPython] Clone2D  label="Sketch001 (2D)"  # Draft 2D object (typed FeaturePython)
  Fuse = false
  Objects = -> [Sketch001]
  Placement = pos=(1141.19,10409,0) rot=(0,0,1;0rad)
  Scale = (10,10,1)
FEATURE [Part::Part2DObjectPython] Clone2D001  label="Sketch001 (2D) (2D)"  # Draft 2D object (typed FeaturePython)
  Fuse = false
  Objects = -> [Clone2D]
  Placement = pos=(1580,9550,-500) rot=(0,0,1;0rad)
  Scale = (10,10,1)
FEATURE [Part::Part2DObjectPython] Clone2D002  label="Sketch001 (2D) (2D)001"  # Draft 2D object (typed FeaturePython)
  Fuse = false
  Objects = -> [Clone2D]
  Placement = pos=(1141.96,10409.2,0) rot=(0,0,1;0rad)
  Scale = (10,10,1)
FEATURE [TechDraw::DrawViewAnnotation] Annotation001
  Font = Arial Narrow
  LineSpace = 80
  LockPosition = false
  MaxWidth = -1
  Rotation = 0
  ScaleType = 0
  Text = AAb
  TextSize = 3
  TextStyle = 0
  X = 115.231
  Y = 272.337
FEATURE [App::FeaturePython] dLabel002  # WARN: FeaturePython — macro-defined, semantics opaque (R4)
  CustomText = Label
  LabelType = 7
  Placement = pos=(1411.26,10408.9,-300) rot=(0,0,1;0rad)
  Points = (3) [(1411.26,10408.9,-300),(1561.85,10408.9,-300),(1668.37,10162.8,-300)]
  StraightDirection = 0
  StraightDistance = 150.591
  Target = -> Structure [Face5]
  TargetPoint = (1668.37,10162.8,-300)
  Text = B1
FEATURE [App::FeaturePython] Dimension011  # Draft dimension (typed FeaturePython)
  Diameter = false
  Dimline = (2171.36,10354.8,0)
  Direction = (0,0,0)
  Distance = 700
  End = (2280,10250,-500)
  Normal = (0,0,1)
  Start = (1580,10250,-500)
FEATURE [App::GeometryPython] BuildingPart028  label="02-FUND-2D"  # Arch/BIM 172 (typed FeaturePython)
  Area = 0
  Group = -> [Line013,dLabel001,Sketch001,Line014,Clone2D,Clone2D001,Clone2D002,Dimension011]
  Height = 0
  HeightPropagate = true
  IfcData = attributes={"GlobalId": {"name": "GlobalId", "type": "IfcGloballyUniqueId", "is_enum": false, "enum_values": []}, "Description": {"... (+484 chars omitted),+1 more (map truncated)
  IfcType = 172
  LevelOffset = 0
  Placement = pos=(0,0,-300) rot=(0,0,1;0rad)
  PredefinedType = 0
FEATURE [App::FeaturePython] Section003  label="SEC-02a-Planta Fundaciones"  # WARN: FeaturePython — macro-defined, semantics opaque (R4)
  Clip = false
  Objects = -> [BuildingPart002,BuildingPart001,BuildingPart028,Axis004,Axis]
  OnlySolids = false
  Placement = pos=(0,0,-300) rot=(0,0,1;0rad)
  UseMaterialColorForFill = true
FEATURE [Part::Part2DObjectPython] Shape2DView001  label="DRW-01-Planta Fundaciones"  # Draft 2D object (typed FeaturePython)
  Base = -> Section003
  FuseArch = false
  HiddenLines = false
  InPlace = true
  Placement = pos=(0,-20000,0) rot=(0,0,1;0rad)
  Projection = (0,0,1)
  ProjectionMode = 0
  SegmentLength = 0.05
  Tessellation = false
  VisibleOnly = false
FEATURE [App::DocumentObjectGroup] Group006  label="02a-Planta Fundaciones"
  Group = -> [Section003,Shape2DView001,Section004,Shape2DView,Section005,BuildingPart028]
FEATURE [App::DocumentObjectGroup] Group005  label="Vistas"
  Group = -> [Group006]
FEATURE [TechDraw::DrawViewArch] ArchView004  label="ArchView-Planta Fundaciones"
  AllOn = true
  CutLineWidth = 0.4
  FillSpaces = false
  FontSize = 7
  JoinArch = false
  LineWidth = 0.2
  LockPosition = true
  RenderMode = 0
  Rotation = 0
  Scale = 0.02
  ScaleType = 2
  ShowFill = true
  ShowHidden = false
  Source = -> Section003
  Symbol = <blob: 43409 chars omitted>
  X = 215.785
  Y = 169.571
FEATURE [TechDraw::DrawPage] Page007  label="02-FUNDACIONES"
  KeepUpdated = true
  NextBalloonIndex = 1
  ProjectionType = 0
  Template = -> Template007
  Views = -> [ArchView004,Annotation001]
FEATURE [TechDraw::DrawViewPart] View002  label="FRONTAL GRAL"
  CoarseView = false
  Direction = (0,-1,0)
  Focus = 100
  HardHidden = false
  IsoCount = 0
  IsoHidden = false
  IsoVisible = false
  LockPosition = false
  Perspective = false
  Rotation = 0
  Scale = 0.02
  ScaleType = 0
  SeamHidden = false
  SeamVisible = true
  SmoothHidden = false
  SmoothVisible = true
  Source = -> [BuildingPart,BuildingPart028]
  X = -187.194
  XDirection = (1,0,0)
  Y = 25.233
FEATURE [TechDraw::DrawViewPart] View001  label="PLANTA GRAL"
  CoarseView = false
  Direction = (0,0,1)
  Focus = 100
  HardHidden = false
  IsoCount = 0
  IsoHidden = false
  IsoVisible = false
  LockPosition = false
  Perspective = false
  Rotation = 0
  Scale = 0.02
  ScaleType = 0
  SeamHidden = false
  SeamVisible = true
  SmoothHidden = false
  SmoothVisible = true
  Source = -> [BuildingPart]
  X = -189.3
  XDirection = (1,0,0)
  Y = 417.339
FEATURE [TechDraw::DrawViewSection] SectionView  label="FUND PLANTA"
  BaseView = -> View002
  Caption = PLANTA FUNDACIONES
  CoarseView = false
  CutSurfaceDisplay = 1
  Direction = (0,0,1)
  FileGeomPattern = <path>
  FileHatchPattern = <path>
  Focus = 100
  FuseBeforeCut = false
  HardHidden = false
  HatchScale = 1
  IsoCount = 0
  IsoHidden = false
  IsoVisible = false
  LockPosition = true
  NameGeomPattern = Diamond
  Perspective = false
  Rotation = 0
  Scale = 0.02
  ScaleType = 0
  SeamHidden = false
  SeamVisible = true
  SectionDirection = 3
  SectionNormal = (0,0,1)
  SectionOrigin = (8570,5000,-300)
  SmoothHidden = false
  SmoothVisible = true
  Source = -> [BuildingPart,BuildingPart028,Line013,Axis,Axis002]
  X = 222.873
  XDirection = (1,0,0)
  Y = 166.982
FEATURE [TechDraw::DrawViewDimension] Dimension008
  Arbitrary = false
  FormatSpec = %.2f
  Inverted = false
  LockPosition = false
  MeasureType = 1
  OverTolerance = 0
  References2D = -> [SectionView]
  Rotation = 0
  ScaleType = 0
  TheoreticalExact = false
  Type = 1
  UnderTolerance = 0
  X = 68.8
  Y = 112
FEATURE [TechDraw::DrawViewDimension] Dimension005
  Arbitrary = false
  FormatSpec = %.2f
  Inverted = false
  LockPosition = false
  MeasureType = 1
  OverTolerance = 0
  References2D = -> [SectionView]
  Rotation = 0
  ScaleType = 0
  TheoreticalExact = false
  Type = 1
  UnderTolerance = 0
  X = -19.7
  Y = 112
FEATURE [TechDraw::DrawViewDimension] Dimension007
  Arbitrary = false
  FormatSpec = %.2f
  Inverted = false
  LockPosition = false
  MeasureType = 1
  OverTolerance = 0
  References2D = -> [SectionView]
  Rotation = 0
  ScaleType = 0
  TheoreticalExact = false
  Type = 1
  UnderTolerance = 0
  X = 38.8
  Y = 112
FEATURE [TechDraw::DrawViewDimension] Dimension002
  Arbitrary = false
  FormatSpec = %.2f
  Inverted = false
  LockPosition = false
  MeasureType = 1
  OverTolerance = 0
  References2D = -> [SectionView]
  Rotation = 0
  ScaleType = 0
  TheoreticalExact = false
  Type = 1
  UnderTolerance = 0
  X = -132.8
  Y = 112
FEATURE [TechDraw::DrawViewDimension] Dimension004
  Arbitrary = false
  FormatSpec = %.2f
  Inverted = false
  LockPosition = false
  MeasureType = 1
  OverTolerance = 0
  References2D = -> [SectionView]
  Rotation = 0
  ScaleType = 0
  TheoreticalExact = false
  Type = 1
  UnderTolerance = 0
  X = -48.2
  Y = 112
FEATURE [TechDraw::DrawViewDimension] Dimension003
  Arbitrary = false
  FormatSpec = %.2f
  Inverted = false
  LockPosition = false
  MeasureType = 1
  OverTolerance = 0
  References2D = -> [SectionView]
  Rotation = 0
  ScaleType = 0
  TheoreticalExact = false
  Type = 1
  UnderTolerance = 0
  X = -90.346
  Y = 112
FEATURE [TechDraw::DrawViewDimension] Dimension006
  Arbitrary = false
  FormatSpec = %.2f
  Inverted = false
  LockPosition = false
  MeasureType = 1
  OverTolerance = 0
  References2D = -> [SectionView]
  Rotation = 0
  ScaleType = 0
  TheoreticalExact = false
  Type = 1
  UnderTolerance = 0
  X = 8.8
  Y = 112
FEATURE [TechDraw::DrawViewDimension] Dimension010
  Arbitrary = false
  FormatSpec = %.2f
  Inverted = false
  LockPosition = false
  MeasureType = 1
  OverTolerance = 0
  References2D = -> [SectionView]
  Rotation = 0
  ScaleType = 0
  TheoreticalExact = false
  Type = 1
  UnderTolerance = 0
  X = 132.8
  Y = 112
FEATURE [TechDraw::DrawViewDimension] Dimension009
  Arbitrary = false
  FormatSpec = %.2f
  Inverted = false
  LockPosition = false
  MeasureType = 1
  OverTolerance = 0
  References2D = -> [SectionView]
  Rotation = 0
  ScaleType = 0
  TheoreticalExact = false
  Type = 1
  UnderTolerance = 0
  X = 100.8
  Y = 112
FEATURE [TechDraw::DrawViewDimension] Dimension012
  Arbitrary = false
  FormatSpec = %.2f
  Inverted = false
  LockPosition = false
  MeasureType = 1
  OverTolerance = 0
  References2D = -> [SectionView]
  Rotation = 0
  ScaleType = 0
  TheoreticalExact = false
  Type = 2
  UnderTolerance = 0
  X = -150
  Y = 98.3065
FEATURE [TechDraw::DrawViewDimension] Dimension013
  Arbitrary = false
  FormatSpec = %.2f
  Inverted = false
  LockPosition = false
  MeasureType = 1
  OverTolerance = 0
  References2D = -> [SectionView]
  Rotation = 0
  ScaleType = 0
  TheoreticalExact = false
  Type = 2
  UnderTolerance = 0
  X = -150
  Y = 66.7297
FEATURE [TechDraw::DrawViewDimension] Dimension014
  Arbitrary = false
  FormatSpec = %.2f
  Inverted = false
  LockPosition = false
  MeasureType = 1
  OverTolerance = 0
  References2D = -> [SectionView]
  Rotation = 0
  ScaleType = 0
  TheoreticalExact = false
  Type = 2
  UnderTolerance = 0
  X = -150
  Y = 32.8
FEATURE [TechDraw::DrawViewDimension] Dimension015
  Arbitrary = false
  FormatSpec = %.2f
  Inverted = false
  LockPosition = false
  MeasureType = 1
  OverTolerance = 0
  References2D = -> [SectionView]
  Rotation = 0
  ScaleType = 0
  TheoreticalExact = false
  Type = 2
  UnderTolerance = 0
  X = -150
  Y = -0.1
FEATURE [TechDraw::DrawViewDimension] Dimension016
  Arbitrary = false
  FormatSpec = %.2f
  Inverted = false
  LockPosition = false
  MeasureType = 1
  OverTolerance = 0
  References2D = -> [SectionView]
  Rotation = 0
  ScaleType = 0
  TheoreticalExact = false
  Type = 2
  UnderTolerance = 0
  X = -150
  Y = -33
FEATURE [TechDraw::DrawViewDimension] Dimension017
  Arbitrary = false
  FormatSpec = %.2f
  Inverted = false
  LockPosition = false
  MeasureType = 1
  OverTolerance = 0
  References2D = -> [SectionView]
  Rotation = 0
  ScaleType = 0
  TheoreticalExact = false
  Type = 2
  UnderTolerance = 0
  X = -150
  Y = -65.5
FEATURE [TechDraw::DrawViewDimension] Dimension018
  Arbitrary = false
  FormatSpec = %.2f
  Inverted = false
  LockPosition = false
  MeasureType = 1
  OverTolerance = 0
  References2D = -> [SectionView]
  Rotation = 0
  ScaleType = 0
  TheoreticalExact = false
  Type = 2
  UnderTolerance = 0
  X = -150
  Y = -97.4094
FEATURE [TechDraw::DrawPage] Page  label="ES-002-ESTRUCTURA CIMIENTOS"
  KeepUpdated = true
  NextBalloonIndex = 1
  ProjectionType = 0
  Template = -> Template
  Views = -> [View001,View002,SectionView,Dimension002,Dimension003,Dimension004,Dimension005,Dimension006,Dimension007,Dimension008,Dimension009,Dimension010,Dimension012,Dimension013,Dimension014,Dimension015,Dimension016,Dimension017,Dimension018]
FEATURE [App::GeometryPython] BuildingPart029  label="PLANOS"  # Arch/BIM 172 (typed FeaturePython)
  Area = 0
  Group = -> [Page008,Page,Page010]
  Height = 0
  HeightPropagate = true
  IfcData = attributes={"GlobalId": {"name": "GlobalId", "type": "IfcGloballyUniqueId", "is_enum": false, "enum_values": []}, "Description": {"... (+484 chars omitted),+1 more (map truncated)
  IfcType = 172
  LevelOffset = 0
  Placement = pos=(0,0,-300) rot=(0,0,1;0rad)
  PredefinedType = 0
FEATURE [App::FeaturePython] Dimension019  # Draft dimension (typed FeaturePython)
  Diameter = false
  Dimline = (1298.38,-16027.7,-300)
  Direction = (0,0,0)
  Distance = 700
  End = (1580,-17000,0)
  LinkedGeometry = -> [Shape2DView001]
  Normal = (0,0,1)
  Start = (1580,-16300,0)
  Support = -> Shape2DView001
FEATURE [App::FeaturePython] dLabel004  # WARN: FeaturePython — macro-defined, semantics opaque (R4)
  CustomText = Label
  LabelType = 2
  Placement = pos=(919.079,10314.3,-300) rot=(0,0,1;0rad)
  Points = (3) [(919.079,10314.3,-300),(1432.36,10314.3,-300),(1580,10250,-500)]
  StraightDirection = 0
  StraightDistance = 513.285
  Target = -> Structure [Face5]
  TargetPoint = (1580,10250,-500)
  Text = CAB PIL 1
FEATURE [App::FeaturePython] Dimension020  # Draft dimension (typed FeaturePython)
  Diameter = false
  Dimline = (6360.74,-8756.54,-300)
  Direction = (0,0,0)
  Distance = 700
  End = (6510,-9750,0)
  Normal = (0,0,1)
  Start = (5810,-9750,0)
FEATURE [App::FeaturePython] Dimension  # Draft dimension (typed FeaturePython)
  Diameter = false
  Dimline = (2181.86,-10398.7,-300)
  Direction = (0,0,0)
  Distance = 700
  End = (2280,-10450,0)
  Normal = (0,0,1)
  Start = (1580,-10450,0)
FEATURE [App::FeaturePython] Dimension021  # Draft dimension (typed FeaturePython)
  Diameter = false
  Dimline = (1481.07,-10263.9,-300)
  Direction = (0,0,0)
  Distance = 100
  End = (1580,-10250,0)
  Normal = (0,0,1)
  Start = (1580,-10350,0)
note: 4 file-system paths scrubbed to <path> (originals preserved in the JSON sidecar)
